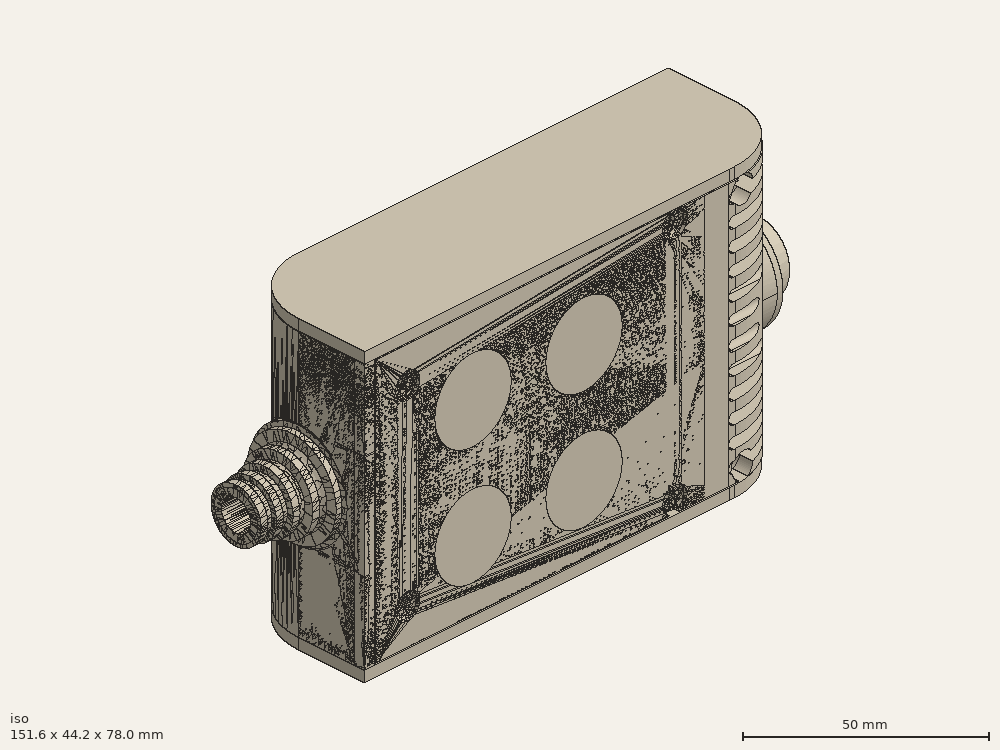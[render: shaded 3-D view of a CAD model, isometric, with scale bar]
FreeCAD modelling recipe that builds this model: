
FCSTD DOCUMENT  (FreeCAD 0.19R0.19.2)
Label: enclosure_178FCStd
License: All rights reserved
LicenseURL: http://en.wikipedia.org/wiki/All_rights_reserved
objects: Part::Revolution×152, Part::MultiFuse×146, Part::Feature×146, Sketcher::SketchObject×84, Part::Cut×70, Part::Cylinder×70, Part::Extrusion×67, Part::Fillet×58, Part::Box×36, App::MeasureDistance×4, PartDesign::Body×2, Image::ImagePlane×1
note: 831 computed .brp shape members not serialized (recipe doc carries the construction recipe); baked Part::Feature solids carry a one-line shape summary decoded from their .brp

FEATURE [Sketcher::SketchObject] Sketch  label="topSketch"
  FullyConstrained = true
  sketch-geometry (20):
    g0: LineSegment StartX=5.21097e-06 StartY=3 StartZ=0 EndX=5.21097e-06 EndY=19 EndZ=0
    g1: ArcOfCircle CenterX=19 CenterY=19 CenterZ=0 NormalX=0 NormalY=0 NormalZ=1 AngleXU=0 Radius=19 StartAngle=1.5708 EndAngle=3.14159
    g2: ArcOfCircle CenterX=19 CenterY=19 CenterZ=0 NormalX=0 NormalY=0 NormalZ=1 AngleXU=0 Radius=16 StartAngle=1.5708 EndAngle=3.14159
    g3: LineSegment StartX=114 StartY=35 StartZ=0 EndX=19 EndY=35 EndZ=0
    g4: LineSegment StartX=5.21097e-06 StartY=3 StartZ=0 EndX=5.21097e-06 EndY=0 EndZ=0
    g5: LineSegment StartX=3 StartY=0 StartZ=0 EndX=5.21097e-06 EndY=0 EndZ=0
    g6: LineSegment StartX=3 StartY=19 StartZ=0 EndX=3 EndY=0 EndZ=0
    g7: LineSegment StartX=19 StartY=38 StartZ=0 EndX=124 EndY=38 EndZ=0
    g8: Circle CenterX=119 CenterY=35 CenterZ=0 NormalX=0 NormalY=0 NormalZ=1 AngleXU=0 Radius=1
    g9: Circle CenterX=121 CenterY=35 CenterZ=0 NormalX=0 NormalY=0 NormalZ=1 AngleXU=0 Radius=1
    g10: Circle CenterX=121 CenterY=33 CenterZ=0 NormalX=0 NormalY=0 NormalZ=1 AngleXU=0 Radius=1
    g11: BSplineCurve PolesCount=3 KnotsCount=2 Degree=2 IsPeriodic=0
    g12: GeomPoint X=119 Y=35 Z=0
    g13: GeomPoint X=121 Y=33 Z=0
    g14: LineSegment StartX=119 StartY=35 StartZ=0 EndX=114 EndY=35 EndZ=0
    g15: ArcOfCircle CenterX=105 CenterY=19 CenterZ=0 NormalX=0 NormalY=0 NormalZ=1 AngleXU=0 Radius=19 StartAngle=5.7297 EndAngle=6.28319
    g16: ArcOfCircle CenterX=105 CenterY=19 CenterZ=0 NormalX=0 NormalY=0 NormalZ=1 AngleXU=0 Radius=16 StartAngle=5.60905 EndAngle=6.28319
    g17: LineSegment StartX=121 StartY=33 StartZ=0 EndX=121 EndY=19 EndZ=0
    g18: LineSegment StartX=124 StartY=38 StartZ=0 EndX=124 EndY=19 EndZ=0
    g19: LineSegment StartX=117.5 StartY=9.01251 StartZ=0 EndX=121.163 EndY=9.0125 EndZ=0
  constraints (46):
    c: Vertical(g0)
    c: Block(g0)
    c: Coincident(g1,g0)
    c: Block(g1)
    c: Coincident(g2,g1)
    c: Block(g2)
    c: Coincident(g3,g2)
    c: Horizontal(g3)
    c: Tangent(g3,g2)
    c: Coincident(g4,g0)
    c: Distance(g4) = 3
    c: Vertical(g4)
    c: Coincident(g5,g4)
    c: Horizontal(g5)
    c: Coincident(g6,g2)
    c: Coincident(g6,g5)
    c: Vertical(g6)
    c: Horizontal(g7)
    c: Distance(g7) = 105
    c: Coincident(g7,g1)
    c: Block(g3)
    c: Weight(g8) = 1
    c: Equal(g8,g9)
    c: Equal(g8,g10)
    c: InternalAlignment(g8,g11)
    c: InternalAlignment(g9,g11)
    c: InternalAlignment(g10,g11)
    c: InternalAlignment(g12,g11)
    c: InternalAlignment(g13,g11)
    c: Block(g11)
    c: Coincident(g14,g11)
    c: Coincident(g14,g3)
    c: Horizontal(g14)
    c: Block(g15)
    c: Coincident(g16,g15)
    c: Block(g16)
    c: Coincident(g17,g11)
    c: Coincident(g17,g16)
    c: Vertical(g17)
    c: Distance(g17) = 14
    c: Coincident(g18,g7)
    c: Coincident(g18,g15)
    c: Vertical(g18)
    c: Distance(g18) = 19
    c: Coincident(g19,g16)
    c: Coincident(g19,g15)
FEATURE [Sketcher::SketchObject] Sketch001  label="bottomSketch"
  FullyConstrained = true
  sketch-geometry (32):
    g0: LineSegment StartX=3.3 StartY=-6.03275e-07 StartZ=0 EndX=98 EndY=-6.03275e-07 EndZ=0
    g1: ArcOfCircle CenterX=98 CenterY=19 CenterZ=0 NormalX=0 NormalY=0 NormalZ=1 AngleXU=0 Radius=19 StartAngle=4.71239 EndAngle=5.71103
    g2: LineSegment StartX=6.3 StartY=8 StartZ=0 EndX=3.3 EndY=8 EndZ=0
    g3: LineSegment StartX=3.3 StartY=8 StartZ=0 EndX=3.3 EndY=-6.03275e-07 EndZ=0
    g4: ArcOfCircle CenterX=8.3 CenterY=5 CenterZ=0 NormalX=0 NormalY=0 NormalZ=1 AngleXU=0 Radius=2 StartAngle=3.14159 EndAngle=4.71239
    g5: LineSegment StartX=6.3 StartY=8 StartZ=0 EndX=6.3 EndY=5 EndZ=0
    g6: ArcOfCircle CenterX=98 CenterY=19 CenterZ=0 NormalX=0 NormalY=0 NormalZ=1 AngleXU=0 Radius=12.7 StartAngle=4.71239 EndAngle=6.28319
    g7: LineSegment StartX=94.7 StartY=3 StartZ=0 EndX=8.3 EndY=3 EndZ=0
    g8-g12: Circle x5 (B-spline internal-alignment scaffolding for g13; pole/knot coordinates omitted)
    g13: BSplineCurve PolesCount=5 KnotsCount=3 Degree=3 IsPeriodic=0
    g14: GeomPoint X=98 Y=6.3 Z=0
    g15: GeomPoint X=96.3938 Y=4.71946 Z=0
    g16: GeomPoint X=94.7 Y=3 Z=0
    g17-g23: Circle x7 (B-spline internal-alignment scaffolding for g24; pole/knot coordinates omitted)
    g24: BSplineCurve PolesCount=7 KnotsCount=5 Degree=3 IsPeriodic=0
    g25-g29: GeomPoint x5 (B-spline internal-alignment scaffolding for g24; pole/knot coordinates omitted)
    g30: ArcOfCircle CenterX=98 CenterY=19 CenterZ=0 NormalX=0 NormalY=0 NormalZ=1 AngleXU=0 Radius=15.7 StartAngle=5.81226 EndAngle=6.28319
    g31: LineSegment StartX=110.7 StartY=19 StartZ=0 EndX=113.7 EndY=19 EndZ=0
  constraints (41):
    c: Horizontal(g0)
    c: Coincident(g1,g0)
    c: Block(g1)
    c: Horizontal(g2)
    c: Distance(g2) = 3
    c: Coincident(g3,g2)
    c: Vertical(g3)
    c: Coincident(g3,g0)
    c: Block(g4)
    c: Block(g2)
    c: Coincident(g5,g2)
    c: Coincident(g5,g4)
    c: Vertical(g5)
    c: Coincident(g6,g1)
    c: Block(g6)
    c: Coincident(g7,g4)
    c: Horizontal(g7)
    c: Block(g0)
    c: Block(g7)
    c: Block(g3)
    c: Coincident(g13,g6)
    c: Weight(g8) = 1
    c: Equal(g8, g9-g12) x4
    c: Coincident(g13,g7)
    c: InternalAlignment(g8-g12 -> g13) x5
    c: InternalAlignment(g14,g13)
    c: InternalAlignment(g15,g13)
    c: InternalAlignment(g16,g13)
    c: Block(g13)
    c: Weight(g17) = 1
    c: Equal(g17, g18-g23) x6
    c: Coincident(g24,g1)
    c: InternalAlignment(g17-g23 -> g24) x7
    c: InternalAlignment(g25-g29 -> g24) x5
    c: Block(g24)
    c: Coincident(g30,g24)
    c: Coincident(g31,g6)
    c: Coincident(g31,g30)
    c: Horizontal(g31)
    c: Block(g31)
    c: Block(g30)
FEATURE [Part::Extrusion] Extrude  label="top"
  Base = -> Sketch
  Dir = (0,0,1)
  DirMode = 2
  FaceMakerClass = Part::FaceMakerBullseye
  LengthFwd = 72
  LengthRev = 0
  Solid = true
  Symmetric = false
FEATURE [Part::Extrusion] Extrude001  label="bottom"
  Base = -> Sketch001
  Dir = (0,0,1)
  DirMode = 2
  FaceMakerClass = Part::FaceMakerBullseye
  LengthFwd = 71.4
  LengthRev = 0
  Placement = pos=(0,0,0.3) rot=(0,0,1;0rad)
  Solid = true
  Symmetric = false
FEATURE [Sketcher::SketchObject] Sketch002  label="topSketch001"
  FullyConstrained = true
  sketch-geometry (8):
    g0: ArcOfCircle CenterX=19 CenterY=19.0975 CenterZ=0 NormalX=0 NormalY=0 NormalZ=1 AngleXU=0 Radius=18.9025 StartAngle=1.5708 EndAngle=3.14674
    g1: LineSegment StartX=0.0977805 StartY=19.0003 StartZ=0 EndX=0.0977805 EndY=0.000251602 EndZ=0
    g2: LineSegment StartX=19 StartY=38 StartZ=0 EndX=124 EndY=38 EndZ=0
    g3: LineSegment StartX=0.0977805 StartY=0.000251602 StartZ=0 EndX=105.098 EndY=0.000251602 EndZ=0
    g4: LineSegment StartX=124 StartY=38 StartZ=0 EndX=125.616 EndY=38 EndZ=0
    g5: LineSegment StartX=105.098 StartY=0.000251602 StartZ=0 EndX=106.713 EndY=0.000251602 EndZ=0
    g6: ArcOfCircle CenterX=106.616 CenterY=19 CenterZ=0 NormalX=0 NormalY=0 NormalZ=1 AngleXU=0 Radius=19 StartAngle=4.71754 EndAngle=6.28319
    g7: LineSegment StartX=125.616 StartY=38 StartZ=0 EndX=125.616 EndY=19 EndZ=0
  constraints (21):
    c: Block(g0)
    c: Coincident(g1,g0)
    c: Vertical(g1)
    c: Horizontal(g2)
    c: Distance(g2) = 105
    c: Coincident(g2,g0)
    c: Distance(g1) = 19
    c: Coincident(g3,g1)
    c: Horizontal(g3)
    c: Distance(g3) = 105
    c: Coincident(g4,g2)
    c: Horizontal(g4)
    c: Distance(g4) = 1.61553
    c: Horizontal(g5)
    c: Equal(g4,g5) = 1.61553
    c: Coincident(g5,g3)
    c: Block(g6)
    c: Coincident(g6,g5)
    c: Coincident(g7,g4)
    c: Coincident(g7,g6)
    c: Vertical(g7)
FEATURE [Part::Extrusion] Extrude002  label="sideA"
  Base = -> Sketch002
  Dir = (0,0,1)
  DirMode = 2
  FaceMakerClass = Part::FaceMakerBullseye
  LengthFwd = 3
  LengthRev = 0
  Placement = pos=(0,0,-3) rot=(0,0,1;0rad)
  Solid = true
  Symmetric = false
FEATURE [Sketcher::SketchObject] Sketch003  label="topSketch002"
  FullyConstrained = true
  sketch-geometry (6):
    g0: LineSegment StartX=19 StartY=38 StartZ=0 EndX=117 EndY=38 EndZ=0
    g1: ArcOfCircle CenterX=19 CenterY=19 CenterZ=0 NormalX=0 NormalY=0 NormalZ=1 AngleXU=0 Radius=19 StartAngle=1.5708 EndAngle=3.14159
    g2: LineSegment StartX=117 StartY=38 StartZ=0 EndX=117 EndY=19 EndZ=0
    g3: LineSegment StartX=98 StartY=1.0161e-12 StartZ=0 EndX=5.22862e-06 EndY=1.0161e-12 EndZ=0
    g4: LineSegment StartX=5.22862e-06 StartY=19 StartZ=0 EndX=5.22862e-06 EndY=1.0161e-12 EndZ=0
    g5: ArcOfCircle CenterX=98 CenterY=19 CenterZ=0 NormalX=0 NormalY=0 NormalZ=1 AngleXU=0 Radius=19 StartAngle=4.71239 EndAngle=6.28319
  constraints (16):
    c: Horizontal(g0)
    c: Distance(g0) = 98
    c: Coincident(g1,g0)
    c: Block(g1)
    c: Coincident(g2,g0)
    c: Vertical(g2)
    c: Distance(g2) = 19
    c: Horizontal(g3)
    c: Coincident(g4,g1)
    c: Vertical(g4)
    c: Coincident(g3,g4)
    c: Block(g3)
    c: Coincident(g5,g2)
    c: Coincident(g5,g3)
    c: Block(g0)
    c: Block(g5)
FEATURE [Sketcher::SketchObject] Sketch004
  FullyConstrained = true
  MapMode = 3
  Placement = pos=(0,0,0) rot=(1,0,0;1.5708rad)
  Support = -> [Extrude]
  sketch-geometry (8):
    g0: Circle CenterX=80.351 CenterY=-67.6202 CenterZ=0 NormalX=0 NormalY=0 NormalZ=1 AngleXU=0 Radius=2
    g1: Circle CenterX=80.351 CenterY=-67.6202 CenterZ=0 NormalX=0 NormalY=0 NormalZ=1 AngleXU=0 Radius=3
    g2: Circle CenterX=80.351 CenterY=-4.92017 CenterZ=0 NormalX=0 NormalY=0 NormalZ=1 AngleXU=0 Radius=2
    g3: Circle CenterX=80.351 CenterY=-4.92017 CenterZ=0 NormalX=0 NormalY=0 NormalZ=1 AngleXU=0 Radius=3
    g4: Circle CenterX=23.851 CenterY=-4.92017 CenterZ=0 NormalX=0 NormalY=0 NormalZ=1 AngleXU=0 Radius=2
    g5: Circle CenterX=23.851 CenterY=-4.92017 CenterZ=0 NormalX=0 NormalY=0 NormalZ=1 AngleXU=0 Radius=3
    g6: Circle CenterX=23.851 CenterY=-67.6202 CenterZ=0 NormalX=0 NormalY=0 NormalZ=1 AngleXU=0 Radius=2
    g7: Circle CenterX=23.851 CenterY=-67.6202 CenterZ=0 NormalX=0 NormalY=0 NormalZ=1 AngleXU=0 Radius=3
  constraints (8):
    c: Block(g3)
    c: Block(g2)
    c: Block(g1)
    c: Block(g0)
    c: Block(g6)
    c: Block(g7)
    c: Block(g4)
    c: Block(g5)
FEATURE [Part::Extrusion] Extrude004
  Base = -> Sketch004
  Dir = (0,-1,2e-16)
  DirMode = 2
  FaceMakerClass = Part::FaceMakerBullseye
  LengthFwd = 6
  LengthRev = 0
  Placement = pos=(0,9,0) rot=(0,0,1;0rad)
  Solid = true
  Symmetric = false
FEATURE [Sketcher::SketchObject] Sketch005
  FullyConstrained = true
  MapMode = 3
  Placement = pos=(0,0,0) rot=(1,0,0;1.5708rad)
  Support = -> [Extrude]
  sketch-geometry (8):
    g0: Circle CenterX=80.351 CenterY=-67.6202 CenterZ=0 NormalX=0 NormalY=0 NormalZ=1 AngleXU=0 Radius=3
    g1: Circle CenterX=80.351 CenterY=-4.92017 CenterZ=0 NormalX=0 NormalY=0 NormalZ=1 AngleXU=0 Radius=3
    g2: Circle CenterX=23.851 CenterY=-4.92017 CenterZ=0 NormalX=0 NormalY=0 NormalZ=1 AngleXU=0 Radius=3
    g3: Circle CenterX=23.851 CenterY=-67.6202 CenterZ=0 NormalX=0 NormalY=0 NormalZ=1 AngleXU=0 Radius=3
    g4: Circle CenterX=23.851 CenterY=-67.6202 CenterZ=0 NormalX=0 NormalY=0 NormalZ=1 AngleXU=0 Radius=5
    g5: Circle CenterX=80.351 CenterY=-67.6202 CenterZ=0 NormalX=0 NormalY=0 NormalZ=1 AngleXU=0 Radius=5
    g6: Circle CenterX=23.851 CenterY=-4.92017 CenterZ=0 NormalX=0 NormalY=0 NormalZ=1 AngleXU=0 Radius=5
    g7: Circle CenterX=80.351 CenterY=-4.92017 CenterZ=0 NormalX=0 NormalY=0 NormalZ=1 AngleXU=0 Radius=5
  constraints (8):
    c: Block(g1)
    c: Block(g0)
    c: Block(g3)
    c: Block(g2)
    c: Block(g5)
    c: Block(g4)
    c: Block(g6)
    c: Block(g7)
FEATURE [Part::Extrusion] Extrude005
  Base = -> Sketch005
  Dir = (0,-1,2e-16)
  DirMode = 2
  FaceMakerClass = Part::FaceMakerBullseye
  LengthFwd = 2
  LengthRev = 0
  Solid = true
  Symmetric = false
FEATURE [Sketcher::SketchObject] Sketch006
  FullyConstrained = true
  MapMode = 3
  Placement = pos=(0,0,0) rot=(1,0,0;1.5708rad)
  sketch-geometry (8):
    g0: Circle CenterX=80.351 CenterY=-67.6202 CenterZ=0 NormalX=0 NormalY=0 NormalZ=1 AngleXU=0 Radius=3
    g1: Circle CenterX=80.351 CenterY=-4.92017 CenterZ=0 NormalX=0 NormalY=0 NormalZ=1 AngleXU=0 Radius=3
    g2: Circle CenterX=23.851 CenterY=-4.92017 CenterZ=0 NormalX=0 NormalY=0 NormalZ=1 AngleXU=0 Radius=3
    g3: Circle CenterX=23.851 CenterY=-67.6202 CenterZ=0 NormalX=0 NormalY=0 NormalZ=1 AngleXU=0 Radius=3
    g4: Circle CenterX=23.851 CenterY=-67.6202 CenterZ=0 NormalX=0 NormalY=0 NormalZ=1 AngleXU=0 Radius=5
    g5: Circle CenterX=80.351 CenterY=-67.6202 CenterZ=0 NormalX=0 NormalY=0 NormalZ=1 AngleXU=0 Radius=5
    g6: Circle CenterX=23.851 CenterY=-4.92017 CenterZ=0 NormalX=0 NormalY=0 NormalZ=1 AngleXU=0 Radius=5
    g7: Circle CenterX=80.351 CenterY=-4.92017 CenterZ=0 NormalX=0 NormalY=0 NormalZ=1 AngleXU=0 Radius=5
  constraints (8):
    c: Block(g1)
    c: Block(g0)
    c: Block(g3)
    c: Block(g2)
    c: Block(g5)
    c: Block(g4)
    c: Block(g6)
    c: Block(g7)
FEATURE [Part::Extrusion] Extrude007
  Base = -> Sketch006
  Dir = (0,-1,2e-16)
  DirMode = 2
  FaceMakerClass = Part::FaceMakerBullseye
  LengthFwd = 2
  LengthRev = 0
  Solid = true
  Symmetric = false
FEATURE [Part::Fillet] Fillet
  Base = -> Extrude007
  Edges = 4 edges r=1.99: [Edge6,Edge12,Edge18,Edge24]
FEATURE [Part::Cut] Cut
  Base = -> Extrude005
  Placement = pos=(0,5,0) rot=(0,0,1;0rad)
  Tool = -> Fillet
FEATURE [Part::MultiFuse] Fusion  label="pCBScrews"
  Placement = pos=(-2.5,0,72.3) rot=(0,0,1;0rad)
  Shapes = -> [Extrude004,Cut]
FEATURE [App::MeasureDistance] Distance  label="Distance: 0.69 mm"
  Distance = 0.685967
  P1 = (24.0138,2.9647,0.3)
  P2 = (23.8901,3,-0.373787)
FEATURE [App::MeasureDistance] Distance001  label="Distance: 0.53 mm"
  Distance = 0.533607
  P1 = (80.2939,3,72.2334)
  P2 = (80.281,2.99661,71.7)
FEATURE [Part::Fillet] Fillet001
  Base = -> Extrude001
  Edges = 1 edges r=2.4: [Edge17]
FEATURE [Part::Fillet] Fillet002  label="bottom001"
  Base = -> Fillet001
  Edges = 1 edges r=2.4: [Edge36]
FEATURE [Part::Fillet] Fillet003  label="top001"
  Base = -> Extrude
  Edges = 1 edges r=2: [Edge1]
FEATURE [Sketcher::SketchObject] Sketch007
  FullyConstrained = true
  sketch-geometry (16):
    g0: LineSegment StartX=4 StartY=0 StartZ=0 EndX=4 EndY=2.4 EndZ=0
    g1: LineSegment StartX=4 StartY=2.4 StartZ=0 EndX=7 EndY=2.4 EndZ=0
    g2: LineSegment StartX=4 StartY=0 StartZ=0 EndX=5.7 EndY=0 EndZ=0
    g3: LineSegment StartX=5.7 StartY=0 StartZ=0 EndX=5.7 EndY=-5.6 EndZ=0
    g4-g8: Circle x5 (B-spline internal-alignment scaffolding for g9; pole/knot coordinates omitted)
    g9: BSplineCurve PolesCount=5 KnotsCount=3 Degree=3 IsPeriodic=0
    g10: GeomPoint X=7 Y=2.4 Z=0
    g11: GeomPoint X=10.4582 Y=-1.55472 Z=0
    g12: GeomPoint X=14 Y=-5.6 Z=0
    g13: LineSegment StartX=14 StartY=-5.6 StartZ=0 EndX=14 EndY=-14.1 EndZ=0
    g14: LineSegment StartX=14 StartY=-14.1 StartZ=0 EndX=6.5 EndY=-14.1 EndZ=0
    g15: LineSegment StartX=5.7 StartY=-5.6 StartZ=0 EndX=6.5 EndY=-14.1 EndZ=0
  constraints (28):
    c: Distance(g0) = 2.4
    c: Vertical(g0)
    c: Block(g0)
    c: Coincident(g1,g0)
    c: Horizontal(g1)
    c: Distance(g1) = 3
    c: Coincident(g2,g0)
    c: Horizontal(g2)
    c: Distance(g2) = 1.7
    c: Coincident(g3,g2)
    c: Vertical(g3)
    c: Distance(g3) = 5.6
    c: Coincident(g9,g1)
    c: Weight(g4) = 1
    c: Equal(g4, g5-g8) x4
    c: InternalAlignment(g4-g8 -> g9) x5
    c: InternalAlignment(g10,g9)
    c: InternalAlignment(g11,g9)
    c: InternalAlignment(g12,g9)
    c: Block(g9)
    c: Coincident(g13,g9)
    c: Vertical(g13)
    c: Distance(g13) = 8.5
    c: Coincident(g14,g13)
    c: Horizontal(g14)
    c: Distance(g14) = 7.5
    c: Coincident(g15,g3)
    c: Coincident(g15,g14)
FEATURE [Part::Feature] Face
  shape: bbox 10 x 16.5 x 2e-07 mm, 1 faces, 0 solids (baked)
FEATURE [Part::Revolution] Revolve  label="plugHousing"
  Angle = 360
  Axis = (0,1,0)
  Base = (0,0,0)
  FaceMakerClass = Part::FaceMakerBullseye
  Placement = pos=(0,0,36.15) rot=(0,0,1;0rad)
  Solid = false
  Source = -> Face
  Symmetric = false
FEATURE [Part::Feature] Face001
  shape: bbox 10 x 16.5 x 2e-07 mm, 1 faces, 0 solids (baked)
FEATURE [Part::Revolution] Revolve001  label="plugHousing001"
  Angle = 360
  Axis = (0,1,0)
  Base = (0,0,0)
  FaceMakerClass = Part::FaceMakerBullseye
  Placement = pos=(0,0,36.15) rot=(0,0,1;0rad)
  Solid = false
  Source = -> Face001
  Symmetric = false
FEATURE [Part::MultiFuse] Fusion001  label="plugHousing002"
  Placement = pos=(0,0,0) rot=(0,0,1;1.5708rad)
  Shapes = -> [Revolve001,Revolve]
FEATURE [Part::Feature] Face002
  shape: bbox 10 x 16.5 x 2e-07 mm, 1 faces, 0 solids (baked)
FEATURE [Part::Revolution] Revolve003  label="plugHousing005"
  Angle = 360
  Axis = (0,1,0)
  Base = (0,0,0)
  FaceMakerClass = Part::FaceMakerBullseye
  Placement = pos=(0,0,36.15) rot=(0,0,1;0rad)
  Solid = false
  Source = -> Face002
  Symmetric = false
FEATURE [Part::Feature] Face003
  shape: bbox 10 x 16.5 x 2e-07 mm, 1 faces, 0 solids (baked)
FEATURE [Part::Revolution] Revolve002  label="plugHousing003"
  Angle = 360
  Axis = (0,1,0)
  Base = (0,0,0)
  FaceMakerClass = Part::FaceMakerBullseye
  Placement = pos=(0,0,36.15) rot=(0,0,1;0rad)
  Solid = false
  Source = -> Face003
  Symmetric = false
FEATURE [Part::MultiFuse] Fusion002  label="plugHousing004"
  Placement = pos=(0,0,0) rot=(0,0,1;1.5708rad)
  Shapes = -> [Revolve002,Revolve003]
FEATURE [Part::MultiFuse] Fusion003  label="plugHousing006"
  Placement = pos=(0,19,0) rot=(0,0,1;3.14159rad)
  Shapes = -> [Fusion002,Fusion001]
FEATURE [Part::Feature] Face004
  shape: bbox 10 x 16.5 x 2e-07 mm, 1 faces, 0 solids (baked)
FEATURE [Part::Revolution] Revolve006  label="plugHousing010"
  Angle = 360
  Axis = (0,1,0)
  Base = (0,0,0)
  FaceMakerClass = Part::FaceMakerBullseye
  Placement = pos=(0,0,36.15) rot=(0,0,1;0rad)
  Solid = false
  Source = -> Face004
  Symmetric = false
FEATURE [Part::Feature] Face005
  shape: bbox 10 x 16.5 x 2e-07 mm, 1 faces, 0 solids (baked)
FEATURE [Part::Revolution] Revolve007  label="plugHousing011"
  Angle = 360
  Axis = (0,1,0)
  Base = (0,0,0)
  FaceMakerClass = Part::FaceMakerBullseye
  Placement = pos=(0,0,36.15) rot=(0,0,1;0rad)
  Solid = false
  Source = -> Face005
  Symmetric = false
FEATURE [Part::Feature] Face006
  shape: bbox 10 x 16.5 x 2e-07 mm, 1 faces, 0 solids (baked)
FEATURE [Part::Revolution] Revolve004  label="plugHousing007"
  Angle = 360
  Axis = (0,1,0)
  Base = (0,0,0)
  FaceMakerClass = Part::FaceMakerBullseye
  Placement = pos=(0,0,36.15) rot=(0,0,1;0rad)
  Solid = false
  Source = -> Face006
  Symmetric = false
FEATURE [Part::MultiFuse] Fusion004  label="plugHousing009"
  Placement = pos=(0,0,0) rot=(0,0,1;1.5708rad)
  Shapes = -> [Revolve004,Revolve007]
FEATURE [Part::Feature] Face007
  shape: bbox 10 x 16.5 x 2e-07 mm, 1 faces, 0 solids (baked)
FEATURE [Part::Revolution] Revolve005  label="plugHousing008"
  Angle = 360
  Axis = (0,1,0)
  Base = (0,0,0)
  FaceMakerClass = Part::FaceMakerBullseye
  Placement = pos=(0,0,36.15) rot=(0,0,1;0rad)
  Solid = false
  Source = -> Face007
  Symmetric = false
FEATURE [Part::MultiFuse] Fusion005  label="plugHousing012"
  Placement = pos=(0,0,0) rot=(0,0,1;1.5708rad)
  Shapes = -> [Revolve006,Revolve005]
FEATURE [Part::MultiFuse] Fusion006  label="plugHousing013"
  Placement = pos=(0,19,0) rot=(0,0,1;3.14159rad)
  Shapes = -> [Fusion005,Fusion004]
FEATURE [Part::MultiFuse] Fusion007  label="plugHousing014"
  Placement = pos=(122.621,0,-0.15) rot=(0,0,1;0rad)
  Shapes = -> [Fusion003,Fusion006]
FEATURE [Part::Cylinder] Cylinder002
  Angle = 360
  AttacherType = Attacher::AttachEngine3D
  Height = 20
  Placement = pos=(0,0,36.15) rot=(0,0,1;0rad)
  Radius = 4
FEATURE [Part::Cylinder] Cylinder003
  Angle = 360
  AttacherType = Attacher::AttachEngine3D
  Height = 10
  Placement = pos=(0,0,36.15) rot=(0,0,1;0rad)
  Radius = 4
FEATURE [Part::MultiFuse] Fusion009  label="removeToCreateHoleForPlugHousing"
  Placement = pos=(70,19,36.15) rot=(0,1,0;1.5708rad)
  Shapes = -> [Cylinder002,Cylinder003]
FEATURE [Part::Cylinder] Cylinder004
  Angle = 360
  AttacherType = Attacher::AttachEngine3D
  Height = 20
  Placement = pos=(0,0,36.15) rot=(0,0,1;0rad)
  Radius = 4
FEATURE [Part::Cylinder] Cylinder005
  Angle = 360
  AttacherType = Attacher::AttachEngine3D
  Height = 10
  Placement = pos=(0,0,36.15) rot=(0,0,1;0rad)
  Radius = 4
FEATURE [Part::MultiFuse] Fusion010  label="removeToCreateHoleForPlugHousing001"
  Placement = pos=(70,19,36.15) rot=(0,1,0;1.5708rad)
  Shapes = -> [Cylinder004,Cylinder005]
FEATURE [Part::Cut] Cut001
  Base = -> Fillet003
  Tool = -> Fusion010
FEATURE [Part::Cut] Cut002  label="Bottom"
  Base = -> Fillet002
  Tool = -> Fusion009
FEATURE [Part::Feature] Face008
  shape: bbox 10 x 16.5 x 2e-07 mm, 1 faces, 0 solids (baked)
FEATURE [Part::Revolution] Revolve011  label="plugHousing021"
  Angle = 360
  Axis = (0,1,0)
  Base = (0,0,0)
  FaceMakerClass = Part::FaceMakerBullseye
  Placement = pos=(0,0,36.15) rot=(0,0,1;0rad)
  Solid = false
  Source = -> Face008
  Symmetric = false
FEATURE [Part::Feature] Face009
  shape: bbox 10 x 16.5 x 2e-07 mm, 1 faces, 0 solids (baked)
FEATURE [Part::Revolution] Revolve012  label="plugHousing022"
  Angle = 360
  Axis = (0,1,0)
  Base = (0,0,0)
  FaceMakerClass = Part::FaceMakerBullseye
  Placement = pos=(0,0,36.15) rot=(0,0,1;0rad)
  Solid = false
  Source = -> Face009
  Symmetric = false
FEATURE [Part::Feature] Face010 .. Face013  x4 (patterned run collapsed; names and placements below)
  shape: bbox 10 x 16.5 x 2e-07 mm, 1 faces, 0 solids (baked)
FEATURE [Part::Revolution] Revolve015  label="plugHousing027"
  Angle = 360
  Axis = (0,1,0)
  Base = (0,0,0)
  FaceMakerClass = Part::FaceMakerBullseye
  Placement = pos=(0,0,36.15) rot=(0,0,1;0rad)
  Solid = false
  Source = -> Face013
  Symmetric = false
FEATURE [Part::Feature] Face014
  shape: bbox 10 x 16.5 x 2e-07 mm, 1 faces, 0 solids (baked)
FEATURE [Part::Feature] Face015
  shape: bbox 10 x 16.5 x 2e-07 mm, 1 faces, 0 solids (baked)
FEATURE [Part::Feature] Face016
  shape: bbox 10 x 16.5 x 2e-07 mm, 1 faces, 0 solids (baked)
FEATURE [Part::Revolution] Revolve019  label="plugHousing033"
  Angle = 360
  Axis = (0,1,0)
  Base = (0,0,0)
  FaceMakerClass = Part::FaceMakerBullseye
  Placement = pos=(0,0,36.15) rot=(0,0,1;0rad)
  Solid = false
  Source = -> Face016
  Symmetric = false
FEATURE [Part::Feature] Face017
  shape: bbox 10 x 16.5 x 2e-07 mm, 1 faces, 0 solids (baked)
FEATURE [Part::Revolution] Revolve020  label="plugHousing034"
  Angle = 360
  Axis = (0,1,0)
  Base = (0,0,0)
  FaceMakerClass = Part::FaceMakerBullseye
  Placement = pos=(0,0,36.15) rot=(0,0,1;0rad)
  Solid = false
  Source = -> Face017
  Symmetric = false
FEATURE [Part::Feature] Face018
  shape: bbox 10 x 16.5 x 2e-07 mm, 1 faces, 0 solids (baked)
FEATURE [Part::Revolution] Revolve016  label="plugHousing030"
  Angle = 360
  Axis = (0,1,0)
  Base = (0,0,0)
  FaceMakerClass = Part::FaceMakerBullseye
  Placement = pos=(0,0,36.15) rot=(0,0,1;0rad)
  Solid = false
  Source = -> Face018
  Symmetric = false
FEATURE [Part::MultiFuse] Fusion020  label="plugHousing038"
  Placement = pos=(0,0,0) rot=(0,0,1;1.5708rad)
  Shapes = -> [Revolve016,Revolve020]
FEATURE [Part::Feature] Face019
  shape: bbox 10 x 16.5 x 2e-07 mm, 1 faces, 0 solids (baked)
FEATURE [Part::Feature] Face020
  shape: bbox 10 x 16.5 x 2e-07 mm, 1 faces, 0 solids (baked)
FEATURE [Part::Revolution] Revolve017  label="plugHousing031"
  Angle = 360
  Axis = (0,1,0)
  Base = (0,0,0)
  FaceMakerClass = Part::FaceMakerBullseye
  Placement = pos=(0,0,36.15) rot=(0,0,1;0rad)
  Solid = false
  Source = -> Face020
  Symmetric = false
FEATURE [Part::MultiFuse] Fusion021  label="plugHousing039"
  Placement = pos=(0,0,0) rot=(0,0,1;1.5708rad)
  Shapes = -> [Revolve019,Revolve017]
FEATURE [Part::MultiFuse] Fusion023  label="plugHousing041"
  Placement = pos=(0,19,0) rot=(0,0,1;3.14159rad)
  Shapes = -> [Fusion021,Fusion020]
FEATURE [Part::Revolution] Revolve022  label="plugHousing043"
  Angle = 360
  Axis = (0,1,0)
  Base = (0,0,0)
  FaceMakerClass = Part::FaceMakerBullseye
  Placement = pos=(0,0,36.15) rot=(0,0,1;0rad)
  Solid = false
  Source = -> Face019
  Symmetric = false
FEATURE [Part::Feature] Face021
  shape: bbox 10 x 16.5 x 2e-07 mm, 1 faces, 0 solids (baked)
FEATURE [Part::Revolution] Revolve023  label="plugHousing044"
  Angle = 360
  Axis = (0,1,0)
  Base = (0,0,0)
  FaceMakerClass = Part::FaceMakerBullseye
  Placement = pos=(0,0,36.15) rot=(0,0,1;0rad)
  Solid = false
  Source = -> Face021
  Symmetric = false
FEATURE [Part::Feature] Face022
  shape: bbox 10 x 16.5 x 2e-07 mm, 1 faces, 0 solids (baked)
FEATURE [Part::Revolution] Revolve018  label="plugHousing032"
  Angle = 360
  Axis = (0,1,0)
  Base = (0,0,0)
  FaceMakerClass = Part::FaceMakerBullseye
  Placement = pos=(0,0,36.15) rot=(0,0,1;0rad)
  Solid = false
  Source = -> Face022
  Symmetric = false
FEATURE [Part::MultiFuse] Fusion022  label="plugHousing040"
  Placement = pos=(0,0,0) rot=(0,0,1;1.5708rad)
  Shapes = -> [Revolve018,Revolve023]
FEATURE [Part::Feature] Face023
  shape: bbox 10 x 16.5 x 2e-07 mm, 1 faces, 0 solids (baked)
FEATURE [Part::Revolution] Revolve021  label="plugHousing035"
  Angle = 360
  Axis = (0,1,0)
  Base = (0,0,0)
  FaceMakerClass = Part::FaceMakerBullseye
  Placement = pos=(0,0,36.15) rot=(0,0,1;0rad)
  Solid = false
  Source = -> Face023
  Symmetric = false
FEATURE [Part::MultiFuse] Fusion018  label="plugHousing036"
  Placement = pos=(0,0,0) rot=(0,0,1;1.5708rad)
  Shapes = -> [Revolve022,Revolve021]
FEATURE [Part::MultiFuse] Fusion019  label="plugHousing037"
  Placement = pos=(0,19,0) rot=(0,0,1;3.14159rad)
  Shapes = -> [Fusion018,Fusion022]
FEATURE [Part::MultiFuse] Fusion024  label="plugHousing042"
  Placement = pos=(122.621,0,-0.15) rot=(0,0,1;0rad)
  Shapes = -> [Fusion023,Fusion019]
FEATURE [Part::Cylinder] Cylinder006
  Angle = 360
  AttacherType = Attacher::AttachEngine3D
  Height = 20
  Placement = pos=(0,0,36.15) rot=(0,0,1;0rad)
  Radius = 14.3
FEATURE [Part::Cylinder] Cylinder007
  Angle = 360
  AttacherType = Attacher::AttachEngine3D
  Height = 10
  Placement = pos=(0,0,36.15) rot=(0,0,1;0rad)
  Radius = 4
FEATURE [Part::MultiFuse] Fusion026  label="removeToCreteHoleForPlugHousing"
  Placement = pos=(70,19,36) rot=(0,1,0;1.5708rad)
  Shapes = -> [Cylinder006,Cylinder007]
FEATURE [Part::Box] Box001  label="Cube001"
  AttacherType = Attacher::AttachEngine3D
  Height = 28
  Length = 3
  Placement = pos=(110.7,19,22) rot=(0,0,1;0rad)
  Width = 15.7
FEATURE [Part::Cut] Cut003  label="top002"
  Base = -> Cut001
  Tool = -> Fusion007
FEATURE [Part::Revolution] Revolve008  label="plugHousing015"
  Angle = 360
  Axis = (0,1,0)
  Base = (0,0,0)
  FaceMakerClass = Part::FaceMakerBullseye
  Placement = pos=(0,0,36.15) rot=(0,0,1;0rad)
  Solid = false
  Source = -> Face010
  Symmetric = false
FEATURE [Part::MultiFuse] Fusion013  label="plugHousing020"
  Placement = pos=(0,0,0) rot=(0,0,1;1.5708rad)
  Shapes = -> [Revolve008,Revolve012]
FEATURE [Part::Cut] Cut004  label="top003"
  Base = -> Cut003
  Placement = pos=(1,0,0) rot=(0,0,1;0rad)
  Tool = -> Fusion026
FEATURE [Part::Cylinder] Cylinder008
  Angle = 360
  AttacherType = Attacher::AttachEngine3D
  Height = 20
  Placement = pos=(0,0,36.15) rot=(0,0,1;0rad)
  Radius = 10.3
FEATURE [Part::Cylinder] Cylinder009
  Angle = 360
  AttacherType = Attacher::AttachEngine3D
  Height = 10
  Placement = pos=(0,0,36.15) rot=(0,0,1;0rad)
  Radius = 4
FEATURE [Part::MultiFuse] Fusion027  label="removeToCreteHoleForPlugHousing001"
  Placement = pos=(70,19,36) rot=(0,1,0;1.5708rad)
  Shapes = -> [Cylinder008,Cylinder009]
FEATURE [Part::Cut] Cut005  label="plugHousingTab"
  Base = -> Box001
  Tool = -> Fusion027
FEATURE [Part::MultiFuse] Fusion028  label="plugHousing045"
  Shapes = -> [Fusion024,Cut005]
FEATURE [Part::Box] Box002  label="Cube002"
  AttacherType = Attacher::AttachEngine3D
  Height = 28.8
  Length = 3
  Placement = pos=(107.3,28,21.6) rot=(0,0,1;0rad)
  Width = 7
FEATURE [Part::Box] Box003  label="Cube003"
  AttacherType = Attacher::AttachEngine3D
  Height = 3
  Length = 6.4
  Placement = pos=(107.3,28,18.6) rot=(0,0,1;0rad)
  Width = 7
FEATURE [Part::Box] Box004  label="Cube004"
  AttacherType = Attacher::AttachEngine3D
  Height = 3
  Length = 6.4
  Placement = pos=(107.3,28,50.4) rot=(0,0,1;0rad)
  Width = 7
FEATURE [Part::MultiFuse] Fusion029  label="plugHousingBracketHolder"
  Shapes = -> [Box004,Box002,Box003]
FEATURE [Part::Cylinder] Cylinder010
  Angle = 360
  AttacherType = Attacher::AttachEngine3D
  Height = 20
  Placement = pos=(0,0,36.15) rot=(0,0,1;0rad)
  Radius = 14.3
FEATURE [Part::Cylinder] Cylinder011
  Angle = 360
  AttacherType = Attacher::AttachEngine3D
  Height = 10
  Placement = pos=(0,0,36.15) rot=(0,0,1;0rad)
  Radius = 4
FEATURE [Part::MultiFuse] Fusion030  label="removeToCreteHoleForPlugHousing002"
  Placement = pos=(70,19,36) rot=(0,1,0;1.5708rad)
  Shapes = -> [Cylinder010,Cylinder011]
FEATURE [Part::Cut] Cut006  label="plugHousingBracketHolder001"
  Base = -> Fusion029
  Tool = -> Fusion030
FEATURE [Part::Cylinder] Cylinder012
  Angle = 360
  AttacherType = Attacher::AttachEngine3D
  Height = 20
  Placement = pos=(0,0,36.15) rot=(0,0,1;0rad)
  Radius = 7
FEATURE [Part::Cylinder] Cylinder013
  Angle = 360
  AttacherType = Attacher::AttachEngine3D
  Height = 10
  Placement = pos=(0,0,36.15) rot=(0,0,1;0rad)
  Radius = 4
FEATURE [Part::MultiFuse] Fusion032  label="removeToCreteHoleForPlugHousing003"
  Placement = pos=(70,19,36) rot=(0,1,0;1.5708rad)
  Shapes = -> [Cylinder012,Cylinder013]
FEATURE [Part::Cut] Cut007  label="bottom002"
  Base = -> Cut002
  Tool = -> Fusion032
FEATURE [Sketcher::SketchObject] Sketch008
  FullyConstrained = true
  sketch-geometry (54):
    g0: LineSegment StartX=-4.2 StartY=0 StartZ=0 EndX=-6.2 EndY=0 EndZ=0
    g1: LineSegment StartX=-14 StartY=-18 StartZ=0 EndX=-14 EndY=-26.5 EndZ=0
    g2: LineSegment StartX=-4.2 StartY=0 StartZ=0 EndX=-4.2 EndY=-13.4877 EndZ=0
    g3: Circle CenterX=-4.2 CenterY=-13.4877 CenterZ=0 NormalX=0 NormalY=0 NormalZ=1 AngleXU=0 Radius=1
    g4: Circle CenterX=-4.2 CenterY=-26.5 CenterZ=0 NormalX=0 NormalY=0 NormalZ=1 AngleXU=0 Radius=1
    g5: Circle CenterX=-8.2 CenterY=-26.5 CenterZ=0 NormalX=0 NormalY=0 NormalZ=1 AngleXU=0 Radius=1
    g6: BSplineCurve PolesCount=3 KnotsCount=2 Degree=2 IsPeriodic=0
    g7: GeomPoint X=-4.2 Y=-13.4877 Z=0
    g8: GeomPoint X=-8.2 Y=-26.5 Z=0
    g9: LineSegment StartX=-14 StartY=-26.5 StartZ=0 EndX=-8.2 EndY=-26.5 EndZ=0
    g10: LineSegment StartX=-10.15 StartY=-12 StartZ=0 EndX=-10.15 EndY=-14 EndZ=0
    g11: LineSegment StartX=-12.8401 StartY=-16 StartZ=0 EndX=-10.1571 EndY=-16 EndZ=0
    g12: LineSegment StartX=-10.15 StartY=-14 StartZ=0 EndX=-8.70761 EndY=-14 EndZ=0
    g13: LineSegment StartX=-12.8401 StartY=-16 StartZ=0 EndX=-12.8401 EndY=-17.6958 EndZ=0
    g14: LineSegment StartX=-10.15 StartY=-12 StartZ=0 EndX=-7.79258 EndY=-12 EndZ=0
    g15: Circle CenterX=-6.2215 CenterY=-2 CenterZ=0 NormalX=0 NormalY=0 NormalZ=1 AngleXU=0 Radius=1
    g16: Circle CenterX=-6.22762 CenterY=-2.58724 CenterZ=0 NormalX=0 NormalY=0 NormalZ=1 AngleXU=0 Radius=1
    g17: Circle CenterX=-6.32538 CenterY=-4 CenterZ=0 NormalX=0 NormalY=0 NormalZ=1 AngleXU=0 Radius=1
    g18: BSplineCurve PolesCount=3 KnotsCount=2 Degree=2 IsPeriodic=0
    g19: GeomPoint X=-6.2215 Y=-2 Z=0
    g20: GeomPoint X=-6.32538 Y=-4 Z=0
    g21: Circle CenterX=-6.48644 CenterY=-5.99526 CenterZ=0 NormalX=0 NormalY=0 NormalZ=1 AngleXU=0 Radius=1
    g22: Circle CenterX=-6.58486 CenterY=-6.99526 CenterZ=0 NormalX=0 NormalY=0 NormalZ=1 AngleXU=0 Radius=1
    g23: Circle CenterX=-6.77343 CenterY=-8 CenterZ=0 NormalX=0 NormalY=0 NormalZ=1 AngleXU=0 Radius=1
    g24: BSplineCurve PolesCount=3 KnotsCount=2 Degree=2 IsPeriodic=0
    g25: GeomPoint X=-6.48644 Y=-5.99526 Z=0
    g26: GeomPoint X=-6.77343 Y=-8 Z=0
    g27: Circle CenterX=-7.19003 CenterY=-10 CenterZ=0 NormalX=0 NormalY=0 NormalZ=1 AngleXU=0 Radius=1
    g28: Circle CenterX=-7.44407 CenterY=-11.0915 CenterZ=0 NormalX=0 NormalY=0 NormalZ=1 AngleXU=0 Radius=1
    g29: Circle CenterX=-7.79258 CenterY=-12 CenterZ=0 NormalX=0 NormalY=0 NormalZ=1 AngleXU=0 Radius=1
    g30: BSplineCurve PolesCount=3 KnotsCount=2 Degree=2 IsPeriodic=0
    g31: GeomPoint X=-7.19003 Y=-10 Z=0
    g32: GeomPoint X=-7.79258 Y=-12 Z=0
    g33: Circle CenterX=-8.70761 CenterY=-14 CenterZ=0 NormalX=0 NormalY=0 NormalZ=1 AngleXU=0 Radius=1
    g34: Circle CenterX=-9.33087 CenterY=-15.1837 CenterZ=0 NormalX=0 NormalY=0 NormalZ=1 AngleXU=0 Radius=1
    g35: Circle CenterX=-10.1571 CenterY=-16 CenterZ=0 NormalX=0 NormalY=0 NormalZ=1 AngleXU=0 Radius=1
    g36: BSplineCurve PolesCount=3 KnotsCount=2 Degree=2 IsPeriodic=0
    g37: GeomPoint X=-8.70761 Y=-14 Z=0
    g38: GeomPoint X=-10.1571 Y=-16 Z=0
    g39: Circle CenterX=-12.8401 CenterY=-17.6958 CenterZ=0 NormalX=0 NormalY=0 NormalZ=1 AngleXU=0 Radius=1
    g40: Circle CenterX=-13.3521 CenterY=-17.9027 CenterZ=0 NormalX=0 NormalY=0 NormalZ=1 AngleXU=0 Radius=1
    g41: Circle CenterX=-14 CenterY=-18 CenterZ=0 NormalX=0 NormalY=0 NormalZ=1 AngleXU=0 Radius=1
    g42: BSplineCurve PolesCount=3 KnotsCount=2 Degree=2 IsPeriodic=0
    g43: GeomPoint X=-12.8401 Y=-17.6958 Z=0
    g44: GeomPoint X=-14 Y=-18 Z=0
    g45: LineSegment StartX=-6.2 StartY=0 StartZ=0 EndX=-7.2 EndY=0 EndZ=0
    g46: LineSegment StartX=-7.2 StartY=0 StartZ=0 EndX=-7.2 EndY=-2 EndZ=0
    g47: LineSegment StartX=-7.2 StartY=-2 StartZ=0 EndX=-6.2215 EndY=-2 EndZ=0
    g48: LineSegment StartX=-6.32538 StartY=-4 StartZ=0 EndX=-7.65538 EndY=-4 EndZ=0
    g49: LineSegment StartX=-7.65538 StartY=-4 StartZ=0 EndX=-7.65538 EndY=-5.99526 EndZ=0
    g50: LineSegment StartX=-7.65538 StartY=-5.99526 StartZ=0 EndX=-6.48644 EndY=-5.99526 EndZ=0
    g51: LineSegment StartX=-6.77343 StartY=-8 StartZ=0 EndX=-8.43343 EndY=-8 EndZ=0
    g52: LineSegment StartX=-8.43343 StartY=-8 StartZ=0 EndX=-8.43343 EndY=-10 EndZ=0
    g53: LineSegment StartX=-8.43343 StartY=-10 StartZ=0 EndX=-7.19003 EndY=-10 EndZ=0
  constraints (112):
    c: Horizontal(g0)
    c: Distance(g0) = 2
    c: Block(g0)
    c: Vertical(g1)
    c: Coincident(g2,g0)
    c: Vertical(g2)
    c: Block(g2)
    c: Coincident(g6,g2)
    c: Weight(g3) = 1
    c: Equal(g3,g4)
    c: Equal(g3,g5)
    c: InternalAlignment(g3,g6)
    c: InternalAlignment(g4,g6)
    c: InternalAlignment(g5,g6)
    c: InternalAlignment(g7,g6)
    c: InternalAlignment(g8,g6)
    c: Block(g6)
    c: Coincident(g9,g1)
    c: Coincident(g9,g6)
    c: Horizontal(g9)
    c: Vertical(g10)
    c: Block(g10)
    c: Horizontal(g11)
    c: Block(g11)
    c: Coincident(g12,g10)
    c: Horizontal(g12)
    c: Block(g12)
    c: Coincident(g13,g11)
    c: Vertical(g13)
    c: Block(g13)
    c: Coincident(g14,g10)
    c: Horizontal(g14)
    c: Block(g14)
    c: Block(g9)
    c: Block(g1)
    c: Weight(g15) = 1
    c: Equal(g15,g16)
    c: Equal(g15,g17)
    c: InternalAlignment(g15,g18)
    c: InternalAlignment(g16,g18)
    c: InternalAlignment(g17,g18)
    c: InternalAlignment(g19,g18)
    c: InternalAlignment(g20,g18)
    c: Weight(g21) = 1
    c: Equal(g21,g22)
    c: Equal(g21,g23)
    c: InternalAlignment(g21,g24)
    c: InternalAlignment(g22,g24)
    c: InternalAlignment(g23,g24)
    c: InternalAlignment(g25,g24)
    c: InternalAlignment(g26,g24)
    c: Weight(g27) = 1
    c: Equal(g27,g28)
    c: Equal(g27,g29)
    c: Coincident(g30,g14)
    c: InternalAlignment(g27,g30)
    c: InternalAlignment(g28,g30)
    c: InternalAlignment(g29,g30)
    c: InternalAlignment(g31,g30)
    c: InternalAlignment(g32,g30)
    c: Coincident(g36,g12)
    c: Weight(g33) = 1
    c: Equal(g33,g34)
    c: Equal(g33,g35)
    c: Coincident(g36,g11)
    c: InternalAlignment(g33,g36)
    c: InternalAlignment(g34,g36)
    c: InternalAlignment(g35,g36)
    c: InternalAlignment(g37,g36)
    c: InternalAlignment(g38,g36)
    c: Coincident(g42,g13)
    c: Weight(g39) = 1
    c: Equal(g39,g40)
    c: Equal(g39,g41)
    c: Coincident(g42,g1)
    c: InternalAlignment(g39,g42)
    c: InternalAlignment(g40,g42)
    c: InternalAlignment(g41,g42)
    c: InternalAlignment(g43,g42)
    c: InternalAlignment(g44,g42)
    c: Block(g18)
    c: Block(g24)
    c: Block(g30)
    c: Block(g36)
    c: Block(g42)
    c: Horizontal(g45)
    c: Coincident(g45,g0)
    c: Vertical(g46)
    c: Coincident(g46,g45)
    c: Coincident(g47,g46)
    c: Coincident(g47,g18)
    c: Horizontal(g47)
    c: Block(g46)
    c: Coincident(g48,g18)
    c: Horizontal(g48)
    c: Distance(g48) = 1.33
    c: Vertical(g49)
    c: Coincident(g49,g48)
    c: Coincident(g50,g49)
    c: Coincident(g50,g24)
    c: Horizontal(g50)
    c: Tangent(g50,g22)
    c: Horizontal(g51)
    c: Coincident(g51,g24)
    c: Block(g51)
    c: Vertical(g52)
    c: Block(g52)
    c: Coincident(g52,g51)
    c: Coincident(g53,g52)
    c: Coincident(g53,g30)
    c: Horizontal(g53)
    c: Distance(g1) = 8.5
FEATURE [Part::Feature] Face024
  shape: bbox 9.8 x 26.5 x 2e-07 mm, 1 faces, 0 solids (baked)
FEATURE [Part::Revolution] Revolve024
  Angle = 360
  Axis = (0,1,0)
  Base = (0,0,0)
  FaceMakerClass = Part::FaceMakerBullseye
  Placement = pos=(0,0,0) rot=(0,0,1;1.5708rad)
  Solid = false
  Source = -> Face024
  Symmetric = false
FEATURE [Part::Feature] Face025
  shape: bbox 9.8 x 26.5 x 2e-07 mm, 1 faces, 0 solids (baked)
FEATURE [Part::Revolution] Revolve025
  Angle = 360
  Axis = (0,1,0)
  Base = (0,0,0)
  FaceMakerClass = Part::FaceMakerBullseye
  Placement = pos=(0,0,0) rot=(0,0,1;1.5708rad)
  Solid = false
  Source = -> Face025
  Symmetric = false
FEATURE [Part::MultiFuse] Fusion033
  Placement = pos=(-18,19,36) rot=(0,0,1;0rad)
  Shapes = -> [Revolve025,Revolve024]
FEATURE [Part::Cylinder] Cylinder014
  Angle = 360
  AttacherType = Attacher::AttachEngine3D
  Height = 20
  Placement = pos=(0,0,36.15) rot=(0,0,1;0rad)
  Radius = 14.3
FEATURE [Part::Cylinder] Cylinder015
  Angle = 360
  AttacherType = Attacher::AttachEngine3D
  Height = 10
  Placement = pos=(0,0,36.15) rot=(0,0,1;0rad)
  Radius = 4
FEATURE [Part::MultiFuse] Fusion034  label="removeToCreteHoleForPlugHousing004"
  Placement = pos=(-42,19,36) rot=(0,1,0;1.5708rad)
  Shapes = -> [Cylinder014,Cylinder015]
FEATURE [Part::Cut] Cut008  label="top004"
  Base = -> Cut004
  Placement = pos=(-1,0,0) rot=(0,0,1;0rad)
  Tool = -> Fusion034
FEATURE [Part::Box] Box005  label="Cube005"
  AttacherType = Attacher::AttachEngine3D
  Height = 28
  Length = 3
  Placement = pos=(110.7,19,22) rot=(0,0,1;0rad)
  Width = 15.7
FEATURE [Part::Cylinder] Cylinder016
  Angle = 360
  AttacherType = Attacher::AttachEngine3D
  Height = 10
  Placement = pos=(0,0,36.15) rot=(0,0,1;0rad)
  Radius = 4
FEATURE [Part::Cylinder] Cylinder017
  Angle = 360
  AttacherType = Attacher::AttachEngine3D
  Height = 20
  Placement = pos=(0,0,36.15) rot=(0,0,1;0rad)
  Radius = 10.3
FEATURE [Part::MultiFuse] Fusion035  label="removeToCreteHoleForPlugHousing005"
  Placement = pos=(70,19,36) rot=(0,1,0;1.5708rad)
  Shapes = -> [Cylinder017,Cylinder016]
FEATURE [Part::Cut] Cut009  label="plugHousingTab001"
  Base = -> Box005
  Placement = pos=(-107.4,-14,0) rot=(0,0,1;0rad)
  Tool = -> Fusion035
FEATURE [Part::Box] Box006  label="Cube006"
  AttacherType = Attacher::AttachEngine3D
  Height = 28
  Length = 3
  Placement = pos=(110.7,19,22) rot=(0,0,1;0rad)
  Width = 15.7
FEATURE [Part::Cylinder] Cylinder018
  Angle = 360
  AttacherType = Attacher::AttachEngine3D
  Height = 10
  Placement = pos=(0,0,36.15) rot=(0,0,1;0rad)
  Radius = 4
FEATURE [Part::Cylinder] Cylinder019
  Angle = 360
  AttacherType = Attacher::AttachEngine3D
  Height = 20
  Placement = pos=(0,0,36.15) rot=(0,0,1;0rad)
  Radius = 10.3
FEATURE [Part::MultiFuse] Fusion036  label="removeToCreteHoleForPlugHousing006"
  Placement = pos=(70,19,36) rot=(0,1,0;1.5708rad)
  Shapes = -> [Cylinder019,Cylinder018]
FEATURE [Part::Cut] Cut010  label="plugHousingTab002"
  Base = -> Box006
  Placement = pos=(-107.4,-14,0) rot=(0,0,1;0rad)
  Tool = -> Fusion036
FEATURE [Part::MultiFuse] Fusion037
  Placement = pos=(9.6,23,0) rot=(0,0,1;3.14159rad)
  Shapes = -> [Cut009,Cut010]
FEATURE [Part::Box] Box  label="Cube"
  AttacherType = Attacher::AttachEngine3D
  Height = 10
  Length = 3
  Placement = pos=(3.3,4,12) rot=(0,0,1;0rad)
  Width = 10
FEATURE [Part::Fillet] Fillet004
  Base = -> Fusion028
  Edges = 1 edges r=2: [Edge25]
FEATURE [Part::Fillet] Fillet005  label="plugHousing046"
  Base = -> Fillet004
  Edges = 1 edges r=2: [Edge8]
FEATURE [Part::Fillet] Fillet006
  Base = -> Box
  Edges = 1 edges r=2: [Edge11]
FEATURE [Part::Box] Box007  label="Cube007"
  AttacherType = Attacher::AttachEngine3D
  Height = 10
  Length = 3
  Placement = pos=(3.3,4,50) rot=(0,0,1;0rad)
  Width = 10
FEATURE [Part::Fillet] Fillet007
  Base = -> Box007
  Edges = 1 edges r=2: [Edge12]
FEATURE [Part::Box] Box008  label="Cube008"
  AttacherType = Attacher::AttachEngine3D
  Height = 28
  Length = 4
  Placement = pos=(5,0,22) rot=(0,0,1;0rad)
  Width = 10
FEATURE [Part::Fillet] Fillet008
  Base = -> Box008
  Edges = 1 edges r=1: [Edge7]
FEATURE [Part::Fillet] Fillet009
  Base = -> Fillet008
  Edges = 1 edges r=2: [Edge5]
FEATURE [Part::Fillet] Fillet010
  Base = -> Fillet009
  Edges = 1 edges r=2: [Edge2]
FEATURE [Sketcher::SketchObject] Sketch009  label="topSketch003"
  FullyConstrained = true
  sketch-geometry (4):
    g0: LineSegment StartX=16.8446 StartY=31.512 StartZ=0 EndX=16.3251 EndY=34.4666 EndZ=0
    g1: ArcOfCircle CenterX=19 CenterY=19.2524 CenterZ=0 NormalX=0 NormalY=0 NormalZ=1 AngleXU=0 Radius=15.4476 StartAngle=1.74483 EndAngle=2.72717
    g2: ArcOfCircle CenterX=19 CenterY=19.2524 CenterZ=0 NormalX=0 NormalY=0 NormalZ=1 AngleXU=0 Radius=12.4476 StartAngle=1.74483 EndAngle=2.73189
    g3: LineSegment StartX=4.86004 StartY=25.4725 StartZ=0 EndX=7.58253 EndY=24.2107 EndZ=0
  constraints (7):
    c: Block(g0)
    c: Coincident(g1,g0)
    c: Coincident(g2,g0)
    c: Coincident(g3,g1)
    c: Coincident(g3,g2)
    c: Block(g1)
    c: Block(g2)
FEATURE [Part::Extrusion] Extrude008
  Base = -> Sketch009
  Dir = (0,0,1)
  DirMode = 2
  FaceMakerClass = Part::FaceMakerBullseye
  LengthFwd = 10
  LengthRev = 0
  Placement = pos=(0,0,31) rot=(0,0,1;0rad)
  Solid = true
  Symmetric = false
FEATURE [Part::Cylinder] Cylinder020
  Angle = 360
  AttacherType = Attacher::AttachEngine3D
  Height = 20
  Placement = pos=(0,0,36.15) rot=(0,0,1;0rad)
  Radius = 8.2
FEATURE [Part::Cylinder] Cylinder021
  Angle = 360
  AttacherType = Attacher::AttachEngine3D
  Height = 10
  Placement = pos=(0,0,36.15) rot=(0,0,1;0rad)
  Radius = 4
FEATURE [Part::MultiFuse] Fusion038  label="removeToCreteHoleForPlugHousing007"
  Placement = pos=(-42,19,36) rot=(0,1,0;1.5708rad)
  Shapes = -> [Cylinder020,Cylinder021]
FEATURE [Part::Cut] Cut011
  Base = -> Extrude008
  Tool = -> Fusion038
FEATURE [Part::Fillet] Fillet011
  Base = -> Cut011
  Edges = 1 edges r=2: [Edge1]
FEATURE [Part::Fillet] Fillet012
  Base = -> Fillet011
  Edges = 1 edges r=2.5: [Edge1]
FEATURE [Part::Fillet] Fillet013
  Base = -> Fillet012
  Edges = 1 edges r=2.5: [Edge2]
FEATURE [Part::Box] Box010  label="Cube010"
  AttacherType = Attacher::AttachEngine3D
  Height = 16
  Length = 8
  Placement = pos=(12.7,31.52,28) rot=(0,0,1;0rad)
  Width = 4
FEATURE [Sketcher::SketchObject] Sketch010  label="topSketch004"
  FullyConstrained = true
  sketch-geometry (4):
    g0: LineSegment StartX=16.8446 StartY=31.512 StartZ=0 EndX=16.3251 EndY=34.4666 EndZ=0
    g1: ArcOfCircle CenterX=19 CenterY=19.2524 CenterZ=0 NormalX=0 NormalY=0 NormalZ=1 AngleXU=0 Radius=15.4476 StartAngle=1.74483 EndAngle=2.72717
    g2: ArcOfCircle CenterX=19 CenterY=19.2524 CenterZ=0 NormalX=0 NormalY=0 NormalZ=1 AngleXU=0 Radius=12.4476 StartAngle=1.74483 EndAngle=2.73189
    g3: LineSegment StartX=4.86004 StartY=25.4725 StartZ=0 EndX=7.58253 EndY=24.2107 EndZ=0
  constraints (7):
    c: Block(g0)
    c: Coincident(g1,g0)
    c: Coincident(g2,g0)
    c: Coincident(g3,g1)
    c: Coincident(g3,g2)
    c: Block(g1)
    c: Block(g2)
FEATURE [Part::Cylinder] Cylinder022
  Angle = 360
  AttacherType = Attacher::AttachEngine3D
  Height = 10
  Placement = pos=(0,0,36.15) rot=(0,0,1;0rad)
  Radius = 4
FEATURE [Sketcher::SketchObject] Sketch011  label="topSketch005"
  FullyConstrained = true
  sketch-geometry (4):
    g0: LineSegment StartX=16.8446 StartY=31.512 StartZ=0 EndX=16.3251 EndY=34.4666 EndZ=0
    g1: ArcOfCircle CenterX=19 CenterY=19.2524 CenterZ=0 NormalX=0 NormalY=0 NormalZ=1 AngleXU=0 Radius=15.4476 StartAngle=1.74483 EndAngle=2.72717
    g2: ArcOfCircle CenterX=19 CenterY=19.2524 CenterZ=0 NormalX=0 NormalY=0 NormalZ=1 AngleXU=0 Radius=12.4476 StartAngle=1.74483 EndAngle=2.73189
    g3: LineSegment StartX=4.86004 StartY=25.4725 StartZ=0 EndX=7.58253 EndY=24.2107 EndZ=0
  constraints (7):
    c: Block(g0)
    c: Coincident(g1,g0)
    c: Coincident(g2,g0)
    c: Coincident(g3,g1)
    c: Coincident(g3,g2)
    c: Block(g1)
    c: Block(g2)
FEATURE [Part::Extrusion] Extrude010
  Base = -> Sketch011
  Dir = (0,0,1)
  DirMode = 2
  FaceMakerClass = Part::FaceMakerBullseye
  LengthFwd = 10.6
  LengthRev = 0
  Placement = pos=(0,0,31) rot=(0,0,1;0rad)
  Solid = true
  Symmetric = false
FEATURE [Part::Cylinder] Cylinder023
  Angle = 360
  AttacherType = Attacher::AttachEngine3D
  Height = 20
  Placement = pos=(0,0,36.15) rot=(0,0,1;0rad)
  Radius = 8.2
FEATURE [Part::MultiFuse] Fusion039  label="removeToCreteHoleForPlugHousing008"
  Placement = pos=(-42,19,36) rot=(0,1,0;1.5708rad)
  Shapes = -> [Cylinder023,Cylinder022]
FEATURE [Part::Cut] Cut012
  Base = -> Extrude010
  Placement = pos=(0,0,-0.3) rot=(0,0,1;0rad)
  Tool = -> Fusion039
FEATURE [Part::Cut] Cut013
  Base = -> Box010
  Tool = -> Cut012
FEATURE [Part::Fillet] Fillet014
  Base = -> Cut013
  Edges = 1 edges r=0.7: [Edge13]
FEATURE [Part::Fillet] Fillet015
  Base = -> Fillet014
  Edges = 1 edges r=0.7: [Edge13]
FEATURE [Part::Fillet] Fillet016
  Base = -> Fillet015
  Edges = 1 edges r=0.7: [Edge16]
FEATURE [Part::Fillet] Fillet017
  Base = -> Fillet016
  Edges = 1 edges r=0.7: [Edge11]
FEATURE [Part::Fillet] Fillet018
  Base = -> Fillet017
  Edges = 1 edges r=0.7: [Edge10]
FEATURE [Part::Fillet] Fillet019
  Base = -> Fillet018
  Edges = 1 edges r=1.2: [Edge5]
FEATURE [Part::Fillet] Fillet020
  Base = -> Fillet019
  Edges = 1 edges r=1.2: [Edge12]
FEATURE [Part::Fillet] Fillet021
  Base = -> Fillet020
  Edges = 1 edges r=2: [Edge1]
  Placement = pos=(0.3,0,0) rot=(0,0,1;0rad)
FEATURE [Part::MultiFuse] Fusion040  label="top005"
  Shapes = -> [Cut008,Fillet021]
FEATURE [Part::MultiFuse] Fusion041  label="wireHolder"
  Shapes = -> [Fusion033,Fillet013]
FEATURE [Part::MultiFuse] Fusion042
  Shapes = -> [Fillet007,Fusion041]
FEATURE [Part::MultiFuse] Fusion043  label="wireHolder001"
  Shapes = -> [Fusion042,Fillet010]
FEATURE [Part::MultiFuse] Fusion044  label="wireHolder002"
  Shapes = -> [Fillet006,Fusion037,Fusion043]
FEATURE [Part::Feature] Face026
  shape: bbox 11 x 6 x 2e-07 mm, 1 faces, 0 solids (baked)
FEATURE [Part::Revolution] Revolve026
  Angle = 360
  Axis = (0,1,0)
  Base = (0,0,0)
  FaceMakerClass = Part::FaceMakerBullseye
  Placement = pos=(30.3,-1,19.7) rot=(0,0,1;0rad)
  Solid = false
  Source = -> Face026
  Symmetric = false
FEATURE [Sketcher::SketchObject] Sketch013  label="topSketch006"
  FullyConstrained = true
  sketch-geometry (13):
    g0: LineSegment StartX=117 StartY=19 StartZ=0 EndX=117 EndY=38 EndZ=0
    g1: ArcOfCircle CenterX=98 CenterY=19 CenterZ=0 NormalX=0 NormalY=0 NormalZ=1 AngleXU=0 Radius=19 StartAngle=5.7297 EndAngle=6.28319
    g2: LineSegment StartX=0 StartY=3 StartZ=0 EndX=0 EndY=19 EndZ=0
    g3: LineSegment StartX=19 StartY=38 StartZ=0 EndX=117 EndY=38 EndZ=0
    g4: ArcOfCircle CenterX=19 CenterY=19 CenterZ=0 NormalX=0 NormalY=0 NormalZ=1 AngleXU=0 Radius=19 StartAngle=1.5708 EndAngle=3.14159
    g5: ArcOfCircle CenterX=19 CenterY=19 CenterZ=0 NormalX=0 NormalY=0 NormalZ=1 AngleXU=0 Radius=16 StartAngle=1.5708 EndAngle=3.14159
    g6: ArcOfCircle CenterX=98 CenterY=19 CenterZ=0 NormalX=0 NormalY=0 NormalZ=1 AngleXU=0 Radius=16 StartAngle=5.60905 EndAngle=6.28319
    g7: LineSegment StartX=114 StartY=19 StartZ=0 EndX=114 EndY=35 EndZ=0
    g8: LineSegment StartX=110.5 StartY=9.01251 StartZ=0 EndX=114.163 EndY=9.01251 EndZ=0
    g9: LineSegment StartX=114 StartY=35 StartZ=0 EndX=19 EndY=35 EndZ=0
    g10: LineSegment StartX=0 StartY=3 StartZ=0 EndX=0 EndY=0 EndZ=0
    g11: LineSegment StartX=3 StartY=0 StartZ=0 EndX=0 EndY=0 EndZ=0
    g12: LineSegment StartX=3 StartY=19 StartZ=0 EndX=3 EndY=0 EndZ=0
  constraints (33):
    c: Vertical(g0)
    c: Distance(g0) = 19
    c: Block(g0)
    c: Coincident(g1,g0)
    c: Block(g1)
    c: Vertical(g2)
    c: Block(g2)
    c: Coincident(g3,g0)
    c: Horizontal(g3)
    c: Distance(g3) = 98
    c: Coincident(g4,g3)
    c: Coincident(g4,g2)
    c: Block(g4)
    c: Coincident(g5,g4)
    c: Coincident(g6,g1)
    c: Block(g6)
    c: Block(g5)
    c: Coincident(g7,g6)
    c: Vertical(g7)
    c: Coincident(g8,g6)
    c: Coincident(g8,g1)
    c: Coincident(g9,g7)
    c: Coincident(g9,g5)
    c: Horizontal(g9)
    c: Tangent(g9,g5)
    c: Coincident(g10,g2)
    c: Distance(g10) = 3
    c: Vertical(g10)
    c: Coincident(g11,g10)
    c: Horizontal(g11)
    c: Coincident(g12,g5)
    c: Coincident(g12,g11)
    c: Vertical(g12)
FEATURE [Part::Extrusion] Extrude011  label="top006"
  Base = -> Sketch013
  Dir = (0,0,1)
  DirMode = 2
  FaceMakerClass = Part::FaceMakerBullseye
  LengthFwd = 72
  LengthRev = 0
  Solid = true
  Symmetric = false
FEATURE [Sketcher::SketchObject] Sketch014
  FullyConstrained = true
  MapMode = 3
  Placement = pos=(0,0,0) rot=(1,0,0;1.5708rad)
  Support = -> [Extrude011]
  sketch-geometry (8):
    g0: Circle CenterX=80.351 CenterY=-67.6202 CenterZ=0 NormalX=0 NormalY=0 NormalZ=1 AngleXU=0 Radius=2
    g1: Circle CenterX=80.351 CenterY=-67.6202 CenterZ=0 NormalX=0 NormalY=0 NormalZ=1 AngleXU=0 Radius=3
    g2: Circle CenterX=80.351 CenterY=-4.92017 CenterZ=0 NormalX=0 NormalY=0 NormalZ=1 AngleXU=0 Radius=2
    g3: Circle CenterX=80.351 CenterY=-4.92017 CenterZ=0 NormalX=0 NormalY=0 NormalZ=1 AngleXU=0 Radius=3
    g4: Circle CenterX=23.851 CenterY=-4.92017 CenterZ=0 NormalX=0 NormalY=0 NormalZ=1 AngleXU=0 Radius=2
    g5: Circle CenterX=23.851 CenterY=-4.92017 CenterZ=0 NormalX=0 NormalY=0 NormalZ=1 AngleXU=0 Radius=3
    g6: Circle CenterX=23.851 CenterY=-67.6202 CenterZ=0 NormalX=0 NormalY=0 NormalZ=1 AngleXU=0 Radius=2
    g7: Circle CenterX=23.851 CenterY=-67.6202 CenterZ=0 NormalX=0 NormalY=0 NormalZ=1 AngleXU=0 Radius=3
  constraints (8):
    c: Block(g3)
    c: Block(g2)
    c: Block(g1)
    c: Block(g0)
    c: Block(g6)
    c: Block(g7)
    c: Block(g4)
    c: Block(g5)
FEATURE [Part::Feature] Face027
  shape: bbox 11 x 6 x 2e-07 mm, 1 faces, 0 solids (baked)
FEATURE [Part::Revolution] Revolve027
  Angle = 360
  Axis = (0,1,0)
  Base = (0,0,0)
  FaceMakerClass = Part::FaceMakerBullseye
  Placement = pos=(30.3,-1,51.7) rot=(0,0,1;0rad)
  Solid = false
  Source = -> Face027
  Symmetric = false
FEATURE [Part::Feature] Face028
  shape: bbox 11 x 6 x 2e-07 mm, 1 faces, 0 solids (baked)
FEATURE [Part::Revolution] Revolve028
  Angle = 360
  Axis = (0,1,0)
  Base = (0,0,0)
  FaceMakerClass = Part::FaceMakerBullseye
  Placement = pos=(62.3,-1,19.7) rot=(0,0,1;0rad)
  Solid = false
  Source = -> Face028
  Symmetric = false
FEATURE [Part::Feature] Face029
  shape: bbox 11 x 6 x 2e-07 mm, 1 faces, 0 solids (baked)
FEATURE [Part::Revolution] Revolve029
  Angle = 360
  Axis = (0,1,0)
  Base = (0,0,0)
  FaceMakerClass = Part::FaceMakerBullseye
  Placement = pos=(62.3,-1,51.7) rot=(0,0,1;0rad)
  Solid = false
  Source = -> Face029
  Symmetric = false
FEATURE [Part::Feature] Wire
  shape: bbox 11 x 5.2 x 2e-07 mm, 0 faces, 0 solids (baked)
FEATURE [Part::Revolution] Revolve030
  Angle = 360
  Axis = (0,1,0)
  Base = (0,0,0)
  FaceMakerClass = Part::FaceMakerBullseye
  Placement = pos=(30.3,38,19.7) rot=(0,0,1;0rad)
  Solid = true
  Source = -> Wire
  Symmetric = false
FEATURE [Part::Feature] Wire001
  shape: bbox 11 x 5.2 x 2e-07 mm, 0 faces, 0 solids (baked)
FEATURE [Part::Revolution] Revolve031
  Angle = 360
  Axis = (0,1,0)
  Base = (0,0,0)
  FaceMakerClass = Part::FaceMakerBullseye
  Placement = pos=(30.3,38,51.7) rot=(0,0,1;0rad)
  Solid = true
  Source = -> Wire001
  Symmetric = false
FEATURE [Part::Feature] Wire002
  shape: bbox 11 x 5.2 x 2e-07 mm, 0 faces, 0 solids (baked)
FEATURE [Part::Revolution] Revolve032
  Angle = 360
  Axis = (0,1,0)
  Base = (0,0,0)
  FaceMakerClass = Part::FaceMakerBullseye
  Placement = pos=(62.3,38,51.7) rot=(0,0,1;0rad)
  Solid = true
  Source = -> Wire002
  Symmetric = false
FEATURE [Part::Feature] Wire003
  shape: bbox 11 x 5.2 x 2e-07 mm, 0 faces, 0 solids (baked)
FEATURE [Part::Revolution] Revolve033
  Angle = 360
  Axis = (0,1,0)
  Base = (0,0,0)
  FaceMakerClass = Part::FaceMakerBullseye
  Placement = pos=(62.3,38,19.7) rot=(0,0,1;0rad)
  Solid = true
  Source = -> Wire003
  Symmetric = false
FEATURE [Part::MultiFuse] Fusion045  label="altRandScrewHousing"
  Shapes = -> [Revolve029,Revolve027,Revolve028,Revolve026]
FEATURE [Part::MultiFuse] Fusion046  label="fanScrewHousing"
  Shapes = -> [Revolve033,Revolve032,Revolve031,Revolve030]
FEATURE [Sketcher::SketchObject] Sketch015
  FullyConstrained = true
  sketch-geometry (17):
    g0: Circle CenterX=-3.5 CenterY=23.5 CenterZ=0 NormalX=0 NormalY=0 NormalZ=1 AngleXU=0 Radius=1
    g1: Circle CenterX=-1 CenterY=15.25 CenterZ=0 NormalX=0 NormalY=0 NormalZ=1 AngleXU=0 Radius=1
    g2: Circle CenterX=-3.5 CenterY=7 CenterZ=0 NormalX=0 NormalY=0 NormalZ=1 AngleXU=0 Radius=1
    g3: BSplineCurve PolesCount=3 KnotsCount=2 Degree=2 IsPeriodic=0
    g4: GeomPoint X=-3.5 Y=23.5 Z=0
    g5: GeomPoint X=-3.5 Y=7 Z=0
    g6: Circle CenterX=-4.8 CenterY=30.5 CenterZ=0 NormalX=0 NormalY=0 NormalZ=1 AngleXU=0 Radius=1
    g7: Circle CenterX=-3.5 CenterY=30.5 CenterZ=0 NormalX=0 NormalY=0 NormalZ=1 AngleXU=0 Radius=1
    g8: Circle CenterX=-3.5 CenterY=29.2 CenterZ=0 NormalX=0 NormalY=0 NormalZ=1 AngleXU=0 Radius=1
    g9: BSplineCurve PolesCount=3 KnotsCount=2 Degree=2 IsPeriodic=0
    g10: GeomPoint X=-4.8 Y=30.5 Z=0
    g11: GeomPoint X=-3.5 Y=29.2 Z=0
    g12: LineSegment StartX=-3.5 StartY=29.2 StartZ=0 EndX=-3.5 EndY=23.5 EndZ=0
    g13: LineSegment StartX=-4.8 StartY=30.5 StartZ=0 EndX=0 EndY=30.5 EndZ=0
    g14: LineSegment StartX=-3.5 StartY=0.3 StartZ=0 EndX=0 EndY=0.3 EndZ=0
    g15: LineSegment StartX=-3.5 StartY=0.3 StartZ=0 EndX=-3.5 EndY=7 EndZ=0
    g16: LineSegment StartX=0 StartY=0.3 StartZ=0 EndX=0 EndY=30.5 EndZ=0
  constraints (33):
    c: Weight(g0) = 1
    c: Equal(g0,g1)
    c: Equal(g0,g2)
    c: InternalAlignment(g0,g3)
    c: InternalAlignment(g1,g3)
    c: InternalAlignment(g2,g3)
    c: InternalAlignment(g4,g3)
    c: InternalAlignment(g5,g3)
    c: Block(g3)
    c: Weight(g6) = 1
    c: Equal(g6,g7)
    c: Equal(g6,g8)
    c: InternalAlignment(g6,g9)
    c: InternalAlignment(g7,g9)
    c: InternalAlignment(g8,g9)
    c: InternalAlignment(g10,g9)
    c: InternalAlignment(g11,g9)
    c: Block(g9)
    c: Coincident(g12,g9)
    c: Coincident(g12,g3)
    c: Vertical(g12)
    c: Coincident(g13,g9)
    c: Horizontal(g13)
    c: Distance(g13) = 4.8
    c: Horizontal(g14)
    c: Block(g14)
    c: Coincident(g15,g14)
    c: Coincident(g15,g3)
    c: Vertical(g15)
    c: Coincident(g16,g14)
    c: Coincident(g16,g13)
    c: Vertical(g16)
    c: Tangent(g16,g1)
FEATURE [Sketcher::SketchObject] Sketch016
  FullyConstrained = true
  sketch-geometry (16):
    g0: Circle CenterX=-3.5 CenterY=23.5 CenterZ=0 NormalX=0 NormalY=0 NormalZ=1 AngleXU=0 Radius=1
    g1: Circle CenterX=-1 CenterY=15.25 CenterZ=0 NormalX=0 NormalY=0 NormalZ=1 AngleXU=0 Radius=1
    g2: Circle CenterX=-3.5 CenterY=7 CenterZ=0 NormalX=0 NormalY=0 NormalZ=1 AngleXU=0 Radius=1
    g3: BSplineCurve PolesCount=3 KnotsCount=2 Degree=2 IsPeriodic=0
    g4: GeomPoint X=-3.5 Y=23.5 Z=0
    g5: GeomPoint X=-3.5 Y=7 Z=0
    g6: LineSegment StartX=-3.5 StartY=28.2 StartZ=0 EndX=-3.5 EndY=23.5 EndZ=0
    g7: LineSegment StartX=0 StartY=29.5 StartZ=0 EndX=0 EndY=30 EndZ=0
    g8: LineSegment StartX=-3.5 StartY=28.2 StartZ=0 EndX=-3.5 EndY=30 EndZ=0
    g9: LineSegment StartX=0 StartY=30 StartZ=0 EndX=0 EndY=30.5 EndZ=0
    g10: LineSegment StartX=0 StartY=30.5 StartZ=0 EndX=-3.5 EndY=30.5 EndZ=0
    g11: LineSegment StartX=-3.5 StartY=30.5 StartZ=0 EndX=-3.5 EndY=30 EndZ=0
    g12: LineSegment StartX=0 StartY=29.5 StartZ=0 EndX=0 EndY=5 EndZ=0
    g13: LineSegment StartX=-3.5 StartY=0.3 StartZ=0 EndX=-3.5 EndY=7 EndZ=0
    g14: LineSegment StartX=-3.5 StartY=0.3 StartZ=0 EndX=0 EndY=0.3 EndZ=0
    g15: LineSegment StartX=0 StartY=5 StartZ=0 EndX=0 EndY=0.3 EndZ=0
  constraints (39):
    c: Weight(g0) = 1
    c: Equal(g0,g1)
    c: Equal(g0,g2)
    c: InternalAlignment(g0,g3)
    c: InternalAlignment(g1,g3)
    c: InternalAlignment(g2,g3)
    c: InternalAlignment(g4,g3)
    c: InternalAlignment(g5,g3)
    c: Block(g3)
    c: Coincident(g6,g3)
    c: Vertical(g6)
    c: Vertical(g7)
    c: Distance(g7) = 0.5
    c: Coincident(g8,g6)
    c: Vertical(g8)
    c: Block(g6)
    c: Block(g7)
    c: Vertical(g9)
    c: Equal(g7,g9) = 0.5
    c: Block(g9)
    c: Coincident(g9,g7)
    c: Horizontal(g10)
    c: Coincident(g10,g9)
    c: Coincident(g11,g10)
    c: Coincident(g11,g8)
    c: Vertical(g11)
    c: Block(g11)
    c: Coincident(g12,g7)
    c: Vertical(g12)
    c: Coincident(g13,g3)
    c: Vertical(g13)
    c: Distance(g13) = 6.7
    c: Coincident(g14,g13)
    c: Horizontal(g14)
    c: Block(g14)
    c: Coincident(g15,g12)
    c: Coincident(g15,g14)
    c: Vertical(g15)
    c: Block(g15)
FEATURE [Sketcher::SketchObject] Sketch017
  FullyConstrained = true
  sketch-geometry (11):
    g0: LineSegment StartX=-3.5 StartY=1e-16 StartZ=0 EndX=-1.6 EndY=1e-16 EndZ=0
    g1: LineSegment StartX=-1.6 StartY=1e-16 StartZ=0 EndX=-1.6 EndY=1.5 EndZ=0
    g2: LineSegment StartX=-3.5 StartY=1.5 StartZ=0 EndX=-1.6 EndY=1.5 EndZ=0
    g3: LineSegment StartX=-3.5 StartY=1e-16 StartZ=0 EndX=-4.8 EndY=1e-16 EndZ=0
    g4: Circle CenterX=-3.5 CenterY=1.3 CenterZ=0 NormalX=0 NormalY=0 NormalZ=1 AngleXU=0 Radius=1
    g5: Circle CenterX=-3.5 CenterY=1e-16 CenterZ=0 NormalX=0 NormalY=0 NormalZ=1 AngleXU=0 Radius=1
    g6: Circle CenterX=-4.8 CenterY=1e-16 CenterZ=0 NormalX=0 NormalY=0 NormalZ=1 AngleXU=0 Radius=1
    g7: BSplineCurve PolesCount=3 KnotsCount=2 Degree=2 IsPeriodic=0
    g8: GeomPoint X=-3.5 Y=1.3 Z=0
    g9: GeomPoint X=-4.8 Y=1e-16 Z=0
    g10: LineSegment StartX=-3.5 StartY=1.3 StartZ=0 EndX=-3.5 EndY=1.5 EndZ=0
  constraints (24):
    c: Horizontal(g0)
    c: Distance(g0) = 1.9
    c: Block(g0)
    c: Coincident(g1,g0)
    c: Vertical(g1)
    c: Coincident(g2,g1)
    c: Horizontal(g2)
    c: Coincident(g3,g0)
    c: Horizontal(g3)
    c: Distance(g3) = 1.3
    c: Weight(g4) = 1
    c: Equal(g4,g5)
    c: Coincident(g5,g0)
    c: Equal(g4,g6)
    c: Coincident(g7,g3)
    c: InternalAlignment(g4,g7)
    c: InternalAlignment(g5,g7)
    c: InternalAlignment(g6,g7)
    c: InternalAlignment(g8,g7)
    c: InternalAlignment(g9,g7)
    c: Coincident(g10,g7)
    c: Coincident(g10,g2)
    c: Vertical(g10)
    c: Block(g10)
FEATURE [Part::Feature] Face035
  shape: bbox 3.2 x 1.5 x 2e-07 mm, 1 faces, 0 solids (baked)
FEATURE [Part::Revolution] Revolve039  label="backCaseScrewRetainer"
  Angle = 360
  Axis = (0,1,0)
  Base = (0,0,0)
  FaceMakerClass = Part::FaceMakerBullseye
  Placement = pos=(12.5,3,62) rot=(0,0,1;0rad)
  Solid = false
  Source = -> Face035
  Symmetric = false
FEATURE [Part::Feature] Face036
  shape: bbox 3.2 x 1.5 x 2e-07 mm, 1 faces, 0 solids (baked)
FEATURE [Part::Feature] Face039
  shape: bbox 4.8 x 30.2 x 2e-07 mm, 1 faces, 0 solids (baked)
FEATURE [Part::Revolution] Revolve043  label="frontCaseScrewPost002"
  Angle = 360
  Axis = (0,1,0)
  Base = (0,0,0)
  FaceMakerClass = Part::FaceMakerBullseye
  Placement = pos=(89.5,4.5,3.5) rot=(0,0,1;0rad)
  Solid = false
  Source = -> Face039
  Symmetric = false
FEATURE [Part::Feature] Face042
  shape: bbox 4.8 x 30.2 x 2e-07 mm, 1 faces, 0 solids (baked)
FEATURE [Part::Revolution] Revolve046  label="frontCaseScrewPost003"
  Angle = 360
  Axis = (0,1,0)
  Base = (0,0,0)
  FaceMakerClass = Part::FaceMakerBullseye
  Placement = pos=(89.5,4.5,68.5) rot=(0,0,1;0rad)
  Solid = false
  Source = -> Face042
  Symmetric = false
FEATURE [Part::Feature] Face043
  shape: bbox 3.2 x 1.5 x 2e-07 mm, 1 faces, 0 solids (baked)
FEATURE [Part::Revolution] Revolve047  label="frontCaseScrewRetainer002"
  Angle = 360
  Axis = (0,1,0)
  Base = (0,0,0)
  FaceMakerClass = Part::FaceMakerBullseye
  Placement = pos=(89.5,3,68.5) rot=(0,0,1;0rad)
  Solid = false
  Source = -> Face043
  Symmetric = false
FEATURE [Part::Feature] Face044
  shape: bbox 3.2 x 1.5 x 2e-07 mm, 1 faces, 0 solids (baked)
FEATURE [Part::Revolution] Revolve048  label="frontCaseScrewRetainer003"
  Angle = 360
  Axis = (0,1,0)
  Base = (0,0,0)
  FaceMakerClass = Part::FaceMakerBullseye
  Placement = pos=(89.5,3,3.5) rot=(0,0,1;0rad)
  Solid = false
  Source = -> Face044
  Symmetric = false
FEATURE [App::MeasureDistance] Distance002  label="Distance: 1.67 mm"
  Distance = 1.66921
  P1 = (99.2361,4.7524,71.7)
  P2 = (99.2347,6.42161,71.7)
FEATURE [Sketcher::SketchObject] Sketch018
  FullyConstrained = true
  sketch-geometry (7):
    g0: LineSegment StartX=0 StartY=0 StartZ=0 EndX=0 EndY=6 EndZ=0
    g1: Circle CenterX=0 CenterY=0 CenterZ=0 NormalX=0 NormalY=0 NormalZ=1 AngleXU=0 Radius=1
    g2: Circle CenterX=8 CenterY=6 CenterZ=0 NormalX=0 NormalY=0 NormalZ=1 AngleXU=0 Radius=1
    g3: BSplineCurve PolesCount=3 KnotsCount=2 Degree=2 IsPeriodic=0
    g4: GeomPoint X=0 Y=0 Z=0
    g5: GeomPoint X=8 Y=6 Z=0
    g6: LineSegment StartX=0 StartY=6 StartZ=0 EndX=8 EndY=6 EndZ=0
  constraints (14):
    c: Coincident(g0,g-1)
    c: Distance(g0) = 6
    c: Vertical(g0)
    c: Coincident(g3,g0)
    c: Weight(g1) = 1
    c: Equal(g1,g2)
    c: InternalAlignment(g1,g3)
    c: InternalAlignment(g2,g3)
    c: InternalAlignment(g4,g3)
    c: InternalAlignment(g5,g3)
    c: Block(g3)
    c: Coincident(g6,g0)
    c: Coincident(g6,g3)
    c: Horizontal(g6)
FEATURE [Part::Extrusion] Extrude012  label="caseScrewPillarBracket"
  Base = -> Sketch018
  Dir = (0,0,1)
  DirMode = 2
  FaceMakerClass = Part::FaceMakerBullseye
  LengthFwd = 2.4
  LengthRev = 0
  Placement = pos=(15.76,29,8.8) rot=(0,1,0;0rad)
  Solid = true
  Symmetric = false
FEATURE [Sketcher::SketchObject] Sketch019
  FullyConstrained = true
  sketch-geometry (7):
    g0: LineSegment StartX=0 StartY=0 StartZ=0 EndX=0 EndY=6 EndZ=0
    g1: Circle CenterX=0 CenterY=0 CenterZ=0 NormalX=0 NormalY=0 NormalZ=1 AngleXU=0 Radius=1
    g2: Circle CenterX=8 CenterY=6 CenterZ=0 NormalX=0 NormalY=0 NormalZ=1 AngleXU=0 Radius=1
    g3: BSplineCurve PolesCount=3 KnotsCount=2 Degree=2 IsPeriodic=0
    g4: GeomPoint X=0 Y=0 Z=0
    g5: GeomPoint X=8 Y=6 Z=0
    g6: LineSegment StartX=0 StartY=6 StartZ=0 EndX=8 EndY=6 EndZ=0
  constraints (14):
    c: Coincident(g0,g-1)
    c: Distance(g0) = 6
    c: Vertical(g0)
    c: Coincident(g3,g0)
    c: Weight(g1) = 1
    c: Equal(g1,g2)
    c: InternalAlignment(g1,g3)
    c: InternalAlignment(g2,g3)
    c: InternalAlignment(g4,g3)
    c: InternalAlignment(g5,g3)
    c: Block(g3)
    c: Coincident(g6,g0)
    c: Coincident(g6,g3)
    c: Horizontal(g6)
FEATURE [Part::Extrusion] Extrude013  label="caseScrewPillarBracket001"
  Base = -> Sketch019
  Dir = (0,0,1)
  DirMode = 2
  FaceMakerClass = Part::FaceMakerBullseye
  LengthFwd = 2.4
  LengthRev = 0
  Placement = pos=(15.76,29,60.8) rot=(0,0,1;0rad)
  Solid = true
  Symmetric = false
FEATURE [Sketcher::SketchObject] Sketch020
  FullyConstrained = true
  sketch-geometry (7):
    g0: LineSegment StartX=0 StartY=0 StartZ=0 EndX=0 EndY=6 EndZ=0
    g1: Circle CenterX=0 CenterY=0 CenterZ=0 NormalX=0 NormalY=0 NormalZ=1 AngleXU=0 Radius=1
    g2: Circle CenterX=8 CenterY=6 CenterZ=0 NormalX=0 NormalY=0 NormalZ=1 AngleXU=0 Radius=1
    g3: BSplineCurve PolesCount=3 KnotsCount=2 Degree=2 IsPeriodic=0
    g4: GeomPoint X=0 Y=0 Z=0
    g5: GeomPoint X=8 Y=6 Z=0
    g6: LineSegment StartX=0 StartY=6 StartZ=0 EndX=8 EndY=6 EndZ=0
  constraints (14):
    c: Coincident(g0,g-1)
    c: Distance(g0) = 6
    c: Vertical(g0)
    c: Coincident(g3,g0)
    c: Weight(g1) = 1
    c: Equal(g1,g2)
    c: InternalAlignment(g1,g3)
    c: InternalAlignment(g2,g3)
    c: InternalAlignment(g4,g3)
    c: InternalAlignment(g5,g3)
    c: Block(g3)
    c: Coincident(g6,g0)
    c: Coincident(g6,g3)
    c: Horizontal(g6)
FEATURE [Part::Extrusion] Extrude014  label="caseScrewPillarBracket002"
  Base = -> Sketch020
  Dir = (0,0,1)
  DirMode = 2
  FaceMakerClass = Part::FaceMakerBullseye
  LengthFwd = 2.4
  LengthRev = 0
  Placement = pos=(13.7,29,13.26) rot=(0,-1,0;1.5708rad)
  Solid = true
  Symmetric = false
FEATURE [Sketcher::SketchObject] Sketch021
  FullyConstrained = true
  sketch-geometry (7):
    g0: LineSegment StartX=0 StartY=0 StartZ=0 EndX=0 EndY=6 EndZ=0
    g1: Circle CenterX=0 CenterY=0 CenterZ=0 NormalX=0 NormalY=0 NormalZ=1 AngleXU=0 Radius=1
    g2: Circle CenterX=8 CenterY=6 CenterZ=0 NormalX=0 NormalY=0 NormalZ=1 AngleXU=0 Radius=1
    g3: BSplineCurve PolesCount=3 KnotsCount=2 Degree=2 IsPeriodic=0
    g4: GeomPoint X=0 Y=0 Z=0
    g5: GeomPoint X=8 Y=6 Z=0
    g6: LineSegment StartX=0 StartY=6 StartZ=0 EndX=8 EndY=6 EndZ=0
  constraints (14):
    c: Coincident(g0,g-1)
    c: Distance(g0) = 6
    c: Vertical(g0)
    c: Coincident(g3,g0)
    c: Weight(g1) = 1
    c: Equal(g1,g2)
    c: InternalAlignment(g1,g3)
    c: InternalAlignment(g2,g3)
    c: InternalAlignment(g4,g3)
    c: InternalAlignment(g5,g3)
    c: Block(g3)
    c: Coincident(g6,g0)
    c: Coincident(g6,g3)
    c: Horizontal(g6)
FEATURE [Part::Extrusion] Extrude015  label="caseScrewPillarBracket003"
  Base = -> Sketch021
  Dir = (0,0,1)
  DirMode = 2
  FaceMakerClass = Part::FaceMakerBullseye
  LengthFwd = 2.4
  LengthRev = 0
  Placement = pos=(11.3,29,58.74) rot=(0,1,0;1.5708rad)
  Solid = true
  Symmetric = false
FEATURE [Sketcher::SketchObject] Sketch022
  FullyConstrained = true
  sketch-geometry (7):
    g0: LineSegment StartX=0 StartY=0 StartZ=0 EndX=0 EndY=6 EndZ=0
    g1: Circle CenterX=0 CenterY=0 CenterZ=0 NormalX=0 NormalY=0 NormalZ=1 AngleXU=0 Radius=1
    g2: Circle CenterX=8 CenterY=6 CenterZ=0 NormalX=0 NormalY=0 NormalZ=1 AngleXU=0 Radius=1
    g3: BSplineCurve PolesCount=3 KnotsCount=2 Degree=2 IsPeriodic=0
    g4: GeomPoint X=0 Y=0 Z=0
    g5: GeomPoint X=8 Y=6 Z=0
    g6: LineSegment StartX=0 StartY=6 StartZ=0 EndX=8 EndY=6 EndZ=0
  constraints (14):
    c: Coincident(g0,g-1)
    c: Distance(g0) = 6
    c: Vertical(g0)
    c: Coincident(g3,g0)
    c: Weight(g1) = 1
    c: Equal(g1,g2)
    c: InternalAlignment(g1,g3)
    c: InternalAlignment(g2,g3)
    c: InternalAlignment(g4,g3)
    c: InternalAlignment(g5,g3)
    c: Block(g3)
    c: Coincident(g6,g0)
    c: Coincident(g6,g3)
    c: Horizontal(g6)
FEATURE [Part::Extrusion] Extrude016  label="caseScrewPillarBracket004"
  Base = -> Sketch022
  Dir = (0,0,1)
  DirMode = 2
  FaceMakerClass = Part::FaceMakerBullseye
  LengthFwd = 2.4
  LengthRev = 0
  Placement = pos=(88.3,29,65.23) rot=(0,1,0;1.5708rad)
  Solid = true
  Symmetric = false
FEATURE [Sketcher::SketchObject] Sketch023
  FullyConstrained = true
  sketch-geometry (7):
    g0: LineSegment StartX=0 StartY=0 StartZ=0 EndX=0 EndY=6 EndZ=0
    g1: Circle CenterX=0 CenterY=0 CenterZ=0 NormalX=0 NormalY=0 NormalZ=1 AngleXU=0 Radius=1
    g2: Circle CenterX=8 CenterY=6 CenterZ=0 NormalX=0 NormalY=0 NormalZ=1 AngleXU=0 Radius=1
    g3: BSplineCurve PolesCount=3 KnotsCount=2 Degree=2 IsPeriodic=0
    g4: GeomPoint X=0 Y=0 Z=0
    g5: GeomPoint X=8 Y=6 Z=0
    g6: LineSegment StartX=0 StartY=6 StartZ=0 EndX=8 EndY=6 EndZ=0
  constraints (14):
    c: Coincident(g0,g-1)
    c: Distance(g0) = 6
    c: Vertical(g0)
    c: Coincident(g3,g0)
    c: Weight(g1) = 1
    c: Equal(g1,g2)
    c: InternalAlignment(g1,g3)
    c: InternalAlignment(g2,g3)
    c: InternalAlignment(g4,g3)
    c: InternalAlignment(g5,g3)
    c: Block(g3)
    c: Coincident(g6,g0)
    c: Coincident(g6,g3)
    c: Horizontal(g6)
FEATURE [Part::Extrusion] Extrude017  label="caseScrewPillarBracket005"
  Base = -> Sketch023
  Dir = (0,0,1)
  DirMode = 2
  FaceMakerClass = Part::FaceMakerBullseye
  LengthFwd = 2.4
  LengthRev = 0
  Placement = pos=(90.7,29,6.77) rot=(0,-1,0;1.5708rad)
  Solid = true
  Symmetric = false
FEATURE [Sketcher::SketchObject] Sketch024
  FullyConstrained = true
  sketch-geometry (7):
    g0: LineSegment StartX=0 StartY=0 StartZ=0 EndX=0 EndY=6 EndZ=0
    g1: Circle CenterX=0 CenterY=0 CenterZ=0 NormalX=0 NormalY=0 NormalZ=1 AngleXU=0 Radius=1
    g2: Circle CenterX=8 CenterY=6 CenterZ=0 NormalX=0 NormalY=0 NormalZ=1 AngleXU=0 Radius=1
    g3: BSplineCurve PolesCount=3 KnotsCount=2 Degree=2 IsPeriodic=0
    g4: GeomPoint X=0 Y=0 Z=0
    g5: GeomPoint X=8 Y=6 Z=0
    g6: LineSegment StartX=0 StartY=6 StartZ=0 EndX=8 EndY=6 EndZ=0
  constraints (14):
    c: Coincident(g0,g-1)
    c: Distance(g0) = 6
    c: Vertical(g0)
    c: Coincident(g3,g0)
    c: Weight(g1) = 1
    c: Equal(g1,g2)
    c: InternalAlignment(g1,g3)
    c: InternalAlignment(g2,g3)
    c: InternalAlignment(g4,g3)
    c: InternalAlignment(g5,g3)
    c: Block(g3)
    c: Coincident(g6,g0)
    c: Coincident(g6,g3)
    c: Horizontal(g6)
FEATURE [Part::Extrusion] Extrude018  label="caseScrewPillarBracket006"
  Base = -> Sketch024
  Dir = (0,0,1)
  DirMode = 2
  FaceMakerClass = Part::FaceMakerBullseye
  LengthFwd = 2.4
  LengthRev = 0
  Placement = pos=(103.7,29,6.77) rot=(0,-1,0;1.5708rad)
  Solid = true
  Symmetric = false
FEATURE [Sketcher::SketchObject] Sketch025
  FullyConstrained = true
  sketch-geometry (7):
    g0: LineSegment StartX=0 StartY=0 StartZ=0 EndX=0 EndY=6 EndZ=0
    g1: Circle CenterX=0 CenterY=0 CenterZ=0 NormalX=0 NormalY=0 NormalZ=1 AngleXU=0 Radius=1
    g2: Circle CenterX=8 CenterY=6 CenterZ=0 NormalX=0 NormalY=0 NormalZ=1 AngleXU=0 Radius=1
    g3: BSplineCurve PolesCount=3 KnotsCount=2 Degree=2 IsPeriodic=0
    g4: GeomPoint X=0 Y=0 Z=0
    g5: GeomPoint X=8 Y=6 Z=0
    g6: LineSegment StartX=0 StartY=6 StartZ=0 EndX=8 EndY=6 EndZ=0
  constraints (14):
    c: Coincident(g0,g-1)
    c: Distance(g0) = 6
    c: Vertical(g0)
    c: Coincident(g3,g0)
    c: Weight(g1) = 1
    c: Equal(g1,g2)
    c: InternalAlignment(g1,g3)
    c: InternalAlignment(g2,g3)
    c: InternalAlignment(g4,g3)
    c: InternalAlignment(g5,g3)
    c: Block(g3)
    c: Coincident(g6,g0)
    c: Coincident(g6,g3)
    c: Horizontal(g6)
FEATURE [Part::Extrusion] Extrude019  label="caseScrewPillarBracket007"
  Base = -> Sketch025
  Dir = (0,0,1)
  DirMode = 2
  FaceMakerClass = Part::FaceMakerBullseye
  LengthFwd = 2.4
  LengthRev = 0
  Placement = pos=(101.3,29,65.23) rot=(0,1,0;1.5708rad)
  Solid = true
  Symmetric = false
FEATURE [Part::Box] Box011  label="frontCaseScrewPillarBracket"
  AttacherType = Attacher::AttachEngine3D
  Height = 2.4
  Length = 16
  Placement = pos=(87,28,2.3) rot=(0,0,1;0rad)
  Width = 7
FEATURE [Part::Box] Box012  label="frontCaseScrewPillarBracket001"
  AttacherType = Attacher::AttachEngine3D
  Height = 2.4
  Length = 16
  Placement = pos=(87,28,67.3) rot=(0,0,1;0rad)
  Width = 7
FEATURE [Sketcher::SketchObject] Sketch026
  FullyConstrained = true
  sketch-geometry (17):
    g0: Circle CenterX=-3.5 CenterY=23.5 CenterZ=0 NormalX=0 NormalY=0 NormalZ=1 AngleXU=0 Radius=1
    g1: Circle CenterX=-1 CenterY=15.25 CenterZ=0 NormalX=0 NormalY=0 NormalZ=1 AngleXU=0 Radius=1
    g2: Circle CenterX=-3.5 CenterY=7 CenterZ=0 NormalX=0 NormalY=0 NormalZ=1 AngleXU=0 Radius=1
    g3: BSplineCurve PolesCount=3 KnotsCount=2 Degree=2 IsPeriodic=0
    g4: GeomPoint X=-3.5 Y=23.5 Z=0
    g5: GeomPoint X=-3.5 Y=7 Z=0
    g6: Circle CenterX=-4.8 CenterY=30.5 CenterZ=0 NormalX=0 NormalY=0 NormalZ=1 AngleXU=0 Radius=1
    g7: Circle CenterX=-3.5 CenterY=30.5 CenterZ=0 NormalX=0 NormalY=0 NormalZ=1 AngleXU=0 Radius=1
    g8: Circle CenterX=-3.5 CenterY=29.2 CenterZ=0 NormalX=0 NormalY=0 NormalZ=1 AngleXU=0 Radius=1
    g9: BSplineCurve PolesCount=3 KnotsCount=2 Degree=2 IsPeriodic=0
    g10: GeomPoint X=-4.8 Y=30.5 Z=0
    g11: GeomPoint X=-3.5 Y=29.2 Z=0
    g12: LineSegment StartX=-3.5 StartY=29.2 StartZ=0 EndX=-3.5 EndY=23.5 EndZ=0
    g13: LineSegment StartX=-4.8 StartY=30.5 StartZ=0 EndX=0 EndY=30.5 EndZ=0
    g14: LineSegment StartX=-3.5 StartY=5 StartZ=0 EndX=-3.5 EndY=7 EndZ=0
    g15: LineSegment StartX=0 StartY=5 StartZ=0 EndX=0 EndY=30.5 EndZ=0
    g16: LineSegment StartX=-3.5 StartY=5 StartZ=0 EndX=0 EndY=5 EndZ=0
  constraints (33):
    c: Weight(g0) = 1
    c: Equal(g0,g1)
    c: Equal(g0,g2)
    c: InternalAlignment(g0,g3)
    c: InternalAlignment(g1,g3)
    c: InternalAlignment(g2,g3)
    c: InternalAlignment(g4,g3)
    c: InternalAlignment(g5,g3)
    c: Block(g3)
    c: Weight(g6) = 1
    c: Equal(g6,g7)
    c: Equal(g6,g8)
    c: InternalAlignment(g6,g9)
    c: InternalAlignment(g7,g9)
    c: InternalAlignment(g8,g9)
    c: InternalAlignment(g10,g9)
    c: InternalAlignment(g11,g9)
    c: Block(g9)
    c: Coincident(g12,g9)
    c: Coincident(g12,g3)
    c: Vertical(g12)
    c: Coincident(g13,g9)
    c: Horizontal(g13)
    c: Distance(g13) = 4.8
    c: Coincident(g14,g3)
    c: Vertical(g14)
    c: Coincident(g15,g13)
    c: Vertical(g15)
    c: Tangent(g15,g1)
    c: Distance(g14) = 2
    c: Coincident(g16,g14)
    c: Horizontal(g16)
    c: Coincident(g15,g16)
FEATURE [Part::Feature] Face050
  shape: bbox 4.8 x 25.5 x 2e-07 mm, 1 faces, 0 solids (baked)
FEATURE [Part::Revolution] Revolve054  label="moreFrontCaseScrewPost001"
  Angle = 360
  Axis = (0,1,0)
  Base = (0,0,0)
  FaceMakerClass = Part::FaceMakerBullseye
  Placement = pos=(102.5,4.5,3.5) rot=(0,0,1;0rad)
  Solid = false
  Source = -> Face050
  Symmetric = false
FEATURE [Part::Feature] Face051
  shape: bbox 4.8 x 25.5 x 2e-07 mm, 1 faces, 0 solids (baked)
FEATURE [Part::Revolution] Revolve055  label="moreFrontCaseScrewPost002"
  Angle = 360
  Axis = (0,1,0)
  Base = (0,0,0)
  FaceMakerClass = Part::FaceMakerBullseye
  Placement = pos=(102.5,4.5,68.5) rot=(0,0,1;0rad)
  Solid = false
  Source = -> Face051
  Symmetric = false
FEATURE [Sketcher::SketchObject] Sketch027
  FullyConstrained = true
  sketch-geometry (10):
    g0: LineSegment StartX=-1.6 StartY=4.7 StartZ=0 EndX=-1.6 EndY=1.7 EndZ=0
    g1: LineSegment StartX=-3.5 StartY=4.7 StartZ=0 EndX=-1.6 EndY=4.7 EndZ=0
    g2: LineSegment StartX=-1.6 StartY=1.7 StartZ=0 EndX=-1.6 EndY=1.5 EndZ=0
    g3: LineSegment StartX=-1.6 StartY=1.5 StartZ=0 EndX=-5.2 EndY=1.5 EndZ=0
    g4: Circle CenterX=-3.5 CenterY=4.7 CenterZ=0 NormalX=0 NormalY=0 NormalZ=1 AngleXU=0 Radius=1
    g5: Circle CenterX=-3.59627 CenterY=2.99743 CenterZ=0 NormalX=0 NormalY=0 NormalZ=1 AngleXU=0 Radius=1
    g6: Circle CenterX=-5.2 CenterY=1.5 CenterZ=0 NormalX=0 NormalY=0 NormalZ=1 AngleXU=0 Radius=1
    g7: BSplineCurve PolesCount=3 KnotsCount=2 Degree=2 IsPeriodic=0
    g8: GeomPoint X=-3.5 Y=4.7 Z=0
    g9: GeomPoint X=-5.2 Y=1.5 Z=0
  constraints (23):
    c: Vertical(g0)
    c: Distance(g0) = 3
    c: Coincident(g1,g0)
    c: Horizontal(g1)
    c: Block(g0)
    c: Block(g1)
    c: Coincident(g2,g0)
    c: Vertical(g2)
    c: Distance(g2) = 0.2
    c: Coincident(g3,g2)
    c: Horizontal(g3)
    c: Block(g3)
    c: Coincident(g7,g1)
    c: Weight(g4) = 1
    c: Equal(g4,g5)
    c: Equal(g4,g6)
    c: Coincident(g7,g3)
    c: InternalAlignment(g4,g7)
    c: InternalAlignment(g5,g7)
    c: InternalAlignment(g6,g7)
    c: InternalAlignment(g8,g7)
    c: InternalAlignment(g9,g7)
    c: Block(g7)
FEATURE [Sketcher::SketchObject] Sketch028
  FullyConstrained = true
  sketch-geometry (18):
    g0: LineSegment StartX=0 StartY=3e-16 StartZ=0 EndX=0 EndY=1.7 EndZ=0
    g1: LineSegment StartX=-3.5 StartY=0 StartZ=0 EndX=-3.5 EndY=0.9 EndZ=0
    g2: Circle CenterX=-2.7 CenterY=1.7 CenterZ=0 NormalX=0 NormalY=0 NormalZ=1 AngleXU=0 Radius=1
    g3: Circle CenterX=-3.5 CenterY=1.7 CenterZ=0 NormalX=0 NormalY=0 NormalZ=1 AngleXU=0 Radius=1
    g4: Circle CenterX=-3.5 CenterY=0.9 CenterZ=0 NormalX=0 NormalY=0 NormalZ=1 AngleXU=0 Radius=1
    g5: BSplineCurve PolesCount=3 KnotsCount=2 Degree=2 IsPeriodic=0
    g6: GeomPoint X=-2.7 Y=1.7 Z=0
    g7: GeomPoint X=-3.5 Y=0.9 Z=0
    g8: LineSegment StartX=-3.5 StartY=0 StartZ=0 EndX=-3.5 EndY=-7 EndZ=0
    g9: LineSegment StartX=0 StartY=3e-16 StartZ=0 EndX=0 EndY=-7 EndZ=0
    g10: LineSegment StartX=-3.5 StartY=-7 StartZ=0 EndX=0 EndY=-7 EndZ=0
    g11: LineSegment StartX=-2.7 StartY=1.7 StartZ=0 EndX=-1.6 EndY=1.7 EndZ=0
    g12: LineSegment StartX=0 StartY=1.7 StartZ=0 EndX=0 EndY=4.5 EndZ=0
    g13: LineSegment StartX=0 StartY=4.5 StartZ=0 EndX=0 EndY=10.8 EndZ=0
    g14: LineSegment StartX=0 StartY=10.8 StartZ=0 EndX=-2 EndY=10.8 EndZ=0
    g15: LineSegment StartX=-1.6 StartY=4.7 StartZ=0 EndX=-1.6 EndY=1.7 EndZ=0
    g16: LineSegment StartX=-1.6 StartY=4.7 StartZ=0 EndX=-2 EndY=4.7 EndZ=0
    g17: LineSegment StartX=-2 StartY=4.7 StartZ=0 EndX=-2 EndY=10.8 EndZ=0
  constraints (44):
    c: Vertical(g0)
    c: Vertical(g1)
    c: Distance(g1) = 0.9
    c: Block(g0)
    c: Distance(g0) = 1.7
    c: Weight(g2) = 1
    c: Equal(g2,g3)
    c: Equal(g2,g4)
    c: Coincident(g5,g1)
    c: InternalAlignment(g2,g5)
    c: InternalAlignment(g3,g5)
    c: InternalAlignment(g4,g5)
    c: InternalAlignment(g6,g5)
    c: InternalAlignment(g7,g5)
    c: Block(g5)
    c: Coincident(g8,g1)
    c: Vertical(g8)
    c: Distance(g8) = 7
    c: Vertical(g9)
    c: Equal(g8,g9) = 7
    c: Coincident(g9,g0)
    c: Coincident(g10,g8)
    c: Coincident(g10,g9)
    c: Horizontal(g10)
    c: Coincident(g11,g5)
    c: Horizontal(g11)
    c: Coincident(g12,g0)
    c: Vertical(g12)
    c: Distance(g12) = 2.8
    c: Coincident(g13,g12)
    c: Vertical(g13)
    c: Distance(g13) = 6.3
    c: Coincident(g14,g13)
    c: Horizontal(g14)
    c: Distance(g14) = 2
    c: Vertical(g15)
    c: Distance(g15) = 3
    c: Block(g11)
    c: Coincident(g15,g11)
    c: Coincident(g16,g15)
    c: Horizontal(g16)
    c: Coincident(g17,g16)
    c: Coincident(g17,g14)
    c: Vertical(g17)
FEATURE [Part::Revolution] Revolve040  label="backCaseScrewRetainer001"
  Angle = 360
  Axis = (0,1,0)
  Base = (0,0,0)
  FaceMakerClass = Part::FaceMakerBullseye
  Placement = pos=(12.5,3,10) rot=(0,0,1;0rad)
  Solid = false
  Source = -> Face036
  Symmetric = false
FEATURE [Part::Feature] Face055
  shape: bbox 3.5 x 30.2 x 2e-07 mm, 1 faces, 0 solids (baked)
FEATURE [Part::Revolution] Revolve059  label="backCaseScrewPost"
  Angle = 360
  Axis = (0,1,0)
  Base = (0,0,0)
  FaceMakerClass = Part::FaceMakerBullseye
  Placement = pos=(12.5,4.5,10) rot=(0,0,1;0rad)
  Solid = false
  Source = -> Face055
  Symmetric = false
FEATURE [Part::Feature] Face056
  shape: bbox 3.5 x 30.2 x 2e-07 mm, 1 faces, 0 solids (baked)
FEATURE [Part::Revolution] Revolve060  label="backCaseScrewPost001"
  Angle = 360
  Axis = (0,1,0)
  Base = (0,0,0)
  FaceMakerClass = Part::FaceMakerBullseye
  Placement = pos=(12.5,4.5,62) rot=(0,0,1;0rad)
  Solid = false
  Source = -> Face056
  Symmetric = false
FEATURE [Part::Feature] Face057
  shape: bbox 3.5 x 17.8 x 2e-07 mm, 1 faces, 0 solids (baked)
FEATURE [Part::Revolution] Revolve061  label="removeToCreateScrewAndThreadedInsertHole"
  Angle = 360
  Axis = (0,1,0)
  Base = (0,0,0)
  FaceMakerClass = Part::FaceMakerBullseye
  Placement = pos=(12.5,0,10) rot=(0,0,1;0rad)
  Solid = false
  Source = -> Face057
  Symmetric = false
FEATURE [Part::Feature] Face058
  shape: bbox 3.5 x 17.8 x 2e-07 mm, 1 faces, 0 solids (baked)
FEATURE [Part::Revolution] Revolve062  label="removeToCreateScrewAndThreadedInsertHole001"
  Angle = 360
  Axis = (0,1,0)
  Base = (0,0,0)
  FaceMakerClass = Part::FaceMakerBullseye
  Placement = pos=(12.5,0,62) rot=(0,0,1;0rad)
  Solid = false
  Source = -> Face058
  Symmetric = false
FEATURE [Part::Feature] Face059
  shape: bbox 3.5 x 17.8 x 2e-07 mm, 1 faces, 0 solids (baked)
FEATURE [Part::Revolution] Revolve063  label="removeToCreateScrewAndThreadedInsertHole002"
  Angle = 360
  Axis = (0,1,0)
  Base = (0,0,0)
  FaceMakerClass = Part::FaceMakerBullseye
  Placement = pos=(89.5,0,68.5) rot=(0,0,1;0rad)
  Solid = false
  Source = -> Face059
  Symmetric = false
FEATURE [Part::Feature] Face060
  shape: bbox 3.5 x 17.8 x 2e-07 mm, 1 faces, 0 solids (baked)
FEATURE [Part::Revolution] Revolve064  label="removeToCreateScrewAndThreadedInsertHole003"
  Angle = 360
  Axis = (0,1,0)
  Base = (0,0,0)
  FaceMakerClass = Part::FaceMakerBullseye
  Placement = pos=(89.5,0,3.5) rot=(0,0,1;0rad)
  Solid = false
  Source = -> Face060
  Symmetric = false
FEATURE [Part::Feature] Face061
  shape: bbox 3.5 x 17.8 x 2e-07 mm, 1 faces, 0 solids (baked)
FEATURE [Part::Revolution] Revolve065  label="removeToCreateScrewAndThreadedInsertHole004"
  Angle = 360
  Axis = (0,1,0)
  Base = (0,0,0)
  FaceMakerClass = Part::FaceMakerBullseye
  Placement = pos=(102.5,4.7,3.5) rot=(0,0,1;0rad)
  Solid = false
  Source = -> Face061
  Symmetric = false
FEATURE [Part::Feature] Face062
  shape: bbox 3.5 x 17.8 x 2e-07 mm, 1 faces, 0 solids (baked)
FEATURE [Part::Revolution] Revolve066  label="removeToCreateScrewAndThreadedInsertHole005"
  Angle = 360
  Axis = (0,1,0)
  Base = (0,0,0)
  FaceMakerClass = Part::FaceMakerBullseye
  Placement = pos=(102.5,4.7,68.5) rot=(0,0,1;0rad)
  Solid = false
  Source = -> Face062
  Symmetric = false
FEATURE [Part::MultiFuse] Fusion047  label="makeHoles"
  Shapes = -> [Revolve066,Revolve065,Revolve064,Revolve063,Revolve062,Revolve061]
FEATURE [Part::Feature] Face063
  shape: bbox 3.6 x 3.2 x 2e-07 mm, 1 faces, 0 solids (baked)
FEATURE [Part::Revolution] Revolve067  label="moreFrontCaseScrewRetainer002"
  Angle = 360
  Axis = (0,1,0)
  Base = (0,0,0)
  FaceMakerClass = Part::FaceMakerBullseye
  Placement = pos=(102.5,4.5,68.5) rot=(0,0,1;0rad)
  Solid = false
  Source = -> Face063
  Symmetric = false
FEATURE [Part::Feature] Face064
  shape: bbox 3.6 x 3.2 x 2e-07 mm, 1 faces, 0 solids (baked)
FEATURE [Part::Revolution] Revolve068  label="moreFrontCaseScrewRetainer003"
  Angle = 360
  Axis = (0,1,0)
  Base = (0,0,0)
  FaceMakerClass = Part::FaceMakerBullseye
  Placement = pos=(102.5,4.5,3.5) rot=(0,0,1;0rad)
  Solid = false
  Source = -> Face064
  Symmetric = false
FEATURE [Part::Feature] Face065
  shape: bbox 3.5 x 17.8 x 2e-07 mm, 1 faces, 0 solids (baked)
FEATURE [Part::Revolution] Revolve069  label="removeToCreateScrewAndThreadedInsertHole006"
  Angle = 360
  Axis = (0,1,0)
  Base = (0,0,0)
  FaceMakerClass = Part::FaceMakerBullseye
  Placement = pos=(12.5,0,10) rot=(0,0,1;0rad)
  Solid = false
  Source = -> Face065
  Symmetric = false
FEATURE [Part::Feature] Face066
  shape: bbox 3.5 x 17.8 x 2e-07 mm, 1 faces, 0 solids (baked)
FEATURE [Part::Revolution] Revolve070  label="removeToCreateScrewAndThreadedInsertHole007"
  Angle = 360
  Axis = (0,1,0)
  Base = (0,0,0)
  FaceMakerClass = Part::FaceMakerBullseye
  Placement = pos=(12.5,0,62) rot=(0,0,1;0rad)
  Solid = false
  Source = -> Face066
  Symmetric = false
FEATURE [Part::Feature] Face067
  shape: bbox 3.5 x 17.8 x 2e-07 mm, 1 faces, 0 solids (baked)
FEATURE [Part::Revolution] Revolve071  label="removeToCreateScrewAndThreadedInsertHole008"
  Angle = 360
  Axis = (0,1,0)
  Base = (0,0,0)
  FaceMakerClass = Part::FaceMakerBullseye
  Placement = pos=(89.5,0,68.5) rot=(0,0,1;0rad)
  Solid = false
  Source = -> Face067
  Symmetric = false
FEATURE [Part::Feature] Face068
  shape: bbox 3.5 x 17.8 x 2e-07 mm, 1 faces, 0 solids (baked)
FEATURE [Part::Revolution] Revolve072  label="removeToCreateScrewAndThreadedInsertHole009"
  Angle = 360
  Axis = (0,1,0)
  Base = (0,0,0)
  FaceMakerClass = Part::FaceMakerBullseye
  Placement = pos=(89.5,0,3.5) rot=(0,0,1;0rad)
  Solid = false
  Source = -> Face068
  Symmetric = false
FEATURE [Part::Feature] Face069
  shape: bbox 3.5 x 17.8 x 2e-07 mm, 1 faces, 0 solids (baked)
FEATURE [Part::Feature] Face070
  shape: bbox 3.5 x 17.8 x 2e-07 mm, 1 faces, 0 solids (baked)
FEATURE [Part::Revolution] Revolve073  label="removeToCreateScrewAndThreadedInsertHole010"
  Angle = 360
  Axis = (0,1,0)
  Base = (0,0,0)
  FaceMakerClass = Part::FaceMakerBullseye
  Placement = pos=(102.5,4.7,3.5) rot=(0,0,1;0rad)
  Solid = false
  Source = -> Face069
  Symmetric = false
FEATURE [Part::Revolution] Revolve074  label="removeToCreateScrewAndThreadedInsertHole011"
  Angle = 360
  Axis = (0,1,0)
  Base = (0,0,0)
  FaceMakerClass = Part::FaceMakerBullseye
  Placement = pos=(102.5,4.7,68.5) rot=(0,0,1;0rad)
  Solid = false
  Source = -> Face070
  Symmetric = false
FEATURE [Part::MultiFuse] Fusion048  label="makeHoles001"
  Shapes = -> [Revolve074,Revolve073,Revolve072,Revolve071,Revolve070,Revolve069]
FEATURE [Part::MultiFuse] Fusion049  label="caseScrewRetainers"
  Shapes = -> [Revolve067,Revolve068,Revolve048,Revolve047,Revolve039,Revolve040]
FEATURE [Part::Cut] Cut015  label="caseScrewRetainers001"
  Base = -> Fusion049
  Tool = -> Fusion048
FEATURE [Part::MultiFuse] Fusion050  label="casePillars"
  Shapes = -> [Revolve055,Revolve054,Revolve043,Revolve046,Revolve059,Revolve060]
FEATURE [Part::Feature] Face071 .. Face076  x6 (patterned run collapsed; names and placements below)
  shape: bbox 3.5 x 17.8 x 2e-07 mm, 1 faces, 0 solids (baked)
FEATURE [Part::Revolution] Revolve075  label="removeToCreateScrewAndThreadedInsertHole012"
  Angle = 360
  Axis = (0,1,0)
  Base = (0,0,0)
  FaceMakerClass = Part::FaceMakerBullseye
  Placement = pos=(12.5,0,10) rot=(0,0,1;0rad)
  Solid = false
  Source = -> Face071
  Symmetric = false
FEATURE [Part::Revolution] Revolve076  label="removeToCreateScrewAndThreadedInsertHole013"
  Angle = 360
  Axis = (0,1,0)
  Base = (0,0,0)
  FaceMakerClass = Part::FaceMakerBullseye
  Placement = pos=(12.5,0,62) rot=(0,0,1;0rad)
  Solid = false
  Source = -> Face072
  Symmetric = false
FEATURE [Part::Revolution] Revolve077  label="removeToCreateScrewAndThreadedInsertHole014"
  Angle = 360
  Axis = (0,1,0)
  Base = (0,0,0)
  FaceMakerClass = Part::FaceMakerBullseye
  Placement = pos=(89.5,0,68.5) rot=(0,0,1;0rad)
  Solid = false
  Source = -> Face073
  Symmetric = false
FEATURE [Part::Revolution] Revolve078  label="removeToCreateScrewAndThreadedInsertHole015"
  Angle = 360
  Axis = (0,1,0)
  Base = (0,0,0)
  FaceMakerClass = Part::FaceMakerBullseye
  Placement = pos=(89.5,0,3.5) rot=(0,0,1;0rad)
  Solid = false
  Source = -> Face074
  Symmetric = false
FEATURE [Part::Revolution] Revolve079  label="removeToCreateScrewAndThreadedInsertHole016"
  Angle = 360
  Axis = (0,1,0)
  Base = (0,0,0)
  FaceMakerClass = Part::FaceMakerBullseye
  Placement = pos=(102.5,4.7,3.5) rot=(0,0,1;0rad)
  Solid = false
  Source = -> Face075
  Symmetric = false
FEATURE [Part::Revolution] Revolve080  label="removeToCreateScrewAndThreadedInsertHole017"
  Angle = 360
  Axis = (0,1,0)
  Base = (0,0,0)
  FaceMakerClass = Part::FaceMakerBullseye
  Placement = pos=(102.5,4.7,68.5) rot=(0,0,1;0rad)
  Solid = false
  Source = -> Face076
  Symmetric = false
FEATURE [Part::MultiFuse] Fusion051  label="makeHoles002"
  Shapes = -> [Revolve080,Revolve079,Revolve078,Revolve077,Revolve076,Revolve075]
FEATURE [Part::Cut] Cut016  label="caesPillars"
  Base = -> Fusion050
  Tool = -> Fusion051
FEATURE [Part::Revolution] Revolve009  label="plugHousing016"
  Angle = 360
  Axis = (0,1,0)
  Base = (0,0,0)
  FaceMakerClass = Part::FaceMakerBullseye
  Placement = pos=(0,0,36.15) rot=(0,0,1;0rad)
  Solid = false
  Source = -> Face012
  Symmetric = false
FEATURE [Part::MultiFuse] Fusion014  label="plugHousing023"
  Placement = pos=(0,0,0) rot=(0,0,1;1.5708rad)
  Shapes = -> [Revolve011,Revolve009]
FEATURE [Part::Revolution] Revolve010  label="plugHousing017"
  Angle = 360
  Axis = (0,1,0)
  Base = (0,0,0)
  FaceMakerClass = Part::FaceMakerBullseye
  Placement = pos=(0,0,36.15) rot=(0,0,1;0rad)
  Solid = false
  Source = -> Face014
  Symmetric = false
FEATURE [Part::MultiFuse] Fusion015  label="plugHousing024"
  Placement = pos=(0,0,0) rot=(0,0,1;1.5708rad)
  Shapes = -> [Revolve010,Revolve015]
FEATURE [Part::Revolution] Revolve014  label="plugHousing026"
  Angle = 360
  Axis = (0,1,0)
  Base = (0,0,0)
  FaceMakerClass = Part::FaceMakerBullseye
  Placement = pos=(0,0,36.15) rot=(0,0,1;0rad)
  Solid = false
  Source = -> Face011
  Symmetric = false
FEATURE [Part::Revolution] Revolve013  label="plugHousing025"
  Angle = 360
  Axis = (0,1,0)
  Base = (0,0,0)
  FaceMakerClass = Part::FaceMakerBullseye
  Placement = pos=(0,0,36.15) rot=(0,0,1;0rad)
  Solid = false
  Source = -> Face015
  Symmetric = false
FEATURE [Part::MultiFuse] Fusion016  label="plugHousing028"
  Placement = pos=(0,19,0) rot=(0,0,1;3.14159rad)
  Shapes = -> [Fusion014,Fusion013]
FEATURE [Part::MultiFuse] Fusion011  label="plugHousing018"
  Placement = pos=(0,0,0) rot=(0,0,1;1.5708rad)
  Shapes = -> [Revolve014,Revolve013]
FEATURE [Part::MultiFuse] Fusion012  label="plugHousing019"
  Placement = pos=(0,19,0) rot=(0,0,1;3.14159rad)
  Shapes = -> [Fusion011,Fusion015]
FEATURE [Part::MultiFuse] Fusion017  label="plugHousing029"
  Placement = pos=(122.621,0,-0.15) rot=(0,0,1;0rad)
  Shapes = -> [Fusion016,Fusion012]
FEATURE [Part::MultiFuse] Fusion052  label="casePillarRetainers"
  Shapes = -> [Extrude012,Extrude013,Extrude014,Extrude015,Extrude016,Extrude017,Extrude018,Extrude019,Box011,Box012]
FEATURE [Part::Feature] Face077
  shape: bbox 3.5 x 17.8 x 2e-07 mm, 1 faces, 0 solids (baked)
FEATURE [Part::Revolution] Revolve081  label="removeToCreateScrewAndThreadedInsertHole018"
  Angle = 360
  Axis = (0,1,0)
  Base = (0,0,0)
  FaceMakerClass = Part::FaceMakerBullseye
  Placement = pos=(62.3,30.3,19.7) rot=(0,0,1;0rad)
  Solid = false
  Source = -> Face077
  Symmetric = false
FEATURE [Part::Feature] Face078
  shape: bbox 3.5 x 17.8 x 2e-07 mm, 1 faces, 0 solids (baked)
FEATURE [Part::Revolution] Revolve082  label="removeToCreateScrewAndThreadedInsertHole019"
  Angle = 360
  Axis = (0,1,0)
  Base = (0,0,0)
  FaceMakerClass = Part::FaceMakerBullseye
  Placement = pos=(62.3,30.3,51.7) rot=(0,0,1;0rad)
  Solid = false
  Source = -> Face078
  Symmetric = false
FEATURE [Part::Feature] Face079
  shape: bbox 3.5 x 17.8 x 2e-07 mm, 1 faces, 0 solids (baked)
FEATURE [Part::Revolution] Revolve083  label="removeToCreateScrewAndThreadedInsertHole020"
  Angle = 360
  Axis = (0,1,0)
  Base = (0,0,0)
  FaceMakerClass = Part::FaceMakerBullseye
  Placement = pos=(30.3,30.3,19.7) rot=(0,0,1;0rad)
  Solid = false
  Source = -> Face079
  Symmetric = false
FEATURE [Part::Feature] Face080
  shape: bbox 3.5 x 17.8 x 2e-07 mm, 1 faces, 0 solids (baked)
FEATURE [Part::Revolution] Revolve084  label="removeToCreateScrewAndThreadedInsertHole021"
  Angle = 360
  Axis = (0,1,0)
  Base = (0,0,0)
  FaceMakerClass = Part::FaceMakerBullseye
  Placement = pos=(30.3,30.3,51.7) rot=(0,0,1;0rad)
  Solid = false
  Source = -> Face080
  Symmetric = false
FEATURE [Part::MultiFuse] Fusion053  label="createThreadedInsertHolesForFan"
  Shapes = -> [Revolve081,Revolve082,Revolve083,Revolve084]
FEATURE [Part::Cut] Cut017  label="fanScrewHousing001"
  Base = -> Fusion046
  Tool = -> Fusion053
FEATURE [Part::Feature] Face081
  shape: bbox 3.5 x 17.8 x 2e-07 mm, 1 faces, 0 solids (baked)
FEATURE [Part::Revolution] Revolve085  label="removeToCreateScrewAndThreadedInsertHole022"
  Angle = 360
  Axis = (0,1,0)
  Base = (0,0,0)
  FaceMakerClass = Part::FaceMakerBullseye
  Placement = pos=(62.3,30.3,19.7) rot=(0,0,1;0rad)
  Solid = false
  Source = -> Face081
  Symmetric = false
FEATURE [Part::Feature] Face082
  shape: bbox 3.5 x 17.8 x 2e-07 mm, 1 faces, 0 solids (baked)
FEATURE [Part::Revolution] Revolve086  label="removeToCreateScrewAndThreadedInsertHole023"
  Angle = 360
  Axis = (0,1,0)
  Base = (0,0,0)
  FaceMakerClass = Part::FaceMakerBullseye
  Placement = pos=(62.3,30.3,51.7) rot=(0,0,1;0rad)
  Solid = false
  Source = -> Face082
  Symmetric = false
FEATURE [Part::Feature] Face083
  shape: bbox 3.5 x 17.8 x 2e-07 mm, 1 faces, 0 solids (baked)
FEATURE [Part::Revolution] Revolve087  label="removeToCreateScrewAndThreadedInsertHole024"
  Angle = 360
  Axis = (0,1,0)
  Base = (0,0,0)
  FaceMakerClass = Part::FaceMakerBullseye
  Placement = pos=(30.3,30.3,19.7) rot=(0,0,1;0rad)
  Solid = false
  Source = -> Face083
  Symmetric = false
FEATURE [Part::Feature] Face084
  shape: bbox 3.5 x 17.8 x 2e-07 mm, 1 faces, 0 solids (baked)
FEATURE [Part::Revolution] Revolve088  label="removeToCreateScrewAndThreadedInsertHole025"
  Angle = 360
  Axis = (0,1,0)
  Base = (0,0,0)
  FaceMakerClass = Part::FaceMakerBullseye
  Placement = pos=(30.3,30.3,51.7) rot=(0,0,1;0rad)
  Solid = false
  Source = -> Face084
  Symmetric = false
FEATURE [Part::MultiFuse] Fusion054  label="createThreadedInsertHolesForFan001"
  Shapes = -> [Revolve085,Revolve086,Revolve087,Revolve088]
FEATURE [Part::Cut] Cut018  label="top007"
  Base = -> Fusion040
  Tool = -> Fusion054
FEATURE [Sketcher::SketchObject] Sketch029
  FullyConstrained = false
  Placement = pos=(0,0,0) rot=(1,0,0;1.5708rad)
  sketch-geometry (24):
    g0: ArcOfCircle CenterX=-4 CenterY=-10.5 CenterZ=0 NormalX=0 NormalY=0 NormalZ=1 AngleXU=0 Radius=1.5 StartAngle=6e-16 EndAngle=3.14159
    g1: ArcOfCircle CenterX=-34.2 CenterY=-10.5 CenterZ=0 NormalX=0 NormalY=0 NormalZ=1 AngleXU=0 Radius=1.5 StartAngle=0 EndAngle=3.14159
    g2: ArcOfCircle CenterX=-34.2 CenterY=-27.7 CenterZ=0 NormalX=0 NormalY=0 NormalZ=1 AngleXU=0 Radius=1.5 StartAngle=3.14159 EndAngle=6.28319
    g3: ArcOfCircle CenterX=-4 CenterY=-27.7 CenterZ=0 NormalX=0 NormalY=0 NormalZ=1 AngleXU=0 Radius=1.5 StartAngle=3.1416 EndAngle=6.28319
    g4: ArcOfCircle CenterX=-10 CenterY=-4.3 CenterZ=0 NormalX=0 NormalY=0 NormalZ=1 AngleXU=0 Radius=1.5 StartAngle=2e-16 EndAngle=3.14159
    g5: ArcOfCircle CenterX=-16.1 CenterY=-1.8 CenterZ=0 NormalX=0 NormalY=0 NormalZ=1 AngleXU=0 Radius=1.5 StartAngle=5e-16 EndAngle=3.14159
    g6: ArcOfCircle CenterX=-22.1 CenterY=-1.8 CenterZ=0 NormalX=0 NormalY=0 NormalZ=1 AngleXU=0 Radius=1.5 StartAngle=5e-16 EndAngle=3.14159
    g7: ArcOfCircle CenterX=-28.2 CenterY=-4.3 CenterZ=0 NormalX=0 NormalY=0 NormalZ=1 AngleXU=0 Radius=1.5 StartAngle=2e-16 EndAngle=3.14159
    g8: ArcOfCircle CenterX=-10 CenterY=-33.9 CenterZ=0 NormalX=0 NormalY=0 NormalZ=1 AngleXU=0 Radius=1.5 StartAngle=3.14159 EndAngle=6.28319
    g9: ArcOfCircle CenterX=-16.1 CenterY=-36.4 CenterZ=0 NormalX=0 NormalY=0 NormalZ=1 AngleXU=0 Radius=1.5 StartAngle=3.14159 EndAngle=6.28319
    g10: ArcOfCircle CenterX=-22.1 CenterY=-36.4 CenterZ=0 NormalX=0 NormalY=0 NormalZ=1 AngleXU=0 Radius=1.5 StartAngle=3.14159 EndAngle=6.28319
    g11: ArcOfCircle CenterX=-28.2 CenterY=-33.9 CenterZ=0 NormalX=0 NormalY=0 NormalZ=1 AngleXU=0 Radius=1.5 StartAngle=3.14159 EndAngle=6.28319
    g12: LineSegment StartX=-35.7 StartY=-10.5 StartZ=0 EndX=-35.7 EndY=-27.7 EndZ=0
    g13: LineSegment StartX=-32.7 StartY=-10.5 StartZ=0 EndX=-32.7 EndY=-27.7 EndZ=0
    g14: LineSegment StartX=-29.7 StartY=-33.9 StartZ=0 EndX=-29.7 EndY=-4.3 EndZ=0
    g15: LineSegment StartX=-26.7 StartY=-33.9 StartZ=0 EndX=-26.7 EndY=-4.3 EndZ=0
    g16: LineSegment StartX=-2.5 StartY=-10.5 StartZ=0 EndX=-2.5 EndY=-27.7 EndZ=0
    g17: LineSegment StartX=-8.5 StartY=-4.3 StartZ=0 EndX=-8.5 EndY=-33.9 EndZ=0
    g18: LineSegment StartX=-5.5 StartY=-10.5 StartZ=0 EndX=-5.5 EndY=-27.7 EndZ=0
    g19: LineSegment StartX=-11.5 StartY=-4.3 StartZ=0 EndX=-11.5 EndY=-33.9 EndZ=0
    g20: LineSegment StartX=-14.6 StartY=-1.8 StartZ=0 EndX=-14.6 EndY=-36.4 EndZ=0
    g21: LineSegment StartX=-17.6 StartY=-1.8 StartZ=0 EndX=-17.6 EndY=-36.4 EndZ=0
    g22: LineSegment StartX=-20.6 StartY=-36.4 StartZ=0 EndX=-20.6 EndY=-1.8 EndZ=0
    g23: LineSegment StartX=-23.6 StartY=-1.8 StartZ=0 EndX=-23.6 EndY=-36.4 EndZ=0
  constraints (48):
    c: Block(g0)
    c: Block(g1)
    c: Block(g2)
    c: Block(g3)
    c: Block(g4)
    c: Block(g5)
    c: Block(g6)
    c: Block(g7)
    c: Block(g8)
    c: Block(g9)
    c: Block(g10)
    c: Block(g11)
    c: Coincident(g12,g1)
    c: Coincident(g12,g2)
    c: Vertical(g12)
    c: Coincident(g13,g1)
    c: Coincident(g13,g2)
    c: Vertical(g13)
    c: Coincident(g14,g11)
    c: Coincident(g14,g7)
    c: Vertical(g14)
    c: Coincident(g15,g11)
    c: Coincident(g15,g7)
    c: Vertical(g15)
    c: Coincident(g16,g0)
    c: Coincident(g16,g3)
    c: Vertical(g16)
    c: Coincident(g17,g4)
    c: Coincident(g17,g8)
    c: Vertical(g17)
    c: Coincident(g18,g0)
    c: Coincident(g18,g3)
    c: Vertical(g18)
    c: Coincident(g19,g4)
    c: Coincident(g19,g8)
    c: Vertical(g19)
    c: Coincident(g20,g5)
    c: Coincident(g20,g9)
    c: Vertical(g20)
    c: Coincident(g21,g5)
    c: Coincident(g21,g9)
    c: Vertical(g21)
    c: Coincident(g22,g10)
    c: Coincident(g22,g6)
    c: Vertical(g22)
    c: Coincident(g23,g6)
    c: Coincident(g23,g10)
    c: Vertical(g23)
FEATURE [Part::Extrusion] Extrude020  label="removeToCreateFanGrillHoles"
  Base = -> Sketch029
  Dir = (0,-1,6e-16)
  DirMode = 2
  FaceMakerClass = Part::FaceMakerBullseye
  LengthFwd = 10
  LengthRev = 0
  Placement = pos=(65.4,44,54.82) rot=(0,0,1;0rad)
  Solid = true
  Symmetric = false
FEATURE [Part::MultiFuse] Fusion055  label="top008"
  Shapes = -> [Cut017,Cut018]
FEATURE [Part::Cut] Cut019  label="top009"
  Base = -> Fusion055
  Tool = -> Extrude020
FEATURE [App::MeasureDistance] Distance003  label="Distance: 71.95 mm"
  Distance = 71.9513
  P1 = (117,38,72)
  P2 = (117,38,0.0487319)
FEATURE [Sketcher::SketchObject] Sketch030
  FullyConstrained = true
  Placement = pos=(117,19,0) rot=(0.57735,0.57735,0.57735;2.0944rad)
  sketch-geometry (48):
    g0: LineSegment StartX=-49.19 StartY=69.25 StartZ=0 EndX=-49.19 EndY=66.25 EndZ=0
    g1: LineSegment StartX=-49.19 StartY=63.5 StartZ=0 EndX=-49.19 EndY=60.5 EndZ=0
    g2: LineSegment StartX=-49.19 StartY=57.75 StartZ=0 EndX=-49.19 EndY=54.75 EndZ=0
    g3: LineSegment StartX=-49.19 StartY=52 StartZ=0 EndX=-49.19 EndY=49 EndZ=0
    g4: LineSegment StartX=-49.19 StartY=46.25 StartZ=0 EndX=-49.19 EndY=43.25 EndZ=0
    g5: LineSegment StartX=-49.19 StartY=40.5 StartZ=0 EndX=-49.19 EndY=37.5 EndZ=0
    g6: LineSegment StartX=-49.19 StartY=34.5 StartZ=0 EndX=-49.19 EndY=31.5 EndZ=0
    g7: LineSegment StartX=-49.19 StartY=28.75 StartZ=0 EndX=-49.19 EndY=25.75 EndZ=0
    g8: LineSegment StartX=-49.19 StartY=23 StartZ=0 EndX=-49.19 EndY=20 EndZ=0
    g9: LineSegment StartX=-49.19 StartY=17.25 StartZ=0 EndX=-49.19 EndY=14.25 EndZ=0
    g10: LineSegment StartX=-49.19 StartY=11.5 StartZ=0 EndX=-49.19 EndY=8.5 EndZ=0
    g11: LineSegment StartX=-49.19 StartY=5.75 StartZ=0 EndX=-49.19 EndY=2.75 EndZ=0
    g12: ArcOfCircle CenterX=-1.5 CenterY=67.75 CenterZ=0 NormalX=0 NormalY=0 NormalZ=1 AngleXU=0 Radius=1.5 StartAngle=4.71239 EndAngle=7.85398
    g13: ArcOfCircle CenterX=-1.5 CenterY=62 CenterZ=0 NormalX=0 NormalY=0 NormalZ=1 AngleXU=0 Radius=1.5 StartAngle=4.71239 EndAngle=7.85398
    g14: ArcOfCircle CenterX=-1.5 CenterY=56.25 CenterZ=0 NormalX=0 NormalY=0 NormalZ=1 AngleXU=0 Radius=1.5 StartAngle=4.71239 EndAngle=7.85398
    g15: ArcOfCircle CenterX=-11.49 CenterY=50.5 CenterZ=0 NormalX=0 NormalY=0 NormalZ=1 AngleXU=0 Radius=1.5 StartAngle=4.71239 EndAngle=7.85398
    g16: ArcOfCircle CenterX=-16.28 CenterY=44.75 CenterZ=0 NormalX=0 NormalY=0 NormalZ=1 AngleXU=0 Radius=1.5 StartAngle=4.71239 EndAngle=7.85398
    g17: ArcOfCircle CenterX=-18.2337 CenterY=39 CenterZ=0 NormalX=0 NormalY=0 NormalZ=1 AngleXU=0 Radius=1.5 StartAngle=4.71485 EndAngle=7.85398
    g18: ArcOfCircle CenterX=-16.2837 CenterY=27.25 CenterZ=0 NormalX=0 NormalY=0 NormalZ=1 AngleXU=0 Radius=1.5 StartAngle=4.71485 EndAngle=7.85398
    g19: ArcOfCircle CenterX=-18.2337 CenterY=33 CenterZ=0 NormalX=0 NormalY=0 NormalZ=1 AngleXU=0 Radius=1.5 StartAngle=4.71485 EndAngle=7.85398
    g20: ArcOfCircle CenterX=-11.49 CenterY=21.5 CenterZ=0 NormalX=0 NormalY=0 NormalZ=1 AngleXU=0 Radius=1.5 StartAngle=4.71239 EndAngle=7.85398
    g21: ArcOfCircle CenterX=-1.5 CenterY=4.25 CenterZ=0 NormalX=0 NormalY=0 NormalZ=1 AngleXU=0 Radius=1.5 StartAngle=4.71239 EndAngle=7.85398
    g22: ArcOfCircle CenterX=-1.5 CenterY=10 CenterZ=0 NormalX=0 NormalY=0 NormalZ=1 AngleXU=0 Radius=1.5 StartAngle=4.71239 EndAngle=7.85398
    g23: ArcOfCircle CenterX=-1.5 CenterY=15.75 CenterZ=0 NormalX=0 NormalY=0 NormalZ=1 AngleXU=0 Radius=1.5 StartAngle=4.71239 EndAngle=7.85398
    g24: LineSegment StartX=-49.19 StartY=69.25 StartZ=0 EndX=-1.5 EndY=69.25 EndZ=0
    g25: LineSegment StartX=-49.19 StartY=66.25 StartZ=0 EndX=-1.5 EndY=66.25 EndZ=0
    g26: LineSegment StartX=-49.19 StartY=63.5 StartZ=0 EndX=-1.5 EndY=63.5 EndZ=0
    g27: LineSegment StartX=-49.19 StartY=60.5 StartZ=0 EndX=-1.5 EndY=60.5 EndZ=0
    g28: LineSegment StartX=-49.19 StartY=57.75 StartZ=0 EndX=-1.5 EndY=57.75 EndZ=0
    g29: LineSegment StartX=-49.19 StartY=54.75 StartZ=0 EndX=-1.5 EndY=54.75 EndZ=0
    g30: LineSegment StartX=-49.19 StartY=52 StartZ=0 EndX=-11.49 EndY=52 EndZ=0
    g31: LineSegment StartX=-49.19 StartY=49 StartZ=0 EndX=-11.49 EndY=49 EndZ=0
    g32: LineSegment StartX=-49.19 StartY=46.25 StartZ=0 EndX=-16.28 EndY=46.25 EndZ=0
    g33: LineSegment StartX=-49.19 StartY=43.25 StartZ=0 EndX=-16.28 EndY=43.25 EndZ=0
    g34: LineSegment StartX=-49.19 StartY=40.5 StartZ=0 EndX=-18.2337 EndY=40.5 EndZ=0
    g35: LineSegment StartX=-49.19 StartY=37.5 StartZ=0 EndX=-18.23 EndY=37.5 EndZ=0
    g36: LineSegment StartX=-49.19 StartY=34.5 StartZ=0 EndX=-18.2337 EndY=34.5 EndZ=0
    g37: LineSegment StartX=-49.19 StartY=31.5 StartZ=0 EndX=-18.23 EndY=31.5 EndZ=0
    g38: LineSegment StartX=-49.19 StartY=28.75 StartZ=0 EndX=-16.2837 EndY=28.75 EndZ=0
    g39: LineSegment StartX=-49.19 StartY=25.75 StartZ=0 EndX=-16.28 EndY=25.75 EndZ=0
    g40: LineSegment StartX=-49.19 StartY=23 StartZ=0 EndX=-11.49 EndY=23 EndZ=0
    g41: LineSegment StartX=-49.19 StartY=20 StartZ=0 EndX=-11.49 EndY=20 EndZ=0
    g42: LineSegment StartX=-49.19 StartY=17.25 StartZ=0 EndX=-1.5 EndY=17.25 EndZ=0
    g43: LineSegment StartX=-49.19 StartY=14.25 StartZ=0 EndX=-1.5 EndY=14.25 EndZ=0
    g44: LineSegment StartX=-49.19 StartY=11.5 StartZ=0 EndX=-1.5 EndY=11.5 EndZ=0
    g45: LineSegment StartX=-49.19 StartY=8.5 StartZ=0 EndX=-1.5 EndY=8.5 EndZ=0
    g46: LineSegment StartX=-49.19 StartY=5.75 StartZ=0 EndX=-1.5 EndY=5.75 EndZ=0
    g47: LineSegment StartX=-49.19 StartY=2.75 StartZ=0 EndX=-1.5 EndY=2.75 EndZ=0
  constraints (120):
    c: Vertical(g0)
    c: Distance(g0) = 3
    c: Block(g0)
    c: Vertical(g1)
    c: Distance(g1) = 3
    c: Vertical(g2)
    c: Equal(g0,g2) = 3
    c: Block(g2)
    c: Vertical(g3)
    c: Equal(g1,g3) = 3
    c: Vertical(g4)
    c: Equal(g0,g4) = 3
    c: Block(g4)
    c: Vertical(g5)
    c: Equal(g1,g5) = 3
    c: Vertical(g6)
    c: Equal(g0,g6) = 3
    c: Block(g6)
    c: Vertical(g7)
    c: Equal(g1,g7) = 3
    c: Vertical(g8)
    c: Equal(g0,g8) = 3
    c: Block(g8)
    c: Vertical(g9)
    c: Equal(g1,g9) = 3
    c: Vertical(g10)
    c: Equal(g0,g10) = 3
    c: Block(g10)
    c: Vertical(g11)
    c: Equal(g1,g11) = 3
    c: Block(g12)
    c: Block(g13)
    c: Block(g14)
    c: Block(g15)
    c: Block(g16)
    c: Block(g17)
    c: Block(g18)
    c: Block(g19)
    c: Block(g20)
    c: Block(g21)
    c: Block(g22)
    c: Block(g23)
    c: Block(g11)
    c: Block(g9)
    c: Block(g7)
    c: Block(g5)
    c: Block(g3)
    c: Block(g1)
    c: Coincident(g24,g0)
    c: Coincident(g24,g12)
    c: Horizontal(g24)
    c: Coincident(g25,g0)
    c: Coincident(g25,g12)
    c: Horizontal(g25)
    c: Coincident(g26,g1)
    c: Coincident(g26,g13)
    c: Horizontal(g26)
    c: Coincident(g27,g1)
    c: Coincident(g27,g13)
    c: Horizontal(g27)
    c: Coincident(g28,g2)
    c: Coincident(g28,g14)
    c: Horizontal(g28)
    c: Coincident(g29,g2)
    c: Coincident(g29,g14)
    c: Horizontal(g29)
    c: Coincident(g30,g3)
    c: Coincident(g30,g15)
    c: Horizontal(g30)
    c: Coincident(g31,g3)
    c: Coincident(g31,g15)
    c: Horizontal(g31)
    c: Coincident(g32,g4)
    c: Coincident(g32,g16)
    c: Horizontal(g32)
    c: Coincident(g33,g4)
    c: Coincident(g33,g16)
    c: Horizontal(g33)
    c: Coincident(g34,g5)
    c: Coincident(g34,g17)
    c: Horizontal(g34)
    c: Coincident(g35,g5)
    c: Coincident(g35,g17)
    c: Horizontal(g35)
    c: Coincident(g36,g6)
    c: Coincident(g36,g19)
    c: Horizontal(g36)
    c: Coincident(g37,g6)
    c: Coincident(g37,g19)
    c: Horizontal(g37)
    c: Coincident(g38,g7)
    c: Coincident(g38,g18)
    c: Horizontal(g38)
    c: Coincident(g39,g7)
    c: Coincident(g39,g18)
    c: Horizontal(g39)
    c: Coincident(g40,g8)
    c: Coincident(g40,g20)
    c: Horizontal(g40)
    c: Coincident(g41,g8)
    c: Coincident(g41,g20)
    c: Horizontal(g41)
    c: Coincident(g42,g9)
    c: Coincident(g42,g23)
    c: Horizontal(g42)
    c: Coincident(g43,g9)
    c: Coincident(g43,g23)
    c: Horizontal(g43)
    c: Coincident(g44,g10)
    c: Coincident(g44,g22)
    c: Horizontal(g44)
    c: Coincident(g45,g10)
    c: Coincident(g45,g22)
    c: Horizontal(g45)
    c: Coincident(g46,g11)
    c: Coincident(g46,g21)
    c: Horizontal(g46)
    c: Coincident(g47,g11)
    c: Coincident(g47,g21)
    c: Horizontal(g47)
FEATURE [Sketcher::SketchObject] Sketch031
  FullyConstrained = true
  Placement = pos=(117,19,0) rot=(0.57735,0.57735,0.57735;2.0944rad)
  sketch-geometry (24):
    g0: ArcOfCircle CenterX=-49.19 CenterY=67.75 CenterZ=0 NormalX=0 NormalY=0 NormalZ=1 AngleXU=0 Radius=1.5 StartAngle=1.5708 EndAngle=4.71239
    g1: ArcOfCircle CenterX=-49.19 CenterY=62 CenterZ=0 NormalX=0 NormalY=0 NormalZ=1 AngleXU=0 Radius=1.5 StartAngle=1.5708 EndAngle=4.71239
    g2: ArcOfCircle CenterX=-49.19 CenterY=56.25 CenterZ=0 NormalX=0 NormalY=0 NormalZ=1 AngleXU=0 Radius=1.5 StartAngle=1.5708 EndAngle=4.71239
    g3: ArcOfCircle CenterX=-49.19 CenterY=50.5 CenterZ=0 NormalX=0 NormalY=0 NormalZ=1 AngleXU=0 Radius=1.5 StartAngle=1.5708 EndAngle=4.71239
    g4: ArcOfCircle CenterX=-49.19 CenterY=44.75 CenterZ=0 NormalX=0 NormalY=0 NormalZ=1 AngleXU=0 Radius=1.5 StartAngle=1.5708 EndAngle=4.71239
    g5: ArcOfCircle CenterX=-49.19 CenterY=39 CenterZ=0 NormalX=0 NormalY=0 NormalZ=1 AngleXU=0 Radius=1.5 StartAngle=1.5708 EndAngle=4.71239
    g6: ArcOfCircle CenterX=-49.19 CenterY=33 CenterZ=0 NormalX=0 NormalY=0 NormalZ=1 AngleXU=0 Radius=1.5 StartAngle=1.5708 EndAngle=4.71239
    g7: ArcOfCircle CenterX=-49.19 CenterY=27.25 CenterZ=0 NormalX=0 NormalY=0 NormalZ=1 AngleXU=0 Radius=1.5 StartAngle=1.5708 EndAngle=4.71239
    g8: ArcOfCircle CenterX=-49.19 CenterY=21.5 CenterZ=0 NormalX=0 NormalY=0 NormalZ=1 AngleXU=0 Radius=1.5 StartAngle=1.5708 EndAngle=4.71239
    g9: ArcOfCircle CenterX=-49.19 CenterY=15.75 CenterZ=0 NormalX=0 NormalY=0 NormalZ=1 AngleXU=0 Radius=1.5 StartAngle=1.5708 EndAngle=4.71239
    g10: ArcOfCircle CenterX=-49.19 CenterY=10 CenterZ=0 NormalX=0 NormalY=0 NormalZ=1 AngleXU=0 Radius=1.5 StartAngle=1.5708 EndAngle=4.71239
    g11: ArcOfCircle CenterX=-49.19 CenterY=4.25 CenterZ=0 NormalX=0 NormalY=0 NormalZ=1 AngleXU=0 Radius=1.5 StartAngle=1.5708 EndAngle=4.71239
    g12: LineSegment StartX=-49.19 StartY=69.25 StartZ=0 EndX=-49.19 EndY=66.25 EndZ=0
    g13: LineSegment StartX=-49.19 StartY=63.5 StartZ=0 EndX=-49.19 EndY=60.5 EndZ=0
    g14: LineSegment StartX=-49.19 StartY=57.75 StartZ=0 EndX=-49.19 EndY=54.75 EndZ=0
    g15: LineSegment StartX=-49.19 StartY=52 StartZ=0 EndX=-49.19 EndY=49 EndZ=0
    g16: LineSegment StartX=-49.19 StartY=46.25 StartZ=0 EndX=-49.19 EndY=43.25 EndZ=0
    g17: LineSegment StartX=-49.19 StartY=40.5 StartZ=0 EndX=-49.19 EndY=37.5 EndZ=0
    g18: LineSegment StartX=-49.19 StartY=34.5 StartZ=0 EndX=-49.19 EndY=31.5 EndZ=0
    g19: LineSegment StartX=-49.19 StartY=28.75 StartZ=0 EndX=-49.19 EndY=25.75 EndZ=0
    g20: LineSegment StartX=-49.19 StartY=23 StartZ=0 EndX=-49.19 EndY=20 EndZ=0
    g21: LineSegment StartX=-49.19 StartY=17.25 StartZ=0 EndX=-49.19 EndY=14.25 EndZ=0
    g22: LineSegment StartX=-49.19 StartY=11.5 StartZ=0 EndX=-49.19 EndY=8.5 EndZ=0
    g23: LineSegment StartX=-49.19 StartY=5.75 StartZ=0 EndX=-49.19 EndY=2.75 EndZ=0
  constraints (48):
    c: Block(g0)
    c: Block(g1)
    c: Block(g2)
    c: Block(g3)
    c: Block(g4)
    c: Block(g5)
    c: Block(g6)
    c: Block(g7)
    c: Block(g8)
    c: Block(g9)
    c: Block(g10)
    c: Block(g11)
    c: Coincident(g12,g0)
    c: Coincident(g12,g0)
    c: Vertical(g12)
    c: Vertical(g13)
    c: Coincident(g13,g1)
    c: Vertical(g14)
    c: Coincident(g14,g2)
    c: Vertical(g15)
    c: Coincident(g15,g3)
    c: Vertical(g16)
    c: Coincident(g16,g4)
    c: Vertical(g17)
    c: Coincident(g17,g5)
    c: Vertical(g18)
    c: Coincident(g18,g6)
    c: Vertical(g19)
    c: Coincident(g19,g7)
    c: Vertical(g20)
    c: Coincident(g20,g8)
    c: Vertical(g21)
    c: Coincident(g21,g9)
    c: Vertical(g22)
    c: Coincident(g22,g10)
    c: Vertical(g23)
    c: Coincident(g23,g11)
    c: Block(g23)
    c: Block(g22)
    c: Block(g21)
    c: Block(g20)
    c: Block(g13)
    c: Block(g14)
    c: Block(g15)
    c: Block(g16)
    c: Block(g17)
    c: Block(g18)
    c: Block(g19)
FEATURE [Part::Extrusion] Extrude022
  Base = -> Sketch030
  Dir = (1,-2e-16,2e-16)
  DirMode = 2
  FaceMakerClass = Part::FaceMakerBullseye
  LengthFwd = 19
  LengthRev = 0
  Placement = pos=(-19,0,0) rot=(0,0,1;0rad)
  Solid = true
  Symmetric = false
FEATURE [Part::Fillet] Fillet022
  Base = -> Extrude022
  Edges = 24 edges r=1.49: [Edge6,Edge11,Edge18,Edge23,Edge30,Edge35,Edge42,Edge47,Edge54,Edge59,Edge66,Edge71,Edge78,Edge83,Edge90,Edge95,Edge102,Edge107,Edge114,Edge119,Edge126,Edge131,Edge138,Edge143]
FEATURE [Part::Cut] Cut020  label="top010"
  Base = -> Cut019
  Tool = -> Fillet022
FEATURE [Sketcher::SketchObject] Sketch032
  FullyConstrained = true
  Placement = pos=(117,19,0) rot=(0.57735,0.57735,0.57735;2.0944rad)
  sketch-geometry (48):
    g0: LineSegment StartX=-49.19 StartY=69.25 StartZ=0 EndX=-49.19 EndY=66.25 EndZ=0
    g1: LineSegment StartX=-49.19 StartY=63.5 StartZ=0 EndX=-49.19 EndY=60.5 EndZ=0
    g2: LineSegment StartX=-49.19 StartY=57.75 StartZ=0 EndX=-49.19 EndY=54.75 EndZ=0
    g3: LineSegment StartX=-49.19 StartY=52 StartZ=0 EndX=-49.19 EndY=49 EndZ=0
    g4: LineSegment StartX=-49.19 StartY=46.25 StartZ=0 EndX=-49.19 EndY=43.25 EndZ=0
    g5: LineSegment StartX=-49.19 StartY=40.5 StartZ=0 EndX=-49.19 EndY=37.5 EndZ=0
    g6: LineSegment StartX=-49.19 StartY=34.5 StartZ=0 EndX=-49.19 EndY=31.5 EndZ=0
    g7: LineSegment StartX=-49.19 StartY=28.75 StartZ=0 EndX=-49.19 EndY=25.75 EndZ=0
    g8: LineSegment StartX=-49.19 StartY=23 StartZ=0 EndX=-49.19 EndY=20 EndZ=0
    g9: LineSegment StartX=-49.19 StartY=17.25 StartZ=0 EndX=-49.19 EndY=14.25 EndZ=0
    g10: LineSegment StartX=-49.19 StartY=11.5 StartZ=0 EndX=-49.19 EndY=8.5 EndZ=0
    g11: LineSegment StartX=-49.19 StartY=5.75 StartZ=0 EndX=-49.19 EndY=2.75 EndZ=0
    g12: ArcOfCircle CenterX=-1.5 CenterY=67.75 CenterZ=0 NormalX=0 NormalY=0 NormalZ=1 AngleXU=0 Radius=1.5 StartAngle=4.71239 EndAngle=7.85398
    g13: ArcOfCircle CenterX=-1.5 CenterY=62 CenterZ=0 NormalX=0 NormalY=0 NormalZ=1 AngleXU=0 Radius=1.5 StartAngle=4.71239 EndAngle=7.85398
    g14: ArcOfCircle CenterX=-1.5 CenterY=56.25 CenterZ=0 NormalX=0 NormalY=0 NormalZ=1 AngleXU=0 Radius=1.5 StartAngle=4.71239 EndAngle=7.85398
    g15: ArcOfCircle CenterX=-11.49 CenterY=50.5 CenterZ=0 NormalX=0 NormalY=0 NormalZ=1 AngleXU=0 Radius=1.5 StartAngle=4.71239 EndAngle=7.85398
    g16: ArcOfCircle CenterX=-16.28 CenterY=44.75 CenterZ=0 NormalX=0 NormalY=0 NormalZ=1 AngleXU=0 Radius=1.5 StartAngle=4.71239 EndAngle=7.85398
    g17: ArcOfCircle CenterX=-18.2337 CenterY=39 CenterZ=0 NormalX=0 NormalY=0 NormalZ=1 AngleXU=0 Radius=1.5 StartAngle=4.71485 EndAngle=7.85398
    g18: ArcOfCircle CenterX=-16.2837 CenterY=27.25 CenterZ=0 NormalX=0 NormalY=0 NormalZ=1 AngleXU=0 Radius=1.5 StartAngle=4.71485 EndAngle=7.85398
    g19: ArcOfCircle CenterX=-18.2337 CenterY=33 CenterZ=0 NormalX=0 NormalY=0 NormalZ=1 AngleXU=0 Radius=1.5 StartAngle=4.71485 EndAngle=7.85398
    g20: ArcOfCircle CenterX=-11.49 CenterY=21.5 CenterZ=0 NormalX=0 NormalY=0 NormalZ=1 AngleXU=0 Radius=1.5 StartAngle=4.71239 EndAngle=7.85398
    g21: ArcOfCircle CenterX=-1.5 CenterY=4.25 CenterZ=0 NormalX=0 NormalY=0 NormalZ=1 AngleXU=0 Radius=1.5 StartAngle=4.71239 EndAngle=7.85398
    g22: ArcOfCircle CenterX=-1.5 CenterY=10 CenterZ=0 NormalX=0 NormalY=0 NormalZ=1 AngleXU=0 Radius=1.5 StartAngle=4.71239 EndAngle=7.85398
    g23: ArcOfCircle CenterX=-1.5 CenterY=15.75 CenterZ=0 NormalX=0 NormalY=0 NormalZ=1 AngleXU=0 Radius=1.5 StartAngle=4.71239 EndAngle=7.85398
    g24: LineSegment StartX=-49.19 StartY=69.25 StartZ=0 EndX=-1.5 EndY=69.25 EndZ=0
    g25: LineSegment StartX=-49.19 StartY=66.25 StartZ=0 EndX=-1.5 EndY=66.25 EndZ=0
    g26: LineSegment StartX=-49.19 StartY=63.5 StartZ=0 EndX=-1.5 EndY=63.5 EndZ=0
    g27: LineSegment StartX=-49.19 StartY=60.5 StartZ=0 EndX=-1.5 EndY=60.5 EndZ=0
    g28: LineSegment StartX=-49.19 StartY=57.75 StartZ=0 EndX=-1.5 EndY=57.75 EndZ=0
    g29: LineSegment StartX=-49.19 StartY=54.75 StartZ=0 EndX=-1.5 EndY=54.75 EndZ=0
    g30: LineSegment StartX=-49.19 StartY=52 StartZ=0 EndX=-11.49 EndY=52 EndZ=0
    g31: LineSegment StartX=-49.19 StartY=49 StartZ=0 EndX=-11.49 EndY=49 EndZ=0
    g32: LineSegment StartX=-49.19 StartY=46.25 StartZ=0 EndX=-16.28 EndY=46.25 EndZ=0
    g33: LineSegment StartX=-49.19 StartY=43.25 StartZ=0 EndX=-16.28 EndY=43.25 EndZ=0
    g34: LineSegment StartX=-49.19 StartY=40.5 StartZ=0 EndX=-18.2337 EndY=40.5 EndZ=0
    g35: LineSegment StartX=-49.19 StartY=37.5 StartZ=0 EndX=-18.23 EndY=37.5 EndZ=0
    g36: LineSegment StartX=-49.19 StartY=34.5 StartZ=0 EndX=-18.2337 EndY=34.5 EndZ=0
    g37: LineSegment StartX=-49.19 StartY=31.5 StartZ=0 EndX=-18.23 EndY=31.5 EndZ=0
    g38: LineSegment StartX=-49.19 StartY=28.75 StartZ=0 EndX=-16.2837 EndY=28.75 EndZ=0
    g39: LineSegment StartX=-49.19 StartY=25.75 StartZ=0 EndX=-16.28 EndY=25.75 EndZ=0
    g40: LineSegment StartX=-49.19 StartY=23 StartZ=0 EndX=-11.49 EndY=23 EndZ=0
    g41: LineSegment StartX=-49.19 StartY=20 StartZ=0 EndX=-11.49 EndY=20 EndZ=0
    g42: LineSegment StartX=-49.19 StartY=17.25 StartZ=0 EndX=-1.5 EndY=17.25 EndZ=0
    g43: LineSegment StartX=-49.19 StartY=14.25 StartZ=0 EndX=-1.5 EndY=14.25 EndZ=0
    g44: LineSegment StartX=-49.19 StartY=11.5 StartZ=0 EndX=-1.5 EndY=11.5 EndZ=0
    g45: LineSegment StartX=-49.19 StartY=8.5 StartZ=0 EndX=-1.5 EndY=8.5 EndZ=0
    g46: LineSegment StartX=-49.19 StartY=5.75 StartZ=0 EndX=-1.5 EndY=5.75 EndZ=0
    g47: LineSegment StartX=-49.19 StartY=2.75 StartZ=0 EndX=-1.5 EndY=2.75 EndZ=0
  constraints (120):
    c: Vertical(g0)
    c: Distance(g0) = 3
    c: Block(g0)
    c: Vertical(g1)
    c: Distance(g1) = 3
    c: Vertical(g2)
    c: Equal(g0,g2) = 3
    c: Block(g2)
    c: Vertical(g3)
    c: Equal(g1,g3) = 3
    c: Vertical(g4)
    c: Equal(g0,g4) = 3
    c: Block(g4)
    c: Vertical(g5)
    c: Equal(g1,g5) = 3
    c: Vertical(g6)
    c: Equal(g0,g6) = 3
    c: Block(g6)
    c: Vertical(g7)
    c: Equal(g1,g7) = 3
    c: Vertical(g8)
    c: Equal(g0,g8) = 3
    c: Block(g8)
    c: Vertical(g9)
    c: Equal(g1,g9) = 3
    c: Vertical(g10)
    c: Equal(g0,g10) = 3
    c: Block(g10)
    c: Vertical(g11)
    c: Equal(g1,g11) = 3
    c: Block(g12)
    c: Block(g13)
    c: Block(g14)
    c: Block(g15)
    c: Block(g16)
    c: Block(g17)
    c: Block(g18)
    c: Block(g19)
    c: Block(g20)
    c: Block(g21)
    c: Block(g22)
    c: Block(g23)
    c: Block(g11)
    c: Block(g9)
    c: Block(g7)
    c: Block(g5)
    c: Block(g3)
    c: Block(g1)
    c: Coincident(g24,g0)
    c: Coincident(g24,g12)
    c: Horizontal(g24)
    c: Coincident(g25,g0)
    c: Coincident(g25,g12)
    c: Horizontal(g25)
    c: Coincident(g26,g1)
    c: Coincident(g26,g13)
    c: Horizontal(g26)
    c: Coincident(g27,g1)
    c: Coincident(g27,g13)
    c: Horizontal(g27)
    c: Coincident(g28,g2)
    c: Coincident(g28,g14)
    c: Horizontal(g28)
    c: Coincident(g29,g2)
    c: Coincident(g29,g14)
    c: Horizontal(g29)
    c: Coincident(g30,g3)
    c: Coincident(g30,g15)
    c: Horizontal(g30)
    c: Coincident(g31,g3)
    c: Coincident(g31,g15)
    c: Horizontal(g31)
    c: Coincident(g32,g4)
    c: Coincident(g32,g16)
    c: Horizontal(g32)
    c: Coincident(g33,g4)
    c: Coincident(g33,g16)
    c: Horizontal(g33)
    c: Coincident(g34,g5)
    c: Coincident(g34,g17)
    c: Horizontal(g34)
    c: Coincident(g35,g5)
    c: Coincident(g35,g17)
    c: Horizontal(g35)
    c: Coincident(g36,g6)
    c: Coincident(g36,g19)
    c: Horizontal(g36)
    c: Coincident(g37,g6)
    c: Coincident(g37,g19)
    c: Horizontal(g37)
    c: Coincident(g38,g7)
    c: Coincident(g38,g18)
    c: Horizontal(g38)
    c: Coincident(g39,g7)
    c: Coincident(g39,g18)
    c: Horizontal(g39)
    c: Coincident(g40,g8)
    c: Coincident(g40,g20)
    c: Horizontal(g40)
    c: Coincident(g41,g8)
    c: Coincident(g41,g20)
    c: Horizontal(g41)
    c: Coincident(g42,g9)
    c: Coincident(g42,g23)
    c: Horizontal(g42)
    c: Coincident(g43,g9)
    c: Coincident(g43,g23)
    c: Horizontal(g43)
    c: Coincident(g44,g10)
    c: Coincident(g44,g22)
    c: Horizontal(g44)
    c: Coincident(g45,g10)
    c: Coincident(g45,g22)
    c: Horizontal(g45)
    c: Coincident(g46,g11)
    c: Coincident(g46,g21)
    c: Horizontal(g46)
    c: Coincident(g47,g11)
    c: Coincident(g47,g21)
    c: Horizontal(g47)
FEATURE [Part::Extrusion] Extrude023
  Base = -> Sketch032
  Dir = (1,-2e-16,2e-16)
  DirMode = 2
  FaceMakerClass = Part::FaceMakerBullseye
  LengthFwd = 19
  LengthRev = 0
  Placement = pos=(-19,0,0) rot=(0,0,1;0rad)
  Solid = true
  Symmetric = false
FEATURE [Part::Fillet] Fillet023
  Base = -> Extrude023
  Edges = <same value as first occurrence — deduplicated (x6 in doc)>
  Placement = pos=(0,0.05,0) rot=(0,0,1;0rad)
FEATURE [Part::Cut] Cut014  label="bottom003"
  Base = -> Cut007
  Tool = -> Fusion047
FEATURE [Part::Cut] Cut021  label="bottom004"
  Base = -> Cut014
  Tool = -> Fillet023
FEATURE [Sketcher::SketchObject] Sketch033
  FullyConstrained = true
  Placement = pos=(117,19,0) rot=(0.57735,0.57735,0.57735;2.0944rad)
  sketch-geometry (8):
    g0: LineSegment StartX=-49.19 StartY=69.25 StartZ=0 EndX=-49.19 EndY=66.25 EndZ=0
    g1: LineSegment StartX=-49.19 StartY=5.75 StartZ=0 EndX=-49.19 EndY=2.75 EndZ=0
    g2: ArcOfCircle CenterX=-1.5 CenterY=67.75 CenterZ=0 NormalX=0 NormalY=0 NormalZ=1 AngleXU=0 Radius=1.5 StartAngle=4.71239 EndAngle=7.85398
    g3: ArcOfCircle CenterX=-1.5 CenterY=4.25 CenterZ=0 NormalX=0 NormalY=0 NormalZ=1 AngleXU=0 Radius=1.5 StartAngle=4.71239 EndAngle=7.85398
    g4: LineSegment StartX=-49.19 StartY=69.25 StartZ=0 EndX=-1.5 EndY=69.25 EndZ=0
    g5: LineSegment StartX=-49.19 StartY=66.25 StartZ=0 EndX=-1.5 EndY=66.25 EndZ=0
    g6: LineSegment StartX=-49.19 StartY=5.75 StartZ=0 EndX=-1.5 EndY=5.75 EndZ=0
    g7: LineSegment StartX=-49.19 StartY=2.75 StartZ=0 EndX=-1.5 EndY=2.75 EndZ=0
  constraints (19):
    c: Vertical(g0)
    c: Distance(g0) = 3
    c: Block(g0)
    c: Vertical(g1)
    c: Block(g2)
    c: Block(g3)
    c: Block(g1)
    c: Coincident(g4,g0)
    c: Coincident(g4,g2)
    c: Horizontal(g4)
    c: Coincident(g5,g0)
    c: Coincident(g5,g2)
    c: Horizontal(g5)
    c: Coincident(g6,g1)
    c: Coincident(g6,g3)
    c: Horizontal(g6)
    c: Coincident(g7,g1)
    c: Coincident(g7,g3)
    c: Horizontal(g7)
FEATURE [Sketcher::SketchObject] Sketch034
  FullyConstrained = true
  Placement = pos=(117,19,0) rot=(0.57735,0.57735,0.57735;2.0944rad)
  sketch-geometry (8):
    g0: LineSegment StartX=-49.19 StartY=63.5 StartZ=0 EndX=-49.19 EndY=60.5 EndZ=0
    g1: LineSegment StartX=-49.19 StartY=11.5 StartZ=0 EndX=-49.19 EndY=8.5 EndZ=0
    g2: ArcOfCircle CenterX=-1.5 CenterY=62 CenterZ=0 NormalX=0 NormalY=0 NormalZ=1 AngleXU=0 Radius=1.5 StartAngle=4.71239 EndAngle=7.85398
    g3: ArcOfCircle CenterX=-1.5 CenterY=10 CenterZ=0 NormalX=0 NormalY=0 NormalZ=1 AngleXU=0 Radius=1.5 StartAngle=4.71239 EndAngle=7.85398
    g4: LineSegment StartX=-49.19 StartY=63.5 StartZ=0 EndX=-1.5 EndY=63.5 EndZ=0
    g5: LineSegment StartX=-49.19 StartY=60.5 StartZ=0 EndX=-1.5 EndY=60.5 EndZ=0
    g6: LineSegment StartX=-49.19 StartY=11.5 StartZ=0 EndX=-1.5 EndY=11.5 EndZ=0
    g7: LineSegment StartX=-49.19 StartY=8.5 StartZ=0 EndX=-1.5 EndY=8.5 EndZ=0
  constraints (19):
    c: Vertical(g0)
    c: Distance(g0) = 3
    c: Vertical(g1)
    c: Block(g1)
    c: Block(g2)
    c: Block(g3)
    c: Block(g0)
    c: Coincident(g4,g0)
    c: Coincident(g4,g2)
    c: Horizontal(g4)
    c: Coincident(g5,g0)
    c: Coincident(g5,g2)
    c: Horizontal(g5)
    c: Coincident(g6,g1)
    c: Coincident(g6,g3)
    c: Horizontal(g6)
    c: Coincident(g7,g1)
    c: Coincident(g7,g3)
    c: Horizontal(g7)
FEATURE [Part::Extrusion] Extrude024
  Base = -> Sketch033
  Dir = (1,0,0)
  DirMode = 2
  FaceMakerClass = Part::FaceMakerBullseye
  LengthFwd = 10
  LengthRev = 0
  Solid = true
  Symmetric = false
FEATURE [Part::Extrusion] Extrude025
  Base = -> Sketch034
  Dir = (1,0,0)
  DirMode = 2
  FaceMakerClass = Part::FaceMakerBullseye
  LengthFwd = 10
  LengthRev = 0
  Solid = true
  Symmetric = false
FEATURE [Part::Fillet] Fillet024  label="removeFromtMoreFrontCaseScrewRetainers"
  Base = -> Extrude024
  Edges = 4 edges r=1.49: [Edge6,Edge11,Edge18,Edge23]
  Placement = pos=(-11,0,0) rot=(0,0,1;0rad)
FEATURE [Part::Fillet] Fillet025  label="removeFromtMoreFrontCaseScrewRetainers001"
  Base = -> Extrude025
  Edges = 4 edges r=1.49: [Edge6,Edge11,Edge18,Edge23]
  Placement = pos=(-19,0,0) rot=(0,0,1;0rad)
FEATURE [Part::Cut] Cut022
  Base = -> Cut015
  Tool = -> Fillet025
FEATURE [Part::Cut] Cut023  label="screwRetainers"
  Base = -> Cut022
  Tool = -> Fillet024
FEATURE [Part::MultiFuse] Fusion056  label="bottom005"
  Shapes = -> [Fusion044,Cut021]
FEATURE [Part::MultiFuse] Fusion057  label="casePillars001"
  Shapes = -> [Cut016,Fusion052]
FEATURE [Part::MultiFuse] Fusion058  label="bottom006"
  Shapes = -> [Fusion056,Cut023]
FEATURE [Part::MultiFuse] Fusion059  label="bottom007"
  Shapes = -> [Fusion058,Fillet005]
FEATURE [Part::MultiFuse] Fusion060  label="bottom008"
  Shapes = -> [Fusion059,Fusion]
FEATURE [Part::MultiFuse] Fusion061  label="top011"
  Shapes = -> [Cut006,Cut020]
FEATURE [Part::MultiFuse] Fusion062  label="top012"
  Shapes = -> [Fusion057,Fusion061]
FEATURE [Sketcher::SketchObject] Sketch035  label="topSketch007"
  FullyConstrained = true
  sketch-geometry (6):
    g0: LineSegment StartX=19 StartY=38 StartZ=0 EndX=117 EndY=38 EndZ=0
    g1: ArcOfCircle CenterX=19 CenterY=19 CenterZ=0 NormalX=0 NormalY=0 NormalZ=1 AngleXU=0 Radius=19 StartAngle=1.5708 EndAngle=3.14159
    g2: LineSegment StartX=117 StartY=38 StartZ=0 EndX=117 EndY=19 EndZ=0
    g3: LineSegment StartX=98 StartY=1.0161e-12 StartZ=0 EndX=5.22862e-06 EndY=1.0161e-12 EndZ=0
    g4: LineSegment StartX=5.22862e-06 StartY=19 StartZ=0 EndX=5.22862e-06 EndY=1.0161e-12 EndZ=0
    g5: ArcOfCircle CenterX=98 CenterY=19 CenterZ=0 NormalX=0 NormalY=0 NormalZ=1 AngleXU=0 Radius=19 StartAngle=4.71239 EndAngle=6.28319
  constraints (16):
    c: Horizontal(g0)
    c: Distance(g0) = 98
    c: Coincident(g1,g0)
    c: Block(g1)
    c: Coincident(g2,g0)
    c: Vertical(g2)
    c: Distance(g2) = 19
    c: Horizontal(g3)
    c: Coincident(g4,g1)
    c: Vertical(g4)
    c: Coincident(g3,g4)
    c: Block(g3)
    c: Coincident(g5,g2)
    c: Coincident(g5,g3)
    c: Block(g0)
    c: Block(g5)
FEATURE [Part::Extrusion] Extrude026  label="sideA001"
  Base = -> Sketch035
  Dir = (0,0,1)
  DirMode = 2
  FaceMakerClass = Part::FaceMakerBullseye
  LengthFwd = 3
  LengthRev = 0
  Placement = pos=(0,0,-2.7) rot=(0,0,1;0rad)
  Solid = true
  Symmetric = false
FEATURE [Sketcher::SketchObject] Sketch036  label="topSketch008"
  FullyConstrained = true
  sketch-geometry (6):
    g0: LineSegment StartX=19 StartY=38 StartZ=0 EndX=117 EndY=38 EndZ=0
    g1: ArcOfCircle CenterX=19 CenterY=19 CenterZ=0 NormalX=0 NormalY=0 NormalZ=1 AngleXU=0 Radius=19 StartAngle=1.5708 EndAngle=3.14159
    g2: LineSegment StartX=117 StartY=38 StartZ=0 EndX=117 EndY=19 EndZ=0
    g3: LineSegment StartX=98 StartY=1.0161e-12 StartZ=0 EndX=5.22862e-06 EndY=1.0161e-12 EndZ=0
    g4: LineSegment StartX=5.22862e-06 StartY=19 StartZ=0 EndX=5.22862e-06 EndY=1.0161e-12 EndZ=0
    g5: ArcOfCircle CenterX=98 CenterY=19 CenterZ=0 NormalX=0 NormalY=0 NormalZ=1 AngleXU=0 Radius=19 StartAngle=4.71239 EndAngle=6.28319
  constraints (16):
    c: Horizontal(g0)
    c: Distance(g0) = 98
    c: Coincident(g1,g0)
    c: Block(g1)
    c: Coincident(g2,g0)
    c: Vertical(g2)
    c: Distance(g2) = 19
    c: Horizontal(g3)
    c: Coincident(g4,g1)
    c: Vertical(g4)
    c: Coincident(g3,g4)
    c: Block(g3)
    c: Coincident(g5,g2)
    c: Coincident(g5,g3)
    c: Block(g0)
    c: Block(g5)
FEATURE [Part::Extrusion] Extrude027  label="sideB001"
  Base = -> Sketch036
  Dir = (0,0,1)
  DirMode = 2
  FaceMakerClass = Part::FaceMakerBullseye
  LengthFwd = 3
  LengthRev = 0
  Placement = pos=(0,0,71.7) rot=(0,0,1;0rad)
  Solid = true
  Symmetric = false
FEATURE [Part::MultiFuse] Fusion064  label="removeFromBottom"
  Shapes = -> [Extrude026,Extrude027]
FEATURE [Part::Cut] Cut024  label="bottom009"
  Base = -> Fusion060
  Tool = -> Fusion064
FEATURE [Sketcher::SketchObject] Sketch037  label="topSketch009"
  FullyConstrained = true
  sketch-geometry (8):
    g0: ArcOfCircle CenterX=19 CenterY=19.1201 CenterZ=0 NormalX=0 NormalY=0 NormalZ=1 AngleXU=0 Radius=18.8799 StartAngle=1.5708 EndAngle=3.14793
    g1: LineSegment StartX=0.120501 StartY=19.0004 StartZ=0 EndX=0.120501 EndY=0.000382114 EndZ=0
    g2: LineSegment StartX=19 StartY=38 StartZ=0 EndX=124 EndY=38 EndZ=0
    g3: LineSegment StartX=0.120501 StartY=0.000382114 StartZ=0 EndX=105.121 EndY=0.000382114 EndZ=0
    g4: LineSegment StartX=124 StartY=38 StartZ=0 EndX=125.616 EndY=38 EndZ=0
    g5: LineSegment StartX=105.121 StartY=0.000382114 StartZ=0 EndX=106.736 EndY=0.000382114 EndZ=0
    g6: ArcOfCircle CenterX=106.616 CenterY=19 CenterZ=0 NormalX=0 NormalY=0 NormalZ=1 AngleXU=0 Radius=19 StartAngle=4.71873 EndAngle=6.28319
    g7: LineSegment StartX=125.616 StartY=38 StartZ=0 EndX=125.616 EndY=19 EndZ=0
  constraints (21):
    c: Block(g0)
    c: Coincident(g1,g0)
    c: Vertical(g1)
    c: Horizontal(g2)
    c: Distance(g2) = 105
    c: Coincident(g2,g0)
    c: Distance(g1) = 19
    c: Coincident(g3,g1)
    c: Horizontal(g3)
    c: Distance(g3) = 105
    c: Coincident(g4,g2)
    c: Horizontal(g4)
    c: Distance(g4) = 1.61553
    c: Horizontal(g5)
    c: Equal(g4,g5) = 1.61553
    c: Coincident(g5,g3)
    c: Block(g6)
    c: Coincident(g6,g5)
    c: Coincident(g7,g4)
    c: Coincident(g7,g6)
    c: Vertical(g7)
FEATURE [Part::Extrusion] Extrude028  label="sideB"
  Base = -> Sketch037
  Dir = (0,0,1)
  DirMode = 2
  FaceMakerClass = Part::FaceMakerBullseye
  LengthFwd = 3
  LengthRev = 0
  Placement = pos=(0,0,72) rot=(0,0,1;0rad)
  Solid = true
  Symmetric = false
FEATURE [Sketcher::SketchObject] Sketch038  label="topSketch010"
  FullyConstrained = true
  sketch-geometry (22):
    g0: LineSegment StartX=5.21097e-06 StartY=3 StartZ=0 EndX=5.21097e-06 EndY=19 EndZ=0
    g1: ArcOfCircle CenterX=19 CenterY=19 CenterZ=0 NormalX=0 NormalY=0 NormalZ=1 AngleXU=0 Radius=19 StartAngle=1.5708 EndAngle=3.14159
    g2: ArcOfCircle CenterX=19 CenterY=19 CenterZ=0 NormalX=0 NormalY=0 NormalZ=1 AngleXU=0 Radius=16 StartAngle=1.5708 EndAngle=3.14159
    g3: LineSegment StartX=114 StartY=35 StartZ=0 EndX=19 EndY=35 EndZ=0
    g4: LineSegment StartX=5.21097e-06 StartY=3 StartZ=0 EndX=5.21097e-06 EndY=0 EndZ=0
    g5: LineSegment StartX=3 StartY=0 StartZ=0 EndX=5.21097e-06 EndY=0 EndZ=0
    g6: LineSegment StartX=3 StartY=19 StartZ=0 EndX=3 EndY=0 EndZ=0
    g7: LineSegment StartX=19 StartY=38 StartZ=0 EndX=124 EndY=38 EndZ=0
    g8: Circle CenterX=119 CenterY=35 CenterZ=0 NormalX=0 NormalY=0 NormalZ=1 AngleXU=0 Radius=1
    g9: Circle CenterX=121 CenterY=35 CenterZ=0 NormalX=0 NormalY=0 NormalZ=1 AngleXU=0 Radius=1
    g10: Circle CenterX=121 CenterY=33 CenterZ=0 NormalX=0 NormalY=0 NormalZ=1 AngleXU=0 Radius=1
    g11: BSplineCurve PolesCount=3 KnotsCount=2 Degree=2 IsPeriodic=0
    g12: GeomPoint X=119 Y=35 Z=0
    g13: GeomPoint X=121 Y=33 Z=0
    g14: LineSegment StartX=119 StartY=35 StartZ=0 EndX=114 EndY=35 EndZ=0
    g15: ArcOfCircle CenterX=105 CenterY=19 CenterZ=0 NormalX=0 NormalY=0 NormalZ=1 AngleXU=0 Radius=16 StartAngle=5.60905 EndAngle=6.28319
    g16: LineSegment StartX=121 StartY=33 StartZ=0 EndX=121 EndY=19 EndZ=0
    g17: LineSegment StartX=117.5 StartY=9.01251 StartZ=0 EndX=121.163 EndY=9.0125 EndZ=0
    g18: ArcOfCircle CenterX=105 CenterY=19 CenterZ=0 NormalX=0 NormalY=0 NormalZ=1 AngleXU=0 Radius=20.6155 StartAngle=5.7297 EndAngle=6.28319
    g19: LineSegment StartX=121.163 StartY=9.0125 StartZ=0 EndX=122.538 EndY=8.16329 EndZ=0
    g20: LineSegment StartX=124 StartY=38 StartZ=0 EndX=125.616 EndY=38 EndZ=0
    g21: LineSegment StartX=125.616 StartY=19 StartZ=0 EndX=125.616 EndY=38 EndZ=0
  constraints (49):
    c: Vertical(g0)
    c: Block(g0)
    c: Coincident(g1,g0)
    c: Block(g1)
    c: Coincident(g2,g1)
    c: Block(g2)
    c: Coincident(g3,g2)
    c: Horizontal(g3)
    c: Tangent(g3,g2)
    c: Coincident(g4,g0)
    c: Distance(g4) = 3
    c: Vertical(g4)
    c: Coincident(g5,g4)
    c: Horizontal(g5)
    c: Coincident(g6,g2)
    c: Coincident(g6,g5)
    c: Vertical(g6)
    c: Horizontal(g7)
    c: Distance(g7) = 105
    c: Coincident(g7,g1)
    c: Block(g3)
    c: Weight(g8) = 1
    c: Equal(g8,g9)
    c: Equal(g8,g10)
    c: InternalAlignment(g8,g11)
    c: InternalAlignment(g9,g11)
    c: InternalAlignment(g10,g11)
    c: InternalAlignment(g12,g11)
    c: InternalAlignment(g13,g11)
    c: Block(g11)
    c: Coincident(g14,g11)
    c: Coincident(g14,g3)
    c: Horizontal(g14)
    c: Block(g15)
    c: Coincident(g16,g11)
    c: Coincident(g16,g15)
    c: Vertical(g16)
    c: Distance(g16) = 14
    c: Coincident(g17,g15)
    c: Block(g18)
    c: Coincident(g19,g18)
    c: Coincident(g20,g7)
    c: Horizontal(g20)
    c: Vertical(g21)
    c: Coincident(g20,g21)
    c: Block(g20)
    c: Block(g21)
    c: Block(g19)
    c: Block(g17)
FEATURE [Part::Extrusion] Extrude029
  Base = -> Sketch038
  Dir = (0,0,1)
  DirMode = 2
  FaceMakerClass = Part::FaceMakerBullseye
  LengthFwd = 72
  LengthRev = 0
  Solid = true
  Symmetric = false
FEATURE [Part::Feature] Face085
  shape: bbox 4.8 x 25.5 x 2e-07 mm, 1 faces, 0 solids (baked)
FEATURE [Part::Revolution] Revolve089  label="moreFrontCaseScrewPost003"
  Angle = 360
  Axis = (0,1,0)
  Base = (0,0,0)
  FaceMakerClass = Part::FaceMakerBullseye
  Placement = pos=(109.5,4.5,3.5) rot=(0,0,1;0rad)
  Solid = false
  Source = -> Face085
  Symmetric = false
FEATURE [Part::Feature] Face086
  shape: bbox 4.8 x 25.5 x 2e-07 mm, 1 faces, 0 solids (baked)
FEATURE [Part::Revolution] Revolve090  label="moreFrontCaseScrewPost004"
  Angle = 360
  Axis = (0,1,0)
  Base = (0,0,0)
  FaceMakerClass = Part::FaceMakerBullseye
  Placement = pos=(109.5,4.5,68.5) rot=(0,0,1;0rad)
  Solid = false
  Source = -> Face086
  Symmetric = false
FEATURE [Part::Fillet] Fillet026  label="top013"
  Base = -> Extrude029
  Edges = 1 edges r=2: [Edge35]
FEATURE [Sketcher::SketchObject] Sketch039
  FullyConstrained = true
  sketch-geometry (7):
    g0: LineSegment StartX=0 StartY=0 StartZ=0 EndX=0 EndY=6 EndZ=0
    g1: Circle CenterX=0 CenterY=0 CenterZ=0 NormalX=0 NormalY=0 NormalZ=1 AngleXU=0 Radius=1
    g2: Circle CenterX=8 CenterY=6 CenterZ=0 NormalX=0 NormalY=0 NormalZ=1 AngleXU=0 Radius=1
    g3: BSplineCurve PolesCount=3 KnotsCount=2 Degree=2 IsPeriodic=0
    g4: GeomPoint X=0 Y=0 Z=0
    g5: GeomPoint X=8 Y=6 Z=0
    g6: LineSegment StartX=0 StartY=6 StartZ=0 EndX=8 EndY=6 EndZ=0
  constraints (14):
    c: Coincident(g0,g-1)
    c: Distance(g0) = 6
    c: Vertical(g0)
    c: Coincident(g3,g0)
    c: Weight(g1) = 1
    c: Equal(g1,g2)
    c: InternalAlignment(g1,g3)
    c: InternalAlignment(g2,g3)
    c: InternalAlignment(g4,g3)
    c: InternalAlignment(g5,g3)
    c: Block(g3)
    c: Coincident(g6,g0)
    c: Coincident(g6,g3)
    c: Horizontal(g6)
FEATURE [Sketcher::SketchObject] Sketch040
  FullyConstrained = true
  sketch-geometry (7):
    g0: LineSegment StartX=0 StartY=0 StartZ=0 EndX=0 EndY=6 EndZ=0
    g1: Circle CenterX=0 CenterY=0 CenterZ=0 NormalX=0 NormalY=0 NormalZ=1 AngleXU=0 Radius=1
    g2: Circle CenterX=8 CenterY=6 CenterZ=0 NormalX=0 NormalY=0 NormalZ=1 AngleXU=0 Radius=1
    g3: BSplineCurve PolesCount=3 KnotsCount=2 Degree=2 IsPeriodic=0
    g4: GeomPoint X=0 Y=0 Z=0
    g5: GeomPoint X=8 Y=6 Z=0
    g6: LineSegment StartX=0 StartY=6 StartZ=0 EndX=8 EndY=6 EndZ=0
  constraints (14):
    c: Coincident(g0,g-1)
    c: Distance(g0) = 6
    c: Vertical(g0)
    c: Coincident(g3,g0)
    c: Weight(g1) = 1
    c: Equal(g1,g2)
    c: InternalAlignment(g1,g3)
    c: InternalAlignment(g2,g3)
    c: InternalAlignment(g4,g3)
    c: InternalAlignment(g5,g3)
    c: Block(g3)
    c: Coincident(g6,g0)
    c: Coincident(g6,g3)
    c: Horizontal(g6)
FEATURE [Sketcher::SketchObject] Sketch041
  FullyConstrained = true
  sketch-geometry (7):
    g0: LineSegment StartX=0 StartY=0 StartZ=0 EndX=0 EndY=6 EndZ=0
    g1: Circle CenterX=0 CenterY=0 CenterZ=0 NormalX=0 NormalY=0 NormalZ=1 AngleXU=0 Radius=1
    g2: Circle CenterX=8 CenterY=6 CenterZ=0 NormalX=0 NormalY=0 NormalZ=1 AngleXU=0 Radius=1
    g3: BSplineCurve PolesCount=3 KnotsCount=2 Degree=2 IsPeriodic=0
    g4: GeomPoint X=0 Y=0 Z=0
    g5: GeomPoint X=8 Y=6 Z=0
    g6: LineSegment StartX=0 StartY=6 StartZ=0 EndX=8 EndY=6 EndZ=0
  constraints (14):
    c: Coincident(g0,g-1)
    c: Distance(g0) = 6
    c: Vertical(g0)
    c: Coincident(g3,g0)
    c: Weight(g1) = 1
    c: Equal(g1,g2)
    c: InternalAlignment(g1,g3)
    c: InternalAlignment(g2,g3)
    c: InternalAlignment(g4,g3)
    c: InternalAlignment(g5,g3)
    c: Block(g3)
    c: Coincident(g6,g0)
    c: Coincident(g6,g3)
    c: Horizontal(g6)
FEATURE [Sketcher::SketchObject] Sketch042
  FullyConstrained = true
  sketch-geometry (7):
    g0: LineSegment StartX=0 StartY=0 StartZ=0 EndX=0 EndY=6 EndZ=0
    g1: Circle CenterX=0 CenterY=0 CenterZ=0 NormalX=0 NormalY=0 NormalZ=1 AngleXU=0 Radius=1
    g2: Circle CenterX=8 CenterY=6 CenterZ=0 NormalX=0 NormalY=0 NormalZ=1 AngleXU=0 Radius=1
    g3: BSplineCurve PolesCount=3 KnotsCount=2 Degree=2 IsPeriodic=0
    g4: GeomPoint X=0 Y=0 Z=0
    g5: GeomPoint X=8 Y=6 Z=0
    g6: LineSegment StartX=0 StartY=6 StartZ=0 EndX=8 EndY=6 EndZ=0
  constraints (14):
    c: Coincident(g0,g-1)
    c: Distance(g0) = 6
    c: Vertical(g0)
    c: Coincident(g3,g0)
    c: Weight(g1) = 1
    c: Equal(g1,g2)
    c: InternalAlignment(g1,g3)
    c: InternalAlignment(g2,g3)
    c: InternalAlignment(g4,g3)
    c: InternalAlignment(g5,g3)
    c: Block(g3)
    c: Coincident(g6,g0)
    c: Coincident(g6,g3)
    c: Horizontal(g6)
FEATURE [Part::Extrusion] Extrude030  label="caseScrewPillarBracket008"
  Base = -> Sketch039
  Dir = (0,0,1)
  DirMode = 2
  FaceMakerClass = Part::FaceMakerBullseye
  LengthFwd = 2.4
  LengthRev = 0
  Placement = pos=(15.76,29,8.8) rot=(0,1,0;0rad)
  Solid = true
  Symmetric = false
FEATURE [Part::Extrusion] Extrude031  label="caseScrewPillarBracket009"
  Base = -> Sketch040
  Dir = (0,0,1)
  DirMode = 2
  FaceMakerClass = Part::FaceMakerBullseye
  LengthFwd = 2.4
  LengthRev = 0
  Placement = pos=(15.76,29,60.8) rot=(0,0,1;0rad)
  Solid = true
  Symmetric = false
FEATURE [Part::Extrusion] Extrude032  label="caseScrewPillarBracket010"
  Base = -> Sketch041
  Dir = (0,0,1)
  DirMode = 2
  FaceMakerClass = Part::FaceMakerBullseye
  LengthFwd = 2.4
  LengthRev = 0
  Placement = pos=(13.7,29,13.26) rot=(0,-1,0;1.5708rad)
  Solid = true
  Symmetric = false
FEATURE [Part::Extrusion] Extrude033  label="caseScrewPillarBracket011"
  Base = -> Sketch042
  Dir = (0,0,1)
  DirMode = 2
  FaceMakerClass = Part::FaceMakerBullseye
  LengthFwd = 2.4
  LengthRev = 0
  Placement = pos=(11.3,29,58.74) rot=(0,1,0;1.5708rad)
  Solid = true
  Symmetric = false
FEATURE [Sketcher::SketchObject] Sketch043
  FullyConstrained = true
  sketch-geometry (7):
    g0: LineSegment StartX=0 StartY=0 StartZ=0 EndX=0 EndY=6 EndZ=0
    g1: Circle CenterX=0 CenterY=0 CenterZ=0 NormalX=0 NormalY=0 NormalZ=1 AngleXU=0 Radius=1
    g2: Circle CenterX=8 CenterY=6 CenterZ=0 NormalX=0 NormalY=0 NormalZ=1 AngleXU=0 Radius=1
    g3: BSplineCurve PolesCount=3 KnotsCount=2 Degree=2 IsPeriodic=0
    g4: GeomPoint X=0 Y=0 Z=0
    g5: GeomPoint X=8 Y=6 Z=0
    g6: LineSegment StartX=0 StartY=6 StartZ=0 EndX=8 EndY=6 EndZ=0
  constraints (14):
    c: Coincident(g0,g-1)
    c: Distance(g0) = 6
    c: Vertical(g0)
    c: Coincident(g3,g0)
    c: Weight(g1) = 1
    c: Equal(g1,g2)
    c: InternalAlignment(g1,g3)
    c: InternalAlignment(g2,g3)
    c: InternalAlignment(g4,g3)
    c: InternalAlignment(g5,g3)
    c: Block(g3)
    c: Coincident(g6,g0)
    c: Coincident(g6,g3)
    c: Horizontal(g6)
FEATURE [Part::Extrusion] Extrude034  label="caseScrewPillarBracket012"
  Base = -> Sketch043
  Dir = (0,0,1)
  DirMode = 2
  FaceMakerClass = Part::FaceMakerBullseye
  LengthFwd = 2.4
  LengthRev = 0
  Placement = pos=(88.3,29,65.23) rot=(0,1,0;1.5708rad)
  Solid = true
  Symmetric = false
FEATURE [Sketcher::SketchObject] Sketch044
  FullyConstrained = true
  sketch-geometry (7):
    g0: LineSegment StartX=0 StartY=0 StartZ=0 EndX=0 EndY=6 EndZ=0
    g1: Circle CenterX=0 CenterY=0 CenterZ=0 NormalX=0 NormalY=0 NormalZ=1 AngleXU=0 Radius=1
    g2: Circle CenterX=8 CenterY=6 CenterZ=0 NormalX=0 NormalY=0 NormalZ=1 AngleXU=0 Radius=1
    g3: BSplineCurve PolesCount=3 KnotsCount=2 Degree=2 IsPeriodic=0
    g4: GeomPoint X=0 Y=0 Z=0
    g5: GeomPoint X=8 Y=6 Z=0
    g6: LineSegment StartX=0 StartY=6 StartZ=0 EndX=8 EndY=6 EndZ=0
  constraints (14):
    c: Coincident(g0,g-1)
    c: Distance(g0) = 6
    c: Vertical(g0)
    c: Coincident(g3,g0)
    c: Weight(g1) = 1
    c: Equal(g1,g2)
    c: InternalAlignment(g1,g3)
    c: InternalAlignment(g2,g3)
    c: InternalAlignment(g4,g3)
    c: InternalAlignment(g5,g3)
    c: Block(g3)
    c: Coincident(g6,g0)
    c: Coincident(g6,g3)
    c: Horizontal(g6)
FEATURE [Part::Extrusion] Extrude035  label="caseScrewPillarBracket013"
  Base = -> Sketch044
  Dir = (0,0,1)
  DirMode = 2
  FaceMakerClass = Part::FaceMakerBullseye
  LengthFwd = 2.4
  LengthRev = 0
  Placement = pos=(90.7,29,6.77) rot=(0,-1,0;1.5708rad)
  Solid = true
  Symmetric = false
FEATURE [Sketcher::SketchObject] Sketch045
  FullyConstrained = true
  sketch-geometry (7):
    g0: LineSegment StartX=0 StartY=0 StartZ=0 EndX=0 EndY=6 EndZ=0
    g1: Circle CenterX=0 CenterY=0 CenterZ=0 NormalX=0 NormalY=0 NormalZ=1 AngleXU=0 Radius=1
    g2: Circle CenterX=8 CenterY=6 CenterZ=0 NormalX=0 NormalY=0 NormalZ=1 AngleXU=0 Radius=1
    g3: BSplineCurve PolesCount=3 KnotsCount=2 Degree=2 IsPeriodic=0
    g4: GeomPoint X=0 Y=0 Z=0
    g5: GeomPoint X=8 Y=6 Z=0
    g6: LineSegment StartX=0 StartY=6 StartZ=0 EndX=8 EndY=6 EndZ=0
  constraints (14):
    c: Coincident(g0,g-1)
    c: Distance(g0) = 6
    c: Vertical(g0)
    c: Coincident(g3,g0)
    c: Weight(g1) = 1
    c: Equal(g1,g2)
    c: InternalAlignment(g1,g3)
    c: InternalAlignment(g2,g3)
    c: InternalAlignment(g4,g3)
    c: InternalAlignment(g5,g3)
    c: Block(g3)
    c: Coincident(g6,g0)
    c: Coincident(g6,g3)
    c: Horizontal(g6)
FEATURE [Sketcher::SketchObject] Sketch046
  FullyConstrained = true
  sketch-geometry (7):
    g0: LineSegment StartX=0 StartY=0 StartZ=0 EndX=0 EndY=6 EndZ=0
    g1: Circle CenterX=0 CenterY=0 CenterZ=0 NormalX=0 NormalY=0 NormalZ=1 AngleXU=0 Radius=1
    g2: Circle CenterX=8 CenterY=6 CenterZ=0 NormalX=0 NormalY=0 NormalZ=1 AngleXU=0 Radius=1
    g3: BSplineCurve PolesCount=3 KnotsCount=2 Degree=2 IsPeriodic=0
    g4: GeomPoint X=0 Y=0 Z=0
    g5: GeomPoint X=8 Y=6 Z=0
    g6: LineSegment StartX=0 StartY=6 StartZ=0 EndX=8 EndY=6 EndZ=0
  constraints (14):
    c: Coincident(g0,g-1)
    c: Distance(g0) = 6
    c: Vertical(g0)
    c: Coincident(g3,g0)
    c: Weight(g1) = 1
    c: Equal(g1,g2)
    c: InternalAlignment(g1,g3)
    c: InternalAlignment(g2,g3)
    c: InternalAlignment(g4,g3)
    c: InternalAlignment(g5,g3)
    c: Block(g3)
    c: Coincident(g6,g0)
    c: Coincident(g6,g3)
    c: Horizontal(g6)
FEATURE [Part::Extrusion] Extrude036  label="caseScrewPillarBracket014"
  Base = -> Sketch045
  Dir = (0,0,1)
  DirMode = 2
  FaceMakerClass = Part::FaceMakerBullseye
  LengthFwd = 2.4
  LengthRev = 0
  Placement = pos=(110.7,29,6.77) rot=(0,-1,0;1.5708rad)
  Solid = true
  Symmetric = false
FEATURE [Part::Extrusion] Extrude037  label="caseScrewPillarBracket015"
  Base = -> Sketch046
  Dir = (0,0,1)
  DirMode = 2
  FaceMakerClass = Part::FaceMakerBullseye
  LengthFwd = 2.4
  LengthRev = 0
  Placement = pos=(108.3,29,65.23) rot=(0,1,0;1.5708rad)
  Solid = true
  Symmetric = false
FEATURE [Part::Box] Box013  label="frontCaseScrewPillarBracket002"
  AttacherType = Attacher::AttachEngine3D
  Height = 2.4
  Length = 22
  Placement = pos=(87,28,2.3) rot=(0,0,1;0rad)
  Width = 7
FEATURE [Part::Box] Box014  label="frontCaseScrewPillarBracket003"
  AttacherType = Attacher::AttachEngine3D
  Height = 2.4
  Length = 22
  Placement = pos=(87,28,67.3) rot=(0,0,1;0rad)
  Width = 7
FEATURE [Part::Feature] Face087
  shape: bbox 4.8 x 30.2 x 2e-07 mm, 1 faces, 0 solids (baked)
FEATURE [Part::Revolution] Revolve091  label="frontCaseScrewPost004"
  Angle = 360
  Axis = (0,1,0)
  Base = (0,0,0)
  FaceMakerClass = Part::FaceMakerBullseye
  Placement = pos=(89.5,4.5,3.5) rot=(0,0,1;0rad)
  Solid = false
  Source = -> Face087
  Symmetric = false
FEATURE [Part::Feature] Face088
  shape: bbox 4.8 x 30.2 x 2e-07 mm, 1 faces, 0 solids (baked)
FEATURE [Part::Revolution] Revolve092  label="frontCaseScrewPost005"
  Angle = 360
  Axis = (0,1,0)
  Base = (0,0,0)
  FaceMakerClass = Part::FaceMakerBullseye
  Placement = pos=(89.5,4.5,68.5) rot=(0,0,1;0rad)
  Solid = false
  Source = -> Face088
  Symmetric = false
FEATURE [Part::Feature] Face089
  shape: bbox 3.5 x 30.2 x 2e-07 mm, 1 faces, 0 solids (baked)
FEATURE [Part::Revolution] Revolve093  label="backCaseScrewPost002"
  Angle = 360
  Axis = (0,1,0)
  Base = (0,0,0)
  FaceMakerClass = Part::FaceMakerBullseye
  Placement = pos=(12.5,4.5,10) rot=(0,0,1;0rad)
  Solid = false
  Source = -> Face089
  Symmetric = false
FEATURE [Part::Feature] Face090
  shape: bbox 3.5 x 30.2 x 2e-07 mm, 1 faces, 0 solids (baked)
FEATURE [Part::Revolution] Revolve094  label="backCaseScrewPost003"
  Angle = 360
  Axis = (0,1,0)
  Base = (0,0,0)
  FaceMakerClass = Part::FaceMakerBullseye
  Placement = pos=(12.5,4.5,62) rot=(0,0,1;0rad)
  Solid = false
  Source = -> Face090
  Symmetric = false
FEATURE [Part::Box] Box015  label="Cube011"
  AttacherType = Attacher::AttachEngine3D
  Height = 28.8
  Length = 3
  Placement = pos=(107.3,28,21.6) rot=(0,0,1;0rad)
  Width = 7
FEATURE [Part::Box] Box016  label="Cube012"
  AttacherType = Attacher::AttachEngine3D
  Height = 3
  Length = 7.4
  Placement = pos=(107.3,28,18.6) rot=(0,0,1;0rad)
  Width = 7
FEATURE [Part::Box] Box017  label="Cube013"
  AttacherType = Attacher::AttachEngine3D
  Height = 3
  Length = 7.4
  Placement = pos=(107.3,28,50.4) rot=(0,0,1;0rad)
  Width = 7
FEATURE [Part::Cylinder] Cylinder024
  Angle = 360
  AttacherType = Attacher::AttachEngine3D
  Height = 20
  Placement = pos=(0,0,36.15) rot=(0,0,1;0rad)
  Radius = 14.3
FEATURE [Part::Cylinder] Cylinder025
  Angle = 360
  AttacherType = Attacher::AttachEngine3D
  Height = 10
  Placement = pos=(0,0,36.15) rot=(0,0,1;0rad)
  Radius = 4
FEATURE [Part::MultiFuse] Fusion066  label="removeToCreteHoleForPlugHousing009"
  Placement = pos=(70,19,36) rot=(0,1,0;1.5708rad)
  Shapes = -> [Cylinder024,Cylinder025]
FEATURE [Part::MultiFuse] Fusion065  label="plugHousingBracketHolder002"
  Shapes = -> [Box017,Box015,Box016]
FEATURE [Part::Cut] Cut025  label="plugHousingBracketHolder003"
  Base = -> Fusion065
  Placement = pos=(7,0,0) rot=(0,0,1;0rad)
  Tool = -> Fusion066
FEATURE [Sketcher::SketchObject] Sketch047
  FullyConstrained = false
  Placement = pos=(0,0,0) rot=(1,0,0;1.5708rad)
  sketch-geometry (24):
    g0: ArcOfCircle CenterX=-4 CenterY=-10.5 CenterZ=0 NormalX=0 NormalY=0 NormalZ=1 AngleXU=0 Radius=1.5 StartAngle=6e-16 EndAngle=3.14159
    g1: ArcOfCircle CenterX=-34.2 CenterY=-10.5 CenterZ=0 NormalX=0 NormalY=0 NormalZ=1 AngleXU=0 Radius=1.5 StartAngle=0 EndAngle=3.14159
    g2: ArcOfCircle CenterX=-34.2 CenterY=-27.7 CenterZ=0 NormalX=0 NormalY=0 NormalZ=1 AngleXU=0 Radius=1.5 StartAngle=3.14159 EndAngle=6.28319
    g3: ArcOfCircle CenterX=-4 CenterY=-27.7 CenterZ=0 NormalX=0 NormalY=0 NormalZ=1 AngleXU=0 Radius=1.5 StartAngle=3.1416 EndAngle=6.28319
    g4: ArcOfCircle CenterX=-10 CenterY=-4.3 CenterZ=0 NormalX=0 NormalY=0 NormalZ=1 AngleXU=0 Radius=1.5 StartAngle=2e-16 EndAngle=3.14159
    g5: ArcOfCircle CenterX=-16.1 CenterY=-1.8 CenterZ=0 NormalX=0 NormalY=0 NormalZ=1 AngleXU=0 Radius=1.5 StartAngle=5e-16 EndAngle=3.14159
    g6: ArcOfCircle CenterX=-22.1 CenterY=-1.8 CenterZ=0 NormalX=0 NormalY=0 NormalZ=1 AngleXU=0 Radius=1.5 StartAngle=5e-16 EndAngle=3.14159
    g7: ArcOfCircle CenterX=-28.2 CenterY=-4.3 CenterZ=0 NormalX=0 NormalY=0 NormalZ=1 AngleXU=0 Radius=1.5 StartAngle=2e-16 EndAngle=3.14159
    g8: ArcOfCircle CenterX=-10 CenterY=-33.9 CenterZ=0 NormalX=0 NormalY=0 NormalZ=1 AngleXU=0 Radius=1.5 StartAngle=3.14159 EndAngle=6.28319
    g9: ArcOfCircle CenterX=-16.1 CenterY=-36.4 CenterZ=0 NormalX=0 NormalY=0 NormalZ=1 AngleXU=0 Radius=1.5 StartAngle=3.14159 EndAngle=6.28319
    g10: ArcOfCircle CenterX=-22.1 CenterY=-36.4 CenterZ=0 NormalX=0 NormalY=0 NormalZ=1 AngleXU=0 Radius=1.5 StartAngle=3.14159 EndAngle=6.28319
    g11: ArcOfCircle CenterX=-28.2 CenterY=-33.9 CenterZ=0 NormalX=0 NormalY=0 NormalZ=1 AngleXU=0 Radius=1.5 StartAngle=3.14159 EndAngle=6.28319
    g12: LineSegment StartX=-35.7 StartY=-10.5 StartZ=0 EndX=-35.7 EndY=-27.7 EndZ=0
    g13: LineSegment StartX=-32.7 StartY=-10.5 StartZ=0 EndX=-32.7 EndY=-27.7 EndZ=0
    g14: LineSegment StartX=-29.7 StartY=-33.9 StartZ=0 EndX=-29.7 EndY=-4.3 EndZ=0
    g15: LineSegment StartX=-26.7 StartY=-33.9 StartZ=0 EndX=-26.7 EndY=-4.3 EndZ=0
    g16: LineSegment StartX=-2.5 StartY=-10.5 StartZ=0 EndX=-2.5 EndY=-27.7 EndZ=0
    g17: LineSegment StartX=-8.5 StartY=-4.3 StartZ=0 EndX=-8.5 EndY=-33.9 EndZ=0
    g18: LineSegment StartX=-5.5 StartY=-10.5 StartZ=0 EndX=-5.5 EndY=-27.7 EndZ=0
    g19: LineSegment StartX=-11.5 StartY=-4.3 StartZ=0 EndX=-11.5 EndY=-33.9 EndZ=0
    g20: LineSegment StartX=-14.6 StartY=-1.8 StartZ=0 EndX=-14.6 EndY=-36.4 EndZ=0
    g21: LineSegment StartX=-17.6 StartY=-1.8 StartZ=0 EndX=-17.6 EndY=-36.4 EndZ=0
    g22: LineSegment StartX=-20.6 StartY=-36.4 StartZ=0 EndX=-20.6 EndY=-1.8 EndZ=0
    g23: LineSegment StartX=-23.6 StartY=-1.8 StartZ=0 EndX=-23.6 EndY=-36.4 EndZ=0
  constraints (48):
    c: Block(g0)
    c: Block(g1)
    c: Block(g2)
    c: Block(g3)
    c: Block(g4)
    c: Block(g5)
    c: Block(g6)
    c: Block(g7)
    c: Block(g8)
    c: Block(g9)
    c: Block(g10)
    c: Block(g11)
    c: Coincident(g12,g1)
    c: Coincident(g12,g2)
    c: Vertical(g12)
    c: Coincident(g13,g1)
    c: Coincident(g13,g2)
    c: Vertical(g13)
    c: Coincident(g14,g11)
    c: Coincident(g14,g7)
    c: Vertical(g14)
    c: Coincident(g15,g11)
    c: Coincident(g15,g7)
    c: Vertical(g15)
    c: Coincident(g16,g0)
    c: Coincident(g16,g3)
    c: Vertical(g16)
    c: Coincident(g17,g4)
    c: Coincident(g17,g8)
    c: Vertical(g17)
    c: Coincident(g18,g0)
    c: Coincident(g18,g3)
    c: Vertical(g18)
    c: Coincident(g19,g4)
    c: Coincident(g19,g8)
    c: Vertical(g19)
    c: Coincident(g20,g5)
    c: Coincident(g20,g9)
    c: Vertical(g20)
    c: Coincident(g21,g5)
    c: Coincident(g21,g9)
    c: Vertical(g21)
    c: Coincident(g22,g10)
    c: Coincident(g22,g6)
    c: Vertical(g22)
    c: Coincident(g23,g6)
    c: Coincident(g23,g10)
    c: Vertical(g23)
FEATURE [Part::Extrusion] Extrude038  label="removeToCreateFanGrillHoles001"
  Base = -> Sketch047
  Dir = (0,-1,6e-16)
  DirMode = 2
  FaceMakerClass = Part::FaceMakerBullseye
  LengthFwd = 10
  LengthRev = 0
  Placement = pos=(65.4,44,54.82) rot=(0,0,1;0rad)
  Solid = true
  Symmetric = false
FEATURE [Part::Feature] Wire004
  shape: bbox 11 x 5.2 x 2e-07 mm, 0 faces, 0 solids (baked)
FEATURE [Part::Revolution] Revolve095
  Angle = 360
  Axis = (0,1,0)
  Base = (0,0,0)
  FaceMakerClass = Part::FaceMakerBullseye
  Placement = pos=(30.3,38,19.7) rot=(0,0,1;0rad)
  Solid = true
  Source = -> Wire004
  Symmetric = false
FEATURE [Part::Feature] Wire005
  shape: bbox 11 x 5.2 x 2e-07 mm, 0 faces, 0 solids (baked)
FEATURE [Part::Revolution] Revolve096
  Angle = 360
  Axis = (0,1,0)
  Base = (0,0,0)
  FaceMakerClass = Part::FaceMakerBullseye
  Placement = pos=(30.3,38,51.7) rot=(0,0,1;0rad)
  Solid = true
  Source = -> Wire005
  Symmetric = false
FEATURE [Part::Feature] Wire006
  shape: bbox 11 x 5.2 x 2e-07 mm, 0 faces, 0 solids (baked)
FEATURE [Part::Revolution] Revolve097
  Angle = 360
  Axis = (0,1,0)
  Base = (0,0,0)
  FaceMakerClass = Part::FaceMakerBullseye
  Placement = pos=(62.3,38,51.7) rot=(0,0,1;0rad)
  Solid = true
  Source = -> Wire006
  Symmetric = false
FEATURE [Part::Feature] Wire007
  shape: bbox 11 x 5.2 x 2e-07 mm, 0 faces, 0 solids (baked)
FEATURE [Part::Revolution] Revolve098
  Angle = 360
  Axis = (0,1,0)
  Base = (0,0,0)
  FaceMakerClass = Part::FaceMakerBullseye
  Placement = pos=(62.3,38,19.7) rot=(0,0,1;0rad)
  Solid = true
  Source = -> Wire007
  Symmetric = false
FEATURE [Part::MultiFuse] Fusion067  label="fanScrewHousing002"
  Shapes = -> [Revolve098,Revolve097,Revolve096,Revolve095]
FEATURE [Part::Feature] Face091 .. Face094  x4 (patterned run collapsed; names and placements below)
  shape: bbox 3.5 x 17.8 x 2e-07 mm, 1 faces, 0 solids (baked)
FEATURE [Part::Revolution] Revolve099  label="removeToCreateScrewAndThreadedInsertHole026"
  Angle = 360
  Axis = (0,1,0)
  Base = (0,0,0)
  FaceMakerClass = Part::FaceMakerBullseye
  Placement = pos=(62.3,30.3,19.7) rot=(0,0,1;0rad)
  Solid = false
  Source = -> Face091
  Symmetric = false
FEATURE [Part::Revolution] Revolve100  label="removeToCreateScrewAndThreadedInsertHole027"
  Angle = 360
  Axis = (0,1,0)
  Base = (0,0,0)
  FaceMakerClass = Part::FaceMakerBullseye
  Placement = pos=(62.3,30.3,51.7) rot=(0,0,1;0rad)
  Solid = false
  Source = -> Face092
  Symmetric = false
FEATURE [Part::Revolution] Revolve101  label="removeToCreateScrewAndThreadedInsertHole028"
  Angle = 360
  Axis = (0,1,0)
  Base = (0,0,0)
  FaceMakerClass = Part::FaceMakerBullseye
  Placement = pos=(30.3,30.3,19.7) rot=(0,0,1;0rad)
  Solid = false
  Source = -> Face093
  Symmetric = false
FEATURE [Part::Revolution] Revolve102  label="removeToCreateScrewAndThreadedInsertHole029"
  Angle = 360
  Axis = (0,1,0)
  Base = (0,0,0)
  FaceMakerClass = Part::FaceMakerBullseye
  Placement = pos=(30.3,30.3,51.7) rot=(0,0,1;0rad)
  Solid = false
  Source = -> Face094
  Symmetric = false
FEATURE [Part::MultiFuse] Fusion068  label="createThreadedInsertHolesForFan002"
  Shapes = -> [Revolve099,Revolve100,Revolve101,Revolve102]
FEATURE [Part::Cut] Cut026  label="fanScrewHousing003"
  Base = -> Fusion067
  Tool = -> Fusion068
FEATURE [Sketcher::SketchObject] Sketch048
  FullyConstrained = false
  Placement = pos=(0,0,0) rot=(1,0,0;1.5708rad)
  sketch-geometry (24):
    g0: ArcOfCircle CenterX=-4 CenterY=-10.5 CenterZ=0 NormalX=0 NormalY=0 NormalZ=1 AngleXU=0 Radius=1.5 StartAngle=6e-16 EndAngle=3.14159
    g1: ArcOfCircle CenterX=-34.2 CenterY=-10.5 CenterZ=0 NormalX=0 NormalY=0 NormalZ=1 AngleXU=0 Radius=1.5 StartAngle=0 EndAngle=3.14159
    g2: ArcOfCircle CenterX=-34.2 CenterY=-27.7 CenterZ=0 NormalX=0 NormalY=0 NormalZ=1 AngleXU=0 Radius=1.5 StartAngle=3.14159 EndAngle=6.28319
    g3: ArcOfCircle CenterX=-4 CenterY=-27.7 CenterZ=0 NormalX=0 NormalY=0 NormalZ=1 AngleXU=0 Radius=1.5 StartAngle=3.1416 EndAngle=6.28319
    g4: ArcOfCircle CenterX=-10 CenterY=-4.3 CenterZ=0 NormalX=0 NormalY=0 NormalZ=1 AngleXU=0 Radius=1.5 StartAngle=2e-16 EndAngle=3.14159
    g5: ArcOfCircle CenterX=-16.1 CenterY=-1.8 CenterZ=0 NormalX=0 NormalY=0 NormalZ=1 AngleXU=0 Radius=1.5 StartAngle=5e-16 EndAngle=3.14159
    g6: ArcOfCircle CenterX=-22.1 CenterY=-1.8 CenterZ=0 NormalX=0 NormalY=0 NormalZ=1 AngleXU=0 Radius=1.5 StartAngle=5e-16 EndAngle=3.14159
    g7: ArcOfCircle CenterX=-28.2 CenterY=-4.3 CenterZ=0 NormalX=0 NormalY=0 NormalZ=1 AngleXU=0 Radius=1.5 StartAngle=2e-16 EndAngle=3.14159
    g8: ArcOfCircle CenterX=-10 CenterY=-33.9 CenterZ=0 NormalX=0 NormalY=0 NormalZ=1 AngleXU=0 Radius=1.5 StartAngle=3.14159 EndAngle=6.28319
    g9: ArcOfCircle CenterX=-16.1 CenterY=-36.4 CenterZ=0 NormalX=0 NormalY=0 NormalZ=1 AngleXU=0 Radius=1.5 StartAngle=3.14159 EndAngle=6.28319
    g10: ArcOfCircle CenterX=-22.1 CenterY=-36.4 CenterZ=0 NormalX=0 NormalY=0 NormalZ=1 AngleXU=0 Radius=1.5 StartAngle=3.14159 EndAngle=6.28319
    g11: ArcOfCircle CenterX=-28.2 CenterY=-33.9 CenterZ=0 NormalX=0 NormalY=0 NormalZ=1 AngleXU=0 Radius=1.5 StartAngle=3.14159 EndAngle=6.28319
    g12: LineSegment StartX=-35.7 StartY=-10.5 StartZ=0 EndX=-35.7 EndY=-27.7 EndZ=0
    g13: LineSegment StartX=-32.7 StartY=-10.5 StartZ=0 EndX=-32.7 EndY=-27.7 EndZ=0
    g14: LineSegment StartX=-29.7 StartY=-33.9 StartZ=0 EndX=-29.7 EndY=-4.3 EndZ=0
    g15: LineSegment StartX=-26.7 StartY=-33.9 StartZ=0 EndX=-26.7 EndY=-4.3 EndZ=0
    g16: LineSegment StartX=-2.5 StartY=-10.5 StartZ=0 EndX=-2.5 EndY=-27.7 EndZ=0
    g17: LineSegment StartX=-8.5 StartY=-4.3 StartZ=0 EndX=-8.5 EndY=-33.9 EndZ=0
    g18: LineSegment StartX=-5.5 StartY=-10.5 StartZ=0 EndX=-5.5 EndY=-27.7 EndZ=0
    g19: LineSegment StartX=-11.5 StartY=-4.3 StartZ=0 EndX=-11.5 EndY=-33.9 EndZ=0
    g20: LineSegment StartX=-14.6 StartY=-1.8 StartZ=0 EndX=-14.6 EndY=-36.4 EndZ=0
    g21: LineSegment StartX=-17.6 StartY=-1.8 StartZ=0 EndX=-17.6 EndY=-36.4 EndZ=0
    g22: LineSegment StartX=-20.6 StartY=-36.4 StartZ=0 EndX=-20.6 EndY=-1.8 EndZ=0
    g23: LineSegment StartX=-23.6 StartY=-1.8 StartZ=0 EndX=-23.6 EndY=-36.4 EndZ=0
  constraints (48):
    c: Block(g0)
    c: Block(g1)
    c: Block(g2)
    c: Block(g3)
    c: Block(g4)
    c: Block(g5)
    c: Block(g6)
    c: Block(g7)
    c: Block(g8)
    c: Block(g9)
    c: Block(g10)
    c: Block(g11)
    c: Coincident(g12,g1)
    c: Coincident(g12,g2)
    c: Vertical(g12)
    c: Coincident(g13,g1)
    c: Coincident(g13,g2)
    c: Vertical(g13)
    c: Coincident(g14,g11)
    c: Coincident(g14,g7)
    c: Vertical(g14)
    c: Coincident(g15,g11)
    c: Coincident(g15,g7)
    c: Vertical(g15)
    c: Coincident(g16,g0)
    c: Coincident(g16,g3)
    c: Vertical(g16)
    c: Coincident(g17,g4)
    c: Coincident(g17,g8)
    c: Vertical(g17)
    c: Coincident(g18,g0)
    c: Coincident(g18,g3)
    c: Vertical(g18)
    c: Coincident(g19,g4)
    c: Coincident(g19,g8)
    c: Vertical(g19)
    c: Coincident(g20,g5)
    c: Coincident(g20,g9)
    c: Vertical(g20)
    c: Coincident(g21,g5)
    c: Coincident(g21,g9)
    c: Vertical(g21)
    c: Coincident(g22,g10)
    c: Coincident(g22,g6)
    c: Vertical(g22)
    c: Coincident(g23,g6)
    c: Coincident(g23,g10)
    c: Vertical(g23)
FEATURE [Part::Extrusion] Extrude039  label="removeToCreateFanGrillHoles002"
  Base = -> Sketch048
  Dir = (0,-1,6e-16)
  DirMode = 2
  FaceMakerClass = Part::FaceMakerBullseye
  LengthFwd = 10
  LengthRev = 0
  Placement = pos=(65.4,44,54.82) rot=(0,0,1;0rad)
  Solid = true
  Symmetric = false
FEATURE [Part::Cut] Cut027  label="fanScrewHousing004"
  Base = -> Cut026
  Tool = -> Extrude038
FEATURE [Part::Cut] Cut028  label="top014"
  Base = -> Fillet026
  Tool = -> Extrude039
FEATURE [Part::Feature] Face095 .. Face098  x4 (patterned run collapsed; names and placements below)
  shape: bbox 3.5 x 17.8 x 2e-07 mm, 1 faces, 0 solids (baked)
FEATURE [Part::Revolution] Revolve103  label="removeToCreateScrewAndThreadedInsertHole030"
  Angle = 360
  Axis = (0,1,0)
  Base = (0,0,0)
  FaceMakerClass = Part::FaceMakerBullseye
  Placement = pos=(62.3,30.3,19.7) rot=(0,0,1;0rad)
  Solid = false
  Source = -> Face095
  Symmetric = false
FEATURE [Part::Revolution] Revolve104  label="removeToCreateScrewAndThreadedInsertHole031"
  Angle = 360
  Axis = (0,1,0)
  Base = (0,0,0)
  FaceMakerClass = Part::FaceMakerBullseye
  Placement = pos=(62.3,30.3,51.7) rot=(0,0,1;0rad)
  Solid = false
  Source = -> Face096
  Symmetric = false
FEATURE [Part::Revolution] Revolve105  label="removeToCreateScrewAndThreadedInsertHole032"
  Angle = 360
  Axis = (0,1,0)
  Base = (0,0,0)
  FaceMakerClass = Part::FaceMakerBullseye
  Placement = pos=(30.3,30.3,19.7) rot=(0,0,1;0rad)
  Solid = false
  Source = -> Face097
  Symmetric = false
FEATURE [Part::Revolution] Revolve106  label="removeToCreateScrewAndThreadedInsertHole033"
  Angle = 360
  Axis = (0,1,0)
  Base = (0,0,0)
  FaceMakerClass = Part::FaceMakerBullseye
  Placement = pos=(30.3,30.3,51.7) rot=(0,0,1;0rad)
  Solid = false
  Source = -> Face098
  Symmetric = false
FEATURE [Part::MultiFuse] Fusion069  label="createThreadedInsertHolesForFan003"
  Shapes = -> [Revolve103,Revolve104,Revolve105,Revolve106]
FEATURE [Part::Cut] Cut029  label="top015"
  Base = -> Cut028
  Tool = -> Fusion054
FEATURE [Part::Cut] Cut030  label="fanScrewHousing005"
  Base = -> Cut027
  Tool = -> Fusion069
FEATURE [Part::Cylinder] Cylinder026  label="removeToCreteHoleForPlugHousing010"
  Angle = 360
  AttacherType = Attacher::AttachEngine3D
  Height = 20
  Placement = pos=(-2,19,36) rot=(0,1,0;1.5708rad)
  Radius = 14.3
FEATURE [Part::Box] Box018  label="removeToCreteHoleForPlugHousing011"
  AttacherType = Attacher::AttachEngine3D
  Height = 28.6
  Length = 10
  Placement = pos=(-2,0,21.7) rot=(0,0,1;0rad)
  Width = 19
FEATURE [Part::Box] Box019  label="wireHolderBottomCaseBit"
  AttacherType = Attacher::AttachEngine3D
  Height = 28
  Length = 3
  Placement = pos=(0,0,22) rot=(0,0,1;0rad)
  Width = 21
FEATURE [Part::Cylinder] Cylinder027  label="removeToCreteHoleForPlugHousing012"
  Angle = 360
  AttacherType = Attacher::AttachEngine3D
  Height = 20
  Placement = pos=(-2,19,36) rot=(0,1,0;1.5708rad)
  Radius = 14.3
FEATURE [Part::Cut] Cut031  label="wireHolderBottomCaseBit001"
  Base = -> Box019
  Tool = -> Cylinder027
FEATURE [Part::MultiFuse] Fusion070  label="removeToCreteHoleForPlugHousing013"
  Shapes = -> [Box018,Cylinder026]
FEATURE [Part::Cut] Cut032  label="top016"
  Base = -> Cut029
  Tool = -> Fusion070
FEATURE [Part::Cylinder] Cylinder028
  Angle = 360
  AttacherType = Attacher::AttachEngine3D
  Height = 20
  Placement = pos=(0,0,36.15) rot=(0,0,1;0rad)
  Radius = 14.3
FEATURE [Part::Cylinder] Cylinder029
  Angle = 360
  AttacherType = Attacher::AttachEngine3D
  Height = 10
  Placement = pos=(0,0,36.15) rot=(0,0,1;0rad)
  Radius = 4
FEATURE [Part::MultiFuse] Fusion071  label="removeToCreteHoleForPlugHousing014"
  Placement = pos=(70,19,36) rot=(0,1,0;1.5708rad)
  Shapes = -> [Cylinder028,Cylinder029]
FEATURE [Sketcher::SketchObject] Sketch049  label="topSketch011"
  FullyConstrained = true
  sketch-geometry (4):
    g0: ArcOfCircle CenterX=105 CenterY=19 CenterZ=0 NormalX=0 NormalY=0 NormalZ=1 AngleXU=0 Radius=20.6155 StartAngle=5.54125 EndAngle=6.28319
    g1: ArcOfCircle CenterX=105 CenterY=19 CenterZ=0 NormalX=0 NormalY=0 NormalZ=1 AngleXU=0 Radius=13 StartAngle=5.54125 EndAngle=6.28319
    g2: LineSegment StartX=118 StartY=19 StartZ=0 EndX=125.616 EndY=19 EndZ=0
    g3: LineSegment StartX=114.583 StartY=10.2157 StartZ=0 EndX=120.197 EndY=5.06982 EndZ=0
  constraints (7):
    c: Block(g0)
    c: Block(g1)
    c: Coincident(g2,g1)
    c: Coincident(g2,g0)
    c: Horizontal(g2)
    c: Coincident(g3,g1)
    c: Coincident(g3,g0)
FEATURE [Part::Box] Box020  label="removeToCreteHoleForPlugHousing015"
  AttacherType = Attacher::AttachEngine3D
  Height = 28.6
  Length = 20
  Placement = pos=(106.15,0,21.7) rot=(0,0,1;0rad)
  Width = 19
FEATURE [Part::MultiFuse] Fusion072  label="removeToCreteHoleForPlugHousing016"
  Shapes = -> [Box020,Fusion071]
FEATURE [Part::Cut] Cut033  label="removeToCreteHoleForPlugHousing017"
  Base = -> Cut032
  Tool = -> Fusion072
FEATURE [Part::Cylinder] Cylinder030
  Angle = 360
  AttacherType = Attacher::AttachEngine3D
  Height = 20
  Placement = pos=(0,0,36.15) rot=(0,0,1;0rad)
  Radius = 14.3
FEATURE [Part::Cylinder] Cylinder031
  Angle = 360
  AttacherType = Attacher::AttachEngine3D
  Height = 10
  Placement = pos=(0,0,36.15) rot=(0,0,1;0rad)
  Radius = 4
FEATURE [Part::Box] Box021  label="removeToCreteHoleForPlugHousing019"
  AttacherType = Attacher::AttachEngine3D
  Height = 28.6
  Length = 20
  Placement = pos=(106.15,0,21.7) rot=(0,0,1;0rad)
  Width = 19
FEATURE [Part::MultiFuse] Fusion074  label="removeToCreteHoleForPlugHousing020"
  Placement = pos=(70,19,36) rot=(0,1,0;1.5708rad)
  Shapes = -> [Cylinder030,Cylinder031]
FEATURE [Part::MultiFuse] Fusion073  label="removeToCreteHoleForPlugHousing018"
  Placement = pos=(0,0,28.3) rot=(0,0,1;0rad)
  Shapes = -> [Box021,Fusion074]
FEATURE [Part::Cylinder] Cylinder032
  Angle = 360
  AttacherType = Attacher::AttachEngine3D
  Height = 20
  Placement = pos=(0,0,36.15) rot=(0,0,1;0rad)
  Radius = 14.3
FEATURE [Part::Cylinder] Cylinder033
  Angle = 360
  AttacherType = Attacher::AttachEngine3D
  Height = 10
  Placement = pos=(0,0,36.15) rot=(0,0,1;0rad)
  Radius = 4
FEATURE [Part::Box] Box022  label="removeToCreteHoleForPlugHousing021"
  AttacherType = Attacher::AttachEngine3D
  Height = 28.6
  Length = 20
  Placement = pos=(106.15,0,21.7) rot=(0,0,1;0rad)
  Width = 19
FEATURE [Part::MultiFuse] Fusion076  label="removeToCreteHoleForPlugHousing023"
  Placement = pos=(70,19,36) rot=(0,1,0;1.5708rad)
  Shapes = -> [Cylinder032,Cylinder033]
FEATURE [Part::MultiFuse] Fusion075  label="removeToCreteHoleForPlugHousing022"
  Placement = pos=(0,0,-28.3) rot=(0,0,1;0rad)
  Shapes = -> [Box022,Fusion076]
FEATURE [Part::MultiFuse] Fusion077  label="removeToCreatePlugHousingBottomBit"
  Shapes = -> [Fusion075,Fusion073]
FEATURE [Part::Cylinder] Cylinder034
  Angle = 360
  AttacherType = Attacher::AttachEngine3D
  Height = 20
  Placement = pos=(0,0,36.15) rot=(0,0,1;0rad)
  Radius = 14
FEATURE [Part::Cylinder] Cylinder035
  Angle = 360
  AttacherType = Attacher::AttachEngine3D
  Height = 10
  Placement = pos=(0,0,36.15) rot=(0,0,1;0rad)
  Radius = 4
FEATURE [Part::MultiFuse] Fusion078  label="removeToCreteHoleForPlugHousing024"
  Placement = pos=(70,19,36) rot=(0,1,0;1.5708rad)
  Shapes = -> [Cylinder034,Cylinder035]
FEATURE [Part::MultiFuse] Fusion079  label="removeToCreatePlugHousingBottomBit001"
  Shapes = -> [Fusion078,Fusion077]
FEATURE [Part::Extrusion] Extrude040  label="bottomPlugHousingBit"
  Base = -> Sketch049
  Dir = (0,0,1)
  DirMode = 2
  FaceMakerClass = Part::FaceMakerBullseye
  LengthFwd = 72
  LengthRev = 0
  Solid = true
  Symmetric = false
FEATURE [Part::Cut] Cut034  label="bottomPlugHousingBit001"
  Base = -> Extrude040
  Placement = pos=(-0.09,0,0) rot=(0,0,1;0rad)
  Tool = -> Fusion079
FEATURE [Part::Box] Box023  label="Cube014"
  AttacherType = Attacher::AttachEngine3D
  Height = 16
  Length = 8
  Placement = pos=(12.7,31.52,28) rot=(0,0,1;0rad)
  Width = 4
FEATURE [Part::Cylinder] Cylinder036
  Angle = 360
  AttacherType = Attacher::AttachEngine3D
  Height = 10
  Placement = pos=(0,0,36.15) rot=(0,0,1;0rad)
  Radius = 4
FEATURE [Part::Cylinder] Cylinder037
  Angle = 360
  AttacherType = Attacher::AttachEngine3D
  Height = 20
  Placement = pos=(0,0,36.15) rot=(0,0,1;0rad)
  Radius = 8.2
FEATURE [Part::MultiFuse] Fusion080  label="removeToCreteHoleForPlugHousing025"
  Placement = pos=(-42,19,36) rot=(0,1,0;1.5708rad)
  Shapes = -> [Cylinder037,Cylinder036]
FEATURE [Sketcher::SketchObject] Sketch050  label="topSketch012"
  FullyConstrained = true
  sketch-geometry (4):
    g0: LineSegment StartX=16.8446 StartY=31.512 StartZ=0 EndX=16.3251 EndY=34.4666 EndZ=0
    g1: ArcOfCircle CenterX=19 CenterY=19.2524 CenterZ=0 NormalX=0 NormalY=0 NormalZ=1 AngleXU=0 Radius=15.4476 StartAngle=1.74483 EndAngle=2.72717
    g2: ArcOfCircle CenterX=19 CenterY=19.2524 CenterZ=0 NormalX=0 NormalY=0 NormalZ=1 AngleXU=0 Radius=12.4476 StartAngle=1.74483 EndAngle=2.73189
    g3: LineSegment StartX=4.86004 StartY=25.4725 StartZ=0 EndX=7.58253 EndY=24.2107 EndZ=0
  constraints (7):
    c: Block(g0)
    c: Coincident(g1,g0)
    c: Coincident(g2,g0)
    c: Coincident(g3,g1)
    c: Coincident(g3,g2)
    c: Block(g1)
    c: Block(g2)
FEATURE [Part::Extrusion] Extrude041
  Base = -> Sketch050
  Dir = (0,0,1)
  DirMode = 2
  FaceMakerClass = Part::FaceMakerBullseye
  LengthFwd = 10.6
  LengthRev = 0
  Placement = pos=(0,0,31) rot=(0,0,1;0rad)
  Solid = true
  Symmetric = false
FEATURE [Part::Cut] Cut035
  Base = -> Extrude041
  Placement = pos=(0,0,-0.3) rot=(0,0,1;0rad)
  Tool = -> Fusion080
FEATURE [Part::Cut] Cut036
  Base = -> Box023
  Tool = -> Cut035
FEATURE [Part::Fillet] Fillet027
  Base = -> Cut036
  Edges = 1 edges r=0.7: [Edge13]
FEATURE [Part::Fillet] Fillet028
  Base = -> Fillet027
  Edges = 1 edges r=0.7: [Edge13]
FEATURE [Part::Fillet] Fillet029
  Base = -> Fillet028
  Edges = 1 edges r=0.7: [Edge16]
FEATURE [Part::Fillet] Fillet030
  Base = -> Fillet029
  Edges = 1 edges r=0.7: [Edge11]
FEATURE [Part::Fillet] Fillet031
  Base = -> Fillet030
  Edges = 1 edges r=0.7: [Edge10]
FEATURE [Part::Fillet] Fillet032
  Base = -> Fillet031
  Edges = 1 edges r=1.2: [Edge5]
FEATURE [Part::Fillet] Fillet033
  Base = -> Fillet032
  Edges = 1 edges r=1.2: [Edge12]
FEATURE [Part::Fillet] Fillet034  label="wireHousingRetainer"
  Base = -> Fillet033
  Edges = 1 edges r=2: [Edge1]
  Placement = pos=(0.3,0,0) rot=(0,0,1;0rad)
FEATURE [Part::Feature] Face099
  shape: bbox 3.5 x 17.8 x 2e-07 mm, 1 faces, 0 solids (baked)
FEATURE [Part::Revolution] Revolve107  label="removeToCreateScrewAndThreadedInsertHole034"
  Angle = 360
  Axis = (0,1,0)
  Base = (0,0,0)
  FaceMakerClass = Part::FaceMakerBullseye
  Placement = pos=(12.5,0,10) rot=(0,0,1;0rad)
  Solid = false
  Source = -> Face099
  Symmetric = false
FEATURE [Part::Feature] Face100
  shape: bbox 3.5 x 17.8 x 2e-07 mm, 1 faces, 0 solids (baked)
FEATURE [Part::Revolution] Revolve108  label="removeToCreateScrewAndThreadedInsertHole035"
  Angle = 360
  Axis = (0,1,0)
  Base = (0,0,0)
  FaceMakerClass = Part::FaceMakerBullseye
  Placement = pos=(12.5,0,62) rot=(0,0,1;0rad)
  Solid = false
  Source = -> Face100
  Symmetric = false
FEATURE [Part::Feature] Face101
  shape: bbox 3.5 x 17.8 x 2e-07 mm, 1 faces, 0 solids (baked)
FEATURE [Part::Revolution] Revolve109  label="removeToCreateScrewAndThreadedInsertHole036"
  Angle = 360
  Axis = (0,1,0)
  Base = (0,0,0)
  FaceMakerClass = Part::FaceMakerBullseye
  Placement = pos=(89.5,0,68.5) rot=(0,0,1;0rad)
  Solid = false
  Source = -> Face101
  Symmetric = false
FEATURE [Part::Feature] Face102
  shape: bbox 3.5 x 17.8 x 2e-07 mm, 1 faces, 0 solids (baked)
FEATURE [Part::Revolution] Revolve110  label="removeToCreateScrewAndThreadedInsertHole037"
  Angle = 360
  Axis = (0,1,0)
  Base = (0,0,0)
  FaceMakerClass = Part::FaceMakerBullseye
  Placement = pos=(89.5,0,3.5) rot=(0,0,1;0rad)
  Solid = false
  Source = -> Face102
  Symmetric = false
FEATURE [Part::Feature] Face103
  shape: bbox 3.5 x 17.8 x 2e-07 mm, 1 faces, 0 solids (baked)
FEATURE [Part::Revolution] Revolve111  label="removeToCreateScrewAndThreadedInsertHole038"
  Angle = 360
  Axis = (0,1,0)
  Base = (0,0,0)
  FaceMakerClass = Part::FaceMakerBullseye
  Placement = pos=(109.5,4.7,3.5) rot=(0,0,1;0rad)
  Solid = false
  Source = -> Face103
  Symmetric = false
FEATURE [Part::Feature] Face104
  shape: bbox 3.5 x 17.8 x 2e-07 mm, 1 faces, 0 solids (baked)
FEATURE [Part::Revolution] Revolve112  label="removeToCreateScrewAndThreadedInsertHole039"
  Angle = 360
  Axis = (0,1,0)
  Base = (0,0,0)
  FaceMakerClass = Part::FaceMakerBullseye
  Placement = pos=(109.5,4.7,68.5) rot=(0,0,1;0rad)
  Solid = false
  Source = -> Face104
  Symmetric = false
FEATURE [Part::MultiFuse] Fusion081  label="removeToCreateScrewAndThreadedInsertHole040"
  Shapes = -> [Revolve107,Revolve108,Revolve109,Revolve110,Revolve111,Revolve112]
FEATURE [Part::MultiFuse] Fusion082  label="casePillars002"
  Shapes = -> [Revolve094,Revolve092,Revolve090,Revolve089,Revolve091,Revolve093]
FEATURE [Part::Cut] Cut037  label="casePillars003"
  Base = -> Fusion082
  Tool = -> Fusion081
FEATURE [Sketcher::SketchObject] Sketch051
  FullyConstrained = true
  Placement = pos=(117,19,0) rot=(0.57735,0.57735,0.57735;2.0944rad)
  sketch-geometry (48):
    g0: LineSegment StartX=-49.19 StartY=69.25 StartZ=0 EndX=-49.19 EndY=66.25 EndZ=0
    g1: LineSegment StartX=-49.19 StartY=63.5 StartZ=0 EndX=-49.19 EndY=60.5 EndZ=0
    g2: LineSegment StartX=-49.19 StartY=57.75 StartZ=0 EndX=-49.19 EndY=54.75 EndZ=0
    g3: LineSegment StartX=-49.19 StartY=52 StartZ=0 EndX=-49.19 EndY=49 EndZ=0
    g4: LineSegment StartX=-49.19 StartY=46.25 StartZ=0 EndX=-49.19 EndY=43.25 EndZ=0
    g5: LineSegment StartX=-49.19 StartY=40.5 StartZ=0 EndX=-49.19 EndY=37.5 EndZ=0
    g6: LineSegment StartX=-49.19 StartY=34.5 StartZ=0 EndX=-49.19 EndY=31.5 EndZ=0
    g7: LineSegment StartX=-49.19 StartY=28.75 StartZ=0 EndX=-49.19 EndY=25.75 EndZ=0
    g8: LineSegment StartX=-49.19 StartY=23 StartZ=0 EndX=-49.19 EndY=20 EndZ=0
    g9: LineSegment StartX=-49.19 StartY=17.25 StartZ=0 EndX=-49.19 EndY=14.25 EndZ=0
    g10: LineSegment StartX=-49.19 StartY=11.5 StartZ=0 EndX=-49.19 EndY=8.5 EndZ=0
    g11: LineSegment StartX=-49.19 StartY=5.75 StartZ=0 EndX=-49.19 EndY=2.75 EndZ=0
    g12: ArcOfCircle CenterX=-1.5 CenterY=67.75 CenterZ=0 NormalX=0 NormalY=0 NormalZ=1 AngleXU=0 Radius=1.5 StartAngle=4.71239 EndAngle=7.85398
    g13: ArcOfCircle CenterX=-1.5 CenterY=62 CenterZ=0 NormalX=0 NormalY=0 NormalZ=1 AngleXU=0 Radius=1.5 StartAngle=4.71239 EndAngle=7.85398
    g14: ArcOfCircle CenterX=-1.5 CenterY=56.25 CenterZ=0 NormalX=0 NormalY=0 NormalZ=1 AngleXU=0 Radius=1.5 StartAngle=4.71239 EndAngle=7.85398
    g15: ArcOfCircle CenterX=-11.49 CenterY=50.5 CenterZ=0 NormalX=0 NormalY=0 NormalZ=1 AngleXU=0 Radius=1.5 StartAngle=4.71239 EndAngle=7.85398
    g16: ArcOfCircle CenterX=-16.28 CenterY=44.75 CenterZ=0 NormalX=0 NormalY=0 NormalZ=1 AngleXU=0 Radius=1.5 StartAngle=4.71239 EndAngle=7.85398
    g17: ArcOfCircle CenterX=-18.2337 CenterY=39 CenterZ=0 NormalX=0 NormalY=0 NormalZ=1 AngleXU=0 Radius=1.5 StartAngle=4.71485 EndAngle=7.85398
    g18: ArcOfCircle CenterX=-16.2837 CenterY=27.25 CenterZ=0 NormalX=0 NormalY=0 NormalZ=1 AngleXU=0 Radius=1.5 StartAngle=4.71485 EndAngle=7.85398
    g19: ArcOfCircle CenterX=-18.2337 CenterY=33 CenterZ=0 NormalX=0 NormalY=0 NormalZ=1 AngleXU=0 Radius=1.5 StartAngle=4.71485 EndAngle=7.85398
    g20: ArcOfCircle CenterX=-11.49 CenterY=21.5 CenterZ=0 NormalX=0 NormalY=0 NormalZ=1 AngleXU=0 Radius=1.5 StartAngle=4.71239 EndAngle=7.85398
    g21: ArcOfCircle CenterX=-1.5 CenterY=4.25 CenterZ=0 NormalX=0 NormalY=0 NormalZ=1 AngleXU=0 Radius=1.5 StartAngle=4.71239 EndAngle=7.85398
    g22: ArcOfCircle CenterX=-1.5 CenterY=10 CenterZ=0 NormalX=0 NormalY=0 NormalZ=1 AngleXU=0 Radius=1.5 StartAngle=4.71239 EndAngle=7.85398
    g23: ArcOfCircle CenterX=-1.5 CenterY=15.75 CenterZ=0 NormalX=0 NormalY=0 NormalZ=1 AngleXU=0 Radius=1.5 StartAngle=4.71239 EndAngle=7.85398
    g24: LineSegment StartX=-49.19 StartY=69.25 StartZ=0 EndX=-1.5 EndY=69.25 EndZ=0
    g25: LineSegment StartX=-49.19 StartY=66.25 StartZ=0 EndX=-1.5 EndY=66.25 EndZ=0
    g26: LineSegment StartX=-49.19 StartY=63.5 StartZ=0 EndX=-1.5 EndY=63.5 EndZ=0
    g27: LineSegment StartX=-49.19 StartY=60.5 StartZ=0 EndX=-1.5 EndY=60.5 EndZ=0
    g28: LineSegment StartX=-49.19 StartY=57.75 StartZ=0 EndX=-1.5 EndY=57.75 EndZ=0
    g29: LineSegment StartX=-49.19 StartY=54.75 StartZ=0 EndX=-1.5 EndY=54.75 EndZ=0
    g30: LineSegment StartX=-49.19 StartY=52 StartZ=0 EndX=-11.49 EndY=52 EndZ=0
    g31: LineSegment StartX=-49.19 StartY=49 StartZ=0 EndX=-11.49 EndY=49 EndZ=0
    g32: LineSegment StartX=-49.19 StartY=46.25 StartZ=0 EndX=-16.28 EndY=46.25 EndZ=0
    g33: LineSegment StartX=-49.19 StartY=43.25 StartZ=0 EndX=-16.28 EndY=43.25 EndZ=0
    g34: LineSegment StartX=-49.19 StartY=40.5 StartZ=0 EndX=-18.2337 EndY=40.5 EndZ=0
    g35: LineSegment StartX=-49.19 StartY=37.5 StartZ=0 EndX=-18.23 EndY=37.5 EndZ=0
    g36: LineSegment StartX=-49.19 StartY=34.5 StartZ=0 EndX=-18.2337 EndY=34.5 EndZ=0
    g37: LineSegment StartX=-49.19 StartY=31.5 StartZ=0 EndX=-18.23 EndY=31.5 EndZ=0
    g38: LineSegment StartX=-49.19 StartY=28.75 StartZ=0 EndX=-16.2837 EndY=28.75 EndZ=0
    g39: LineSegment StartX=-49.19 StartY=25.75 StartZ=0 EndX=-16.28 EndY=25.75 EndZ=0
    g40: LineSegment StartX=-49.19 StartY=23 StartZ=0 EndX=-11.49 EndY=23 EndZ=0
    g41: LineSegment StartX=-49.19 StartY=20 StartZ=0 EndX=-11.49 EndY=20 EndZ=0
    g42: LineSegment StartX=-49.19 StartY=17.25 StartZ=0 EndX=-1.5 EndY=17.25 EndZ=0
    g43: LineSegment StartX=-49.19 StartY=14.25 StartZ=0 EndX=-1.5 EndY=14.25 EndZ=0
    g44: LineSegment StartX=-49.19 StartY=11.5 StartZ=0 EndX=-1.5 EndY=11.5 EndZ=0
    g45: LineSegment StartX=-49.19 StartY=8.5 StartZ=0 EndX=-1.5 EndY=8.5 EndZ=0
    g46: LineSegment StartX=-49.19 StartY=5.75 StartZ=0 EndX=-1.5 EndY=5.75 EndZ=0
    g47: LineSegment StartX=-49.19 StartY=2.75 StartZ=0 EndX=-1.5 EndY=2.75 EndZ=0
  constraints (120):
    c: Vertical(g0)
    c: Distance(g0) = 3
    c: Block(g0)
    c: Vertical(g1)
    c: Distance(g1) = 3
    c: Vertical(g2)
    c: Equal(g0,g2) = 3
    c: Block(g2)
    c: Vertical(g3)
    c: Equal(g1,g3) = 3
    c: Vertical(g4)
    c: Equal(g0,g4) = 3
    c: Block(g4)
    c: Vertical(g5)
    c: Equal(g1,g5) = 3
    c: Vertical(g6)
    c: Equal(g0,g6) = 3
    c: Block(g6)
    c: Vertical(g7)
    c: Equal(g1,g7) = 3
    c: Vertical(g8)
    c: Equal(g0,g8) = 3
    c: Block(g8)
    c: Vertical(g9)
    c: Equal(g1,g9) = 3
    c: Vertical(g10)
    c: Equal(g0,g10) = 3
    c: Block(g10)
    c: Vertical(g11)
    c: Equal(g1,g11) = 3
    c: Block(g12)
    c: Block(g13)
    c: Block(g14)
    c: Block(g15)
    c: Block(g16)
    c: Block(g17)
    c: Block(g18)
    c: Block(g19)
    c: Block(g20)
    c: Block(g21)
    c: Block(g22)
    c: Block(g23)
    c: Block(g11)
    c: Block(g9)
    c: Block(g7)
    c: Block(g5)
    c: Block(g3)
    c: Block(g1)
    c: Coincident(g24,g0)
    c: Coincident(g24,g12)
    c: Horizontal(g24)
    c: Coincident(g25,g0)
    c: Coincident(g25,g12)
    c: Horizontal(g25)
    c: Coincident(g26,g1)
    c: Coincident(g26,g13)
    c: Horizontal(g26)
    c: Coincident(g27,g1)
    c: Coincident(g27,g13)
    c: Horizontal(g27)
    c: Coincident(g28,g2)
    c: Coincident(g28,g14)
    c: Horizontal(g28)
    c: Coincident(g29,g2)
    c: Coincident(g29,g14)
    c: Horizontal(g29)
    c: Coincident(g30,g3)
    c: Coincident(g30,g15)
    c: Horizontal(g30)
    c: Coincident(g31,g3)
    c: Coincident(g31,g15)
    c: Horizontal(g31)
    c: Coincident(g32,g4)
    c: Coincident(g32,g16)
    c: Horizontal(g32)
    c: Coincident(g33,g4)
    c: Coincident(g33,g16)
    c: Horizontal(g33)
    c: Coincident(g34,g5)
    c: Coincident(g34,g17)
    c: Horizontal(g34)
    c: Coincident(g35,g5)
    c: Coincident(g35,g17)
    c: Horizontal(g35)
    c: Coincident(g36,g6)
    c: Coincident(g36,g19)
    c: Horizontal(g36)
    c: Coincident(g37,g6)
    c: Coincident(g37,g19)
    c: Horizontal(g37)
    c: Coincident(g38,g7)
    c: Coincident(g38,g18)
    c: Horizontal(g38)
    c: Coincident(g39,g7)
    c: Coincident(g39,g18)
    c: Horizontal(g39)
    c: Coincident(g40,g8)
    c: Coincident(g40,g20)
    c: Horizontal(g40)
    c: Coincident(g41,g8)
    c: Coincident(g41,g20)
    c: Horizontal(g41)
    c: Coincident(g42,g9)
    c: Coincident(g42,g23)
    c: Horizontal(g42)
    c: Coincident(g43,g9)
    c: Coincident(g43,g23)
    c: Horizontal(g43)
    c: Coincident(g44,g10)
    c: Coincident(g44,g22)
    c: Horizontal(g44)
    c: Coincident(g45,g10)
    c: Coincident(g45,g22)
    c: Horizontal(g45)
    c: Coincident(g46,g11)
    c: Coincident(g46,g21)
    c: Horizontal(g46)
    c: Coincident(g47,g11)
    c: Coincident(g47,g21)
    c: Horizontal(g47)
FEATURE [Part::Extrusion] Extrude042
  Base = -> Sketch051
  Dir = (1,-2e-16,2e-16)
  DirMode = 2
  FaceMakerClass = Part::FaceMakerBullseye
  LengthFwd = 19
  LengthRev = 0
  Placement = pos=(-19,0,0) rot=(0,0,1;0rad)
  Solid = true
  Symmetric = false
FEATURE [Part::Fillet] Fillet035  label="removeToCreateVentalationHoles"
  Base = -> Extrude042
  Edges = <same value as first occurrence — deduplicated (x6 in doc)>
  Placement = pos=(7,0,0) rot=(0,0,1;0rad)
FEATURE [Part::Cut] Cut038  label="top017"
  Base = -> Cut033
  Tool = -> Fillet035
FEATURE [Sketcher::SketchObject] Sketch052  label="bottomSketch001"
  FullyConstrained = true
  sketch-geometry (45):
    g0: LineSegment StartX=6.29999 StartY=8 StartZ=0 EndX=3.29999 EndY=8 EndZ=0
    g1: LineSegment StartX=3.29999 StartY=8 StartZ=0 EndX=3.29999 EndY=-6.03275e-07 EndZ=0
    g2: ArcOfCircle CenterX=8.29999 CenterY=5 CenterZ=0 NormalX=0 NormalY=0 NormalZ=1 AngleXU=0 Radius=2 StartAngle=3.14159 EndAngle=4.71239
    g3: LineSegment StartX=6.29999 StartY=8 StartZ=0 EndX=6.29999 EndY=5 EndZ=0
    g4: ArcOfCircle CenterX=105 CenterY=19 CenterZ=0 NormalX=0 NormalY=0 NormalZ=1 AngleXU=0 Radius=12.7 StartAngle=4.71239 EndAngle=5.94289
    g5-g11: Circle x7 (B-spline internal-alignment scaffolding for g12; pole/knot coordinates omitted)
    g12: BSplineCurve PolesCount=7 KnotsCount=5 Degree=3 IsPeriodic=0
    g13-g17: GeomPoint x5 (B-spline internal-alignment scaffolding for g12; pole/knot coordinates omitted)
    g18: ArcOfCircle CenterX=105 CenterY=19 CenterZ=0 NormalX=0 NormalY=0 NormalZ=1 AngleXU=0 Radius=15.7 StartAngle=5.81226 EndAngle=6.28319
    g19: BSplineCurve PolesCount=5 KnotsCount=3 Degree=3 IsPeriodic=0
    g20: LineSegment StartX=8.29999 StartY=3 StartZ=0 EndX=101.7 EndY=3 EndZ=0
    g21: LineSegment StartX=3.29999 StartY=-6.03275e-07 StartZ=0 EndX=105 EndY=-6.03275e-07 EndZ=0
    g22: LineSegment StartX=120.974 StartY=8.71251 StartZ=0 EndX=122.332 EndY=7.83778 EndZ=0
    g23: LineSegment StartX=105 StartY=-6.03274e-07 StartZ=0 EndX=113 EndY=-6.03274e-07 EndZ=0
    g24: ArcOfCircle CenterX=105 CenterY=19 CenterZ=0 NormalX=0 NormalY=0 NormalZ=1 AngleXU=0 Radius=20.6155 StartAngle=5.11091 EndAngle=5.71103
    g25: ArcOfCircle CenterX=117.7 CenterY=19 CenterZ=0 NormalX=0 NormalY=0 NormalZ=1 AngleXU=0 Radius=3 StartAngle=1.2e-15 EndAngle=2.10468
    g26: Circle CenterX=116.345 CenterY=16.3232 CenterZ=0 NormalX=0 NormalY=0 NormalZ=1 AngleXU=0 Radius=1
    g27: Circle CenterX=117.24 CenterY=15.7584 CenterZ=0 NormalX=0 NormalY=0 NormalZ=1 AngleXU=0 Radius=1
    g28: Circle CenterX=116.972 CenterY=14.7612 CenterZ=0 NormalX=0 NormalY=0 NormalZ=1 AngleXU=0 Radius=1
    g29: BSplineCurve PolesCount=3 KnotsCount=2 Degree=2 IsPeriodic=0
    g30: GeomPoint X=116.345 Y=16.3232 Z=0
    g31: GeomPoint X=116.972 Y=14.7612 Z=0
    g32: Circle CenterX=115.828 CenterY=17.157 CenterZ=0 NormalX=0 NormalY=0 NormalZ=1 AngleXU=0 Radius=1
    g33: Circle CenterX=115.841 CenterY=16.639 CenterZ=0 NormalX=0 NormalY=0 NormalZ=1 AngleXU=0 Radius=1
    g34: Circle CenterX=116.345 CenterY=16.3232 CenterZ=0 NormalX=0 NormalY=0 NormalZ=1 AngleXU=0 Radius=1
    g35: BSplineCurve PolesCount=3 KnotsCount=2 Degree=2 IsPeriodic=0
    g36: GeomPoint X=115.828 Y=17.157 Z=0
    g37: GeomPoint X=116.345 Y=16.3232 Z=0
    g38: LineSegment StartX=115.828 StartY=17.157 StartZ=0 EndX=115.828 EndY=20.8307 EndZ=0
    g39: Circle CenterX=115.828 CenterY=20.8307 CenterZ=0 NormalX=0 NormalY=0 NormalZ=1 AngleXU=0 Radius=1
    g40: Circle CenterX=115.831 CenterY=21.3396 CenterZ=0 NormalX=0 NormalY=0 NormalZ=1 AngleXU=0 Radius=1
    g41: Circle CenterX=116.173 CenterY=21.5825 CenterZ=0 NormalX=0 NormalY=0 NormalZ=1 AngleXU=0 Radius=1
    g42: BSplineCurve PolesCount=3 KnotsCount=2 Degree=2 IsPeriodic=0
    g43: GeomPoint X=115.828 Y=20.8307 Z=0
    g44: GeomPoint X=116.173 Y=21.5825 Z=0
  constraints (70):
    c: Horizontal(g0)
    c: Distance(g0) = 3
    c: Coincident(g1,g0)
    c: Vertical(g1)
    c: Block(g2)
    c: Block(g0)
    c: Coincident(g3,g0)
    c: Coincident(g3,g2)
    c: Vertical(g3)
    c: Block(g1)
    c: Block(g4)
    c: Coincident(g19,g4)
    c: Block(g19)
    c: Equal(g5, g6-g11) x6
    c: InternalAlignment(g5-g11 -> g12) x7
    c: InternalAlignment(g13-g17 -> g12) x5
    c: Block(g12)
    c: Coincident(g18,g12)
    c: Block(g18)
    c: Coincident(g20,g2)
    c: Coincident(g20,g19)
    c: Horizontal(g20)
    c: Distance(g20) = 93.4
    c: Coincident(g21,g1)
    c: Horizontal(g21)
    c: Distance(g21) = 101.7
    c: Horizontal(g23)
    c: Distance(g23) = 8
    c: Coincident(g24,g23)
    c: Block(g23)
    c: Coincident(g22,g24)
    c: Block(g24)
    c: Block(g22)
    c: Distance(g22) = 1.61553
    c: Coincident(g25,g18)
    c: Block(g25)
    c: Weight(g26) = 1
    c: Equal(g26,g27)
    c: Equal(g26,g28)
    c: Coincident(g29,g4)
    c: InternalAlignment(g26,g29)
    c: InternalAlignment(g27,g29)
    c: InternalAlignment(g28,g29)
    c: InternalAlignment(g30,g29)
    c: InternalAlignment(g31,g29)
    c: Block(g29)
    c: Weight(g32) = 1
    c: Equal(g32,g33)
    c: Equal(g32,g34)
    c: Coincident(g35,g29)
    c: InternalAlignment(g32,g35)
    c: InternalAlignment(g33,g35)
    c: InternalAlignment(g34,g35)
    c: InternalAlignment(g36,g35)
    c: InternalAlignment(g37,g35)
    c: Block(g35)
    c: Coincident(g38,g35)
    c: Vertical(g38)
    c: Block(g38)
    c: Coincident(g42,g38)
    c: Weight(g39) = 1
    c: Equal(g39,g40)
    c: Equal(g39,g41)
    c: Coincident(g42,g25)
    c: InternalAlignment(g39,g42)
    c: InternalAlignment(g40,g42)
    c: InternalAlignment(g41,g42)
    c: InternalAlignment(g43,g42)
    c: InternalAlignment(g44,g42)
    c: Block(g42)
FEATURE [Part::Extrusion] Extrude043  label="bottom010"
  Base = -> Sketch052
  Dir = (0,0,1)
  DirMode = 2
  FaceMakerClass = Part::FaceMakerBullseye
  LengthFwd = 71.4
  LengthRev = 0
  Placement = pos=(0,0,0.3) rot=(0,0,1;0rad)
  Solid = true
  Symmetric = false
FEATURE [Sketcher::SketchObject] Sketch053  label="topSketch013"
  FullyConstrained = true
  sketch-geometry (22):
    g0: LineSegment StartX=5.21097e-06 StartY=3 StartZ=0 EndX=5.21097e-06 EndY=19 EndZ=0
    g1: ArcOfCircle CenterX=19 CenterY=19 CenterZ=0 NormalX=0 NormalY=0 NormalZ=1 AngleXU=0 Radius=19 StartAngle=1.5708 EndAngle=3.14159
    g2: ArcOfCircle CenterX=19 CenterY=19 CenterZ=0 NormalX=0 NormalY=0 NormalZ=1 AngleXU=0 Radius=16 StartAngle=1.5708 EndAngle=3.14159
    g3: LineSegment StartX=114 StartY=35 StartZ=0 EndX=19 EndY=35 EndZ=0
    g4: LineSegment StartX=5.21097e-06 StartY=3 StartZ=0 EndX=5.21097e-06 EndY=0 EndZ=0
    g5: LineSegment StartX=3 StartY=0 StartZ=0 EndX=5.21097e-06 EndY=0 EndZ=0
    g6: LineSegment StartX=3 StartY=19 StartZ=0 EndX=3 EndY=0 EndZ=0
    g7: LineSegment StartX=19 StartY=38 StartZ=0 EndX=124 EndY=38 EndZ=0
    g8: Circle CenterX=119 CenterY=35 CenterZ=0 NormalX=0 NormalY=0 NormalZ=1 AngleXU=0 Radius=1
    g9: Circle CenterX=121 CenterY=35 CenterZ=0 NormalX=0 NormalY=0 NormalZ=1 AngleXU=0 Radius=1
    g10: Circle CenterX=121 CenterY=33 CenterZ=0 NormalX=0 NormalY=0 NormalZ=1 AngleXU=0 Radius=1
    g11: BSplineCurve PolesCount=3 KnotsCount=2 Degree=2 IsPeriodic=0
    g12: GeomPoint X=119 Y=35 Z=0
    g13: GeomPoint X=121 Y=33 Z=0
    g14: LineSegment StartX=119 StartY=35 StartZ=0 EndX=114 EndY=35 EndZ=0
    g15: ArcOfCircle CenterX=105 CenterY=19 CenterZ=0 NormalX=0 NormalY=0 NormalZ=1 AngleXU=0 Radius=16 StartAngle=5.60905 EndAngle=6.28319
    g16: LineSegment StartX=121 StartY=33 StartZ=0 EndX=121 EndY=19 EndZ=0
    g17: LineSegment StartX=117.5 StartY=9.01251 StartZ=0 EndX=121.163 EndY=9.0125 EndZ=0
    g18: ArcOfCircle CenterX=105 CenterY=19 CenterZ=0 NormalX=0 NormalY=0 NormalZ=1 AngleXU=0 Radius=20.6155 StartAngle=5.7297 EndAngle=6.28319
    g19: LineSegment StartX=121.163 StartY=9.0125 StartZ=0 EndX=122.538 EndY=8.16329 EndZ=0
    g20: LineSegment StartX=124 StartY=38 StartZ=0 EndX=125.616 EndY=38 EndZ=0
    g21: LineSegment StartX=125.616 StartY=19 StartZ=0 EndX=125.616 EndY=38 EndZ=0
  constraints (50):
    c: Vertical(g0)
    c: Block(g0)
    c: Coincident(g1,g0)
    c: Block(g1)
    c: Coincident(g2,g1)
    c: Block(g2)
    c: Coincident(g3,g2)
    c: Horizontal(g3)
    c: Tangent(g3,g2)
    c: Coincident(g4,g0)
    c: Distance(g4) = 3
    c: Vertical(g4)
    c: Coincident(g5,g4)
    c: Horizontal(g5)
    c: Coincident(g6,g2)
    c: Coincident(g6,g5)
    c: Vertical(g6)
    c: Horizontal(g7)
    c: Distance(g7) = 105
    c: Coincident(g7,g1)
    c: Block(g3)
    c: Weight(g8) = 1
    c: Equal(g8,g9)
    c: Equal(g8,g10)
    c: InternalAlignment(g8,g11)
    c: InternalAlignment(g9,g11)
    c: InternalAlignment(g10,g11)
    c: InternalAlignment(g12,g11)
    c: InternalAlignment(g13,g11)
    c: Block(g11)
    c: Coincident(g14,g11)
    c: Coincident(g14,g3)
    c: Horizontal(g14)
    c: Block(g15)
    c: Coincident(g16,g11)
    c: Coincident(g16,g15)
    c: Vertical(g16)
    c: Distance(g16) = 14
    c: Coincident(g17,g15)
    c: Block(g18)
    c: Coincident(g19,g18)
    c: Coincident(g20,g7)
    c: Horizontal(g20)
    c: Vertical(g21)
    c: Coincident(g20,g21)
    c: Block(g20)
    c: Block(g21)
    c: Block(g19)
    c: Block(g17)
    c: Distance(g20) = 1.61553
FEATURE [Part::Extrusion] Extrude044
  Base = -> Sketch053
  Dir = (0,0,1)
  DirMode = 2
  FaceMakerClass = Part::FaceMakerBullseye
  LengthFwd = 72
  LengthRev = 0
  Solid = true
  Symmetric = false
FEATURE [Part::Fillet] Fillet036  label="top018"
  Base = -> Extrude044
  Edges = 1 edges r=2: [Edge41]
FEATURE [Sketcher::SketchObject] Sketch054
  FullyConstrained = false
  Placement = pos=(0,0,0) rot=(1,0,0;1.5708rad)
  sketch-geometry (24):
    g0: ArcOfCircle CenterX=-4 CenterY=-10.5 CenterZ=0 NormalX=0 NormalY=0 NormalZ=1 AngleXU=0 Radius=1.5 StartAngle=6e-16 EndAngle=3.14159
    g1: ArcOfCircle CenterX=-34.2 CenterY=-10.5 CenterZ=0 NormalX=0 NormalY=0 NormalZ=1 AngleXU=0 Radius=1.5 StartAngle=0 EndAngle=3.14159
    g2: ArcOfCircle CenterX=-34.2 CenterY=-27.7 CenterZ=0 NormalX=0 NormalY=0 NormalZ=1 AngleXU=0 Radius=1.5 StartAngle=3.14159 EndAngle=6.28319
    g3: ArcOfCircle CenterX=-4 CenterY=-27.7 CenterZ=0 NormalX=0 NormalY=0 NormalZ=1 AngleXU=0 Radius=1.5 StartAngle=3.1416 EndAngle=6.28319
    g4: ArcOfCircle CenterX=-10 CenterY=-4.3 CenterZ=0 NormalX=0 NormalY=0 NormalZ=1 AngleXU=0 Radius=1.5 StartAngle=2e-16 EndAngle=3.14159
    g5: ArcOfCircle CenterX=-16.1 CenterY=-1.8 CenterZ=0 NormalX=0 NormalY=0 NormalZ=1 AngleXU=0 Radius=1.5 StartAngle=5e-16 EndAngle=3.14159
    g6: ArcOfCircle CenterX=-22.1 CenterY=-1.8 CenterZ=0 NormalX=0 NormalY=0 NormalZ=1 AngleXU=0 Radius=1.5 StartAngle=5e-16 EndAngle=3.14159
    g7: ArcOfCircle CenterX=-28.2 CenterY=-4.3 CenterZ=0 NormalX=0 NormalY=0 NormalZ=1 AngleXU=0 Radius=1.5 StartAngle=2e-16 EndAngle=3.14159
    g8: ArcOfCircle CenterX=-10 CenterY=-33.9 CenterZ=0 NormalX=0 NormalY=0 NormalZ=1 AngleXU=0 Radius=1.5 StartAngle=3.14159 EndAngle=6.28319
    g9: ArcOfCircle CenterX=-16.1 CenterY=-36.4 CenterZ=0 NormalX=0 NormalY=0 NormalZ=1 AngleXU=0 Radius=1.5 StartAngle=3.14159 EndAngle=6.28319
    g10: ArcOfCircle CenterX=-22.1 CenterY=-36.4 CenterZ=0 NormalX=0 NormalY=0 NormalZ=1 AngleXU=0 Radius=1.5 StartAngle=3.14159 EndAngle=6.28319
    g11: ArcOfCircle CenterX=-28.2 CenterY=-33.9 CenterZ=0 NormalX=0 NormalY=0 NormalZ=1 AngleXU=0 Radius=1.5 StartAngle=3.14159 EndAngle=6.28319
    g12: LineSegment StartX=-35.7 StartY=-10.5 StartZ=0 EndX=-35.7 EndY=-27.7 EndZ=0
    g13: LineSegment StartX=-32.7 StartY=-10.5 StartZ=0 EndX=-32.7 EndY=-27.7 EndZ=0
    g14: LineSegment StartX=-29.7 StartY=-33.9 StartZ=0 EndX=-29.7 EndY=-4.3 EndZ=0
    g15: LineSegment StartX=-26.7 StartY=-33.9 StartZ=0 EndX=-26.7 EndY=-4.3 EndZ=0
    g16: LineSegment StartX=-2.5 StartY=-10.5 StartZ=0 EndX=-2.5 EndY=-27.7 EndZ=0
    g17: LineSegment StartX=-8.5 StartY=-4.3 StartZ=0 EndX=-8.5 EndY=-33.9 EndZ=0
    g18: LineSegment StartX=-5.5 StartY=-10.5 StartZ=0 EndX=-5.5 EndY=-27.7 EndZ=0
    g19: LineSegment StartX=-11.5 StartY=-4.3 StartZ=0 EndX=-11.5 EndY=-33.9 EndZ=0
    g20: LineSegment StartX=-14.6 StartY=-1.8 StartZ=0 EndX=-14.6 EndY=-36.4 EndZ=0
    g21: LineSegment StartX=-17.6 StartY=-1.8 StartZ=0 EndX=-17.6 EndY=-36.4 EndZ=0
    g22: LineSegment StartX=-20.6 StartY=-36.4 StartZ=0 EndX=-20.6 EndY=-1.8 EndZ=0
    g23: LineSegment StartX=-23.6 StartY=-1.8 StartZ=0 EndX=-23.6 EndY=-36.4 EndZ=0
  constraints (48):
    c: Block(g0)
    c: Block(g1)
    c: Block(g2)
    c: Block(g3)
    c: Block(g4)
    c: Block(g5)
    c: Block(g6)
    c: Block(g7)
    c: Block(g8)
    c: Block(g9)
    c: Block(g10)
    c: Block(g11)
    c: Coincident(g12,g1)
    c: Coincident(g12,g2)
    c: Vertical(g12)
    c: Coincident(g13,g1)
    c: Coincident(g13,g2)
    c: Vertical(g13)
    c: Coincident(g14,g11)
    c: Coincident(g14,g7)
    c: Vertical(g14)
    c: Coincident(g15,g11)
    c: Coincident(g15,g7)
    c: Vertical(g15)
    c: Coincident(g16,g0)
    c: Coincident(g16,g3)
    c: Vertical(g16)
    c: Coincident(g17,g4)
    c: Coincident(g17,g8)
    c: Vertical(g17)
    c: Coincident(g18,g0)
    c: Coincident(g18,g3)
    c: Vertical(g18)
    c: Coincident(g19,g4)
    c: Coincident(g19,g8)
    c: Vertical(g19)
    c: Coincident(g20,g5)
    c: Coincident(g20,g9)
    c: Vertical(g20)
    c: Coincident(g21,g5)
    c: Coincident(g21,g9)
    c: Vertical(g21)
    c: Coincident(g22,g10)
    c: Coincident(g22,g6)
    c: Vertical(g22)
    c: Coincident(g23,g6)
    c: Coincident(g23,g10)
    c: Vertical(g23)
FEATURE [Part::Extrusion] Extrude045  label="removeToCreateFanGrillHoles003"
  Base = -> Sketch054
  Dir = (0,-1,6e-16)
  DirMode = 2
  FaceMakerClass = Part::FaceMakerBullseye
  LengthFwd = 10
  LengthRev = 0
  Placement = pos=(65.4,44,54.82) rot=(0,0,1;0rad)
  Solid = true
  Symmetric = false
FEATURE [Part::Feature] Face105 .. Face108  x4 (patterned run collapsed; names and placements below)
  shape: bbox 3.5 x 17.8 x 2e-07 mm, 1 faces, 0 solids (baked)
FEATURE [Part::Revolution] Revolve113  label="removeToCreateScrewAndThreadedInsertHole041"
  Angle = 360
  Axis = (0,1,0)
  Base = (0,0,0)
  FaceMakerClass = Part::FaceMakerBullseye
  Placement = pos=(62.3,30.3,19.7) rot=(0,0,1;0rad)
  Solid = false
  Source = -> Face105
  Symmetric = false
FEATURE [Part::Revolution] Revolve114  label="removeToCreateScrewAndThreadedInsertHole042"
  Angle = 360
  Axis = (0,1,0)
  Base = (0,0,0)
  FaceMakerClass = Part::FaceMakerBullseye
  Placement = pos=(62.3,30.3,51.7) rot=(0,0,1;0rad)
  Solid = false
  Source = -> Face106
  Symmetric = false
FEATURE [Part::Revolution] Revolve115  label="removeToCreateScrewAndThreadedInsertHole043"
  Angle = 360
  Axis = (0,1,0)
  Base = (0,0,0)
  FaceMakerClass = Part::FaceMakerBullseye
  Placement = pos=(30.3,30.3,19.7) rot=(0,0,1;0rad)
  Solid = false
  Source = -> Face107
  Symmetric = false
FEATURE [Part::Revolution] Revolve116  label="removeToCreateScrewAndThreadedInsertHole044"
  Angle = 360
  Axis = (0,1,0)
  Base = (0,0,0)
  FaceMakerClass = Part::FaceMakerBullseye
  Placement = pos=(30.3,30.3,51.7) rot=(0,0,1;0rad)
  Solid = false
  Source = -> Face108
  Symmetric = false
FEATURE [Part::MultiFuse] Fusion083  label="createThreadedInsertHolesForFan004"
  Shapes = -> [Revolve113,Revolve114,Revolve115,Revolve116]
FEATURE [Part::Box] Box024  label="removeToCreteHoleForPlugHousing026"
  AttacherType = Attacher::AttachEngine3D
  Height = 28.6
  Length = 10
  Placement = pos=(-2,0,21.7) rot=(0,0,1;0rad)
  Width = 19
FEATURE [Part::Cylinder] Cylinder038  label="removeToCreteHoleForPlugHousing027"
  Angle = 360
  AttacherType = Attacher::AttachEngine3D
  Height = 20
  Placement = pos=(-2,19,36) rot=(0,1,0;1.5708rad)
  Radius = 14.3
FEATURE [Part::MultiFuse] Fusion084  label="removeToCreteHoleForPlugHousing028"
  Shapes = -> [Box024,Cylinder038]
FEATURE [Part::Cylinder] Cylinder039
  Angle = 360
  AttacherType = Attacher::AttachEngine3D
  Height = 20
  Placement = pos=(0,0,36.15) rot=(0,0,1;0rad)
  Radius = 14.3
FEATURE [Part::Cylinder] Cylinder040
  Angle = 360
  AttacherType = Attacher::AttachEngine3D
  Height = 10
  Placement = pos=(0,0,36.15) rot=(0,0,1;0rad)
  Radius = 4
FEATURE [Part::Box] Box025  label="removeToCreteHoleForPlugHousing030"
  AttacherType = Attacher::AttachEngine3D
  Height = 28.6
  Length = 20
  Placement = pos=(106.15,0,21.7) rot=(0,0,1;0rad)
  Width = 19
FEATURE [Part::MultiFuse] Fusion086  label="removeToCreteHoleForPlugHousing031"
  Placement = pos=(70,19,36) rot=(0,1,0;1.5708rad)
  Shapes = -> [Cylinder039,Cylinder040]
FEATURE [Part::MultiFuse] Fusion085  label="removeToCreteHoleForPlugHousing029"
  Shapes = -> [Box025,Fusion086]
FEATURE [Sketcher::SketchObject] Sketch055
  FullyConstrained = true
  Placement = pos=(117,19,0) rot=(0.57735,0.57735,0.57735;2.0944rad)
  sketch-geometry (48):
    g0: LineSegment StartX=-49.19 StartY=69.25 StartZ=0 EndX=-49.19 EndY=66.25 EndZ=0
    g1: LineSegment StartX=-49.19 StartY=63.5 StartZ=0 EndX=-49.19 EndY=60.5 EndZ=0
    g2: LineSegment StartX=-49.19 StartY=57.75 StartZ=0 EndX=-49.19 EndY=54.75 EndZ=0
    g3: LineSegment StartX=-49.19 StartY=52 StartZ=0 EndX=-49.19 EndY=49 EndZ=0
    g4: LineSegment StartX=-49.19 StartY=46.25 StartZ=0 EndX=-49.19 EndY=43.25 EndZ=0
    g5: LineSegment StartX=-49.19 StartY=40.5 StartZ=0 EndX=-49.19 EndY=37.5 EndZ=0
    g6: LineSegment StartX=-49.19 StartY=34.5 StartZ=0 EndX=-49.19 EndY=31.5 EndZ=0
    g7: LineSegment StartX=-49.19 StartY=28.75 StartZ=0 EndX=-49.19 EndY=25.75 EndZ=0
    g8: LineSegment StartX=-49.19 StartY=23 StartZ=0 EndX=-49.19 EndY=20 EndZ=0
    g9: LineSegment StartX=-49.19 StartY=17.25 StartZ=0 EndX=-49.19 EndY=14.25 EndZ=0
    g10: LineSegment StartX=-49.19 StartY=11.5 StartZ=0 EndX=-49.19 EndY=8.5 EndZ=0
    g11: LineSegment StartX=-49.19 StartY=5.75 StartZ=0 EndX=-49.19 EndY=2.75 EndZ=0
    g12: ArcOfCircle CenterX=-1.5 CenterY=67.75 CenterZ=0 NormalX=0 NormalY=0 NormalZ=1 AngleXU=0 Radius=1.5 StartAngle=4.71239 EndAngle=7.85398
    g13: ArcOfCircle CenterX=-1.5 CenterY=62 CenterZ=0 NormalX=0 NormalY=0 NormalZ=1 AngleXU=0 Radius=1.5 StartAngle=4.71239 EndAngle=7.85398
    g14: ArcOfCircle CenterX=-1.5 CenterY=56.25 CenterZ=0 NormalX=0 NormalY=0 NormalZ=1 AngleXU=0 Radius=1.5 StartAngle=4.71239 EndAngle=7.85398
    g15: ArcOfCircle CenterX=-11.49 CenterY=50.5 CenterZ=0 NormalX=0 NormalY=0 NormalZ=1 AngleXU=0 Radius=1.5 StartAngle=4.71239 EndAngle=7.85398
    g16: ArcOfCircle CenterX=-16.28 CenterY=44.75 CenterZ=0 NormalX=0 NormalY=0 NormalZ=1 AngleXU=0 Radius=1.5 StartAngle=4.71239 EndAngle=7.85398
    g17: ArcOfCircle CenterX=-18.2337 CenterY=39 CenterZ=0 NormalX=0 NormalY=0 NormalZ=1 AngleXU=0 Radius=1.5 StartAngle=4.71485 EndAngle=7.85398
    g18: ArcOfCircle CenterX=-16.2837 CenterY=27.25 CenterZ=0 NormalX=0 NormalY=0 NormalZ=1 AngleXU=0 Radius=1.5 StartAngle=4.71485 EndAngle=7.85398
    g19: ArcOfCircle CenterX=-18.2337 CenterY=33 CenterZ=0 NormalX=0 NormalY=0 NormalZ=1 AngleXU=0 Radius=1.5 StartAngle=4.71485 EndAngle=7.85398
    g20: ArcOfCircle CenterX=-11.49 CenterY=21.5 CenterZ=0 NormalX=0 NormalY=0 NormalZ=1 AngleXU=0 Radius=1.5 StartAngle=4.71239 EndAngle=7.85398
    g21: ArcOfCircle CenterX=-1.5 CenterY=4.25 CenterZ=0 NormalX=0 NormalY=0 NormalZ=1 AngleXU=0 Radius=1.5 StartAngle=4.71239 EndAngle=7.85398
    g22: ArcOfCircle CenterX=-1.5 CenterY=10 CenterZ=0 NormalX=0 NormalY=0 NormalZ=1 AngleXU=0 Radius=1.5 StartAngle=4.71239 EndAngle=7.85398
    g23: ArcOfCircle CenterX=-1.5 CenterY=15.75 CenterZ=0 NormalX=0 NormalY=0 NormalZ=1 AngleXU=0 Radius=1.5 StartAngle=4.71239 EndAngle=7.85398
    g24: LineSegment StartX=-49.19 StartY=69.25 StartZ=0 EndX=-1.5 EndY=69.25 EndZ=0
    g25: LineSegment StartX=-49.19 StartY=66.25 StartZ=0 EndX=-1.5 EndY=66.25 EndZ=0
    g26: LineSegment StartX=-49.19 StartY=63.5 StartZ=0 EndX=-1.5 EndY=63.5 EndZ=0
    g27: LineSegment StartX=-49.19 StartY=60.5 StartZ=0 EndX=-1.5 EndY=60.5 EndZ=0
    g28: LineSegment StartX=-49.19 StartY=57.75 StartZ=0 EndX=-1.5 EndY=57.75 EndZ=0
    g29: LineSegment StartX=-49.19 StartY=54.75 StartZ=0 EndX=-1.5 EndY=54.75 EndZ=0
    g30: LineSegment StartX=-49.19 StartY=52 StartZ=0 EndX=-11.49 EndY=52 EndZ=0
    g31: LineSegment StartX=-49.19 StartY=49 StartZ=0 EndX=-11.49 EndY=49 EndZ=0
    g32: LineSegment StartX=-49.19 StartY=46.25 StartZ=0 EndX=-16.28 EndY=46.25 EndZ=0
    g33: LineSegment StartX=-49.19 StartY=43.25 StartZ=0 EndX=-16.28 EndY=43.25 EndZ=0
    g34: LineSegment StartX=-49.19 StartY=40.5 StartZ=0 EndX=-18.2337 EndY=40.5 EndZ=0
    g35: LineSegment StartX=-49.19 StartY=37.5 StartZ=0 EndX=-18.23 EndY=37.5 EndZ=0
    g36: LineSegment StartX=-49.19 StartY=34.5 StartZ=0 EndX=-18.2337 EndY=34.5 EndZ=0
    g37: LineSegment StartX=-49.19 StartY=31.5 StartZ=0 EndX=-18.23 EndY=31.5 EndZ=0
    g38: LineSegment StartX=-49.19 StartY=28.75 StartZ=0 EndX=-16.2837 EndY=28.75 EndZ=0
    g39: LineSegment StartX=-49.19 StartY=25.75 StartZ=0 EndX=-16.28 EndY=25.75 EndZ=0
    g40: LineSegment StartX=-49.19 StartY=23 StartZ=0 EndX=-11.49 EndY=23 EndZ=0
    g41: LineSegment StartX=-49.19 StartY=20 StartZ=0 EndX=-11.49 EndY=20 EndZ=0
    g42: LineSegment StartX=-49.19 StartY=17.25 StartZ=0 EndX=-1.5 EndY=17.25 EndZ=0
    g43: LineSegment StartX=-49.19 StartY=14.25 StartZ=0 EndX=-1.5 EndY=14.25 EndZ=0
    g44: LineSegment StartX=-49.19 StartY=11.5 StartZ=0 EndX=-1.5 EndY=11.5 EndZ=0
    g45: LineSegment StartX=-49.19 StartY=8.5 StartZ=0 EndX=-1.5 EndY=8.5 EndZ=0
    g46: LineSegment StartX=-49.19 StartY=5.75 StartZ=0 EndX=-1.5 EndY=5.75 EndZ=0
    g47: LineSegment StartX=-49.19 StartY=2.75 StartZ=0 EndX=-1.5 EndY=2.75 EndZ=0
  constraints (120):
    c: Vertical(g0)
    c: Distance(g0) = 3
    c: Block(g0)
    c: Vertical(g1)
    c: Distance(g1) = 3
    c: Vertical(g2)
    c: Equal(g0,g2) = 3
    c: Block(g2)
    c: Vertical(g3)
    c: Equal(g1,g3) = 3
    c: Vertical(g4)
    c: Equal(g0,g4) = 3
    c: Block(g4)
    c: Vertical(g5)
    c: Equal(g1,g5) = 3
    c: Vertical(g6)
    c: Equal(g0,g6) = 3
    c: Block(g6)
    c: Vertical(g7)
    c: Equal(g1,g7) = 3
    c: Vertical(g8)
    c: Equal(g0,g8) = 3
    c: Block(g8)
    c: Vertical(g9)
    c: Equal(g1,g9) = 3
    c: Vertical(g10)
    c: Equal(g0,g10) = 3
    c: Block(g10)
    c: Vertical(g11)
    c: Equal(g1,g11) = 3
    c: Block(g12)
    c: Block(g13)
    c: Block(g14)
    c: Block(g15)
    c: Block(g16)
    c: Block(g17)
    c: Block(g18)
    c: Block(g19)
    c: Block(g20)
    c: Block(g21)
    c: Block(g22)
    c: Block(g23)
    c: Block(g11)
    c: Block(g9)
    c: Block(g7)
    c: Block(g5)
    c: Block(g3)
    c: Block(g1)
    c: Coincident(g24,g0)
    c: Coincident(g24,g12)
    c: Horizontal(g24)
    c: Coincident(g25,g0)
    c: Coincident(g25,g12)
    c: Horizontal(g25)
    c: Coincident(g26,g1)
    c: Coincident(g26,g13)
    c: Horizontal(g26)
    c: Coincident(g27,g1)
    c: Coincident(g27,g13)
    c: Horizontal(g27)
    c: Coincident(g28,g2)
    c: Coincident(g28,g14)
    c: Horizontal(g28)
    c: Coincident(g29,g2)
    c: Coincident(g29,g14)
    c: Horizontal(g29)
    c: Coincident(g30,g3)
    c: Coincident(g30,g15)
    c: Horizontal(g30)
    c: Coincident(g31,g3)
    c: Coincident(g31,g15)
    c: Horizontal(g31)
    c: Coincident(g32,g4)
    c: Coincident(g32,g16)
    c: Horizontal(g32)
    c: Coincident(g33,g4)
    c: Coincident(g33,g16)
    c: Horizontal(g33)
    c: Coincident(g34,g5)
    c: Coincident(g34,g17)
    c: Horizontal(g34)
    c: Coincident(g35,g5)
    c: Coincident(g35,g17)
    c: Horizontal(g35)
    c: Coincident(g36,g6)
    c: Coincident(g36,g19)
    c: Horizontal(g36)
    c: Coincident(g37,g6)
    c: Coincident(g37,g19)
    c: Horizontal(g37)
    c: Coincident(g38,g7)
    c: Coincident(g38,g18)
    c: Horizontal(g38)
    c: Coincident(g39,g7)
    c: Coincident(g39,g18)
    c: Horizontal(g39)
    c: Coincident(g40,g8)
    c: Coincident(g40,g20)
    c: Horizontal(g40)
    c: Coincident(g41,g8)
    c: Coincident(g41,g20)
    c: Horizontal(g41)
    c: Coincident(g42,g9)
    c: Coincident(g42,g23)
    c: Horizontal(g42)
    c: Coincident(g43,g9)
    c: Coincident(g43,g23)
    c: Horizontal(g43)
    c: Coincident(g44,g10)
    c: Coincident(g44,g22)
    c: Horizontal(g44)
    c: Coincident(g45,g10)
    c: Coincident(g45,g22)
    c: Horizontal(g45)
    c: Coincident(g46,g11)
    c: Coincident(g46,g21)
    c: Horizontal(g46)
    c: Coincident(g47,g11)
    c: Coincident(g47,g21)
    c: Horizontal(g47)
FEATURE [Part::Extrusion] Extrude046
  Base = -> Sketch055
  Dir = (1,0,0)
  DirMode = 2
  FaceMakerClass = Part::FaceMakerBullseye
  LengthFwd = 23
  LengthRev = 0
  Placement = pos=(-19,0,0) rot=(0,0,1;0rad)
  Solid = true
  Symmetric = false
FEATURE [Part::Fillet] Fillet038  label="removeToCreateVentalationHoles001"
  Base = -> Extrude046
  Edges = <same value as first occurrence — deduplicated (x6 in doc)>
  Placement = pos=(7,0,0) rot=(0,0,1;0rad)
FEATURE [Sketcher::SketchObject] Sketch056  label="topSketch014"
  FullyConstrained = true
  sketch-geometry (22):
    g0: LineSegment StartX=5.21097e-06 StartY=3 StartZ=0 EndX=5.21097e-06 EndY=19 EndZ=0
    g1: ArcOfCircle CenterX=19 CenterY=19 CenterZ=0 NormalX=0 NormalY=0 NormalZ=1 AngleXU=0 Radius=19 StartAngle=1.5708 EndAngle=3.14159
    g2: ArcOfCircle CenterX=19 CenterY=19 CenterZ=0 NormalX=0 NormalY=0 NormalZ=1 AngleXU=0 Radius=16 StartAngle=1.5708 EndAngle=3.14159
    g3: LineSegment StartX=114 StartY=35 StartZ=0 EndX=19 EndY=35 EndZ=0
    g4: LineSegment StartX=5.21097e-06 StartY=3 StartZ=0 EndX=5.21097e-06 EndY=0 EndZ=0
    g5: LineSegment StartX=3 StartY=0 StartZ=0 EndX=5.21097e-06 EndY=0 EndZ=0
    g6: LineSegment StartX=3 StartY=19 StartZ=0 EndX=3 EndY=0 EndZ=0
    g7: LineSegment StartX=19 StartY=38 StartZ=0 EndX=124 EndY=38 EndZ=0
    g8: Circle CenterX=119 CenterY=35 CenterZ=0 NormalX=0 NormalY=0 NormalZ=1 AngleXU=0 Radius=1
    g9: Circle CenterX=121 CenterY=35 CenterZ=0 NormalX=0 NormalY=0 NormalZ=1 AngleXU=0 Radius=1
    g10: Circle CenterX=121 CenterY=33 CenterZ=0 NormalX=0 NormalY=0 NormalZ=1 AngleXU=0 Radius=1
    g11: BSplineCurve PolesCount=3 KnotsCount=2 Degree=2 IsPeriodic=0
    g12: GeomPoint X=119 Y=35 Z=0
    g13: GeomPoint X=121 Y=33 Z=0
    g14: LineSegment StartX=119 StartY=35 StartZ=0 EndX=114 EndY=35 EndZ=0
    g15: ArcOfCircle CenterX=105 CenterY=19 CenterZ=0 NormalX=0 NormalY=0 NormalZ=1 AngleXU=0 Radius=16 StartAngle=5.60905 EndAngle=6.28319
    g16: LineSegment StartX=121 StartY=33 StartZ=0 EndX=121 EndY=19 EndZ=0
    g17: LineSegment StartX=117.5 StartY=9.01251 StartZ=0 EndX=121.163 EndY=9.0125 EndZ=0
    g18: ArcOfCircle CenterX=105 CenterY=19 CenterZ=0 NormalX=0 NormalY=0 NormalZ=1 AngleXU=0 Radius=20.6155 StartAngle=5.7297 EndAngle=6.28319
    g19: LineSegment StartX=121.163 StartY=9.0125 StartZ=0 EndX=122.538 EndY=8.16329 EndZ=0
    g20: LineSegment StartX=124 StartY=38 StartZ=0 EndX=125.616 EndY=38 EndZ=0
    g21: LineSegment StartX=125.616 StartY=19 StartZ=0 EndX=125.616 EndY=38 EndZ=0
  constraints (49):
    c: Vertical(g0)
    c: Block(g0)
    c: Coincident(g1,g0)
    c: Block(g1)
    c: Coincident(g2,g1)
    c: Block(g2)
    c: Coincident(g3,g2)
    c: Horizontal(g3)
    c: Tangent(g3,g2)
    c: Coincident(g4,g0)
    c: Distance(g4) = 3
    c: Vertical(g4)
    c: Coincident(g5,g4)
    c: Horizontal(g5)
    c: Coincident(g6,g2)
    c: Coincident(g6,g5)
    c: Vertical(g6)
    c: Horizontal(g7)
    c: Distance(g7) = 105
    c: Coincident(g7,g1)
    c: Block(g3)
    c: Weight(g8) = 1
    c: Equal(g8,g9)
    c: Equal(g8,g10)
    c: InternalAlignment(g8,g11)
    c: InternalAlignment(g9,g11)
    c: InternalAlignment(g10,g11)
    c: InternalAlignment(g12,g11)
    c: InternalAlignment(g13,g11)
    c: Block(g11)
    c: Coincident(g14,g11)
    c: Coincident(g14,g3)
    c: Horizontal(g14)
    c: Block(g15)
    c: Coincident(g16,g11)
    c: Coincident(g16,g15)
    c: Vertical(g16)
    c: Distance(g16) = 14
    c: Coincident(g17,g15)
    c: Block(g18)
    c: Coincident(g19,g18)
    c: Coincident(g20,g7)
    c: Horizontal(g20)
    c: Vertical(g21)
    c: Coincident(g20,g21)
    c: Block(g20)
    c: Block(g21)
    c: Block(g19)
    c: Block(g17)
FEATURE [Part::Box] Box026  label="removeToCreteHoleForPlugHousing032"
  AttacherType = Attacher::AttachEngine3D
  Height = 28.6
  Length = 10
  Placement = pos=(-2,0,21.7) rot=(0,0,1;0rad)
  Width = 19
FEATURE [Part::Feature] Face109 .. Face112  x4 (patterned run collapsed; names and placements below)
  shape: bbox 3.5 x 17.8 x 2e-07 mm, 1 faces, 0 solids (baked)
FEATURE [Part::Revolution] Revolve117  label="removeToCreateScrewAndThreadedInsertHole045"
  Angle = 360
  Axis = (0,1,0)
  Base = (0,0,0)
  FaceMakerClass = Part::FaceMakerBullseye
  Placement = pos=(62.3,30.3,19.7) rot=(0,0,1;0rad)
  Solid = false
  Source = -> Face109
  Symmetric = false
FEATURE [Part::Revolution] Revolve118  label="removeToCreateScrewAndThreadedInsertHole046"
  Angle = 360
  Axis = (0,1,0)
  Base = (0,0,0)
  FaceMakerClass = Part::FaceMakerBullseye
  Placement = pos=(62.3,30.3,51.7) rot=(0,0,1;0rad)
  Solid = false
  Source = -> Face110
  Symmetric = false
FEATURE [Part::Revolution] Revolve119  label="removeToCreateScrewAndThreadedInsertHole047"
  Angle = 360
  Axis = (0,1,0)
  Base = (0,0,0)
  FaceMakerClass = Part::FaceMakerBullseye
  Placement = pos=(30.3,30.3,19.7) rot=(0,0,1;0rad)
  Solid = false
  Source = -> Face111
  Symmetric = false
FEATURE [Part::Revolution] Revolve120  label="removeToCreateScrewAndThreadedInsertHole048"
  Angle = 360
  Axis = (0,1,0)
  Base = (0,0,0)
  FaceMakerClass = Part::FaceMakerBullseye
  Placement = pos=(30.3,30.3,51.7) rot=(0,0,1;0rad)
  Solid = false
  Source = -> Face112
  Symmetric = false
FEATURE [Part::MultiFuse] Fusion087  label="createThreadedInsertHolesForFan005"
  Shapes = -> [Revolve117,Revolve118,Revolve119,Revolve120]
FEATURE [Part::Extrusion] Extrude047
  Base = -> Sketch056
  Dir = (0,0,1)
  DirMode = 2
  FaceMakerClass = Part::FaceMakerBullseye
  LengthFwd = 72
  LengthRev = 0
  Solid = true
  Symmetric = false
FEATURE [Part::Fillet] Fillet039  label="top019"
  Base = -> Extrude047
  Edges = 1 edges r=2: [Edge35]
FEATURE [Sketcher::SketchObject] Sketch057
  FullyConstrained = false
  Placement = pos=(0,0,0) rot=(1,0,0;1.5708rad)
  sketch-geometry (24):
    g0: ArcOfCircle CenterX=-4 CenterY=-10.5 CenterZ=0 NormalX=0 NormalY=0 NormalZ=1 AngleXU=0 Radius=1.5 StartAngle=6e-16 EndAngle=3.14159
    g1: ArcOfCircle CenterX=-34.2 CenterY=-10.5 CenterZ=0 NormalX=0 NormalY=0 NormalZ=1 AngleXU=0 Radius=1.5 StartAngle=0 EndAngle=3.14159
    g2: ArcOfCircle CenterX=-34.2 CenterY=-27.7 CenterZ=0 NormalX=0 NormalY=0 NormalZ=1 AngleXU=0 Radius=1.5 StartAngle=3.14159 EndAngle=6.28319
    g3: ArcOfCircle CenterX=-4 CenterY=-27.7 CenterZ=0 NormalX=0 NormalY=0 NormalZ=1 AngleXU=0 Radius=1.5 StartAngle=3.1416 EndAngle=6.28319
    g4: ArcOfCircle CenterX=-10 CenterY=-4.3 CenterZ=0 NormalX=0 NormalY=0 NormalZ=1 AngleXU=0 Radius=1.5 StartAngle=2e-16 EndAngle=3.14159
    g5: ArcOfCircle CenterX=-16.1 CenterY=-1.8 CenterZ=0 NormalX=0 NormalY=0 NormalZ=1 AngleXU=0 Radius=1.5 StartAngle=5e-16 EndAngle=3.14159
    g6: ArcOfCircle CenterX=-22.1 CenterY=-1.8 CenterZ=0 NormalX=0 NormalY=0 NormalZ=1 AngleXU=0 Radius=1.5 StartAngle=5e-16 EndAngle=3.14159
    g7: ArcOfCircle CenterX=-28.2 CenterY=-4.3 CenterZ=0 NormalX=0 NormalY=0 NormalZ=1 AngleXU=0 Radius=1.5 StartAngle=2e-16 EndAngle=3.14159
    g8: ArcOfCircle CenterX=-10 CenterY=-33.9 CenterZ=0 NormalX=0 NormalY=0 NormalZ=1 AngleXU=0 Radius=1.5 StartAngle=3.14159 EndAngle=6.28319
    g9: ArcOfCircle CenterX=-16.1 CenterY=-36.4 CenterZ=0 NormalX=0 NormalY=0 NormalZ=1 AngleXU=0 Radius=1.5 StartAngle=3.14159 EndAngle=6.28319
    g10: ArcOfCircle CenterX=-22.1 CenterY=-36.4 CenterZ=0 NormalX=0 NormalY=0 NormalZ=1 AngleXU=0 Radius=1.5 StartAngle=3.14159 EndAngle=6.28319
    g11: ArcOfCircle CenterX=-28.2 CenterY=-33.9 CenterZ=0 NormalX=0 NormalY=0 NormalZ=1 AngleXU=0 Radius=1.5 StartAngle=3.14159 EndAngle=6.28319
    g12: LineSegment StartX=-35.7 StartY=-10.5 StartZ=0 EndX=-35.7 EndY=-27.7 EndZ=0
    g13: LineSegment StartX=-32.7 StartY=-10.5 StartZ=0 EndX=-32.7 EndY=-27.7 EndZ=0
    g14: LineSegment StartX=-29.7 StartY=-33.9 StartZ=0 EndX=-29.7 EndY=-4.3 EndZ=0
    g15: LineSegment StartX=-26.7 StartY=-33.9 StartZ=0 EndX=-26.7 EndY=-4.3 EndZ=0
    g16: LineSegment StartX=-2.5 StartY=-10.5 StartZ=0 EndX=-2.5 EndY=-27.7 EndZ=0
    g17: LineSegment StartX=-8.5 StartY=-4.3 StartZ=0 EndX=-8.5 EndY=-33.9 EndZ=0
    g18: LineSegment StartX=-5.5 StartY=-10.5 StartZ=0 EndX=-5.5 EndY=-27.7 EndZ=0
    g19: LineSegment StartX=-11.5 StartY=-4.3 StartZ=0 EndX=-11.5 EndY=-33.9 EndZ=0
    g20: LineSegment StartX=-14.6 StartY=-1.8 StartZ=0 EndX=-14.6 EndY=-36.4 EndZ=0
    g21: LineSegment StartX=-17.6 StartY=-1.8 StartZ=0 EndX=-17.6 EndY=-36.4 EndZ=0
    g22: LineSegment StartX=-20.6 StartY=-36.4 StartZ=0 EndX=-20.6 EndY=-1.8 EndZ=0
    g23: LineSegment StartX=-23.6 StartY=-1.8 StartZ=0 EndX=-23.6 EndY=-36.4 EndZ=0
  constraints (48):
    c: Block(g0)
    c: Block(g1)
    c: Block(g2)
    c: Block(g3)
    c: Block(g4)
    c: Block(g5)
    c: Block(g6)
    c: Block(g7)
    c: Block(g8)
    c: Block(g9)
    c: Block(g10)
    c: Block(g11)
    c: Coincident(g12,g1)
    c: Coincident(g12,g2)
    c: Vertical(g12)
    c: Coincident(g13,g1)
    c: Coincident(g13,g2)
    c: Vertical(g13)
    c: Coincident(g14,g11)
    c: Coincident(g14,g7)
    c: Vertical(g14)
    c: Coincident(g15,g11)
    c: Coincident(g15,g7)
    c: Vertical(g15)
    c: Coincident(g16,g0)
    c: Coincident(g16,g3)
    c: Vertical(g16)
    c: Coincident(g17,g4)
    c: Coincident(g17,g8)
    c: Vertical(g17)
    c: Coincident(g18,g0)
    c: Coincident(g18,g3)
    c: Vertical(g18)
    c: Coincident(g19,g4)
    c: Coincident(g19,g8)
    c: Vertical(g19)
    c: Coincident(g20,g5)
    c: Coincident(g20,g9)
    c: Vertical(g20)
    c: Coincident(g21,g5)
    c: Coincident(g21,g9)
    c: Vertical(g21)
    c: Coincident(g22,g10)
    c: Coincident(g22,g6)
    c: Vertical(g22)
    c: Coincident(g23,g6)
    c: Coincident(g23,g10)
    c: Vertical(g23)
FEATURE [Part::Extrusion] Extrude048  label="removeToCreateFanGrillHoles004"
  Base = -> Sketch057
  Dir = (0,-1,6e-16)
  DirMode = 2
  FaceMakerClass = Part::FaceMakerBullseye
  LengthFwd = 10
  LengthRev = 0
  Placement = pos=(65.4,44,54.82) rot=(0,0,1;0rad)
  Solid = true
  Symmetric = false
FEATURE [Part::Cut] Cut040  label="top021"
  Base = -> Fillet039
  Tool = -> Extrude048
FEATURE [Part::Cylinder] Cylinder041  label="removeToCreteHoleForPlugHousing034"
  Angle = 360
  AttacherType = Attacher::AttachEngine3D
  Height = 20
  Placement = pos=(-2,19,36) rot=(0,1,0;1.5708rad)
  Radius = 14.3
FEATURE [Part::MultiFuse] Fusion089  label="removeToCreteHoleForPlugHousing035"
  Shapes = -> [Box026,Cylinder041]
FEATURE [Part::Cylinder] Cylinder042
  Angle = 360
  AttacherType = Attacher::AttachEngine3D
  Height = 20
  Placement = pos=(0,0,36.15) rot=(0,0,1;0rad)
  Radius = 14.3
FEATURE [Part::Cylinder] Cylinder043
  Angle = 360
  AttacherType = Attacher::AttachEngine3D
  Height = 10
  Placement = pos=(0,0,36.15) rot=(0,0,1;0rad)
  Radius = 4
FEATURE [Part::Box] Box027  label="removeToCreteHoleForPlugHousing036"
  AttacherType = Attacher::AttachEngine3D
  Height = 28.6
  Length = 20
  Placement = pos=(106.15,0,21.7) rot=(0,0,1;0rad)
  Width = 19
FEATURE [Part::Cut] Cut041  label="top022"
  Base = -> Cut040
  Tool = -> Fusion087
FEATURE [Part::Cut] Cut039  label="top020"
  Base = -> Cut041
  Tool = -> Fusion089
FEATURE [Part::MultiFuse] Fusion090  label="removeToCreteHoleForPlugHousing037"
  Placement = pos=(70,19,36) rot=(0,1,0;1.5708rad)
  Shapes = -> [Cylinder042,Cylinder043]
FEATURE [Part::MultiFuse] Fusion088  label="removeToCreteHoleForPlugHousing033"
  Shapes = -> [Box027,Fusion090]
FEATURE [Part::Cut] Cut042  label="removeToCreteHoleForPlugHousing038"
  Base = -> Cut039
  Tool = -> Fusion088
FEATURE [Part::MultiFuse] Fusion091  label="removeFromTop"
  Shapes = -> [Fillet038,Fusion085,Fusion084,Fusion083,Extrude045]
FEATURE [Part::Cut] Cut043  label="REAL TOP ====="
  Base = -> Fillet036
  Tool = -> Fusion091
FEATURE [Part::MultiFuse] Fusion092  label="caseScrewPillarBracket016"
  Shapes = -> [Extrude030,Extrude031,Extrude032,Extrude033,Extrude034,Extrude035,Extrude036,Extrude037,Box013,Box014]
FEATURE [Sketcher::SketchObject] Sketch058  label="topSketch015"
  FullyConstrained = true
  sketch-geometry (20):
    g0: LineSegment StartX=5.21097e-06 StartY=3 StartZ=0 EndX=5.21097e-06 EndY=19 EndZ=0
    g1: ArcOfCircle CenterX=19 CenterY=19 CenterZ=0 NormalX=0 NormalY=0 NormalZ=1 AngleXU=0 Radius=19 StartAngle=1.5708 EndAngle=3.14159
    g2: ArcOfCircle CenterX=19 CenterY=19 CenterZ=0 NormalX=0 NormalY=0 NormalZ=1 AngleXU=0 Radius=16 StartAngle=1.5708 EndAngle=3.14159
    g3: LineSegment StartX=114 StartY=35 StartZ=0 EndX=19 EndY=35 EndZ=0
    g4: LineSegment StartX=5.21097e-06 StartY=3 StartZ=0 EndX=5.21097e-06 EndY=0 EndZ=0
    g5: LineSegment StartX=3 StartY=0 StartZ=0 EndX=5.21097e-06 EndY=0 EndZ=0
    g6: LineSegment StartX=3 StartY=19 StartZ=0 EndX=3 EndY=0 EndZ=0
    g7: LineSegment StartX=19 StartY=38 StartZ=0 EndX=124 EndY=38 EndZ=0
    g8: Circle CenterX=119 CenterY=35 CenterZ=0 NormalX=0 NormalY=0 NormalZ=1 AngleXU=0 Radius=1
    g9: Circle CenterX=121 CenterY=35 CenterZ=0 NormalX=0 NormalY=0 NormalZ=1 AngleXU=0 Radius=1
    g10: Circle CenterX=121 CenterY=33 CenterZ=0 NormalX=0 NormalY=0 NormalZ=1 AngleXU=0 Radius=1
    g11: BSplineCurve PolesCount=3 KnotsCount=2 Degree=2 IsPeriodic=0
    g12: GeomPoint X=119 Y=35 Z=0
    g13: GeomPoint X=121 Y=33 Z=0
    g14: LineSegment StartX=119 StartY=35 StartZ=0 EndX=114 EndY=35 EndZ=0
    g15: ArcOfCircle CenterX=105 CenterY=19 CenterZ=0 NormalX=0 NormalY=0 NormalZ=1 AngleXU=0 Radius=19 StartAngle=5.7297 EndAngle=6.28319
    g16: ArcOfCircle CenterX=105 CenterY=19 CenterZ=0 NormalX=0 NormalY=0 NormalZ=1 AngleXU=0 Radius=16 StartAngle=5.60905 EndAngle=6.28319
    g17: LineSegment StartX=121 StartY=33 StartZ=0 EndX=121 EndY=19 EndZ=0
    g18: LineSegment StartX=124 StartY=38 StartZ=0 EndX=124 EndY=19 EndZ=0
    g19: LineSegment StartX=117.5 StartY=9.01251 StartZ=0 EndX=121.163 EndY=9.0125 EndZ=0
  constraints (46):
    c: Vertical(g0)
    c: Block(g0)
    c: Coincident(g1,g0)
    c: Block(g1)
    c: Coincident(g2,g1)
    c: Block(g2)
    c: Coincident(g3,g2)
    c: Horizontal(g3)
    c: Tangent(g3,g2)
    c: Coincident(g4,g0)
    c: Distance(g4) = 3
    c: Vertical(g4)
    c: Coincident(g5,g4)
    c: Horizontal(g5)
    c: Coincident(g6,g2)
    c: Coincident(g6,g5)
    c: Vertical(g6)
    c: Horizontal(g7)
    c: Distance(g7) = 105
    c: Coincident(g7,g1)
    c: Block(g3)
    c: Weight(g8) = 1
    c: Equal(g8,g9)
    c: Equal(g8,g10)
    c: InternalAlignment(g8,g11)
    c: InternalAlignment(g9,g11)
    c: InternalAlignment(g10,g11)
    c: InternalAlignment(g12,g11)
    c: InternalAlignment(g13,g11)
    c: Block(g11)
    c: Coincident(g14,g11)
    c: Coincident(g14,g3)
    c: Horizontal(g14)
    c: Block(g15)
    c: Coincident(g16,g15)
    c: Block(g16)
    c: Coincident(g17,g11)
    c: Coincident(g17,g16)
    c: Vertical(g17)
    c: Distance(g17) = 14
    c: Coincident(g18,g7)
    c: Coincident(g18,g15)
    c: Vertical(g18)
    c: Distance(g18) = 19
    c: Coincident(g19,g16)
    c: Coincident(g19,g15)
FEATURE [Part::Extrusion] Extrude049  label="top023"
  Base = -> Sketch058
  Dir = (0,0,1)
  DirMode = 2
  FaceMakerClass = Part::FaceMakerBullseye
  LengthFwd = 72
  LengthRev = 0
  Solid = true
  Symmetric = false
FEATURE [Sketcher::SketchObject] Sketch059
  FullyConstrained = true
  MapMode = 3
  Placement = pos=(0,0,0) rot=(1,0,0;1.5708rad)
  Support = -> [Extrude049]
  sketch-geometry (8):
    g0: Circle CenterX=80.351 CenterY=-67.6202 CenterZ=0 NormalX=0 NormalY=0 NormalZ=1 AngleXU=0 Radius=2
    g1: Circle CenterX=80.351 CenterY=-67.6202 CenterZ=0 NormalX=0 NormalY=0 NormalZ=1 AngleXU=0 Radius=3
    g2: Circle CenterX=80.351 CenterY=-4.92017 CenterZ=0 NormalX=0 NormalY=0 NormalZ=1 AngleXU=0 Radius=2
    g3: Circle CenterX=80.351 CenterY=-4.92017 CenterZ=0 NormalX=0 NormalY=0 NormalZ=1 AngleXU=0 Radius=3
    g4: Circle CenterX=23.851 CenterY=-4.92017 CenterZ=0 NormalX=0 NormalY=0 NormalZ=1 AngleXU=0 Radius=2
    g5: Circle CenterX=23.851 CenterY=-4.92017 CenterZ=0 NormalX=0 NormalY=0 NormalZ=1 AngleXU=0 Radius=3
    g6: Circle CenterX=23.851 CenterY=-67.6202 CenterZ=0 NormalX=0 NormalY=0 NormalZ=1 AngleXU=0 Radius=2
    g7: Circle CenterX=23.851 CenterY=-67.6202 CenterZ=0 NormalX=0 NormalY=0 NormalZ=1 AngleXU=0 Radius=3
  constraints (8):
    c: Block(g3)
    c: Block(g2)
    c: Block(g1)
    c: Block(g0)
    c: Block(g6)
    c: Block(g7)
    c: Block(g4)
    c: Block(g5)
FEATURE [Sketcher::SketchObject] Sketch060
  FullyConstrained = true
  MapMode = 3
  Placement = pos=(0,0,0) rot=(1,0,0;1.5708rad)
  Support = -> [Extrude049]
  sketch-geometry (8):
    g0: Circle CenterX=80.351 CenterY=-67.6202 CenterZ=0 NormalX=0 NormalY=0 NormalZ=1 AngleXU=0 Radius=3
    g1: Circle CenterX=80.351 CenterY=-4.92017 CenterZ=0 NormalX=0 NormalY=0 NormalZ=1 AngleXU=0 Radius=3
    g2: Circle CenterX=23.851 CenterY=-4.92017 CenterZ=0 NormalX=0 NormalY=0 NormalZ=1 AngleXU=0 Radius=3
    g3: Circle CenterX=23.851 CenterY=-67.6202 CenterZ=0 NormalX=0 NormalY=0 NormalZ=1 AngleXU=0 Radius=3
    g4: Circle CenterX=23.851 CenterY=-67.6202 CenterZ=0 NormalX=0 NormalY=0 NormalZ=1 AngleXU=0 Radius=5
    g5: Circle CenterX=80.351 CenterY=-67.6202 CenterZ=0 NormalX=0 NormalY=0 NormalZ=1 AngleXU=0 Radius=5
    g6: Circle CenterX=23.851 CenterY=-4.92017 CenterZ=0 NormalX=0 NormalY=0 NormalZ=1 AngleXU=0 Radius=5
    g7: Circle CenterX=80.351 CenterY=-4.92017 CenterZ=0 NormalX=0 NormalY=0 NormalZ=1 AngleXU=0 Radius=5
  constraints (8):
    c: Block(g1)
    c: Block(g0)
    c: Block(g3)
    c: Block(g2)
    c: Block(g5)
    c: Block(g4)
    c: Block(g6)
    c: Block(g7)
FEATURE [Sketcher::SketchObject] Sketch061
  FullyConstrained = true
  MapMode = 3
  Placement = pos=(0,0,0) rot=(1,0,0;1.5708rad)
  sketch-geometry (8):
    g0: Circle CenterX=80.351 CenterY=-67.6202 CenterZ=0 NormalX=0 NormalY=0 NormalZ=1 AngleXU=0 Radius=3
    g1: Circle CenterX=80.351 CenterY=-4.92017 CenterZ=0 NormalX=0 NormalY=0 NormalZ=1 AngleXU=0 Radius=3
    g2: Circle CenterX=23.851 CenterY=-4.92017 CenterZ=0 NormalX=0 NormalY=0 NormalZ=1 AngleXU=0 Radius=3
    g3: Circle CenterX=23.851 CenterY=-67.6202 CenterZ=0 NormalX=0 NormalY=0 NormalZ=1 AngleXU=0 Radius=3
    g4: Circle CenterX=23.851 CenterY=-67.6202 CenterZ=0 NormalX=0 NormalY=0 NormalZ=1 AngleXU=0 Radius=5
    g5: Circle CenterX=80.351 CenterY=-67.6202 CenterZ=0 NormalX=0 NormalY=0 NormalZ=1 AngleXU=0 Radius=5
    g6: Circle CenterX=23.851 CenterY=-4.92017 CenterZ=0 NormalX=0 NormalY=0 NormalZ=1 AngleXU=0 Radius=5
    g7: Circle CenterX=80.351 CenterY=-4.92017 CenterZ=0 NormalX=0 NormalY=0 NormalZ=1 AngleXU=0 Radius=5
  constraints (8):
    c: Block(g1)
    c: Block(g0)
    c: Block(g3)
    c: Block(g2)
    c: Block(g5)
    c: Block(g4)
    c: Block(g6)
    c: Block(g7)
FEATURE [Sketcher::SketchObject] Sketch062  label="topSketch016"
  FullyConstrained = true
  sketch-geometry (20):
    g0: LineSegment StartX=5.21097e-06 StartY=3 StartZ=0 EndX=5.21097e-06 EndY=19 EndZ=0
    g1: ArcOfCircle CenterX=19 CenterY=19 CenterZ=0 NormalX=0 NormalY=0 NormalZ=1 AngleXU=0 Radius=19 StartAngle=1.5708 EndAngle=3.14159
    g2: ArcOfCircle CenterX=19 CenterY=19 CenterZ=0 NormalX=0 NormalY=0 NormalZ=1 AngleXU=0 Radius=16 StartAngle=1.5708 EndAngle=3.14159
    g3: LineSegment StartX=114 StartY=35 StartZ=0 EndX=19 EndY=35 EndZ=0
    g4: LineSegment StartX=5.21097e-06 StartY=3 StartZ=0 EndX=5.21097e-06 EndY=0 EndZ=0
    g5: LineSegment StartX=3 StartY=0 StartZ=0 EndX=5.21097e-06 EndY=0 EndZ=0
    g6: LineSegment StartX=3 StartY=19 StartZ=0 EndX=3 EndY=0 EndZ=0
    g7: LineSegment StartX=19 StartY=38 StartZ=0 EndX=124 EndY=38 EndZ=0
    g8: Circle CenterX=119 CenterY=35 CenterZ=0 NormalX=0 NormalY=0 NormalZ=1 AngleXU=0 Radius=1
    g9: Circle CenterX=121 CenterY=35 CenterZ=0 NormalX=0 NormalY=0 NormalZ=1 AngleXU=0 Radius=1
    g10: Circle CenterX=121 CenterY=33 CenterZ=0 NormalX=0 NormalY=0 NormalZ=1 AngleXU=0 Radius=1
    g11: BSplineCurve PolesCount=3 KnotsCount=2 Degree=2 IsPeriodic=0
    g12: GeomPoint X=119 Y=35 Z=0
    g13: GeomPoint X=121 Y=33 Z=0
    g14: LineSegment StartX=119 StartY=35 StartZ=0 EndX=114 EndY=35 EndZ=0
    g15: ArcOfCircle CenterX=105 CenterY=19 CenterZ=0 NormalX=0 NormalY=0 NormalZ=1 AngleXU=0 Radius=19 StartAngle=5.7297 EndAngle=6.28319
    g16: ArcOfCircle CenterX=105 CenterY=19 CenterZ=0 NormalX=0 NormalY=0 NormalZ=1 AngleXU=0 Radius=16 StartAngle=5.60905 EndAngle=6.28319
    g17: LineSegment StartX=121 StartY=33 StartZ=0 EndX=121 EndY=19 EndZ=0
    g18: LineSegment StartX=124 StartY=38 StartZ=0 EndX=124 EndY=19 EndZ=0
    g19: LineSegment StartX=117.5 StartY=9.01251 StartZ=0 EndX=121.163 EndY=9.0125 EndZ=0
  constraints (46):
    c: Vertical(g0)
    c: Block(g0)
    c: Coincident(g1,g0)
    c: Block(g1)
    c: Coincident(g2,g1)
    c: Block(g2)
    c: Coincident(g3,g2)
    c: Horizontal(g3)
    c: Tangent(g3,g2)
    c: Coincident(g4,g0)
    c: Distance(g4) = 3
    c: Vertical(g4)
    c: Coincident(g5,g4)
    c: Horizontal(g5)
    c: Coincident(g6,g2)
    c: Coincident(g6,g5)
    c: Vertical(g6)
    c: Horizontal(g7)
    c: Distance(g7) = 105
    c: Coincident(g7,g1)
    c: Block(g3)
    c: Weight(g8) = 1
    c: Equal(g8,g9)
    c: Equal(g8,g10)
    c: InternalAlignment(g8,g11)
    c: InternalAlignment(g9,g11)
    c: InternalAlignment(g10,g11)
    c: InternalAlignment(g12,g11)
    c: InternalAlignment(g13,g11)
    c: Block(g11)
    c: Coincident(g14,g11)
    c: Coincident(g14,g3)
    c: Horizontal(g14)
    c: Block(g15)
    c: Coincident(g16,g15)
    c: Block(g16)
    c: Coincident(g17,g11)
    c: Coincident(g17,g16)
    c: Vertical(g17)
    c: Distance(g17) = 14
    c: Coincident(g18,g7)
    c: Coincident(g18,g15)
    c: Vertical(g18)
    c: Distance(g18) = 19
    c: Coincident(g19,g16)
    c: Coincident(g19,g15)
FEATURE [Part::Extrusion] Extrude053  label="top024"
  Base = -> Sketch062
  Dir = (0,0,1)
  DirMode = 2
  FaceMakerClass = Part::FaceMakerBullseye
  LengthFwd = 72
  LengthRev = 0
  Solid = true
  Symmetric = false
FEATURE [Sketcher::SketchObject] Sketch063
  FullyConstrained = true
  MapMode = 3
  Placement = pos=(0,0,0) rot=(1,0,0;1.5708rad)
  Support = -> [Extrude053]
  sketch-geometry (8):
    g0: Circle CenterX=80.351 CenterY=-67.6202 CenterZ=0 NormalX=0 NormalY=0 NormalZ=1 AngleXU=0 Radius=2
    g1: Circle CenterX=80.351 CenterY=-67.6202 CenterZ=0 NormalX=0 NormalY=0 NormalZ=1 AngleXU=0 Radius=3
    g2: Circle CenterX=80.351 CenterY=-4.92017 CenterZ=0 NormalX=0 NormalY=0 NormalZ=1 AngleXU=0 Radius=2
    g3: Circle CenterX=80.351 CenterY=-4.92017 CenterZ=0 NormalX=0 NormalY=0 NormalZ=1 AngleXU=0 Radius=3
    g4: Circle CenterX=23.851 CenterY=-4.92017 CenterZ=0 NormalX=0 NormalY=0 NormalZ=1 AngleXU=0 Radius=2
    g5: Circle CenterX=23.851 CenterY=-4.92017 CenterZ=0 NormalX=0 NormalY=0 NormalZ=1 AngleXU=0 Radius=3
    g6: Circle CenterX=23.851 CenterY=-67.6202 CenterZ=0 NormalX=0 NormalY=0 NormalZ=1 AngleXU=0 Radius=2
    g7: Circle CenterX=23.851 CenterY=-67.6202 CenterZ=0 NormalX=0 NormalY=0 NormalZ=1 AngleXU=0 Radius=3
  constraints (8):
    c: Block(g3)
    c: Block(g2)
    c: Block(g1)
    c: Block(g0)
    c: Block(g6)
    c: Block(g7)
    c: Block(g4)
    c: Block(g5)
FEATURE [Part::Extrusion] Extrude054
  Base = -> Sketch063
  Dir = (0,-1,2e-16)
  DirMode = 2
  FaceMakerClass = Part::FaceMakerBullseye
  LengthFwd = 6
  LengthRev = 0
  Placement = pos=(0,9,0) rot=(0,0,1;0rad)
  Solid = true
  Symmetric = false
FEATURE [Sketcher::SketchObject] Sketch064  label="topSketch017"
  FullyConstrained = true
  sketch-geometry (20):
    g0: LineSegment StartX=5.21097e-06 StartY=3 StartZ=0 EndX=5.21097e-06 EndY=19 EndZ=0
    g1: ArcOfCircle CenterX=19 CenterY=19 CenterZ=0 NormalX=0 NormalY=0 NormalZ=1 AngleXU=0 Radius=19 StartAngle=1.5708 EndAngle=3.14159
    g2: ArcOfCircle CenterX=19 CenterY=19 CenterZ=0 NormalX=0 NormalY=0 NormalZ=1 AngleXU=0 Radius=16 StartAngle=1.5708 EndAngle=3.14159
    g3: LineSegment StartX=114 StartY=35 StartZ=0 EndX=19 EndY=35 EndZ=0
    g4: LineSegment StartX=5.21097e-06 StartY=3 StartZ=0 EndX=5.21097e-06 EndY=0 EndZ=0
    g5: LineSegment StartX=3 StartY=0 StartZ=0 EndX=5.21097e-06 EndY=0 EndZ=0
    g6: LineSegment StartX=3 StartY=19 StartZ=0 EndX=3 EndY=0 EndZ=0
    g7: LineSegment StartX=19 StartY=38 StartZ=0 EndX=124 EndY=38 EndZ=0
    g8: Circle CenterX=119 CenterY=35 CenterZ=0 NormalX=0 NormalY=0 NormalZ=1 AngleXU=0 Radius=1
    g9: Circle CenterX=121 CenterY=35 CenterZ=0 NormalX=0 NormalY=0 NormalZ=1 AngleXU=0 Radius=1
    g10: Circle CenterX=121 CenterY=33 CenterZ=0 NormalX=0 NormalY=0 NormalZ=1 AngleXU=0 Radius=1
    g11: BSplineCurve PolesCount=3 KnotsCount=2 Degree=2 IsPeriodic=0
    g12: GeomPoint X=119 Y=35 Z=0
    g13: GeomPoint X=121 Y=33 Z=0
    g14: LineSegment StartX=119 StartY=35 StartZ=0 EndX=114 EndY=35 EndZ=0
    g15: ArcOfCircle CenterX=105 CenterY=19 CenterZ=0 NormalX=0 NormalY=0 NormalZ=1 AngleXU=0 Radius=19 StartAngle=5.7297 EndAngle=6.28319
    g16: ArcOfCircle CenterX=105 CenterY=19 CenterZ=0 NormalX=0 NormalY=0 NormalZ=1 AngleXU=0 Radius=16 StartAngle=5.60905 EndAngle=6.28319
    g17: LineSegment StartX=121 StartY=33 StartZ=0 EndX=121 EndY=19 EndZ=0
    g18: LineSegment StartX=124 StartY=38 StartZ=0 EndX=124 EndY=19 EndZ=0
    g19: LineSegment StartX=117.5 StartY=9.01251 StartZ=0 EndX=121.163 EndY=9.0125 EndZ=0
  constraints (46):
    c: Vertical(g0)
    c: Block(g0)
    c: Coincident(g1,g0)
    c: Block(g1)
    c: Coincident(g2,g1)
    c: Block(g2)
    c: Coincident(g3,g2)
    c: Horizontal(g3)
    c: Tangent(g3,g2)
    c: Coincident(g4,g0)
    c: Distance(g4) = 3
    c: Vertical(g4)
    c: Coincident(g5,g4)
    c: Horizontal(g5)
    c: Coincident(g6,g2)
    c: Coincident(g6,g5)
    c: Vertical(g6)
    c: Horizontal(g7)
    c: Distance(g7) = 105
    c: Coincident(g7,g1)
    c: Block(g3)
    c: Weight(g8) = 1
    c: Equal(g8,g9)
    c: Equal(g8,g10)
    c: InternalAlignment(g8,g11)
    c: InternalAlignment(g9,g11)
    c: InternalAlignment(g10,g11)
    c: InternalAlignment(g12,g11)
    c: InternalAlignment(g13,g11)
    c: Block(g11)
    c: Coincident(g14,g11)
    c: Coincident(g14,g3)
    c: Horizontal(g14)
    c: Block(g15)
    c: Coincident(g16,g15)
    c: Block(g16)
    c: Coincident(g17,g11)
    c: Coincident(g17,g16)
    c: Vertical(g17)
    c: Distance(g17) = 14
    c: Coincident(g18,g7)
    c: Coincident(g18,g15)
    c: Vertical(g18)
    c: Distance(g18) = 19
    c: Coincident(g19,g16)
    c: Coincident(g19,g15)
FEATURE [Sketcher::SketchObject] Sketch065
  FullyConstrained = true
  MapMode = 3
  Placement = pos=(0,0,0) rot=(1,0,0;1.5708rad)
  sketch-geometry (8):
    g0: Circle CenterX=80.351 CenterY=-67.6202 CenterZ=0 NormalX=0 NormalY=0 NormalZ=1 AngleXU=0 Radius=3
    g1: Circle CenterX=80.351 CenterY=-4.92017 CenterZ=0 NormalX=0 NormalY=0 NormalZ=1 AngleXU=0 Radius=3
    g2: Circle CenterX=23.851 CenterY=-4.92017 CenterZ=0 NormalX=0 NormalY=0 NormalZ=1 AngleXU=0 Radius=3
    g3: Circle CenterX=23.851 CenterY=-67.6202 CenterZ=0 NormalX=0 NormalY=0 NormalZ=1 AngleXU=0 Radius=3
    g4: Circle CenterX=23.851 CenterY=-67.6202 CenterZ=0 NormalX=0 NormalY=0 NormalZ=1 AngleXU=0 Radius=5
    g5: Circle CenterX=80.351 CenterY=-67.6202 CenterZ=0 NormalX=0 NormalY=0 NormalZ=1 AngleXU=0 Radius=5
    g6: Circle CenterX=23.851 CenterY=-4.92017 CenterZ=0 NormalX=0 NormalY=0 NormalZ=1 AngleXU=0 Radius=5
    g7: Circle CenterX=80.351 CenterY=-4.92017 CenterZ=0 NormalX=0 NormalY=0 NormalZ=1 AngleXU=0 Radius=5
  constraints (8):
    c: Block(g1)
    c: Block(g0)
    c: Block(g3)
    c: Block(g2)
    c: Block(g5)
    c: Block(g4)
    c: Block(g6)
    c: Block(g7)
FEATURE [Part::Extrusion] Extrude056
  Base = -> Sketch065
  Dir = (0,-1,2e-16)
  DirMode = 2
  FaceMakerClass = Part::FaceMakerBullseye
  LengthFwd = 2
  LengthRev = 0
  Solid = true
  Symmetric = false
FEATURE [Part::Extrusion] Extrude057  label="top025"
  Base = -> Sketch064
  Dir = (0,0,1)
  DirMode = 2
  FaceMakerClass = Part::FaceMakerBullseye
  LengthFwd = 72
  LengthRev = 0
  Solid = true
  Symmetric = false
FEATURE [Sketcher::SketchObject] Sketch066
  FullyConstrained = true
  MapMode = 3
  Placement = pos=(0,0,0) rot=(1,0,0;1.5708rad)
  Support = -> [Extrude057]
  sketch-geometry (8):
    g0: Circle CenterX=80.351 CenterY=-67.6202 CenterZ=0 NormalX=0 NormalY=0 NormalZ=1 AngleXU=0 Radius=3
    g1: Circle CenterX=80.351 CenterY=-4.92017 CenterZ=0 NormalX=0 NormalY=0 NormalZ=1 AngleXU=0 Radius=3
    g2: Circle CenterX=23.851 CenterY=-4.92017 CenterZ=0 NormalX=0 NormalY=0 NormalZ=1 AngleXU=0 Radius=3
    g3: Circle CenterX=23.851 CenterY=-67.6202 CenterZ=0 NormalX=0 NormalY=0 NormalZ=1 AngleXU=0 Radius=3
    g4: Circle CenterX=23.851 CenterY=-67.6202 CenterZ=0 NormalX=0 NormalY=0 NormalZ=1 AngleXU=0 Radius=5
    g5: Circle CenterX=80.351 CenterY=-67.6202 CenterZ=0 NormalX=0 NormalY=0 NormalZ=1 AngleXU=0 Radius=5
    g6: Circle CenterX=23.851 CenterY=-4.92017 CenterZ=0 NormalX=0 NormalY=0 NormalZ=1 AngleXU=0 Radius=5
    g7: Circle CenterX=80.351 CenterY=-4.92017 CenterZ=0 NormalX=0 NormalY=0 NormalZ=1 AngleXU=0 Radius=5
  constraints (8):
    c: Block(g1)
    c: Block(g0)
    c: Block(g3)
    c: Block(g2)
    c: Block(g5)
    c: Block(g4)
    c: Block(g6)
    c: Block(g7)
FEATURE [Part::Extrusion] Extrude055
  Base = -> Sketch066
  Dir = (0,-1,2e-16)
  DirMode = 2
  FaceMakerClass = Part::FaceMakerBullseye
  LengthFwd = 2
  LengthRev = 0
  Solid = true
  Symmetric = false
FEATURE [Part::Fillet] Fillet041
  Base = -> Extrude056
  Edges = 4 edges r=1.99: [Edge6,Edge12,Edge18,Edge24]
FEATURE [Part::Cut] Cut045
  Base = -> Extrude055
  Placement = pos=(0,6,0) rot=(0,0,1;0rad)
  Tool = -> Fillet041
FEATURE [Part::MultiFuse] Fusion095  label="pcbScrewPillars"
  Placement = pos=(-3.2,-1,72.3) rot=(0,0,1;0rad)
  Shapes = -> [Cut045,Extrude054]
FEATURE [Part::Feature] Face113
  shape: bbox 3.2 x 1.5 x 2e-07 mm, 1 faces, 0 solids (baked)
FEATURE [Part::Revolution] Revolve121  label="backCaseScrewRetainer002"
  Angle = 360
  Axis = (0,1,0)
  Base = (0,0,0)
  FaceMakerClass = Part::FaceMakerBullseye
  Placement = pos=(12.5,3,62) rot=(0,0,1;0rad)
  Solid = false
  Source = -> Face113
  Symmetric = false
FEATURE [Part::Feature] Face114
  shape: bbox 3.2 x 1.5 x 2e-07 mm, 1 faces, 0 solids (baked)
FEATURE [Part::Feature] Face115
  shape: bbox 3.2 x 1.5 x 2e-07 mm, 1 faces, 0 solids (baked)
FEATURE [Part::Feature] Face116
  shape: bbox 3.2 x 1.5 x 2e-07 mm, 1 faces, 0 solids (baked)
FEATURE [Part::Revolution] Revolve122  label="frontCaseScrewRetainer004"
  Angle = 360
  Axis = (0,1,0)
  Base = (0,0,0)
  FaceMakerClass = Part::FaceMakerBullseye
  Placement = pos=(89.5,3,68.5) rot=(0,0,1;0rad)
  Solid = false
  Source = -> Face115
  Symmetric = false
FEATURE [Part::Revolution] Revolve123  label="frontCaseScrewRetainer005"
  Angle = 360
  Axis = (0,1,0)
  Base = (0,0,0)
  FaceMakerClass = Part::FaceMakerBullseye
  Placement = pos=(89.5,3,3.5) rot=(0,0,1;0rad)
  Solid = false
  Source = -> Face116
  Symmetric = false
FEATURE [Part::Revolution] Revolve124  label="backCaseScrewRetainer003"
  Angle = 360
  Axis = (0,1,0)
  Base = (0,0,0)
  FaceMakerClass = Part::FaceMakerBullseye
  Placement = pos=(12.5,3,10) rot=(0,0,1;0rad)
  Solid = false
  Source = -> Face114
  Symmetric = false
FEATURE [Part::Feature] Face117
  shape: bbox 3.6 x 3.2 x 2e-07 mm, 1 faces, 0 solids (baked)
FEATURE [Part::Revolution] Revolve125  label="moreFrontCaseScrewRetainer004"
  Angle = 360
  Axis = (0,1,0)
  Base = (0,0,0)
  FaceMakerClass = Part::FaceMakerBullseye
  Placement = pos=(109.5,4.5,68.5) rot=(0,0,1;0rad)
  Solid = false
  Source = -> Face117
  Symmetric = false
FEATURE [Part::Feature] Face118
  shape: bbox 3.6 x 3.2 x 2e-07 mm, 1 faces, 0 solids (baked)
FEATURE [Part::Revolution] Revolve126  label="moreFrontCaseScrewRetainer005"
  Angle = 360
  Axis = (0,1,0)
  Base = (0,0,0)
  FaceMakerClass = Part::FaceMakerBullseye
  Placement = pos=(109.5,4.5,3.5) rot=(0,0,1;0rad)
  Solid = false
  Source = -> Face118
  Symmetric = false
FEATURE [Part::MultiFuse] Fusion096  label="screwRetainers001"
  Shapes = -> [Revolve126,Revolve125,Revolve124,Revolve123,Revolve122,Revolve121]
FEATURE [Part::Feature] Face119
  shape: bbox 10 x 16.5 x 2e-07 mm, 1 faces, 0 solids (baked)
FEATURE [Part::Revolution] Revolve130  label="plugHousing050"
  Angle = 360
  Axis = (0,1,0)
  Base = (0,0,0)
  FaceMakerClass = Part::FaceMakerBullseye
  Placement = pos=(0,0,36.15) rot=(0,0,1;0rad)
  Solid = false
  Source = -> Face119
  Symmetric = false
FEATURE [Part::Feature] Face120
  shape: bbox 10 x 16.5 x 2e-07 mm, 1 faces, 0 solids (baked)
FEATURE [Part::Feature] Face121
  shape: bbox 10 x 16.5 x 2e-07 mm, 1 faces, 0 solids (baked)
FEATURE [Part::Revolution] Revolve127  label="plugHousing047"
  Angle = 360
  Axis = (0,1,0)
  Base = (0,0,0)
  FaceMakerClass = Part::FaceMakerBullseye
  Placement = pos=(0,0,36.15) rot=(0,0,1;0rad)
  Solid = false
  Source = -> Face121
  Symmetric = false
FEATURE [Part::Feature] Face122
  shape: bbox 10 x 16.5 x 2e-07 mm, 1 faces, 0 solids (baked)
FEATURE [Part::Feature] Face123
  shape: bbox 10 x 16.5 x 2e-07 mm, 1 faces, 0 solids (baked)
FEATURE [Part::Revolution] Revolve128  label="plugHousing048"
  Angle = 360
  Axis = (0,1,0)
  Base = (0,0,0)
  FaceMakerClass = Part::FaceMakerBullseye
  Placement = pos=(0,0,36.15) rot=(0,0,1;0rad)
  Solid = false
  Source = -> Face123
  Symmetric = false
FEATURE [Part::MultiFuse] Fusion100  label="plugHousing054"
  Placement = pos=(0,0,0) rot=(0,0,1;1.5708rad)
  Shapes = -> [Revolve130,Revolve128]
FEATURE [Part::Feature] Face124
  shape: bbox 10 x 16.5 x 2e-07 mm, 1 faces, 0 solids (baked)
FEATURE [Part::Feature] Face125
  shape: bbox 10 x 16.5 x 2e-07 mm, 1 faces, 0 solids (baked)
FEATURE [Part::Revolution] Revolve129  label="plugHousing049"
  Angle = 360
  Axis = (0,1,0)
  Base = (0,0,0)
  FaceMakerClass = Part::FaceMakerBullseye
  Placement = pos=(0,0,36.15) rot=(0,0,1;0rad)
  Solid = false
  Source = -> Face125
  Symmetric = false
FEATURE [Part::Feature] Face126
  shape: bbox 10 x 16.5 x 2e-07 mm, 1 faces, 0 solids (baked)
FEATURE [Part::Revolution] Revolve131  label="plugHousing058"
  Angle = 360
  Axis = (0,1,0)
  Base = (0,0,0)
  FaceMakerClass = Part::FaceMakerBullseye
  Placement = pos=(0,0,36.15) rot=(0,0,1;0rad)
  Solid = false
  Source = -> Face120
  Symmetric = false
FEATURE [Part::MultiFuse] Fusion099  label="plugHousing053"
  Placement = pos=(0,0,0) rot=(0,0,1;1.5708rad)
  Shapes = -> [Revolve127,Revolve131]
FEATURE [Part::MultiFuse] Fusion102  label="plugHousing056"
  Placement = pos=(0,19,0) rot=(0,0,1;3.14159rad)
  Shapes = -> [Fusion100,Fusion099]
FEATURE [Part::Revolution] Revolve132  label="plugHousing059"
  Angle = 360
  Axis = (0,1,0)
  Base = (0,0,0)
  FaceMakerClass = Part::FaceMakerBullseye
  Placement = pos=(0,0,36.15) rot=(0,0,1;0rad)
  Solid = false
  Source = -> Face126
  Symmetric = false
FEATURE [Part::Revolution] Revolve133  label="plugHousing060"
  Angle = 360
  Axis = (0,1,0)
  Base = (0,0,0)
  FaceMakerClass = Part::FaceMakerBullseye
  Placement = pos=(0,0,36.15) rot=(0,0,1;0rad)
  Solid = false
  Source = -> Face122
  Symmetric = false
FEATURE [Part::MultiFuse] Fusion097  label="plugHousing051"
  Placement = pos=(0,0,0) rot=(0,0,1;1.5708rad)
  Shapes = -> [Revolve133,Revolve132]
FEATURE [Part::Revolution] Revolve134  label="plugHousing061"
  Angle = 360
  Axis = (0,1,0)
  Base = (0,0,0)
  FaceMakerClass = Part::FaceMakerBullseye
  Placement = pos=(0,0,36.15) rot=(0,0,1;0rad)
  Solid = false
  Source = -> Face124
  Symmetric = false
FEATURE [Part::MultiFuse] Fusion101  label="plugHousing055"
  Placement = pos=(0,0,0) rot=(0,0,1;1.5708rad)
  Shapes = -> [Revolve129,Revolve134]
FEATURE [Part::MultiFuse] Fusion098  label="plugHousing052"
  Placement = pos=(0,19,0) rot=(0,0,1;3.14159rad)
  Shapes = -> [Fusion097,Fusion101]
FEATURE [Part::MultiFuse] Fusion103  label="plugHousing057"
  Placement = pos=(122.621,0,-0.15) rot=(0,0,1;0rad)
  Shapes = -> [Fusion102,Fusion098]
FEATURE [Part::Box] Box028  label="Cube015"
  AttacherType = Attacher::AttachEngine3D
  Height = 28
  Length = 3
  Placement = pos=(110.7,19,22) rot=(0,0,1;0rad)
  Width = 15.7
FEATURE [Part::Cylinder] Cylinder044
  Angle = 360
  AttacherType = Attacher::AttachEngine3D
  Height = 20
  Placement = pos=(0,0,36.15) rot=(0,0,1;0rad)
  Radius = 10.3
FEATURE [Part::Cylinder] Cylinder045
  Angle = 360
  AttacherType = Attacher::AttachEngine3D
  Height = 10
  Placement = pos=(0,0,36.15) rot=(0,0,1;0rad)
  Radius = 4
FEATURE [Part::MultiFuse] Fusion104  label="removeToCreteHoleForPlugHousing040"
  Placement = pos=(70,19,36) rot=(0,1,0;1.5708rad)
  Shapes = -> [Cylinder044,Cylinder045]
FEATURE [Part::Cut] Cut046  label="plugHousingTab003"
  Base = -> Box028
  Tool = -> Fusion104
FEATURE [Part::MultiFuse] Fusion105  label="plugHousing062"
  Shapes = -> [Fusion103,Cut046]
FEATURE [Part::Fillet] Fillet042
  Base = -> Fusion105
  Edges = 1 edges r=2: [Edge25]
FEATURE [Part::Fillet] Fillet043  label="plugHousing063"
  Base = -> Fillet042
  Edges = 1 edges r=2: [Edge8]
  Placement = pos=(7,0,0) rot=(0,0,1;0rad)
FEATURE [Part::Feature] Face127
  shape: bbox 10 x 16.5 x 2e-07 mm, 1 faces, 0 solids (baked)
FEATURE [Part::Feature] Face128
  shape: bbox 10 x 16.5 x 2e-07 mm, 1 faces, 0 solids (baked)
FEATURE [Part::Revolution] Revolve137  label="plugHousing070"
  Angle = 360
  Axis = (0,1,0)
  Base = (0,0,0)
  FaceMakerClass = Part::FaceMakerBullseye
  Placement = pos=(0,0,36.15) rot=(0,0,1;0rad)
  Solid = false
  Source = -> Face127
  Symmetric = false
FEATURE [Part::Revolution] Revolve140  label="plugHousing073"
  Angle = 360
  Axis = (0,1,0)
  Base = (0,0,0)
  FaceMakerClass = Part::FaceMakerBullseye
  Placement = pos=(0,0,36.15) rot=(0,0,1;0rad)
  Solid = false
  Source = -> Face128
  Symmetric = false
FEATURE [Part::Feature] Face129
  shape: bbox 10 x 16.5 x 2e-07 mm, 1 faces, 0 solids (baked)
FEATURE [Part::Revolution] Revolve138  label="plugHousing071"
  Angle = 360
  Axis = (0,1,0)
  Base = (0,0,0)
  FaceMakerClass = Part::FaceMakerBullseye
  Placement = pos=(0,0,36.15) rot=(0,0,1;0rad)
  Solid = false
  Source = -> Face129
  Symmetric = false
FEATURE [Part::Feature] Face130
  shape: bbox 10 x 16.5 x 2e-07 mm, 1 faces, 0 solids (baked)
FEATURE [Part::Revolution] Revolve139  label="plugHousing072"
  Angle = 360
  Axis = (0,1,0)
  Base = (0,0,0)
  FaceMakerClass = Part::FaceMakerBullseye
  Placement = pos=(0,0,36.15) rot=(0,0,1;0rad)
  Solid = false
  Source = -> Face130
  Symmetric = false
FEATURE [Part::Feature] Face131
  shape: bbox 10 x 16.5 x 2e-07 mm, 1 faces, 0 solids (baked)
FEATURE [Part::Revolution] Revolve135  label="plugHousing068"
  Angle = 360
  Axis = (0,1,0)
  Base = (0,0,0)
  FaceMakerClass = Part::FaceMakerBullseye
  Placement = pos=(0,0,36.15) rot=(0,0,1;0rad)
  Solid = false
  Source = -> Face131
  Symmetric = false
FEATURE [Part::MultiFuse] Fusion112  label="plugHousing078"
  Placement = pos=(0,0,0) rot=(0,0,1;1.5708rad)
  Shapes = -> [Revolve135,Revolve139]
FEATURE [Part::Feature] Face132
  shape: bbox 10 x 16.5 x 2e-07 mm, 1 faces, 0 solids (baked)
FEATURE [Part::Revolution] Revolve141  label="plugHousing074"
  Angle = 360
  Axis = (0,1,0)
  Base = (0,0,0)
  FaceMakerClass = Part::FaceMakerBullseye
  Placement = pos=(0,0,36.15) rot=(0,0,1;0rad)
  Solid = false
  Source = -> Face132
  Symmetric = false
FEATURE [Part::MultiFuse] Fusion110  label="plugHousing076"
  Placement = pos=(0,0,0) rot=(0,0,1;1.5708rad)
  Shapes = -> [Revolve141,Revolve140]
FEATURE [Part::Feature] Face133
  shape: bbox 10 x 16.5 x 2e-07 mm, 1 faces, 0 solids (baked)
FEATURE [Part::Revolution] Revolve136  label="plugHousing069"
  Angle = 360
  Axis = (0,1,0)
  Base = (0,0,0)
  FaceMakerClass = Part::FaceMakerBullseye
  Placement = pos=(0,0,36.15) rot=(0,0,1;0rad)
  Solid = false
  Source = -> Face133
  Symmetric = false
FEATURE [Part::MultiFuse] Fusion106  label="plugHousing064"
  Placement = pos=(0,0,0) rot=(0,0,1;1.5708rad)
  Shapes = -> [Revolve138,Revolve136]
FEATURE [Part::MultiFuse] Fusion108  label="plugHousing066"
  Placement = pos=(0,19,0) rot=(0,0,1;3.14159rad)
  Shapes = -> [Fusion106,Fusion112]
FEATURE [Part::Feature] Face134
  shape: bbox 10 x 16.5 x 2e-07 mm, 1 faces, 0 solids (baked)
FEATURE [Part::Revolution] Revolve142  label="plugHousing075"
  Angle = 360
  Axis = (0,1,0)
  Base = (0,0,0)
  FaceMakerClass = Part::FaceMakerBullseye
  Placement = pos=(0,0,36.15) rot=(0,0,1;0rad)
  Solid = false
  Source = -> Face134
  Symmetric = false
FEATURE [Part::MultiFuse] Fusion107  label="plugHousing065"
  Placement = pos=(0,0,0) rot=(0,0,1;1.5708rad)
  Shapes = -> [Revolve137,Revolve142]
FEATURE [Part::MultiFuse] Fusion111  label="plugHousing077"
  Placement = pos=(0,19,0) rot=(0,0,1;3.14159rad)
  Shapes = -> [Fusion110,Fusion107]
FEATURE [Part::MultiFuse] Fusion109  label="plugHousing067"
  Placement = pos=(131.236,0,-0.15) rot=(0,0,1;0rad)
  Shapes = -> [Fusion108,Fusion111]
FEATURE [Part::MultiFuse] Fusion113  label="plugHousing079"
  Shapes = -> [Fillet043,Fusion109]
FEATURE [Part::Feature] Face135
  shape: bbox 3.5 x 17.8 x 2e-07 mm, 1 faces, 0 solids (baked)
FEATURE [Part::Revolution] Revolve143  label="removeToCreateScrewAndThreadedInsertHole049"
  Angle = 360
  Axis = (0,1,0)
  Base = (0,0,0)
  FaceMakerClass = Part::FaceMakerBullseye
  Placement = pos=(12.5,0,10) rot=(0,0,1;0rad)
  Solid = false
  Source = -> Face135
  Symmetric = false
FEATURE [Part::Feature] Face136
  shape: bbox 3.5 x 17.8 x 2e-07 mm, 1 faces, 0 solids (baked)
FEATURE [Part::Revolution] Revolve144  label="removeToCreateScrewAndThreadedInsertHole050"
  Angle = 360
  Axis = (0,1,0)
  Base = (0,0,0)
  FaceMakerClass = Part::FaceMakerBullseye
  Placement = pos=(12.5,0,62) rot=(0,0,1;0rad)
  Solid = false
  Source = -> Face136
  Symmetric = false
FEATURE [Part::Feature] Face137
  shape: bbox 3.5 x 17.8 x 2e-07 mm, 1 faces, 0 solids (baked)
FEATURE [Part::Revolution] Revolve145  label="removeToCreateScrewAndThreadedInsertHole051"
  Angle = 360
  Axis = (0,1,0)
  Base = (0,0,0)
  FaceMakerClass = Part::FaceMakerBullseye
  Placement = pos=(89.5,0,68.5) rot=(0,0,1;0rad)
  Solid = false
  Source = -> Face137
  Symmetric = false
FEATURE [Part::Feature] Face138
  shape: bbox 3.5 x 17.8 x 2e-07 mm, 1 faces, 0 solids (baked)
FEATURE [Part::Revolution] Revolve146  label="removeToCreateScrewAndThreadedInsertHole052"
  Angle = 360
  Axis = (0,1,0)
  Base = (0,0,0)
  FaceMakerClass = Part::FaceMakerBullseye
  Placement = pos=(89.5,0,3.5) rot=(0,0,1;0rad)
  Solid = false
  Source = -> Face138
  Symmetric = false
FEATURE [Part::Feature] Face139
  shape: bbox 3.5 x 17.8 x 2e-07 mm, 1 faces, 0 solids (baked)
FEATURE [Part::Revolution] Revolve147  label="removeToCreateScrewAndThreadedInsertHole053"
  Angle = 360
  Axis = (0,1,0)
  Base = (0,0,0)
  FaceMakerClass = Part::FaceMakerBullseye
  Placement = pos=(109.5,4.7,3.5) rot=(0,0,1;0rad)
  Solid = false
  Source = -> Face139
  Symmetric = false
FEATURE [Part::Feature] Face140
  shape: bbox 3.5 x 17.8 x 2e-07 mm, 1 faces, 0 solids (baked)
FEATURE [Part::Revolution] Revolve148  label="removeToCreateScrewAndThreadedInsertHole054"
  Angle = 360
  Axis = (0,1,0)
  Base = (0,0,0)
  FaceMakerClass = Part::FaceMakerBullseye
  Placement = pos=(109.5,4.7,68.5) rot=(0,0,1;0rad)
  Solid = false
  Source = -> Face140
  Symmetric = false
FEATURE [Part::MultiFuse] Fusion114  label="removeToCreateScrewAndThreadedInsertHole055"
  Shapes = -> [Revolve148,Revolve147,Revolve146,Revolve145,Revolve144,Revolve143]
FEATURE [Part::Cut] Cut047  label="casePillars004"
  Base = -> Cut037
  Tool = -> Fusion114
FEATURE [Part::Feature] Face141
  shape: bbox 3.5 x 17.8 x 2e-07 mm, 1 faces, 0 solids (baked)
FEATURE [Part::Feature] Face142
  shape: bbox 3.5 x 17.8 x 2e-07 mm, 1 faces, 0 solids (baked)
FEATURE [Part::Feature] Face143
  shape: bbox 3.5 x 17.8 x 2e-07 mm, 1 faces, 0 solids (baked)
FEATURE [Part::Revolution] Revolve149  label="removeToCreateScrewAndThreadedInsertHole057"
  Angle = 360
  Axis = (0,1,0)
  Base = (0,0,0)
  FaceMakerClass = Part::FaceMakerBullseye
  Placement = pos=(12.5,0,10) rot=(0,0,1;0rad)
  Solid = false
  Source = -> Face141
  Symmetric = false
FEATURE [Part::Feature] Face144
  shape: bbox 3.5 x 17.8 x 2e-07 mm, 1 faces, 0 solids (baked)
FEATURE [Part::Feature] Face145
  shape: bbox 3.5 x 17.8 x 2e-07 mm, 1 faces, 0 solids (baked)
FEATURE [Part::Feature] Face146
  shape: bbox 3.5 x 17.8 x 2e-07 mm, 1 faces, 0 solids (baked)
FEATURE [Part::Revolution] Revolve150  label="removeToCreateScrewAndThreadedInsertHole058"
  Angle = 360
  Axis = (0,1,0)
  Base = (0,0,0)
  FaceMakerClass = Part::FaceMakerBullseye
  Placement = pos=(12.5,0,62) rot=(0,0,1;0rad)
  Solid = false
  Source = -> Face146
  Symmetric = false
FEATURE [Part::Revolution] Revolve151  label="removeToCreateScrewAndThreadedInsertHole059"
  Angle = 360
  Axis = (0,1,0)
  Base = (0,0,0)
  FaceMakerClass = Part::FaceMakerBullseye
  Placement = pos=(89.5,0,68.5) rot=(0,0,1;0rad)
  Solid = false
  Source = -> Face143
  Symmetric = false
FEATURE [Part::Revolution] Revolve152  label="removeToCreateScrewAndThreadedInsertHole060"
  Angle = 360
  Axis = (0,1,0)
  Base = (0,0,0)
  FaceMakerClass = Part::FaceMakerBullseye
  Placement = pos=(89.5,0,3.5) rot=(0,0,1;0rad)
  Solid = false
  Source = -> Face142
  Symmetric = false
FEATURE [Part::Revolution] Revolve153  label="removeToCreateScrewAndThreadedInsertHole061"
  Angle = 360
  Axis = (0,1,0)
  Base = (0,0,0)
  FaceMakerClass = Part::FaceMakerBullseye
  Placement = pos=(109.5,4.7,3.5) rot=(0,0,1;0rad)
  Solid = false
  Source = -> Face145
  Symmetric = false
FEATURE [Part::Revolution] Revolve154  label="removeToCreateScrewAndThreadedInsertHole062"
  Angle = 360
  Axis = (0,1,0)
  Base = (0,0,0)
  FaceMakerClass = Part::FaceMakerBullseye
  Placement = pos=(109.5,4.7,68.5) rot=(0,0,1;0rad)
  Solid = false
  Source = -> Face144
  Symmetric = false
FEATURE [Part::MultiFuse] Fusion115  label="removeToCreateScrewAndThreadedInsertHole056"
  Shapes = -> [Revolve154,Revolve153,Revolve152,Revolve151,Revolve150,Revolve149]
FEATURE [Part::Feature] Face147
  shape: bbox 9.8 x 26.5 x 2e-07 mm, 1 faces, 0 solids (baked)
FEATURE [Part::Revolution] Revolve155
  Angle = 360
  Axis = (0,1,0)
  Base = (0,0,0)
  FaceMakerClass = Part::FaceMakerBullseye
  Placement = pos=(0,0,0) rot=(0,0,1;1.5708rad)
  Solid = false
  Source = -> Face147
  Symmetric = false
FEATURE [Part::Feature] Face148
  shape: bbox 9.8 x 26.5 x 2e-07 mm, 1 faces, 0 solids (baked)
FEATURE [Part::Revolution] Revolve156
  Angle = 360
  Axis = (0,1,0)
  Base = (0,0,0)
  FaceMakerClass = Part::FaceMakerBullseye
  Placement = pos=(0,0,0) rot=(0,0,1;1.5708rad)
  Solid = false
  Source = -> Face148
  Symmetric = false
FEATURE [Part::MultiFuse] Fusion116
  Placement = pos=(-18,19,36) rot=(0,0,1;0rad)
  Shapes = -> [Revolve156,Revolve155]
FEATURE [Part::Box] Box029  label="Cube016"
  AttacherType = Attacher::AttachEngine3D
  Height = 28
  Length = 3
  Placement = pos=(110.7,19,22) rot=(0,0,1;0rad)
  Width = 15.7
FEATURE [Part::Cylinder] Cylinder046
  Angle = 360
  AttacherType = Attacher::AttachEngine3D
  Height = 10
  Placement = pos=(0,0,36.15) rot=(0,0,1;0rad)
  Radius = 4
FEATURE [Part::Cylinder] Cylinder047
  Angle = 360
  AttacherType = Attacher::AttachEngine3D
  Height = 20
  Placement = pos=(0,0,36.15) rot=(0,0,1;0rad)
  Radius = 10.3
FEATURE [Part::MultiFuse] Fusion117  label="removeToCreteHoleForPlugHousing041"
  Placement = pos=(70,19,36) rot=(0,1,0;1.5708rad)
  Shapes = -> [Cylinder047,Cylinder046]
FEATURE [Part::Cut] Cut049  label="plugHousingTab004"
  Base = -> Box029
  Placement = pos=(-107.4,-14,0) rot=(0,0,1;0rad)
  Tool = -> Fusion117
FEATURE [Part::Box] Box030  label="Cube017"
  AttacherType = Attacher::AttachEngine3D
  Height = 28
  Length = 3
  Placement = pos=(110.7,19,22) rot=(0,0,1;0rad)
  Width = 15.7
FEATURE [Part::Cylinder] Cylinder048
  Angle = 360
  AttacherType = Attacher::AttachEngine3D
  Height = 10
  Placement = pos=(0,0,36.15) rot=(0,0,1;0rad)
  Radius = 4
FEATURE [Part::Cylinder] Cylinder049
  Angle = 360
  AttacherType = Attacher::AttachEngine3D
  Height = 20
  Placement = pos=(0,0,36.15) rot=(0,0,1;0rad)
  Radius = 10.3
FEATURE [Part::MultiFuse] Fusion118  label="removeToCreteHoleForPlugHousing042"
  Placement = pos=(70,19,36) rot=(0,1,0;1.5708rad)
  Shapes = -> [Cylinder049,Cylinder048]
FEATURE [Part::Cut] Cut050  label="plugHousingTab005"
  Base = -> Box030
  Placement = pos=(-107.4,-14,0) rot=(0,0,1;0rad)
  Tool = -> Fusion118
FEATURE [Part::MultiFuse] Fusion119
  Placement = pos=(9.6,23,0) rot=(0,0,1;3.14159rad)
  Shapes = -> [Cut049,Cut050]
FEATURE [Part::Box] Box031  label="Cube018"
  AttacherType = Attacher::AttachEngine3D
  Height = 10
  Length = 3
  Placement = pos=(3.3,4,12) rot=(0,0,1;0rad)
  Width = 10
FEATURE [Part::Fillet] Fillet044
  Base = -> Box031
  Edges = 1 edges r=2: [Edge11]
FEATURE [Part::Box] Box032  label="Cube019"
  AttacherType = Attacher::AttachEngine3D
  Height = 10
  Length = 3
  Placement = pos=(3.3,4,50) rot=(0,0,1;0rad)
  Width = 10
FEATURE [Part::Fillet] Fillet045
  Base = -> Box032
  Edges = 1 edges r=2: [Edge12]
FEATURE [Part::Box] Box033  label="Cube020"
  AttacherType = Attacher::AttachEngine3D
  Height = 28
  Length = 4
  Placement = pos=(5,0,22) rot=(0,0,1;0rad)
  Width = 10
FEATURE [Part::Fillet] Fillet046
  Base = -> Box033
  Edges = 1 edges r=1: [Edge7]
FEATURE [Part::Fillet] Fillet047
  Base = -> Fillet046
  Edges = 1 edges r=2: [Edge5]
FEATURE [Part::Fillet] Fillet048
  Base = -> Fillet047
  Edges = 1 edges r=2: [Edge2]
FEATURE [Part::Cylinder] Cylinder050
  Angle = 360
  AttacherType = Attacher::AttachEngine3D
  Height = 20
  Placement = pos=(0,0,36.15) rot=(0,0,1;0rad)
  Radius = 8.2
FEATURE [Part::Cylinder] Cylinder051
  Angle = 360
  AttacherType = Attacher::AttachEngine3D
  Height = 10
  Placement = pos=(0,0,36.15) rot=(0,0,1;0rad)
  Radius = 4
FEATURE [Part::MultiFuse] Fusion120  label="removeToCreteHoleForPlugHousing043"
  Placement = pos=(-42,19,36) rot=(0,1,0;1.5708rad)
  Shapes = -> [Cylinder050,Cylinder051]
FEATURE [Sketcher::SketchObject] Sketch067  label="topSketch018"
  FullyConstrained = true
  sketch-geometry (4):
    g0: LineSegment StartX=16.8446 StartY=31.512 StartZ=0 EndX=16.3251 EndY=34.4666 EndZ=0
    g1: ArcOfCircle CenterX=19 CenterY=19.2524 CenterZ=0 NormalX=0 NormalY=0 NormalZ=1 AngleXU=0 Radius=15.4476 StartAngle=1.74483 EndAngle=2.72717
    g2: ArcOfCircle CenterX=19 CenterY=19.2524 CenterZ=0 NormalX=0 NormalY=0 NormalZ=1 AngleXU=0 Radius=12.4476 StartAngle=1.74483 EndAngle=2.73189
    g3: LineSegment StartX=4.86004 StartY=25.4725 StartZ=0 EndX=7.58253 EndY=24.2107 EndZ=0
  constraints (7):
    c: Block(g0)
    c: Coincident(g1,g0)
    c: Coincident(g2,g0)
    c: Coincident(g3,g1)
    c: Coincident(g3,g2)
    c: Block(g1)
    c: Block(g2)
FEATURE [Part::Extrusion] Extrude058
  Base = -> Sketch067
  Dir = (0,0,1)
  DirMode = 2
  FaceMakerClass = Part::FaceMakerBullseye
  LengthFwd = 10
  LengthRev = 0
  Placement = pos=(0,0,31) rot=(0,0,1;0rad)
  Solid = true
  Symmetric = false
FEATURE [Part::Cut] Cut051
  Base = -> Extrude058
  Tool = -> Fusion120
FEATURE [Part::Fillet] Fillet049
  Base = -> Cut051
  Edges = 1 edges r=2: [Edge1]
FEATURE [Part::Fillet] Fillet050
  Base = -> Fillet049
  Edges = 1 edges r=2.5: [Edge1]
FEATURE [Part::Fillet] Fillet051
  Base = -> Fillet050
  Edges = 1 edges r=2.5: [Edge2]
FEATURE [Part::MultiFuse] Fusion121  label="wireHolder003"
  Shapes = -> [Fusion116,Fillet051]
FEATURE [Part::MultiFuse] Fusion122
  Shapes = -> [Fillet045,Fusion121]
FEATURE [Part::MultiFuse] Fusion123  label="wireHolder004"
  Shapes = -> [Fusion122,Fillet048]
FEATURE [Part::MultiFuse] Fusion124  label="wireHolder005"
  Shapes = -> [Fillet044,Fusion119,Fusion123]
FEATURE [Sketcher::SketchObject] Sketch068  label="topSketch019"
  FullyConstrained = true
  sketch-geometry (6):
    g0: LineSegment StartX=19 StartY=38 StartZ=0 EndX=117 EndY=38 EndZ=0
    g1: ArcOfCircle CenterX=19 CenterY=19 CenterZ=0 NormalX=0 NormalY=0 NormalZ=1 AngleXU=0 Radius=19 StartAngle=1.5708 EndAngle=3.14159
    g2: LineSegment StartX=117 StartY=38 StartZ=0 EndX=117 EndY=19 EndZ=0
    g3: LineSegment StartX=98 StartY=1.0161e-12 StartZ=0 EndX=5.22862e-06 EndY=1.0161e-12 EndZ=0
    g4: LineSegment StartX=5.22862e-06 StartY=19 StartZ=0 EndX=5.22862e-06 EndY=1.0161e-12 EndZ=0
    g5: ArcOfCircle CenterX=98 CenterY=19 CenterZ=0 NormalX=0 NormalY=0 NormalZ=1 AngleXU=0 Radius=19 StartAngle=4.71239 EndAngle=6.28319
  constraints (16):
    c: Horizontal(g0)
    c: Distance(g0) = 98
    c: Coincident(g1,g0)
    c: Block(g1)
    c: Coincident(g2,g0)
    c: Vertical(g2)
    c: Distance(g2) = 19
    c: Horizontal(g3)
    c: Coincident(g4,g1)
    c: Vertical(g4)
    c: Coincident(g3,g4)
    c: Block(g3)
    c: Coincident(g5,g2)
    c: Coincident(g5,g3)
    c: Block(g0)
    c: Block(g5)
FEATURE [Part::Extrusion] Extrude059  label="sideA002"
  Base = -> Sketch068
  Dir = (0,0,1)
  DirMode = 2
  FaceMakerClass = Part::FaceMakerBullseye
  LengthFwd = 3
  LengthRev = 0
  Placement = pos=(0,0,-2.7) rot=(0,0,1;0rad)
  Solid = true
  Symmetric = false
FEATURE [Sketcher::SketchObject] Sketch069  label="topSketch020"
  FullyConstrained = true
  sketch-geometry (6):
    g0: LineSegment StartX=19 StartY=38 StartZ=0 EndX=117 EndY=38 EndZ=0
    g1: ArcOfCircle CenterX=19 CenterY=19 CenterZ=0 NormalX=0 NormalY=0 NormalZ=1 AngleXU=0 Radius=19 StartAngle=1.5708 EndAngle=3.14159
    g2: LineSegment StartX=117 StartY=38 StartZ=0 EndX=117 EndY=19 EndZ=0
    g3: LineSegment StartX=98 StartY=1.0161e-12 StartZ=0 EndX=5.22862e-06 EndY=1.0161e-12 EndZ=0
    g4: LineSegment StartX=5.22862e-06 StartY=19 StartZ=0 EndX=5.22862e-06 EndY=1.0161e-12 EndZ=0
    g5: ArcOfCircle CenterX=98 CenterY=19 CenterZ=0 NormalX=0 NormalY=0 NormalZ=1 AngleXU=0 Radius=19 StartAngle=4.71239 EndAngle=6.28319
  constraints (16):
    c: Horizontal(g0)
    c: Distance(g0) = 98
    c: Coincident(g1,g0)
    c: Block(g1)
    c: Coincident(g2,g0)
    c: Vertical(g2)
    c: Distance(g2) = 19
    c: Horizontal(g3)
    c: Coincident(g4,g1)
    c: Vertical(g4)
    c: Coincident(g3,g4)
    c: Block(g3)
    c: Coincident(g5,g2)
    c: Coincident(g5,g3)
    c: Block(g0)
    c: Block(g5)
FEATURE [Part::Extrusion] Extrude060  label="sideB002"
  Base = -> Sketch069
  Dir = (0,0,1)
  DirMode = 2
  FaceMakerClass = Part::FaceMakerBullseye
  LengthFwd = 3
  LengthRev = 0
  Placement = pos=(0,0,71.7) rot=(0,0,1;0rad)
  Solid = true
  Symmetric = false
FEATURE [Part::MultiFuse] Fusion127  label="removeFromBottom001"
  Placement = pos=(2,0,0) rot=(0,0,1;0rad)
  Shapes = -> [Extrude059,Extrude060]
FEATURE [Part::Cylinder] Cylinder052
  Angle = 360
  AttacherType = Attacher::AttachEngine3D
  Height = 20
  Placement = pos=(0,0,36.15) rot=(0,0,1;0rad)
  Radius = 14
FEATURE [Part::Cylinder] Cylinder053
  Angle = 360
  AttacherType = Attacher::AttachEngine3D
  Height = 10
  Placement = pos=(0,0,36.15) rot=(0,0,1;0rad)
  Radius = 4
FEATURE [Part::MultiFuse] Fusion128  label="removeToCreteHoleForPlugHousing044"
  Placement = pos=(70,19,36) rot=(0,1,0;1.5708rad)
  Shapes = -> [Cylinder052,Cylinder053]
FEATURE [Part::Cut] Cut052  label="bottom011"
  Base = -> Extrude043
  Tool = -> Fusion128
FEATURE [Part::Cut] Cut054  label="bottom012"
  Base = -> Cut052
  Tool = -> Fusion115
FEATURE [Sketcher::SketchObject] Sketch070
  FullyConstrained = true
  Placement = pos=(117,19,0) rot=(0.57735,0.57735,0.57735;2.0944rad)
  sketch-geometry (48):
    g0: LineSegment StartX=-49.19 StartY=69.25 StartZ=0 EndX=-49.19 EndY=66.25 EndZ=0
    g1: LineSegment StartX=-49.19 StartY=63.5 StartZ=0 EndX=-49.19 EndY=60.5 EndZ=0
    g2: LineSegment StartX=-49.19 StartY=57.75 StartZ=0 EndX=-49.19 EndY=54.75 EndZ=0
    g3: LineSegment StartX=-49.19 StartY=52 StartZ=0 EndX=-49.19 EndY=49 EndZ=0
    g4: LineSegment StartX=-49.19 StartY=46.25 StartZ=0 EndX=-49.19 EndY=43.25 EndZ=0
    g5: LineSegment StartX=-49.19 StartY=40.5 StartZ=0 EndX=-49.19 EndY=37.5 EndZ=0
    g6: LineSegment StartX=-49.19 StartY=34.5 StartZ=0 EndX=-49.19 EndY=31.5 EndZ=0
    g7: LineSegment StartX=-49.19 StartY=28.75 StartZ=0 EndX=-49.19 EndY=25.75 EndZ=0
    g8: LineSegment StartX=-49.19 StartY=23 StartZ=0 EndX=-49.19 EndY=20 EndZ=0
    g9: LineSegment StartX=-49.19 StartY=17.25 StartZ=0 EndX=-49.19 EndY=14.25 EndZ=0
    g10: LineSegment StartX=-49.19 StartY=11.5 StartZ=0 EndX=-49.19 EndY=8.5 EndZ=0
    g11: LineSegment StartX=-49.19 StartY=5.75 StartZ=0 EndX=-49.19 EndY=2.75 EndZ=0
    g12: ArcOfCircle CenterX=-1.5 CenterY=67.75 CenterZ=0 NormalX=0 NormalY=0 NormalZ=1 AngleXU=0 Radius=1.5 StartAngle=4.71239 EndAngle=7.85398
    g13: ArcOfCircle CenterX=-1.5 CenterY=62 CenterZ=0 NormalX=0 NormalY=0 NormalZ=1 AngleXU=0 Radius=1.5 StartAngle=4.71239 EndAngle=7.85398
    g14: ArcOfCircle CenterX=-1.5 CenterY=56.25 CenterZ=0 NormalX=0 NormalY=0 NormalZ=1 AngleXU=0 Radius=1.5 StartAngle=4.71239 EndAngle=7.85398
    g15: ArcOfCircle CenterX=-11.49 CenterY=50.5 CenterZ=0 NormalX=0 NormalY=0 NormalZ=1 AngleXU=0 Radius=1.5 StartAngle=4.71239 EndAngle=7.85398
    g16: ArcOfCircle CenterX=-16.28 CenterY=44.75 CenterZ=0 NormalX=0 NormalY=0 NormalZ=1 AngleXU=0 Radius=1.5 StartAngle=4.71239 EndAngle=7.85398
    g17: ArcOfCircle CenterX=-18.2337 CenterY=39 CenterZ=0 NormalX=0 NormalY=0 NormalZ=1 AngleXU=0 Radius=1.5 StartAngle=4.71485 EndAngle=7.85398
    g18: ArcOfCircle CenterX=-16.2837 CenterY=27.25 CenterZ=0 NormalX=0 NormalY=0 NormalZ=1 AngleXU=0 Radius=1.5 StartAngle=4.71485 EndAngle=7.85398
    g19: ArcOfCircle CenterX=-18.2337 CenterY=33 CenterZ=0 NormalX=0 NormalY=0 NormalZ=1 AngleXU=0 Radius=1.5 StartAngle=4.71485 EndAngle=7.85398
    g20: ArcOfCircle CenterX=-11.49 CenterY=21.5 CenterZ=0 NormalX=0 NormalY=0 NormalZ=1 AngleXU=0 Radius=1.5 StartAngle=4.71239 EndAngle=7.85398
    g21: ArcOfCircle CenterX=-1.5 CenterY=4.25 CenterZ=0 NormalX=0 NormalY=0 NormalZ=1 AngleXU=0 Radius=1.5 StartAngle=4.71239 EndAngle=7.85398
    g22: ArcOfCircle CenterX=-1.5 CenterY=10 CenterZ=0 NormalX=0 NormalY=0 NormalZ=1 AngleXU=0 Radius=1.5 StartAngle=4.71239 EndAngle=7.85398
    g23: ArcOfCircle CenterX=-1.5 CenterY=15.75 CenterZ=0 NormalX=0 NormalY=0 NormalZ=1 AngleXU=0 Radius=1.5 StartAngle=4.71239 EndAngle=7.85398
    g24: LineSegment StartX=-49.19 StartY=69.25 StartZ=0 EndX=-1.5 EndY=69.25 EndZ=0
    g25: LineSegment StartX=-49.19 StartY=66.25 StartZ=0 EndX=-1.5 EndY=66.25 EndZ=0
    g26: LineSegment StartX=-49.19 StartY=63.5 StartZ=0 EndX=-1.5 EndY=63.5 EndZ=0
    g27: LineSegment StartX=-49.19 StartY=60.5 StartZ=0 EndX=-1.5 EndY=60.5 EndZ=0
    g28: LineSegment StartX=-49.19 StartY=57.75 StartZ=0 EndX=-1.5 EndY=57.75 EndZ=0
    g29: LineSegment StartX=-49.19 StartY=54.75 StartZ=0 EndX=-1.5 EndY=54.75 EndZ=0
    g30: LineSegment StartX=-49.19 StartY=52 StartZ=0 EndX=-11.49 EndY=52 EndZ=0
    g31: LineSegment StartX=-49.19 StartY=49 StartZ=0 EndX=-11.49 EndY=49 EndZ=0
    g32: LineSegment StartX=-49.19 StartY=46.25 StartZ=0 EndX=-16.28 EndY=46.25 EndZ=0
    g33: LineSegment StartX=-49.19 StartY=43.25 StartZ=0 EndX=-16.28 EndY=43.25 EndZ=0
    g34: LineSegment StartX=-49.19 StartY=40.5 StartZ=0 EndX=-18.2337 EndY=40.5 EndZ=0
    g35: LineSegment StartX=-49.19 StartY=37.5 StartZ=0 EndX=-18.23 EndY=37.5 EndZ=0
    g36: LineSegment StartX=-49.19 StartY=34.5 StartZ=0 EndX=-18.2337 EndY=34.5 EndZ=0
    g37: LineSegment StartX=-49.19 StartY=31.5 StartZ=0 EndX=-18.23 EndY=31.5 EndZ=0
    g38: LineSegment StartX=-49.19 StartY=28.75 StartZ=0 EndX=-16.2837 EndY=28.75 EndZ=0
    g39: LineSegment StartX=-49.19 StartY=25.75 StartZ=0 EndX=-16.28 EndY=25.75 EndZ=0
    g40: LineSegment StartX=-49.19 StartY=23 StartZ=0 EndX=-11.49 EndY=23 EndZ=0
    g41: LineSegment StartX=-49.19 StartY=20 StartZ=0 EndX=-11.49 EndY=20 EndZ=0
    g42: LineSegment StartX=-49.19 StartY=17.25 StartZ=0 EndX=-1.5 EndY=17.25 EndZ=0
    g43: LineSegment StartX=-49.19 StartY=14.25 StartZ=0 EndX=-1.5 EndY=14.25 EndZ=0
    g44: LineSegment StartX=-49.19 StartY=11.5 StartZ=0 EndX=-1.5 EndY=11.5 EndZ=0
    g45: LineSegment StartX=-49.19 StartY=8.5 StartZ=0 EndX=-1.5 EndY=8.5 EndZ=0
    g46: LineSegment StartX=-49.19 StartY=5.75 StartZ=0 EndX=-1.5 EndY=5.75 EndZ=0
    g47: LineSegment StartX=-49.19 StartY=2.75 StartZ=0 EndX=-1.5 EndY=2.75 EndZ=0
  constraints (120):
    c: Vertical(g0)
    c: Distance(g0) = 3
    c: Block(g0)
    c: Vertical(g1)
    c: Distance(g1) = 3
    c: Vertical(g2)
    c: Equal(g0,g2) = 3
    c: Block(g2)
    c: Vertical(g3)
    c: Equal(g1,g3) = 3
    c: Vertical(g4)
    c: Equal(g0,g4) = 3
    c: Block(g4)
    c: Vertical(g5)
    c: Equal(g1,g5) = 3
    c: Vertical(g6)
    c: Equal(g0,g6) = 3
    c: Block(g6)
    c: Vertical(g7)
    c: Equal(g1,g7) = 3
    c: Vertical(g8)
    c: Equal(g0,g8) = 3
    c: Block(g8)
    c: Vertical(g9)
    c: Equal(g1,g9) = 3
    c: Vertical(g10)
    c: Equal(g0,g10) = 3
    c: Block(g10)
    c: Vertical(g11)
    c: Equal(g1,g11) = 3
    c: Block(g12)
    c: Block(g13)
    c: Block(g14)
    c: Block(g15)
    c: Block(g16)
    c: Block(g17)
    c: Block(g18)
    c: Block(g19)
    c: Block(g20)
    c: Block(g21)
    c: Block(g22)
    c: Block(g23)
    c: Block(g11)
    c: Block(g9)
    c: Block(g7)
    c: Block(g5)
    c: Block(g3)
    c: Block(g1)
    c: Coincident(g24,g0)
    c: Coincident(g24,g12)
    c: Horizontal(g24)
    c: Coincident(g25,g0)
    c: Coincident(g25,g12)
    c: Horizontal(g25)
    c: Coincident(g26,g1)
    c: Coincident(g26,g13)
    c: Horizontal(g26)
    c: Coincident(g27,g1)
    c: Coincident(g27,g13)
    c: Horizontal(g27)
    c: Coincident(g28,g2)
    c: Coincident(g28,g14)
    c: Horizontal(g28)
    c: Coincident(g29,g2)
    c: Coincident(g29,g14)
    c: Horizontal(g29)
    c: Coincident(g30,g3)
    c: Coincident(g30,g15)
    c: Horizontal(g30)
    c: Coincident(g31,g3)
    c: Coincident(g31,g15)
    c: Horizontal(g31)
    c: Coincident(g32,g4)
    c: Coincident(g32,g16)
    c: Horizontal(g32)
    c: Coincident(g33,g4)
    c: Coincident(g33,g16)
    c: Horizontal(g33)
    c: Coincident(g34,g5)
    c: Coincident(g34,g17)
    c: Horizontal(g34)
    c: Coincident(g35,g5)
    c: Coincident(g35,g17)
    c: Horizontal(g35)
    c: Coincident(g36,g6)
    c: Coincident(g36,g19)
    c: Horizontal(g36)
    c: Coincident(g37,g6)
    c: Coincident(g37,g19)
    c: Horizontal(g37)
    c: Coincident(g38,g7)
    c: Coincident(g38,g18)
    c: Horizontal(g38)
    c: Coincident(g39,g7)
    c: Coincident(g39,g18)
    c: Horizontal(g39)
    c: Coincident(g40,g8)
    c: Coincident(g40,g20)
    c: Horizontal(g40)
    c: Coincident(g41,g8)
    c: Coincident(g41,g20)
    c: Horizontal(g41)
    c: Coincident(g42,g9)
    c: Coincident(g42,g23)
    c: Horizontal(g42)
    c: Coincident(g43,g9)
    c: Coincident(g43,g23)
    c: Horizontal(g43)
    c: Coincident(g44,g10)
    c: Coincident(g44,g22)
    c: Horizontal(g44)
    c: Coincident(g45,g10)
    c: Coincident(g45,g22)
    c: Horizontal(g45)
    c: Coincident(g46,g11)
    c: Coincident(g46,g21)
    c: Horizontal(g46)
    c: Coincident(g47,g11)
    c: Coincident(g47,g21)
    c: Horizontal(g47)
FEATURE [Part::Extrusion] Extrude061
  Base = -> Sketch070
  Dir = (1,0,0)
  DirMode = 2
  FaceMakerClass = Part::FaceMakerBullseye
  LengthFwd = 23
  LengthRev = 0
  Placement = pos=(-19,0,0) rot=(0,0,1;0rad)
  Solid = true
  Symmetric = false
FEATURE [Part::Fillet] Fillet052  label="removeToCreateVentalationHoles002"
  Base = -> Extrude061
  Edges = <same value as first occurrence — deduplicated (x6 in doc)>
  Placement = pos=(7,0.02,0) rot=(0,0,1;0rad)
FEATURE [Part::MultiFuse] Fusion130  label="bottom013"
  Shapes = -> [Cut054,Cut034]
FEATURE [Part::Cut] Cut055
  Base = -> Fusion130
  Tool = -> Fillet052
FEATURE [Part::Cylinder] Cylinder054
  Angle = 360
  AttacherType = Attacher::AttachEngine3D
  Height = 20
  Placement = pos=(0,0,36.15) rot=(0,0,1;0rad)
  Radius = 4
FEATURE [Sketcher::SketchObject] Sketch071  label="bottomSketch002"
  FullyConstrained = true
  sketch-geometry (32):
    g0: LineSegment StartX=3.3 StartY=-6.03275e-07 StartZ=0 EndX=98 EndY=-6.03275e-07 EndZ=0
    g1: ArcOfCircle CenterX=98 CenterY=19 CenterZ=0 NormalX=0 NormalY=0 NormalZ=1 AngleXU=0 Radius=19 StartAngle=4.71239 EndAngle=5.71103
    g2: LineSegment StartX=6.3 StartY=8 StartZ=0 EndX=3.3 EndY=8 EndZ=0
    g3: LineSegment StartX=3.3 StartY=8 StartZ=0 EndX=3.3 EndY=-6.03275e-07 EndZ=0
    g4: ArcOfCircle CenterX=8.3 CenterY=5 CenterZ=0 NormalX=0 NormalY=0 NormalZ=1 AngleXU=0 Radius=2 StartAngle=3.14159 EndAngle=4.71239
    g5: LineSegment StartX=6.3 StartY=8 StartZ=0 EndX=6.3 EndY=5 EndZ=0
    g6: ArcOfCircle CenterX=98 CenterY=19 CenterZ=0 NormalX=0 NormalY=0 NormalZ=1 AngleXU=0 Radius=12.7 StartAngle=4.71239 EndAngle=6.28319
    g7: LineSegment StartX=94.7 StartY=3 StartZ=0 EndX=8.3 EndY=3 EndZ=0
    g8-g12: Circle x5 (B-spline internal-alignment scaffolding for g13; pole/knot coordinates omitted)
    g13: BSplineCurve PolesCount=5 KnotsCount=3 Degree=3 IsPeriodic=0
    g14: GeomPoint X=98 Y=6.3 Z=0
    g15: GeomPoint X=96.3938 Y=4.71946 Z=0
    g16: GeomPoint X=94.7 Y=3 Z=0
    g17-g23: Circle x7 (B-spline internal-alignment scaffolding for g24; pole/knot coordinates omitted)
    g24: BSplineCurve PolesCount=7 KnotsCount=5 Degree=3 IsPeriodic=0
    g25-g29: GeomPoint x5 (B-spline internal-alignment scaffolding for g24; pole/knot coordinates omitted)
    g30: ArcOfCircle CenterX=98 CenterY=19 CenterZ=0 NormalX=0 NormalY=0 NormalZ=1 AngleXU=0 Radius=15.7 StartAngle=5.81226 EndAngle=6.28319
    g31: LineSegment StartX=110.7 StartY=19 StartZ=0 EndX=113.7 EndY=19 EndZ=0
  constraints (41):
    c: Horizontal(g0)
    c: Coincident(g1,g0)
    c: Block(g1)
    c: Horizontal(g2)
    c: Distance(g2) = 3
    c: Coincident(g3,g2)
    c: Vertical(g3)
    c: Coincident(g3,g0)
    c: Block(g4)
    c: Block(g2)
    c: Coincident(g5,g2)
    c: Coincident(g5,g4)
    c: Vertical(g5)
    c: Coincident(g6,g1)
    c: Block(g6)
    c: Coincident(g7,g4)
    c: Horizontal(g7)
    c: Block(g0)
    c: Block(g7)
    c: Block(g3)
    c: Coincident(g13,g6)
    c: Weight(g8) = 1
    c: Equal(g8, g9-g12) x4
    c: Coincident(g13,g7)
    c: InternalAlignment(g8-g12 -> g13) x5
    c: InternalAlignment(g14,g13)
    c: InternalAlignment(g15,g13)
    c: InternalAlignment(g16,g13)
    c: Block(g13)
    c: Weight(g17) = 1
    c: Equal(g17, g18-g23) x6
    c: Coincident(g24,g1)
    c: InternalAlignment(g17-g23 -> g24) x7
    c: InternalAlignment(g25-g29 -> g24) x5
    c: Block(g24)
    c: Coincident(g30,g24)
    c: Coincident(g31,g6)
    c: Coincident(g31,g30)
    c: Horizontal(g31)
    c: Block(g31)
    c: Block(g30)
FEATURE [Part::Extrusion] Extrude062  label="bottom014"
  Base = -> Sketch071
  Dir = (0,0,1)
  DirMode = 2
  FaceMakerClass = Part::FaceMakerBullseye
  LengthFwd = 71.4
  LengthRev = 0
  Placement = pos=(0,0,0.3) rot=(0,0,1;0rad)
  Solid = true
  Symmetric = false
FEATURE [Part::Fillet] Fillet054
  Base = -> Extrude062
  Edges = 1 edges r=2.4: [Edge17]
FEATURE [Part::Fillet] Fillet055  label="bottom015"
  Base = -> Fillet054
  Edges = 1 edges r=2.4: [Edge36]
FEATURE [Part::Cylinder] Cylinder055
  Angle = 360
  AttacherType = Attacher::AttachEngine3D
  Height = 10
  Placement = pos=(0,0,36.15) rot=(0,0,1;0rad)
  Radius = 4
FEATURE [Part::MultiFuse] Fusion131  label="removeToCreateHoleForPlugHousing002"
  Placement = pos=(70,19,36.15) rot=(0,1,0;1.5708rad)
  Shapes = -> [Cylinder054,Cylinder055]
FEATURE [Part::Cut] Cut056  label="Bottom001"
  Base = -> Fillet055
  Placement = pos=(9,0,0) rot=(0,0,1;0rad)
  Tool = -> Fusion131
FEATURE [Part::Cut] Cut057
  Base = -> Cut055
  Tool = -> Cut056
FEATURE [Sketcher::SketchObject] Sketch072  label="topSketch021"
  FullyConstrained = true
  sketch-geometry (4):
    g0: ArcOfCircle CenterX=105 CenterY=19 CenterZ=0 NormalX=0 NormalY=0 NormalZ=1 AngleXU=0 Radius=20.6155 StartAngle=5.54125 EndAngle=6.28319
    g1: ArcOfCircle CenterX=105 CenterY=19 CenterZ=0 NormalX=0 NormalY=0 NormalZ=1 AngleXU=0 Radius=13 StartAngle=5.54125 EndAngle=6.28319
    g2: LineSegment StartX=118 StartY=19 StartZ=0 EndX=125.616 EndY=19 EndZ=0
    g3: LineSegment StartX=114.583 StartY=10.2157 StartZ=0 EndX=120.197 EndY=5.06982 EndZ=0
  constraints (7):
    c: Block(g0)
    c: Block(g1)
    c: Coincident(g2,g1)
    c: Coincident(g2,g0)
    c: Horizontal(g2)
    c: Coincident(g3,g1)
    c: Coincident(g3,g0)
FEATURE [Part::Extrusion] Extrude063  label="bottomPlugHousingBit003"
  Base = -> Sketch072
  Dir = (0,0,1)
  DirMode = 2
  FaceMakerClass = Part::FaceMakerBullseye
  LengthFwd = 72
  LengthRev = 0
  Solid = true
  Symmetric = false
FEATURE [Part::Cylinder] Cylinder056
  Angle = 360
  AttacherType = Attacher::AttachEngine3D
  Height = 20
  Placement = pos=(0,0,36.15) rot=(0,0,1;0rad)
  Radius = 14.3
FEATURE [Part::Cylinder] Cylinder057
  Angle = 360
  AttacherType = Attacher::AttachEngine3D
  Height = 10
  Placement = pos=(0,0,36.15) rot=(0,0,1;0rad)
  Radius = 4
FEATURE [Part::Box] Box034  label="removeToCreteHoleForPlugHousing047"
  AttacherType = Attacher::AttachEngine3D
  Height = 28.6
  Length = 20
  Placement = pos=(106.15,0,21.7) rot=(0,0,1;0rad)
  Width = 19
FEATURE [Part::Cylinder] Cylinder058
  Angle = 360
  AttacherType = Attacher::AttachEngine3D
  Height = 20
  Placement = pos=(0,0,36.15) rot=(0,0,1;0rad)
  Radius = 14.3
FEATURE [Part::Cylinder] Cylinder059
  Angle = 360
  AttacherType = Attacher::AttachEngine3D
  Height = 10
  Placement = pos=(0,0,36.15) rot=(0,0,1;0rad)
  Radius = 4
FEATURE [Part::MultiFuse] Fusion134  label="removeToCreteHoleForPlugHousing046"
  Placement = pos=(70,19,36) rot=(0,1,0;1.5708rad)
  Shapes = -> [Cylinder058,Cylinder059]
FEATURE [Part::Cylinder] Cylinder060
  Angle = 360
  AttacherType = Attacher::AttachEngine3D
  Height = 20
  Placement = pos=(0,0,36.15) rot=(0,0,1;0rad)
  Radius = 14
FEATURE [Part::Cylinder] Cylinder061
  Angle = 360
  AttacherType = Attacher::AttachEngine3D
  Height = 10
  Placement = pos=(0,0,36.15) rot=(0,0,1;0rad)
  Radius = 4
FEATURE [Part::MultiFuse] Fusion135  label="removeToCreteHoleForPlugHousing048"
  Placement = pos=(70,19,36) rot=(0,1,0;1.5708rad)
  Shapes = -> [Cylinder060,Cylinder061]
FEATURE [Part::Box] Box035  label="removeToCreteHoleForPlugHousing049"
  AttacherType = Attacher::AttachEngine3D
  Height = 28.6
  Length = 20
  Placement = pos=(106.15,0,21.7) rot=(0,0,1;0rad)
  Width = 19
FEATURE [Part::MultiFuse] Fusion133  label="removeToCreteHoleForPlugHousing045"
  Placement = pos=(0,0,-28.3) rot=(0,0,1;0rad)
  Shapes = -> [Box035,Fusion134]
FEATURE [Part::MultiFuse] Fusion138  label="removeToCreteHoleForPlugHousing051"
  Placement = pos=(70,19,36) rot=(0,1,0;1.5708rad)
  Shapes = -> [Cylinder056,Cylinder057]
FEATURE [Part::MultiFuse] Fusion137  label="removeToCreteHoleForPlugHousing050"
  Placement = pos=(0,0,28.3) rot=(0,0,1;0rad)
  Shapes = -> [Box034,Fusion138]
FEATURE [Part::MultiFuse] Fusion132  label="removeToCreatePlugHousingBottomBit002"
  Shapes = -> [Fusion133,Fusion137]
FEATURE [Part::MultiFuse] Fusion136  label="removeToCreatePlugHousingBottomBit003"
  Shapes = -> [Fusion135,Fusion132]
FEATURE [Part::Cut] Cut058  label="bottomPlugHousingBit002"
  Base = -> Extrude063
  Placement = pos=(-0.09,0,0) rot=(0,0,1;0rad)
  Tool = -> Fusion136
FEATURE [Sketcher::SketchObject] Sketch073  label="bottomSketch003"
  FullyConstrained = true
  sketch-geometry (45):
    g0: LineSegment StartX=6.29999 StartY=8 StartZ=0 EndX=3.29999 EndY=8 EndZ=0
    g1: LineSegment StartX=3.29999 StartY=8 StartZ=0 EndX=3.29999 EndY=-6.03275e-07 EndZ=0
    g2: ArcOfCircle CenterX=8.29999 CenterY=5 CenterZ=0 NormalX=0 NormalY=0 NormalZ=1 AngleXU=0 Radius=2 StartAngle=3.14159 EndAngle=4.71239
    g3: LineSegment StartX=6.29999 StartY=8 StartZ=0 EndX=6.29999 EndY=5 EndZ=0
    g4: ArcOfCircle CenterX=105 CenterY=19 CenterZ=0 NormalX=0 NormalY=0 NormalZ=1 AngleXU=0 Radius=12.7 StartAngle=4.71239 EndAngle=5.94289
    g5-g11: Circle x7 (B-spline internal-alignment scaffolding for g12; pole/knot coordinates omitted)
    g12: BSplineCurve PolesCount=7 KnotsCount=5 Degree=3 IsPeriodic=0
    g13-g17: GeomPoint x5 (B-spline internal-alignment scaffolding for g12; pole/knot coordinates omitted)
    g18: ArcOfCircle CenterX=105 CenterY=19 CenterZ=0 NormalX=0 NormalY=0 NormalZ=1 AngleXU=0 Radius=15.7 StartAngle=5.81226 EndAngle=6.28319
    g19: BSplineCurve PolesCount=5 KnotsCount=3 Degree=3 IsPeriodic=0
    g20: LineSegment StartX=8.29999 StartY=3 StartZ=0 EndX=101.7 EndY=3 EndZ=0
    g21: LineSegment StartX=3.29999 StartY=-6.03275e-07 StartZ=0 EndX=105 EndY=-6.03275e-07 EndZ=0
    g22: LineSegment StartX=120.974 StartY=8.71251 StartZ=0 EndX=122.332 EndY=7.83778 EndZ=0
    g23: LineSegment StartX=105 StartY=-6.03274e-07 StartZ=0 EndX=113 EndY=-6.03274e-07 EndZ=0
    g24: ArcOfCircle CenterX=105 CenterY=19 CenterZ=0 NormalX=0 NormalY=0 NormalZ=1 AngleXU=0 Radius=20.6155 StartAngle=5.11091 EndAngle=5.71103
    g25: ArcOfCircle CenterX=117.7 CenterY=19 CenterZ=0 NormalX=0 NormalY=0 NormalZ=1 AngleXU=0 Radius=3 StartAngle=1.2e-15 EndAngle=2.10468
    g26: Circle CenterX=116.345 CenterY=16.3232 CenterZ=0 NormalX=0 NormalY=0 NormalZ=1 AngleXU=0 Radius=1
    g27: Circle CenterX=117.24 CenterY=15.7584 CenterZ=0 NormalX=0 NormalY=0 NormalZ=1 AngleXU=0 Radius=1
    g28: Circle CenterX=116.972 CenterY=14.7612 CenterZ=0 NormalX=0 NormalY=0 NormalZ=1 AngleXU=0 Radius=1
    g29: BSplineCurve PolesCount=3 KnotsCount=2 Degree=2 IsPeriodic=0
    g30: GeomPoint X=116.345 Y=16.3232 Z=0
    g31: GeomPoint X=116.972 Y=14.7612 Z=0
    g32: Circle CenterX=115.828 CenterY=17.157 CenterZ=0 NormalX=0 NormalY=0 NormalZ=1 AngleXU=0 Radius=1
    g33: Circle CenterX=115.841 CenterY=16.639 CenterZ=0 NormalX=0 NormalY=0 NormalZ=1 AngleXU=0 Radius=1
    g34: Circle CenterX=116.345 CenterY=16.3232 CenterZ=0 NormalX=0 NormalY=0 NormalZ=1 AngleXU=0 Radius=1
    g35: BSplineCurve PolesCount=3 KnotsCount=2 Degree=2 IsPeriodic=0
    g36: GeomPoint X=115.828 Y=17.157 Z=0
    g37: GeomPoint X=116.345 Y=16.3232 Z=0
    g38: LineSegment StartX=115.828 StartY=17.157 StartZ=0 EndX=115.828 EndY=20.8307 EndZ=0
    g39: Circle CenterX=115.828 CenterY=20.8307 CenterZ=0 NormalX=0 NormalY=0 NormalZ=1 AngleXU=0 Radius=1
    g40: Circle CenterX=115.831 CenterY=21.3396 CenterZ=0 NormalX=0 NormalY=0 NormalZ=1 AngleXU=0 Radius=1
    g41: Circle CenterX=116.173 CenterY=21.5825 CenterZ=0 NormalX=0 NormalY=0 NormalZ=1 AngleXU=0 Radius=1
    g42: BSplineCurve PolesCount=3 KnotsCount=2 Degree=2 IsPeriodic=0
    g43: GeomPoint X=115.828 Y=20.8307 Z=0
    g44: GeomPoint X=116.173 Y=21.5825 Z=0
  constraints (70):
    c: Horizontal(g0)
    c: Distance(g0) = 3
    c: Coincident(g1,g0)
    c: Vertical(g1)
    c: Block(g2)
    c: Block(g0)
    c: Coincident(g3,g0)
    c: Coincident(g3,g2)
    c: Vertical(g3)
    c: Block(g1)
    c: Block(g4)
    c: Coincident(g19,g4)
    c: Block(g19)
    c: Equal(g5, g6-g11) x6
    c: InternalAlignment(g5-g11 -> g12) x7
    c: InternalAlignment(g13-g17 -> g12) x5
    c: Block(g12)
    c: Coincident(g18,g12)
    c: Block(g18)
    c: Coincident(g20,g2)
    c: Coincident(g20,g19)
    c: Horizontal(g20)
    c: Distance(g20) = 93.4
    c: Coincident(g21,g1)
    c: Horizontal(g21)
    c: Distance(g21) = 101.7
    c: Horizontal(g23)
    c: Distance(g23) = 8
    c: Coincident(g24,g23)
    c: Block(g23)
    c: Coincident(g22,g24)
    c: Block(g24)
    c: Block(g22)
    c: Distance(g22) = 1.61553
    c: Coincident(g25,g18)
    c: Block(g25)
    c: Weight(g26) = 1
    c: Equal(g26,g27)
    c: Equal(g26,g28)
    c: Coincident(g29,g4)
    c: InternalAlignment(g26,g29)
    c: InternalAlignment(g27,g29)
    c: InternalAlignment(g28,g29)
    c: InternalAlignment(g30,g29)
    c: InternalAlignment(g31,g29)
    c: Block(g29)
    c: Weight(g32) = 1
    c: Equal(g32,g33)
    c: Equal(g32,g34)
    c: Coincident(g35,g29)
    c: InternalAlignment(g32,g35)
    c: InternalAlignment(g33,g35)
    c: InternalAlignment(g34,g35)
    c: InternalAlignment(g36,g35)
    c: InternalAlignment(g37,g35)
    c: Block(g35)
    c: Coincident(g38,g35)
    c: Vertical(g38)
    c: Block(g38)
    c: Coincident(g42,g38)
    c: Weight(g39) = 1
    c: Equal(g39,g40)
    c: Equal(g39,g41)
    c: Coincident(g42,g25)
    c: InternalAlignment(g39,g42)
    c: InternalAlignment(g40,g42)
    c: InternalAlignment(g41,g42)
    c: InternalAlignment(g43,g42)
    c: InternalAlignment(g44,g42)
    c: Block(g42)
FEATURE [Part::Extrusion] Extrude064  label="bottom016"
  Base = -> Sketch073
  Dir = (0,0,1)
  DirMode = 2
  FaceMakerClass = Part::FaceMakerBullseye
  LengthFwd = 71.4
  LengthRev = 0
  Placement = pos=(0,0,0.3) rot=(0,0,1;0rad)
  Solid = true
  Symmetric = false
FEATURE [Part::Revolution] Revolve157  label="removeToCreateScrewAndThreadedInsertHole063"
  Angle = 360
  Axis = (0,1,0)
  Base = (0,0,0)
  FaceMakerClass = Part::FaceMakerBullseye
  Placement = pos=(12.5,0,10) rot=(0,0,1;0rad)
  Solid = false
  Source = -> Face141
  Symmetric = false
FEATURE [Sketcher::SketchObject] Sketch074
  FullyConstrained = true
  Placement = pos=(117,19,0) rot=(0.57735,0.57735,0.57735;2.0944rad)
  sketch-geometry (48):
    g0: LineSegment StartX=-49.19 StartY=69.25 StartZ=0 EndX=-49.19 EndY=66.25 EndZ=0
    g1: LineSegment StartX=-49.19 StartY=63.5 StartZ=0 EndX=-49.19 EndY=60.5 EndZ=0
    g2: LineSegment StartX=-49.19 StartY=57.75 StartZ=0 EndX=-49.19 EndY=54.75 EndZ=0
    g3: LineSegment StartX=-49.19 StartY=52 StartZ=0 EndX=-49.19 EndY=49 EndZ=0
    g4: LineSegment StartX=-49.19 StartY=46.25 StartZ=0 EndX=-49.19 EndY=43.25 EndZ=0
    g5: LineSegment StartX=-49.19 StartY=40.5 StartZ=0 EndX=-49.19 EndY=37.5 EndZ=0
    g6: LineSegment StartX=-49.19 StartY=34.5 StartZ=0 EndX=-49.19 EndY=31.5 EndZ=0
    g7: LineSegment StartX=-49.19 StartY=28.75 StartZ=0 EndX=-49.19 EndY=25.75 EndZ=0
    g8: LineSegment StartX=-49.19 StartY=23 StartZ=0 EndX=-49.19 EndY=20 EndZ=0
    g9: LineSegment StartX=-49.19 StartY=17.25 StartZ=0 EndX=-49.19 EndY=14.25 EndZ=0
    g10: LineSegment StartX=-49.19 StartY=11.5 StartZ=0 EndX=-49.19 EndY=8.5 EndZ=0
    g11: LineSegment StartX=-49.19 StartY=5.75 StartZ=0 EndX=-49.19 EndY=2.75 EndZ=0
    g12: ArcOfCircle CenterX=-1.5 CenterY=67.75 CenterZ=0 NormalX=0 NormalY=0 NormalZ=1 AngleXU=0 Radius=1.5 StartAngle=4.71239 EndAngle=7.85398
    g13: ArcOfCircle CenterX=-1.5 CenterY=62 CenterZ=0 NormalX=0 NormalY=0 NormalZ=1 AngleXU=0 Radius=1.5 StartAngle=4.71239 EndAngle=7.85398
    g14: ArcOfCircle CenterX=-1.5 CenterY=56.25 CenterZ=0 NormalX=0 NormalY=0 NormalZ=1 AngleXU=0 Radius=1.5 StartAngle=4.71239 EndAngle=7.85398
    g15: ArcOfCircle CenterX=-11.49 CenterY=50.5 CenterZ=0 NormalX=0 NormalY=0 NormalZ=1 AngleXU=0 Radius=1.5 StartAngle=4.71239 EndAngle=7.85398
    g16: ArcOfCircle CenterX=-16.28 CenterY=44.75 CenterZ=0 NormalX=0 NormalY=0 NormalZ=1 AngleXU=0 Radius=1.5 StartAngle=4.71239 EndAngle=7.85398
    g17: ArcOfCircle CenterX=-18.2337 CenterY=39 CenterZ=0 NormalX=0 NormalY=0 NormalZ=1 AngleXU=0 Radius=1.5 StartAngle=4.71485 EndAngle=7.85398
    g18: ArcOfCircle CenterX=-16.2837 CenterY=27.25 CenterZ=0 NormalX=0 NormalY=0 NormalZ=1 AngleXU=0 Radius=1.5 StartAngle=4.71485 EndAngle=7.85398
    g19: ArcOfCircle CenterX=-18.2337 CenterY=33 CenterZ=0 NormalX=0 NormalY=0 NormalZ=1 AngleXU=0 Radius=1.5 StartAngle=4.71485 EndAngle=7.85398
    g20: ArcOfCircle CenterX=-11.49 CenterY=21.5 CenterZ=0 NormalX=0 NormalY=0 NormalZ=1 AngleXU=0 Radius=1.5 StartAngle=4.71239 EndAngle=7.85398
    g21: ArcOfCircle CenterX=-1.5 CenterY=4.25 CenterZ=0 NormalX=0 NormalY=0 NormalZ=1 AngleXU=0 Radius=1.5 StartAngle=4.71239 EndAngle=7.85398
    g22: ArcOfCircle CenterX=-1.5 CenterY=10 CenterZ=0 NormalX=0 NormalY=0 NormalZ=1 AngleXU=0 Radius=1.5 StartAngle=4.71239 EndAngle=7.85398
    g23: ArcOfCircle CenterX=-1.5 CenterY=15.75 CenterZ=0 NormalX=0 NormalY=0 NormalZ=1 AngleXU=0 Radius=1.5 StartAngle=4.71239 EndAngle=7.85398
    g24: LineSegment StartX=-49.19 StartY=69.25 StartZ=0 EndX=-1.5 EndY=69.25 EndZ=0
    g25: LineSegment StartX=-49.19 StartY=66.25 StartZ=0 EndX=-1.5 EndY=66.25 EndZ=0
    g26: LineSegment StartX=-49.19 StartY=63.5 StartZ=0 EndX=-1.5 EndY=63.5 EndZ=0
    g27: LineSegment StartX=-49.19 StartY=60.5 StartZ=0 EndX=-1.5 EndY=60.5 EndZ=0
    g28: LineSegment StartX=-49.19 StartY=57.75 StartZ=0 EndX=-1.5 EndY=57.75 EndZ=0
    g29: LineSegment StartX=-49.19 StartY=54.75 StartZ=0 EndX=-1.5 EndY=54.75 EndZ=0
    g30: LineSegment StartX=-49.19 StartY=52 StartZ=0 EndX=-11.49 EndY=52 EndZ=0
    g31: LineSegment StartX=-49.19 StartY=49 StartZ=0 EndX=-11.49 EndY=49 EndZ=0
    g32: LineSegment StartX=-49.19 StartY=46.25 StartZ=0 EndX=-16.28 EndY=46.25 EndZ=0
    g33: LineSegment StartX=-49.19 StartY=43.25 StartZ=0 EndX=-16.28 EndY=43.25 EndZ=0
    g34: LineSegment StartX=-49.19 StartY=40.5 StartZ=0 EndX=-18.2337 EndY=40.5 EndZ=0
    g35: LineSegment StartX=-49.19 StartY=37.5 StartZ=0 EndX=-18.23 EndY=37.5 EndZ=0
    g36: LineSegment StartX=-49.19 StartY=34.5 StartZ=0 EndX=-18.2337 EndY=34.5 EndZ=0
    g37: LineSegment StartX=-49.19 StartY=31.5 StartZ=0 EndX=-18.23 EndY=31.5 EndZ=0
    g38: LineSegment StartX=-49.19 StartY=28.75 StartZ=0 EndX=-16.2837 EndY=28.75 EndZ=0
    g39: LineSegment StartX=-49.19 StartY=25.75 StartZ=0 EndX=-16.28 EndY=25.75 EndZ=0
    g40: LineSegment StartX=-49.19 StartY=23 StartZ=0 EndX=-11.49 EndY=23 EndZ=0
    g41: LineSegment StartX=-49.19 StartY=20 StartZ=0 EndX=-11.49 EndY=20 EndZ=0
    g42: LineSegment StartX=-49.19 StartY=17.25 StartZ=0 EndX=-1.5 EndY=17.25 EndZ=0
    g43: LineSegment StartX=-49.19 StartY=14.25 StartZ=0 EndX=-1.5 EndY=14.25 EndZ=0
    g44: LineSegment StartX=-49.19 StartY=11.5 StartZ=0 EndX=-1.5 EndY=11.5 EndZ=0
    g45: LineSegment StartX=-49.19 StartY=8.5 StartZ=0 EndX=-1.5 EndY=8.5 EndZ=0
    g46: LineSegment StartX=-49.19 StartY=5.75 StartZ=0 EndX=-1.5 EndY=5.75 EndZ=0
    g47: LineSegment StartX=-49.19 StartY=2.75 StartZ=0 EndX=-1.5 EndY=2.75 EndZ=0
  constraints (120):
    c: Vertical(g0)
    c: Distance(g0) = 3
    c: Block(g0)
    c: Vertical(g1)
    c: Distance(g1) = 3
    c: Vertical(g2)
    c: Equal(g0,g2) = 3
    c: Block(g2)
    c: Vertical(g3)
    c: Equal(g1,g3) = 3
    c: Vertical(g4)
    c: Equal(g0,g4) = 3
    c: Block(g4)
    c: Vertical(g5)
    c: Equal(g1,g5) = 3
    c: Vertical(g6)
    c: Equal(g0,g6) = 3
    c: Block(g6)
    c: Vertical(g7)
    c: Equal(g1,g7) = 3
    c: Vertical(g8)
    c: Equal(g0,g8) = 3
    c: Block(g8)
    c: Vertical(g9)
    c: Equal(g1,g9) = 3
    c: Vertical(g10)
    c: Equal(g0,g10) = 3
    c: Block(g10)
    c: Vertical(g11)
    c: Equal(g1,g11) = 3
    c: Block(g12)
    c: Block(g13)
    c: Block(g14)
    c: Block(g15)
    c: Block(g16)
    c: Block(g17)
    c: Block(g18)
    c: Block(g19)
    c: Block(g20)
    c: Block(g21)
    c: Block(g22)
    c: Block(g23)
    c: Block(g11)
    c: Block(g9)
    c: Block(g7)
    c: Block(g5)
    c: Block(g3)
    c: Block(g1)
    c: Coincident(g24,g0)
    c: Coincident(g24,g12)
    c: Horizontal(g24)
    c: Coincident(g25,g0)
    c: Coincident(g25,g12)
    c: Horizontal(g25)
    c: Coincident(g26,g1)
    c: Coincident(g26,g13)
    c: Horizontal(g26)
    c: Coincident(g27,g1)
    c: Coincident(g27,g13)
    c: Horizontal(g27)
    c: Coincident(g28,g2)
    c: Coincident(g28,g14)
    c: Horizontal(g28)
    c: Coincident(g29,g2)
    c: Coincident(g29,g14)
    c: Horizontal(g29)
    c: Coincident(g30,g3)
    c: Coincident(g30,g15)
    c: Horizontal(g30)
    c: Coincident(g31,g3)
    c: Coincident(g31,g15)
    c: Horizontal(g31)
    c: Coincident(g32,g4)
    c: Coincident(g32,g16)
    c: Horizontal(g32)
    c: Coincident(g33,g4)
    c: Coincident(g33,g16)
    c: Horizontal(g33)
    c: Coincident(g34,g5)
    c: Coincident(g34,g17)
    c: Horizontal(g34)
    c: Coincident(g35,g5)
    c: Coincident(g35,g17)
    c: Horizontal(g35)
    c: Coincident(g36,g6)
    c: Coincident(g36,g19)
    c: Horizontal(g36)
    c: Coincident(g37,g6)
    c: Coincident(g37,g19)
    c: Horizontal(g37)
    c: Coincident(g38,g7)
    c: Coincident(g38,g18)
    c: Horizontal(g38)
    c: Coincident(g39,g7)
    c: Coincident(g39,g18)
    c: Horizontal(g39)
    c: Coincident(g40,g8)
    c: Coincident(g40,g20)
    c: Horizontal(g40)
    c: Coincident(g41,g8)
    c: Coincident(g41,g20)
    c: Horizontal(g41)
    c: Coincident(g42,g9)
    c: Coincident(g42,g23)
    c: Horizontal(g42)
    c: Coincident(g43,g9)
    c: Coincident(g43,g23)
    c: Horizontal(g43)
    c: Coincident(g44,g10)
    c: Coincident(g44,g22)
    c: Horizontal(g44)
    c: Coincident(g45,g10)
    c: Coincident(g45,g22)
    c: Horizontal(g45)
    c: Coincident(g46,g11)
    c: Coincident(g46,g21)
    c: Horizontal(g46)
    c: Coincident(g47,g11)
    c: Coincident(g47,g21)
    c: Horizontal(g47)
FEATURE [Part::Extrusion] Extrude065
  Base = -> Sketch074
  Dir = (1,0,0)
  DirMode = 2
  FaceMakerClass = Part::FaceMakerBullseye
  LengthFwd = 23
  LengthRev = 0
  Placement = pos=(-19,0,0) rot=(0,0,1;0rad)
  Solid = true
  Symmetric = false
FEATURE [Part::Fillet] Fillet056  label="removeToCreateVentalationHoles003"
  Base = -> Extrude065
  Edges = <same value as first occurrence — deduplicated (x6 in doc)>
  Placement = pos=(7,0.02,0) rot=(0,0,1;0rad)
FEATURE [Part::Revolution] Revolve158  label="removeToCreateScrewAndThreadedInsertHole065"
  Angle = 360
  Axis = (0,1,0)
  Base = (0,0,0)
  FaceMakerClass = Part::FaceMakerBullseye
  Placement = pos=(12.5,0,62) rot=(0,0,1;0rad)
  Solid = false
  Source = -> Face146
  Symmetric = false
FEATURE [Part::Revolution] Revolve159  label="removeToCreateScrewAndThreadedInsertHole066"
  Angle = 360
  Axis = (0,1,0)
  Base = (0,0,0)
  FaceMakerClass = Part::FaceMakerBullseye
  Placement = pos=(89.5,0,68.5) rot=(0,0,1;0rad)
  Solid = false
  Source = -> Face143
  Symmetric = false
FEATURE [Part::Revolution] Revolve160  label="removeToCreateScrewAndThreadedInsertHole067"
  Angle = 360
  Axis = (0,1,0)
  Base = (0,0,0)
  FaceMakerClass = Part::FaceMakerBullseye
  Placement = pos=(89.5,0,3.5) rot=(0,0,1;0rad)
  Solid = false
  Source = -> Face142
  Symmetric = false
FEATURE [Part::Revolution] Revolve161  label="removeToCreateScrewAndThreadedInsertHole068"
  Angle = 360
  Axis = (0,1,0)
  Base = (0,0,0)
  FaceMakerClass = Part::FaceMakerBullseye
  Placement = pos=(109.5,4.7,3.5) rot=(0,0,1;0rad)
  Solid = false
  Source = -> Face145
  Symmetric = false
FEATURE [Part::Revolution] Revolve162  label="removeToCreateScrewAndThreadedInsertHole069"
  Angle = 360
  Axis = (0,1,0)
  Base = (0,0,0)
  FaceMakerClass = Part::FaceMakerBullseye
  Placement = pos=(109.5,4.7,68.5) rot=(0,0,1;0rad)
  Solid = false
  Source = -> Face144
  Symmetric = false
FEATURE [Part::MultiFuse] Fusion141  label="removeToCreateScrewAndThreadedInsertHole064"
  Shapes = -> [Revolve162,Revolve161,Revolve160,Revolve159,Revolve158,Revolve157]
FEATURE [Part::Cylinder] Cylinder062
  Angle = 360
  AttacherType = Attacher::AttachEngine3D
  Height = 20
  Placement = pos=(0,0,36.15) rot=(0,0,1;0rad)
  Radius = 14
FEATURE [Part::Cylinder] Cylinder063
  Angle = 360
  AttacherType = Attacher::AttachEngine3D
  Height = 10
  Placement = pos=(0,0,36.15) rot=(0,0,1;0rad)
  Radius = 4
FEATURE [Part::MultiFuse] Fusion139  label="removeToCreteHoleForPlugHousing052"
  Placement = pos=(70,19,36) rot=(0,1,0;1.5708rad)
  Shapes = -> [Cylinder062,Cylinder063]
FEATURE [Part::Cut] Cut060  label="bottom017"
  Base = -> Extrude064
  Tool = -> Fusion139
FEATURE [Part::Cut] Cut061  label="bottom019"
  Base = -> Cut060
  Tool = -> Fusion141
FEATURE [Part::MultiFuse] Fusion140  label="bottom018"
  Shapes = -> [Cut061,Cut058]
FEATURE [Part::Cut] Cut059  label="bottom020"
  Base = -> Fusion140
  Tool = -> Fillet056
FEATURE [Part::Box] Box036  label="Cube021"
  AttacherType = Attacher::AttachEngine3D
  Height = 80
  Length = 26
  Placement = pos=(0,-1,-5) rot=(0,0,1;0rad)
  Width = 11
FEATURE [Part::Cut] Cut062  label="removeFromBottom002"
  Base = -> Cut057
  Tool = -> Box036
FEATURE [Part::Cut] Cut063
  Base = -> Cut059
  Tool = -> Cut062
FEATURE [Part::Cut] Cut064  label="pcbStands"
  Base = -> Fusion095
  Tool = -> Fusion127
FEATURE [Sketcher::SketchObject] Sketch075  label="topSketch022"
  FullyConstrained = true
  sketch-geometry (6):
    g0: LineSegment StartX=19 StartY=38 StartZ=0 EndX=117 EndY=38 EndZ=0
    g1: ArcOfCircle CenterX=19 CenterY=19 CenterZ=0 NormalX=0 NormalY=0 NormalZ=1 AngleXU=0 Radius=19 StartAngle=1.5708 EndAngle=3.14159
    g2: LineSegment StartX=117 StartY=38 StartZ=0 EndX=117 EndY=19 EndZ=0
    g3: LineSegment StartX=98 StartY=1.0161e-12 StartZ=0 EndX=5.22862e-06 EndY=1.0161e-12 EndZ=0
    g4: LineSegment StartX=5.22862e-06 StartY=19 StartZ=0 EndX=5.22862e-06 EndY=1.0161e-12 EndZ=0
    g5: ArcOfCircle CenterX=98 CenterY=19 CenterZ=0 NormalX=0 NormalY=0 NormalZ=1 AngleXU=0 Radius=19 StartAngle=4.71239 EndAngle=6.28319
  constraints (16):
    c: Horizontal(g0)
    c: Distance(g0) = 98
    c: Coincident(g1,g0)
    c: Block(g1)
    c: Coincident(g2,g0)
    c: Vertical(g2)
    c: Distance(g2) = 19
    c: Horizontal(g3)
    c: Coincident(g4,g1)
    c: Vertical(g4)
    c: Coincident(g3,g4)
    c: Block(g3)
    c: Coincident(g5,g2)
    c: Coincident(g5,g3)
    c: Block(g0)
    c: Block(g5)
FEATURE [Part::Extrusion] Extrude067  label="sideB003"
  Base = -> Sketch075
  Dir = (0,0,1)
  DirMode = 2
  FaceMakerClass = Part::FaceMakerBullseye
  LengthFwd = 3
  LengthRev = 0
  Placement = pos=(0,0,71.7) rot=(0,0,1;0rad)
  Solid = true
  Symmetric = false
FEATURE [Sketcher::SketchObject] Sketch076  label="topSketch023"
  FullyConstrained = true
  sketch-geometry (6):
    g0: LineSegment StartX=19 StartY=38 StartZ=0 EndX=117 EndY=38 EndZ=0
    g1: ArcOfCircle CenterX=19 CenterY=19 CenterZ=0 NormalX=0 NormalY=0 NormalZ=1 AngleXU=0 Radius=19 StartAngle=1.5708 EndAngle=3.14159
    g2: LineSegment StartX=117 StartY=38 StartZ=0 EndX=117 EndY=19 EndZ=0
    g3: LineSegment StartX=98 StartY=1.0161e-12 StartZ=0 EndX=5.22862e-06 EndY=1.0161e-12 EndZ=0
    g4: LineSegment StartX=5.22862e-06 StartY=19 StartZ=0 EndX=5.22862e-06 EndY=1.0161e-12 EndZ=0
    g5: ArcOfCircle CenterX=98 CenterY=19 CenterZ=0 NormalX=0 NormalY=0 NormalZ=1 AngleXU=0 Radius=19 StartAngle=4.71239 EndAngle=6.28319
  constraints (16):
    c: Horizontal(g0)
    c: Distance(g0) = 98
    c: Coincident(g1,g0)
    c: Block(g1)
    c: Coincident(g2,g0)
    c: Vertical(g2)
    c: Distance(g2) = 19
    c: Horizontal(g3)
    c: Coincident(g4,g1)
    c: Vertical(g4)
    c: Coincident(g3,g4)
    c: Block(g3)
    c: Coincident(g5,g2)
    c: Coincident(g5,g3)
    c: Block(g0)
    c: Block(g5)
FEATURE [Part::Extrusion] Extrude066  label="sideA003"
  Base = -> Sketch076
  Dir = (0,0,1)
  DirMode = 2
  FaceMakerClass = Part::FaceMakerBullseye
  LengthFwd = 3
  LengthRev = 0
  Placement = pos=(0,0,-2.7) rot=(0,0,1;0rad)
  Solid = true
  Symmetric = false
FEATURE [Part::MultiFuse] Fusion142  label="removeFromBottom003"
  Placement = pos=(2,0,0) rot=(0,0,1;0rad)
  Shapes = -> [Extrude066,Extrude067]
FEATURE [Part::Cut] Cut065  label="screwRetainers002"
  Base = -> Fusion096
  Tool = -> Fusion142
FEATURE [Sketcher::SketchObject] Sketch077
  FullyConstrained = true
  Placement = pos=(117,19,0) rot=(0.57735,0.57735,0.57735;2.0944rad)
  sketch-geometry (8):
    g0: LineSegment StartX=-49.19 StartY=63.5 StartZ=0 EndX=-49.19 EndY=60.5 EndZ=0
    g1: LineSegment StartX=-49.19 StartY=11.5 StartZ=0 EndX=-49.19 EndY=8.5 EndZ=0
    g2: ArcOfCircle CenterX=-1.5 CenterY=62 CenterZ=0 NormalX=0 NormalY=0 NormalZ=1 AngleXU=0 Radius=1.5 StartAngle=4.71239 EndAngle=7.85398
    g3: ArcOfCircle CenterX=-1.5 CenterY=10 CenterZ=0 NormalX=0 NormalY=0 NormalZ=1 AngleXU=0 Radius=1.5 StartAngle=4.71239 EndAngle=7.85398
    g4: LineSegment StartX=-49.19 StartY=63.5 StartZ=0 EndX=-1.5 EndY=63.5 EndZ=0
    g5: LineSegment StartX=-49.19 StartY=60.5 StartZ=0 EndX=-1.5 EndY=60.5 EndZ=0
    g6: LineSegment StartX=-49.19 StartY=11.5 StartZ=0 EndX=-1.5 EndY=11.5 EndZ=0
    g7: LineSegment StartX=-49.19 StartY=8.5 StartZ=0 EndX=-1.5 EndY=8.5 EndZ=0
  constraints (19):
    c: Vertical(g0)
    c: Distance(g0) = 3
    c: Vertical(g1)
    c: Block(g1)
    c: Block(g2)
    c: Block(g3)
    c: Block(g0)
    c: Coincident(g4,g0)
    c: Coincident(g4,g2)
    c: Horizontal(g4)
    c: Coincident(g5,g0)
    c: Coincident(g5,g2)
    c: Horizontal(g5)
    c: Coincident(g6,g1)
    c: Coincident(g6,g3)
    c: Horizontal(g6)
    c: Coincident(g7,g1)
    c: Coincident(g7,g3)
    c: Horizontal(g7)
FEATURE [Part::Extrusion] Extrude068
  Base = -> Sketch077
  Dir = (1,0,0)
  DirMode = 2
  FaceMakerClass = Part::FaceMakerBullseye
  LengthFwd = 10
  LengthRev = 0
  Solid = true
  Symmetric = false
FEATURE [Part::Fillet] Fillet057  label="removeFromtMoreFrontCaseScrewRetainers002"
  Base = -> Extrude068
  Edges = 4 edges r=1.49: [Edge6,Edge11,Edge18,Edge23]
  Placement = pos=(-12,0,0) rot=(0,0,1;0rad)
FEATURE [Sketcher::SketchObject] Sketch078
  FullyConstrained = true
  Placement = pos=(117,19,0) rot=(0.57735,0.57735,0.57735;2.0944rad)
  sketch-geometry (8):
    g0: LineSegment StartX=-49.19 StartY=69.25 StartZ=0 EndX=-49.19 EndY=66.25 EndZ=0
    g1: LineSegment StartX=-49.19 StartY=5.75 StartZ=0 EndX=-49.19 EndY=2.75 EndZ=0
    g2: ArcOfCircle CenterX=-1.5 CenterY=67.75 CenterZ=0 NormalX=0 NormalY=0 NormalZ=1 AngleXU=0 Radius=1.5 StartAngle=4.71239 EndAngle=7.85398
    g3: ArcOfCircle CenterX=-1.5 CenterY=4.25 CenterZ=0 NormalX=0 NormalY=0 NormalZ=1 AngleXU=0 Radius=1.5 StartAngle=4.71239 EndAngle=7.85398
    g4: LineSegment StartX=-49.19 StartY=69.25 StartZ=0 EndX=-1.5 EndY=69.25 EndZ=0
    g5: LineSegment StartX=-49.19 StartY=66.25 StartZ=0 EndX=-1.5 EndY=66.25 EndZ=0
    g6: LineSegment StartX=-49.19 StartY=5.75 StartZ=0 EndX=-1.5 EndY=5.75 EndZ=0
    g7: LineSegment StartX=-49.19 StartY=2.75 StartZ=0 EndX=-1.5 EndY=2.75 EndZ=0
  constraints (19):
    c: Vertical(g0)
    c: Distance(g0) = 3
    c: Block(g0)
    c: Vertical(g1)
    c: Block(g2)
    c: Block(g3)
    c: Block(g1)
    c: Coincident(g4,g0)
    c: Coincident(g4,g2)
    c: Horizontal(g4)
    c: Coincident(g5,g0)
    c: Coincident(g5,g2)
    c: Horizontal(g5)
    c: Coincident(g6,g1)
    c: Coincident(g6,g3)
    c: Horizontal(g6)
    c: Coincident(g7,g1)
    c: Coincident(g7,g3)
    c: Horizontal(g7)
FEATURE [Part::Extrusion] Extrude069
  Base = -> Sketch078
  Dir = (1,0,0)
  DirMode = 2
  FaceMakerClass = Part::FaceMakerBullseye
  LengthFwd = 10
  LengthRev = 0
  Solid = true
  Symmetric = false
FEATURE [Part::Fillet] Fillet058  label="removeFromtMoreFrontCaseScrewRetainers003"
  Base = -> Extrude069
  Edges = 4 edges r=1.49: [Edge6,Edge11,Edge18,Edge23]
  Placement = pos=(-4,0,0) rot=(0,0,1;0rad)
FEATURE [Part::Cut] Cut066
  Base = -> Cut065
  Tool = -> Fillet058
FEATURE [Part::Cut] Cut067  label="screwPillars"
  Base = -> Cut066
  Tool = -> Fillet057
FEATURE [Part::MultiFuse] Fusion143  label="bottom021"
  Shapes = -> [Cut031,Cut063]
FEATURE [Part::Cylinder] Cylinder
  Angle = 360
  AttacherType = Attacher::AttachEngine3D
  Height = 10
  Placement = pos=(20.65,12,4.68) rot=(1,0,0;1.5708rad)
  Radius = 2
FEATURE [Part::Cylinder] Cylinder064
  Angle = 360
  AttacherType = Attacher::AttachEngine3D
  Height = 10
  Placement = pos=(20.65,12,67.38) rot=(1,0,0;1.5708rad)
  Radius = 2
FEATURE [Part::Cylinder] Cylinder065
  Angle = 360
  AttacherType = Attacher::AttachEngine3D
  Height = 10
  Placement = pos=(77.15,12,67.38) rot=(1,0,0;1.5708rad)
  Radius = 2
FEATURE [Part::Cylinder] Cylinder066
  Angle = 360
  AttacherType = Attacher::AttachEngine3D
  Height = 10
  Placement = pos=(77.15,12,4.68) rot=(1,0,0;1.5708rad)
  Radius = 2
FEATURE [Part::MultiFuse] Fusion144  label="removeFromThreadedInsertHousing"
  Shapes = -> [Cylinder065,Cylinder064,Cylinder,Cylinder066]
FEATURE [Part::Cut] Cut068  label="pcbStands001"
  Base = -> Cut064
  Tool = -> Fusion144
FEATURE [Part::MultiFuse] Fusion145
  Shapes = -> [Cut068,Fusion143]
FEATURE [Part::MultiFuse] Fusion146
  Shapes = -> [Fusion145]
FEATURE [Part::MultiFuse] Fusion147  label="bottom022"
  Shapes = -> [Cut067,Fusion146]
FEATURE [Part::MultiFuse] Fusion148  label="casePillars005"
  Shapes = -> [Cut047,Fusion092]
FEATURE [Part::MultiFuse] Fusion149  label="bottom023"
  Shapes = -> [Fusion124,Fusion113,Fusion147]
FEATURE [Part::MultiFuse] Fusion150  label="topBits"
  Shapes = -> [Cut025,Fusion148,Cut030,Fillet034]
FEATURE [Part::Feature] Face149 .. Face152  x4 (patterned run collapsed; names and placements below)
  shape: bbox 3.2 x 1.5 x 2e-07 mm, 1 faces, 0 solids (baked)
FEATURE [Part::Feature] Face153
  shape: bbox 3.6 x 3.2 x 2e-07 mm, 1 faces, 0 solids (baked)
FEATURE [Part::Feature] Face154
  shape: bbox 3.6 x 3.2 x 2e-07 mm, 1 faces, 0 solids (baked)
FEATURE [Sketcher::SketchObject] Sketch079  label="topSketch024"
  FullyConstrained = true
  sketch-geometry (6):
    g0: LineSegment StartX=19 StartY=38 StartZ=0 EndX=117 EndY=38 EndZ=0
    g1: ArcOfCircle CenterX=19 CenterY=19 CenterZ=0 NormalX=0 NormalY=0 NormalZ=1 AngleXU=0 Radius=19 StartAngle=1.5708 EndAngle=3.14159
    g2: LineSegment StartX=117 StartY=38 StartZ=0 EndX=117 EndY=19 EndZ=0
    g3: LineSegment StartX=98 StartY=1.0161e-12 StartZ=0 EndX=5.22862e-06 EndY=1.0161e-12 EndZ=0
    g4: LineSegment StartX=5.22862e-06 StartY=19 StartZ=0 EndX=5.22862e-06 EndY=1.0161e-12 EndZ=0
    g5: ArcOfCircle CenterX=98 CenterY=19 CenterZ=0 NormalX=0 NormalY=0 NormalZ=1 AngleXU=0 Radius=19 StartAngle=4.71239 EndAngle=6.28319
  constraints (16):
    c: Horizontal(g0)
    c: Distance(g0) = 98
    c: Coincident(g1,g0)
    c: Block(g1)
    c: Coincident(g2,g0)
    c: Vertical(g2)
    c: Distance(g2) = 19
    c: Horizontal(g3)
    c: Coincident(g4,g1)
    c: Vertical(g4)
    c: Coincident(g3,g4)
    c: Block(g3)
    c: Coincident(g5,g2)
    c: Coincident(g5,g3)
    c: Block(g0)
    c: Block(g5)
FEATURE [Sketcher::SketchObject] Sketch080  label="topSketch025"
  FullyConstrained = true
  sketch-geometry (6):
    g0: LineSegment StartX=19 StartY=38 StartZ=0 EndX=117 EndY=38 EndZ=0
    g1: ArcOfCircle CenterX=19 CenterY=19 CenterZ=0 NormalX=0 NormalY=0 NormalZ=1 AngleXU=0 Radius=19 StartAngle=1.5708 EndAngle=3.14159
    g2: LineSegment StartX=117 StartY=38 StartZ=0 EndX=117 EndY=19 EndZ=0
    g3: LineSegment StartX=98 StartY=1.0161e-12 StartZ=0 EndX=5.22862e-06 EndY=1.0161e-12 EndZ=0
    g4: LineSegment StartX=5.22862e-06 StartY=19 StartZ=0 EndX=5.22862e-06 EndY=1.0161e-12 EndZ=0
    g5: ArcOfCircle CenterX=98 CenterY=19 CenterZ=0 NormalX=0 NormalY=0 NormalZ=1 AngleXU=0 Radius=19 StartAngle=4.71239 EndAngle=6.28319
  constraints (16):
    c: Horizontal(g0)
    c: Distance(g0) = 98
    c: Coincident(g1,g0)
    c: Block(g1)
    c: Coincident(g2,g0)
    c: Vertical(g2)
    c: Distance(g2) = 19
    c: Horizontal(g3)
    c: Coincident(g4,g1)
    c: Vertical(g4)
    c: Coincident(g3,g4)
    c: Block(g3)
    c: Coincident(g5,g2)
    c: Coincident(g5,g3)
    c: Block(g0)
    c: Block(g5)
FEATURE [Part::Extrusion] Extrude070  label="sideA004"
  Base = -> Sketch080
  Dir = (0,0,1)
  DirMode = 2
  FaceMakerClass = Part::FaceMakerBullseye
  LengthFwd = 3
  LengthRev = 0
  Placement = pos=(0,0,-2.7) rot=(0,0,1;0rad)
  Solid = true
  Symmetric = false
FEATURE [Sketcher::SketchObject] Sketch081
  FullyConstrained = true
  Placement = pos=(117,19,0) rot=(0.57735,0.57735,0.57735;2.0944rad)
  sketch-geometry (8):
    g0: LineSegment StartX=-49.19 StartY=63.5 StartZ=0 EndX=-49.19 EndY=60.5 EndZ=0
    g1: LineSegment StartX=-49.19 StartY=11.5 StartZ=0 EndX=-49.19 EndY=8.5 EndZ=0
    g2: ArcOfCircle CenterX=-1.5 CenterY=62 CenterZ=0 NormalX=0 NormalY=0 NormalZ=1 AngleXU=0 Radius=1.5 StartAngle=4.71239 EndAngle=7.85398
    g3: ArcOfCircle CenterX=-1.5 CenterY=10 CenterZ=0 NormalX=0 NormalY=0 NormalZ=1 AngleXU=0 Radius=1.5 StartAngle=4.71239 EndAngle=7.85398
    g4: LineSegment StartX=-49.19 StartY=63.5 StartZ=0 EndX=-1.5 EndY=63.5 EndZ=0
    g5: LineSegment StartX=-49.19 StartY=60.5 StartZ=0 EndX=-1.5 EndY=60.5 EndZ=0
    g6: LineSegment StartX=-49.19 StartY=11.5 StartZ=0 EndX=-1.5 EndY=11.5 EndZ=0
    g7: LineSegment StartX=-49.19 StartY=8.5 StartZ=0 EndX=-1.5 EndY=8.5 EndZ=0
  constraints (19):
    c: Vertical(g0)
    c: Distance(g0) = 3
    c: Vertical(g1)
    c: Block(g1)
    c: Block(g2)
    c: Block(g3)
    c: Block(g0)
    c: Coincident(g4,g0)
    c: Coincident(g4,g2)
    c: Horizontal(g4)
    c: Coincident(g5,g0)
    c: Coincident(g5,g2)
    c: Horizontal(g5)
    c: Coincident(g6,g1)
    c: Coincident(g6,g3)
    c: Horizontal(g6)
    c: Coincident(g7,g1)
    c: Coincident(g7,g3)
    c: Horizontal(g7)
FEATURE [Part::Extrusion] Extrude071  label="sideB004"
  Base = -> Sketch079
  Dir = (0,0,1)
  DirMode = 2
  FaceMakerClass = Part::FaceMakerBullseye
  LengthFwd = 3
  LengthRev = 0
  Placement = pos=(0,0,71.7) rot=(0,0,1;0rad)
  Solid = true
  Symmetric = false
FEATURE [Part::MultiFuse] Fusion152  label="removeFromBottom004"
  Placement = pos=(2,0,0) rot=(0,0,1;0rad)
  Shapes = -> [Extrude070,Extrude071]
FEATURE [Part::Extrusion] Extrude072
  Base = -> Sketch081
  Dir = (1,0,0)
  DirMode = 2
  FaceMakerClass = Part::FaceMakerBullseye
  LengthFwd = 10
  LengthRev = 0
  Solid = true
  Symmetric = false
FEATURE [Part::Fillet] Fillet059  label="removeFromtMoreFrontCaseScrewRetainers004"
  Base = -> Extrude072
  Edges = 4 edges r=1.49: [Edge6,Edge11,Edge18,Edge23]
  Placement = pos=(-12,0,0) rot=(0,0,1;0rad)
FEATURE [Sketcher::SketchObject] Sketch082
  FullyConstrained = true
  Placement = pos=(117,19,0) rot=(0.57735,0.57735,0.57735;2.0944rad)
  sketch-geometry (8):
    g0: LineSegment StartX=-49.19 StartY=69.25 StartZ=0 EndX=-49.19 EndY=66.25 EndZ=0
    g1: LineSegment StartX=-49.19 StartY=5.75 StartZ=0 EndX=-49.19 EndY=2.75 EndZ=0
    g2: ArcOfCircle CenterX=-1.5 CenterY=67.75 CenterZ=0 NormalX=0 NormalY=0 NormalZ=1 AngleXU=0 Radius=1.5 StartAngle=4.71239 EndAngle=7.85398
    g3: ArcOfCircle CenterX=-1.5 CenterY=4.25 CenterZ=0 NormalX=0 NormalY=0 NormalZ=1 AngleXU=0 Radius=1.5 StartAngle=4.71239 EndAngle=7.85398
    g4: LineSegment StartX=-49.19 StartY=69.25 StartZ=0 EndX=-1.5 EndY=69.25 EndZ=0
    g5: LineSegment StartX=-49.19 StartY=66.25 StartZ=0 EndX=-1.5 EndY=66.25 EndZ=0
    g6: LineSegment StartX=-49.19 StartY=5.75 StartZ=0 EndX=-1.5 EndY=5.75 EndZ=0
    g7: LineSegment StartX=-49.19 StartY=2.75 StartZ=0 EndX=-1.5 EndY=2.75 EndZ=0
  constraints (19):
    c: Vertical(g0)
    c: Distance(g0) = 3
    c: Block(g0)
    c: Vertical(g1)
    c: Block(g2)
    c: Block(g3)
    c: Block(g1)
    c: Coincident(g4,g0)
    c: Coincident(g4,g2)
    c: Horizontal(g4)
    c: Coincident(g5,g0)
    c: Coincident(g5,g2)
    c: Horizontal(g5)
    c: Coincident(g6,g1)
    c: Coincident(g6,g3)
    c: Horizontal(g6)
    c: Coincident(g7,g1)
    c: Coincident(g7,g3)
    c: Horizontal(g7)
FEATURE [Part::Extrusion] Extrude073
  Base = -> Sketch082
  Dir = (1,0,0)
  DirMode = 2
  FaceMakerClass = Part::FaceMakerBullseye
  LengthFwd = 10
  LengthRev = 0
  Solid = true
  Symmetric = false
FEATURE [Part::Fillet] Fillet060  label="removeFromtMoreFrontCaseScrewRetainers005"
  Base = -> Extrude073
  Edges = 4 edges r=1.49: [Edge6,Edge11,Edge18,Edge23]
  Placement = pos=(-4,0,0) rot=(0,0,1;0rad)
FEATURE [Part::Revolution] Revolve163  label="backCaseScrewRetainer004"
  Angle = 360
  Axis = (0,1,0)
  Base = (0,0,0)
  FaceMakerClass = Part::FaceMakerBullseye
  Placement = pos=(12.5,3,62) rot=(0,0,1;0rad)
  Solid = false
  Source = -> Face149
  Symmetric = false
FEATURE [Part::Revolution] Revolve164  label="frontCaseScrewRetainer006"
  Angle = 360
  Axis = (0,1,0)
  Base = (0,0,0)
  FaceMakerClass = Part::FaceMakerBullseye
  Placement = pos=(89.5,3,68.5) rot=(0,0,1;0rad)
  Solid = false
  Source = -> Face151
  Symmetric = false
FEATURE [Part::Revolution] Revolve165  label="frontCaseScrewRetainer007"
  Angle = 360
  Axis = (0,1,0)
  Base = (0,0,0)
  FaceMakerClass = Part::FaceMakerBullseye
  Placement = pos=(89.5,3,3.5) rot=(0,0,1;0rad)
  Solid = false
  Source = -> Face152
  Symmetric = false
FEATURE [Part::Revolution] Revolve166  label="backCaseScrewRetainer005"
  Angle = 360
  Axis = (0,1,0)
  Base = (0,0,0)
  FaceMakerClass = Part::FaceMakerBullseye
  Placement = pos=(12.5,3,10) rot=(0,0,1;0rad)
  Solid = false
  Source = -> Face150
  Symmetric = false
FEATURE [Part::Revolution] Revolve167  label="moreFrontCaseScrewRetainer006"
  Angle = 360
  Axis = (0,1,0)
  Base = (0,0,0)
  FaceMakerClass = Part::FaceMakerBullseye
  Placement = pos=(109.5,4.5,68.5) rot=(0,0,1;0rad)
  Solid = false
  Source = -> Face153
  Symmetric = false
FEATURE [Part::Revolution] Revolve168  label="moreFrontCaseScrewRetainer007"
  Angle = 360
  Axis = (0,1,0)
  Base = (0,0,0)
  FaceMakerClass = Part::FaceMakerBullseye
  Placement = pos=(109.5,4.5,3.5) rot=(0,0,1;0rad)
  Solid = false
  Source = -> Face154
  Symmetric = false
FEATURE [Part::MultiFuse] Fusion151  label="screwRetainers003"
  Shapes = -> [Revolve168,Revolve167,Revolve166,Revolve165,Revolve164,Revolve163]
FEATURE [Part::Cut] Cut069  label="screwRetainers004"
  Base = -> Fusion151
  Tool = -> Fusion152
FEATURE [Part::Cut] Cut070
  Base = -> Cut069
  Tool = -> Fillet060
FEATURE [Part::Cut] Cut071  label="screwPillars001"
  Base = -> Cut070
  Tool = -> Fillet059
FEATURE [Part::MultiFuse] Fusion153  label="bottom024"
  Shapes = -> [Fusion149,Cut071]
FEATURE [Part::Cylinder] Cylinder067
  Angle = 360
  AttacherType = Attacher::AttachEngine3D
  Height = 10
  Placement = pos=(20.65,12,4.68) rot=(1,0,0;1.5708rad)
  Radius = 2
FEATURE [Part::Cylinder] Cylinder068
  Angle = 360
  AttacherType = Attacher::AttachEngine3D
  Height = 10
  Placement = pos=(20.65,12,67.38) rot=(1,0,0;1.5708rad)
  Radius = 2
FEATURE [Part::Cylinder] Cylinder069
  Angle = 360
  AttacherType = Attacher::AttachEngine3D
  Height = 10
  Placement = pos=(77.15,12,67.38) rot=(1,0,0;1.5708rad)
  Radius = 2
FEATURE [Part::Cylinder] Cylinder070
  Angle = 360
  AttacherType = Attacher::AttachEngine3D
  Height = 10
  Placement = pos=(77.15,12,4.68) rot=(1,0,0;1.5708rad)
  Radius = 2
FEATURE [Part::MultiFuse] Fusion154  label="removeFromThreadedInsertHousing001"
  Shapes = -> [Cylinder069,Cylinder068,Cylinder067,Cylinder070]
FEATURE [Part::Cut] Cut072  label="bottom025"
  Base = -> Fusion153
  Tool = -> Fusion154
FEATURE [Image::ImagePlane] ImagePlane
  XSize = 339
  YSize = 72
FEATURE [Sketcher::SketchObject] Sketch083
  FullyConstrained = false
  MapMode = 5
  Support = -> [XY_Plane]
  sketch-geometry (34):
    g0: LineSegment StartX=-151.619 StartY=28.8932 StartZ=0 EndX=-140.819 EndY=28.8932 EndZ=0
    g1: LineSegment StartX=-145.128 StartY=24.0313 StartZ=0 EndX=-151.619 EndY=24.0313 EndZ=0
    g2: LineSegment StartX=-151.619 StartY=24.0313 StartZ=0 EndX=-151.619 EndY=28.8932 EndZ=0
    g3: LineSegment StartX=-140.819 StartY=17.7713 StartZ=0 EndX=-151.619 EndY=17.7713 EndZ=0
    g4: LineSegment StartX=-151.619 StartY=17.7713 StartZ=0 EndX=-151.619 EndY=22.6313 EndZ=0
    g5: LineSegment StartX=-151.619 StartY=22.6313 StartZ=0 EndX=-145.128 EndY=22.6313 EndZ=0
    g6: LineSegment StartX=-145.128 StartY=24.0313 StartZ=0 EndX=-140.819 EndY=28.8932 EndZ=0
    g7: LineSegment StartX=-145.128 StartY=22.6313 StartZ=0 EndX=-140.819 EndY=17.7713 EndZ=0
    g8: ArcOfCircle CenterX=-155.157 CenterY=23.3323 CenterZ=0 NormalX=0 NormalY=0 NormalZ=1 AngleXU=0 Radius=6.92354 StartAngle=1.03434 EndAngle=5.24885
    g9: ArcOfCircle CenterX=-155.157 CenterY=23.3323 CenterZ=0 NormalX=0 NormalY=0 NormalZ=1 AngleXU=0 Radius=12.6269 StartAngle=1.28675 EndAngle=4.99643
    g10: LineSegment StartX=-151.619 StartY=35.4532 StartZ=0 EndX=-151.619 EndY=29.2832 EndZ=0
    g11: LineSegment StartX=-151.619 StartY=17.3813 StartZ=0 EndX=-151.619 EndY=11.2113 EndZ=0
    g12-g22: Circle x11 (B-spline internal-alignment scaffolding for g23; pole/knot coordinates omitted)
    g23: BSplineCurve PolesCount=11 KnotsCount=9 Degree=3 IsPeriodic=0
    g24-g32: GeomPoint x9 (B-spline internal-alignment scaffolding for g23; pole/knot coordinates omitted)
    g33: LineSegment StartX=-117.124 StartY=30.093 StartZ=0 EndX=-117.124 EndY=14.2659 EndZ=0
  constraints (34):
    c: Coincident(g1,g2)
    c: Coincident(g2,g0)
    c: Horizontal(g0)
    c: Horizontal(g1)
    c: Vertical(g2)
    c: Coincident(g3,g4)
    c: Coincident(g4,g5)
    c: Horizontal(g5)
    c: Horizontal(g3)
    c: Vertical(g4)
    c: Block(g2)
    c: Block(g1)
    c: Distance(g4) = 4.86
    c: Block(g5)
    c: Distance(g0) = 10.8
    c: Distance(g3) = 10.8
    c: Coincident(g6,g1)
    c: Coincident(g6,g0)
    c: Coincident(g7,g5)
    c: Coincident(g7,g3)
    c: Block(g9)
    c: Block(g8)
    c: Coincident(g10,g9)
    c: Coincident(g10,g8)
    c: Vertical(g10)
    c: Coincident(g11,g8)
    c: Coincident(g11,g9)
    c: Vertical(g11)
    c: Weight(g12) = 1
    c: Equal(g12, g13-g22) x10
    c: InternalAlignment(g12-g22 -> g23) x11
    c: InternalAlignment(g24-g32 -> g23) x9
    c: Vertical(g33)
    c: Block(g23)
FEATURE [PartDesign::Body] Body
  Group = -> [Sketch083]
  Origin = -> Origin
FEATURE [Sketcher::SketchObject] Sketch084
  FullyConstrained = true
  MapMode = 5
  Support = -> [XY_Plane001]
FEATURE [PartDesign::Body] Body001
  Group = -> [Sketch084]
  Origin = -> Origin001
